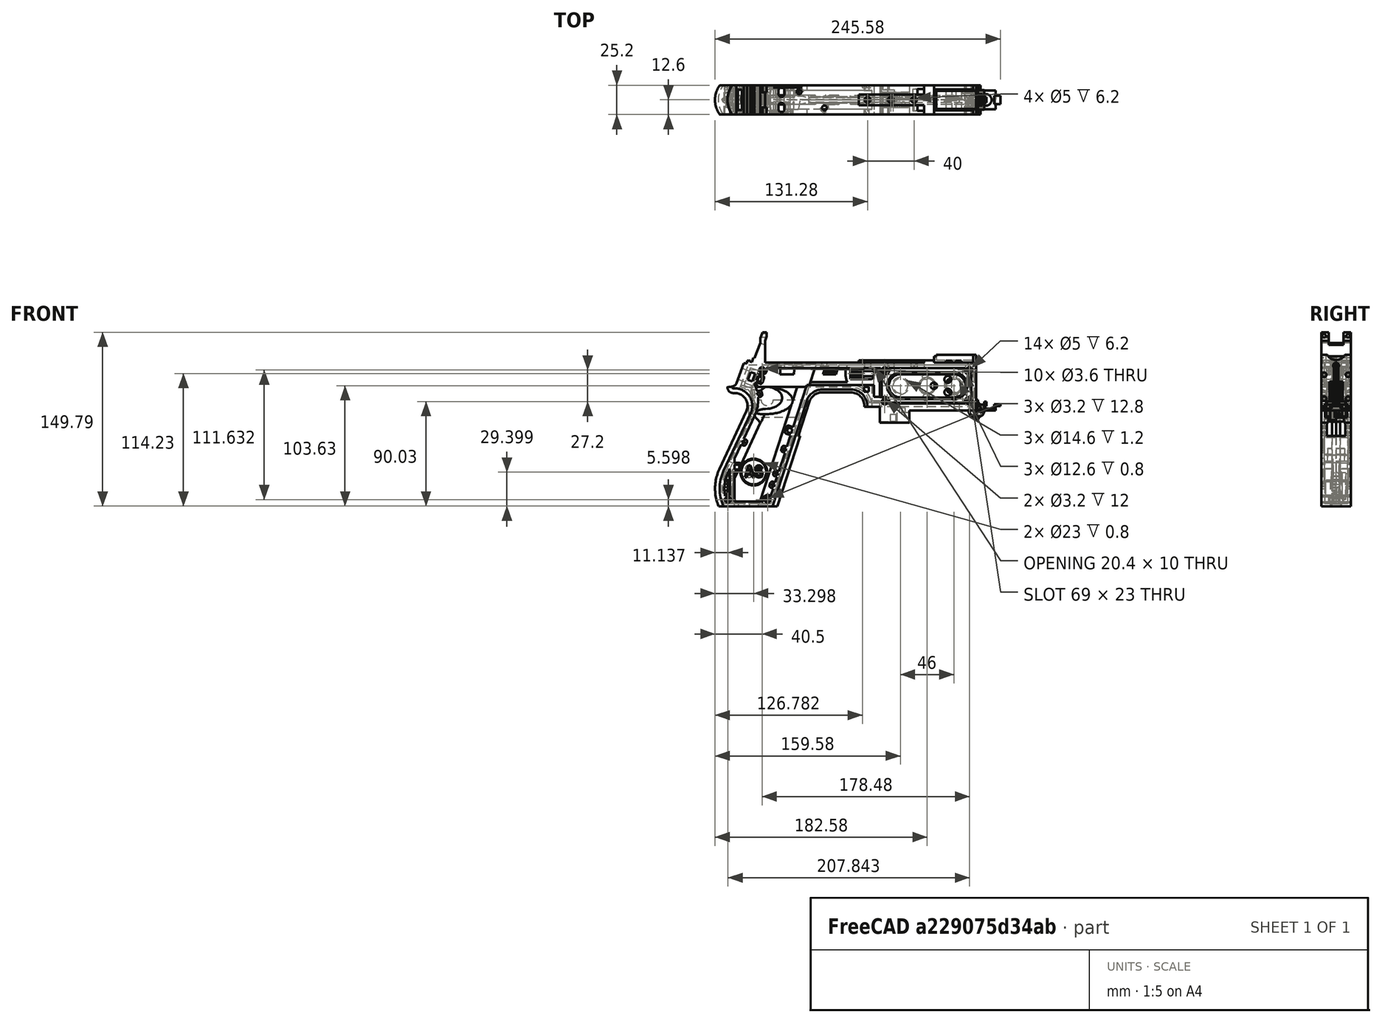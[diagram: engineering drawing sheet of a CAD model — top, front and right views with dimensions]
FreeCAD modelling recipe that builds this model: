
FCSTD DOCUMENT  (FreeCAD 1.0R39319 (Git))
Label: PICON-OF_ver_61
License: All rights reserved
LicenseURL: https://en.wikipedia.org/wiki/All_rights_reserved
objects: Sketcher::SketchObject×132, Part::Extrusion×66, Part::Cut×51, PartDesign::Pad×34, PartDesign::Pocket×21, PartDesign::Chamfer×15, PartDesign::Body×11, PartDesign::Fillet×6, Part::MultiFuse×5, Part::Part2DObjectPython×4, PartDesign::SubtractivePipe×4, PartDesign::SubtractiveLoft×4, PartDesign::Plane×3, PartDesign::SubShapeBinder×2, Part::Sweep×1, PartDesign::ShapeBinder×1, Mesh::Feature×1, PartDesign::Point×1, PartDesign::Groove×1
note: 664 computed .brp shape members not serialized (recipe doc carries the construction recipe); baked Part::Feature solids carry a one-line shape summary decoded from their .brp

FEATURE [Sketcher::SketchObject] Sketch  label="corpo principale"
  ArcFitTolerance = 1e-06
  AttacherType = Attacher::AttachEngine3D
  AttachmentSupport = -> [XZ_Plane]
  FullyConstrained = true
  MakeInternals = false
  MapMode = 5
  Placement = pos=(0,0,0) rot=(1,0,0;1.5708rad)
  sketch-geometry (65):
    g0: LineSegment StartX=0 StartY=0 StartZ=0 EndX=-57.2 EndY=0 EndZ=0
    g1: LineSegment StartX=-57.2 StartY=0 StartZ=0 EndX=-57.2 EndY=-10.4 EndZ=0
    g2: LineSegment StartX=-57.2 StartY=-10.4 StartZ=0 EndX=-82.8 EndY=-10.4 EndZ=0
    g3: LineSegment StartX=-82.8 StartY=-10.4 StartZ=0 EndX=-82.8 EndY=3.2 EndZ=0
    g4: LineSegment StartX=-82.8 StartY=3.2 StartZ=0 EndX=-93.6 EndY=3.2 EndZ=0
    g5: LineSegment StartX=-93.6 StartY=3.2 StartZ=0 EndX=-93.6 EndY=4 EndZ=0
    g6: LineSegment StartX=-107.6 StartY=18 StartZ=0 EndX=-132.428 EndY=18 EndZ=0
    g7: LineSegment StartX=-145.743 StartY=8.32624 StartZ=0 EndX=-175.232 EndY=-82.4316 EndZ=0
    g8: LineSegment StartX=-175.232 StartY=-82.4316 StartZ=0 EndX=-217.232 EndY=-82.4316 EndZ=0
    g9: LineSegment StartX=-217.232 StartY=-52.1862 StartZ=0 EndX=-193.988 EndY=-2.33927 EndZ=0
    g10: LineSegment StartX=-206.196 StartY=23.0857 StartZ=0 EndX=-199.861 EndY=40.4914 EndZ=0
    g11: LineSegment StartX=-199.861 StartY=40.4914 StartZ=0 EndX=-197.061 EndY=40.4914 EndZ=0
    g12: LineSegment StartX=-197.061 StartY=40.4914 StartZ=0 EndX=-197.061 EndY=42.8914 EndZ=0
    g13: LineSegment StartX=-197.061 StartY=42.8914 StartZ=0 EndX=-194.261 EndY=42.8914 EndZ=0
    g14: LineSegment StartX=-194.261 StartY=42.8914 StartZ=0 EndX=-194.535 EndY=42.1397 EndZ=0
    g15: LineSegment StartX=-194.535 StartY=42.1397 StartZ=0 EndX=-193.031 EndY=41.5924 EndZ=0
    g16: LineSegment StartX=-193.031 StartY=41.5924 StartZ=0 EndX=-191.663 EndY=45.3512 EndZ=0
    g17: LineSegment StartX=-191.663 StartY=45.3512 StartZ=0 EndX=-190.536 EndY=44.9408 EndZ=0
    g18: LineSegment StartX=-190.536 StartY=44.9408 StartZ=0 EndX=-185.747 EndY=58.0965 EndZ=0
    g19: LineSegment StartX=-185.747 StartY=58.0965 StartZ=0 EndX=-185.747 EndY=62.0965 EndZ=0
    g20: LineSegment StartX=-185.747 StartY=62.0965 StartZ=0 EndX=-183.832 EndY=67.3588 EndZ=0
    g21: LineSegment StartX=-183.832 StartY=67.3588 StartZ=0 EndX=-180.232 EndY=67.3588 EndZ=0
    g22: LineSegment StartX=-180.232 StartY=67.3588 StartZ=0 EndX=-180.232 EndY=63.7588 EndZ=0
    g23: LineSegment StartX=-180.232 StartY=63.7588 StartZ=0 EndX=-181.6 EndY=60 EndZ=0
    g24: LineSegment StartX=-181.6 StartY=60 StartZ=0 EndX=-181.6 EndY=41.2 EndZ=0
    g25: LineSegment StartX=-181.6 StartY=41.2 StartZ=0 EndX=-100.8 EndY=41.2 EndZ=0
    g26: LineSegment StartX=-36 StartY=43.2 StartZ=0 EndX=-36 EndY=41.2 EndZ=0
    g27: LineSegment StartX=0 StartY=48 StartZ=0 EndX=0 EndY=0 EndZ=0
    g28: LineSegment StartX=-209.901 StartY=19.85 StartZ=0 EndX=-209.901 EndY=20.1 EndZ=0
    g29: LineSegment StartX=-208.001 StartY=22 StartZ=0 EndX=-207.747 EndY=22 EndZ=0
    g30: LineSegment StartX=-207.583 StartY=19 StartZ=0 EndX=-209.051 EndY=19 EndZ=0
    g31: ArcOfCircle CenterX=-208.001 CenterY=20.1 CenterZ=0 NormalX=0 NormalY=0 NormalZ=1 AngleXU=0 Radius=1.9 StartAngle=1.5708 EndAngle=3.14159
    g32: GeomPoint [constr] X=-209.901 Y=22 Z=0
    g33: ArcOfCircle CenterX=-209.051 CenterY=19.85 CenterZ=0 NormalX=0 NormalY=0 NormalZ=1 AngleXU=0 Radius=0.85 StartAngle=3.14159 EndAngle=4.71239
    g34: GeomPoint [constr] X=-209.901 Y=19 Z=0
    g35: ArcOfCircle CenterX=-207.747 CenterY=23.65 CenterZ=0 NormalX=0 NormalY=0 NormalZ=1 AngleXU=0 Radius=1.65 StartAngle=4.71239 EndAngle=5.93412
    g36: GeomPoint [constr] X=-206.591 Y=22 Z=0
    g37: LineSegment StartX=-4 StartY=6 StartZ=0 EndX=-4 EndY=36.4 EndZ=0
    g38: LineSegment StartX=-4 StartY=36.4 StartZ=0 EndX=-185.2 EndY=36.4 EndZ=0
    g39: LineSegment StartX=-185.2 StartY=36.4 StartZ=0 EndX=-190.441 EndY=22 EndZ=0
    g40: LineSegment StartX=-214.575 StartY=-78.4316 StartZ=0 EndX=-178.142 EndY=-78.4316 EndZ=0
    g41: LineSegment StartX=-178.142 StartY=-78.4316 StartZ=0 EndX=-145.51 EndY=22 EndZ=0
    g42: LineSegment StartX=-145.51 StartY=22 StartZ=0 EndX=-87.91 EndY=22 EndZ=0
    g43: LineSegment StartX=-87.91 StartY=22 StartZ=0 EndX=-87.91 EndY=11.6 EndZ=0
    g44: LineSegment StartX=-87.91 StartY=11.6 StartZ=0 EndX=-80.11 EndY=11.6 EndZ=0
    g45: LineSegment StartX=-80.11 StartY=11.6 StartZ=0 EndX=-80.11 EndY=6 EndZ=0
    g46: LineSegment StartX=-80.11 StartY=6 StartZ=0 EndX=-4 EndY=6 EndZ=0
    g47: LineSegment StartX=-190.363 StartY=-4.02975 StartZ=0 EndX=-213.607 EndY=-53.8767 EndZ=0
    g48: ArcOfCircle CenterX=-132.428 CenterY=4 CenterZ=0 NormalX=0 NormalY=0 NormalZ=1 AngleXU=0 Radius=14 StartAngle=1.5708 EndAngle=2.82743
    g49: GeomPoint [constr] X=-142.6 Y=18 Z=0
    g50: ArcOfCircle CenterX=-107.6 CenterY=4 CenterZ=0 NormalX=0 NormalY=0 NormalZ=1 AngleXU=0 Radius=14 StartAngle=0 EndAngle=1.5708
    g51: GeomPoint [constr] X=-93.6 Y=18 Z=0
    g52: ArcOfCircle CenterX=-184.801 CenterY=-67.3089 CenterZ=0 NormalX=0 NormalY=0 NormalZ=1 AngleXU=0 Radius=35.7833 StartAngle=2.70526 EndAngle=3.57792
    g53: ArcOfCircle CenterX=-207.583 CenterY=4 CenterZ=0 NormalX=0 NormalY=0 NormalZ=1 AngleXU=0 Radius=15 StartAngle=5.84685 EndAngle=7.85398
    g54: LineSegment [constr] StartX=-213.607 StartY=-53.8767 StartZ=0 EndX=-217.232 EndY=-52.1862 EndZ=0
    g55: ArcOfCircle CenterX=-184.801 CenterY=-67.3089 CenterZ=0 NormalX=0 NormalY=0 NormalZ=1 AngleXU=0 Radius=31.7833 StartAngle=2.70526 EndAngle=3.49911
    g56: ArcOfCircle CenterX=-218.095 CenterY=8.90192 CenterZ=0 NormalX=0 NormalY=0 NormalZ=1 AngleXU=0 Radius=30.5989 StartAngle=5.84685 EndAngle=6.72553
    g57: LineSegment StartX=-44.6 StartY=43.2 StartZ=0 EndX=-36 EndY=43.2 EndZ=0
    g58: LineSegment StartX=-100.8 StartY=41.2 StartZ=0 EndX=-44.6 EndY=41.2 EndZ=0
    g59: LineSegment StartX=-44.6 StartY=41.2 StartZ=0 EndX=-44.6 EndY=43.2 EndZ=0
    g60: LineSegment StartX=-2.4 StartY=48 StartZ=0 EndX=0 EndY=48 EndZ=0
    g61: LineSegment StartX=-36 StartY=41.2 StartZ=0 EndX=-2.4 EndY=41.2 EndZ=0
    g62: LineSegment StartX=-2.4 StartY=41.2 StartZ=0 EndX=-2.4 EndY=48 EndZ=0
    g63: LineSegment [constr] StartX=-181.6 StartY=36.4 StartZ=0 EndX=-152.209 EndY=36.4 EndZ=0
    g64: LineSegment [constr] StartX=-181.6 StartY=36.4 StartZ=0 EndX=-130.41 EndY=36.4 EndZ=0
  constraints (183):
    c: Coincident(g-1,g0)
    c: PointOnObject(g0,g-1)
    c: Coincident(g0,g1)
    c: Vertical(g1)
    c: Coincident(g1,g2)
    c: Horizontal(g2)
    c: Coincident(g2,g3)
    c: Vertical(g3)
    c: Coincident(g3,g4)
    c: Coincident(g4,g5)
    c: Vertical(g5)
    c: Horizontal(g6)
    c: Coincident(g7,g8)
    c: Horizontal(g8)
    c: Coincident(g10,g11)
    c: Horizontal(g11)
    c: Coincident(g11,g12)
    c: Vertical(g12)
    c: Coincident(g12,g13)
    c: Horizontal(g13)
    c: Coincident(g13,g14)
    c: Coincident(g14,g15)
    c: Coincident(g15,g16)
    c: Coincident(g16,g17)
    c: Coincident(g17,g18)
    c: Coincident(g18,g19)
    c: Vertical(g19)
    c: Coincident(g19,g20)
    c: Coincident(g20,g21)
    c: Horizontal(g21)
    c: Coincident(g21,g22)
    c: Vertical(g22)
    c: Coincident(g22,g23)
    c: Coincident(g23,g24)
    c: Vertical(g24)
    c: Coincident(g24,g25)
    c: Horizontal(g25)
    c: Coincident(g57,g26)
    c: Vertical(g26)
    c: Coincident(g26,g61)
    c: PointOnObject(g60,g-2)
    c: Coincident(g60,g27)
    c: Coincident(g27,g0)
    c: DistanceY(g27,g27) = 48
    c: DistanceY(g1,g1) = 10.4
    c: DistanceX(g0,g0) = 57.2
    c: DistanceX(g2,g2) = 25.6
    c: Horizontal(g4)
    c: DistanceY(g3,g3) = 13.6
    c: DistanceX(g4,g4) = 10.8
    c: DistanceY(g5,g51) = 14.8
    c: DistanceX(g49,g51) = 49
    c: Distance(g7,g49) = 105.6
    c: DistanceX(g61,g60) = 36
    c: DistanceX(g25,g25) = 80.8
    c: DistanceY(g24,g24) = 18.8
    c: DistanceY(g22,g22) = 3.6
    c: Distance(g23) = 4
    c: Angle(g-1,g23) = 1.22173
    c: DistanceX(g21,g21) = 3.6
    c: Distance(g20) = 5.6
    c: Angle(g-1,g20) = 1.22173
    c: DistanceY(g19,g19) = 4
    c: Distance(g18) = 14
    c: Angle(g-1,g18) = 1.22173
    c: Distance(g17) = 1.2
    c: Distance(g16) = 4
    c: Angle(g16) = 1.22173
    c: Perpendicular(g18,g17)
    c: Distance(g15) = 1.6
    c: Perpendicular(g16,g15)
    c: Distance(g14) = 0.8
    c: DistanceX(g13,g13) = 2.8
    c: Perpendicular(g15,g14)
    c: DistanceY(g12,g12) = 2.4
    c: DistanceX(g11,g11) = 2.8
    c: Distance(g9) = 55
    c: Angle(g9,g-1) = 2.00713
    c: Horizontal(g29)
    c: Vertical(g28)
    c: Horizontal(g30)
    c: PointOnObject(g32,g29)
    c: PointOnObject(g32,g28)
    c: Tangent(g29,g31) = 1.5708
    c: Tangent(g28,g31) = 1.5708
    c: PointOnObject(g34,g28)
    c: PointOnObject(g34,g30)
    c: Tangent(g28,g33) = 1.5708
    c: Tangent(g30,g33) = 1.5708
    c: PointOnObject(g36,g29)
    c: PointOnObject(g36,g10)
    c: Tangent(g29,g35) = -1.5708
    c: Tangent(g10,g35) = -1.5708
    c: Angle(g-1,g10) = 1.22173
    c: Radius(g35) = 1.65
    c: Vertical(g37)
    c: Coincident(g37,g38)
    c: Horizontal(g38)
    c: Coincident(g38,g39)
    c: Horizontal(g40)
    c: Coincident(g40,g41)
    c: Coincident(g41,g42)
    c: Horizontal(g42)
    c: Coincident(g42,g43)
    c: Vertical(g43)
    c: Coincident(g43,g44)
    c: Horizontal(g44)
    c: Coincident(g44,g45)
    c: Vertical(g45)
    c: Coincident(g45,g46)
    c: Coincident(g46,g37)
    c: Horizontal(g46)
    c: DistanceY(g0,g37) = 6
    c: DistanceX(g37,g0) = 4
    c: DistanceY(g37,g25) = 4.8
    c: DistanceX(g38,g38) = 181.2
    c: DistanceX(g42,g42) = 57.6
    c: DistanceY(g49,g41) = 4
    c: DistanceX(g41,g49) = 2.91
    c: DistanceY(g43,g43) = 10.4
    c: DistanceX(g44,g44) = 7.8
    c: DistanceY(g7,g40) = 4
    c: Distance(g47) = 55
    c: Angle(g-1,g39) = 1.22173
    c: PointOnObject(g49,g7)
    c: PointOnObject(g49,g6)
    c: Tangent(g7,g48) = -1.5708
    c: Tangent(g6,g48) = -1.5708
    c: PointOnObject(g51,g5)
    c: PointOnObject(g51,g6)
    c: Tangent(g5,g50) = -1.5708
    c: Tangent(g6,g50) = -1.5708
    c: Radius(g50) = 14
    c: Radius(g48) = 14
    c: DistanceX(g8,g8) = 42
    c: Angle(g7,g-1) = 1.88496
    c: Parallel(g41,g7)
    c: Parallel(g47,g9)
    c: Coincident(g52,g8)
    c: Tangent(g52,g9) = 1.5708
    c: DistanceX(g9,g8) = 0
    c: Tangent(g53,g9) = -1.5708
    c: Tangent(g53,g30) = -1.5708
    c: Diameter(g53) = 30
    c: DistanceY(g53,g0) = -4
    c: Coincident(g54,g47)
    c: Distance(g54) = 4
    c: Coincident(g54,g9)
    c: Coincident(g55,g40)
    c: Tangent(g55,g47) = -1.5708
    c: Coincident(g52,g55)
    c: Coincident(g56,g39)
    c: Tangent(g56,g47) = 1.5708
    c: Horizontal(g57)
    c: DistanceX(g57,g57) = 8.6
    c: Coincident(g58,g25)
    c: Horizontal(g58)
    c: Coincident(g59,g58)
    c: Vertical(g59)
    c: DistanceY(g58,g57) = 2
    c: DistanceX(g58,g58) = 56.2
    c: Coincident(g59,g57)
    c: DistanceY(g41,g36) = 0
    c: DistanceY(g36,g39) = 0
    c: DistanceY(g28,g28) = 0.25
    c: DistanceX(g30,g36) = 2.46
    c: DistanceX(g28,g29) = 1.9
    c: Coincident(g62,g60)
    c: Horizontal(g60)
    c: DistanceX(g62,g27) = 2.4
    c: Coincident(g61,g62)
    c: DistanceY(g26,g26) = 2
    c: Vertical(g62)
    c: DistanceY(g61,g60) = 6.8
    c: Horizontal(g61)
    c: Distance(g63) = 29.391
    c: PointOnObject(g63,g38)
    c: PointOnObject(g63,g38)
    c: Distance(g64) = 51.19
    c: PointOnObject(g64,g38)
    c: PointOnObject(g64,g38)
    c: DistanceX(g24,g63) = 0
    c: DistanceX(g24,g64) = 0
FEATURE [Part::Extrusion] Extrude  label="Extrude corpo principale"
  Base = -> Sketch
  Dir = (0,-1,2e-16)
  DirMode = 2
  FaceMakerClass = Part::FaceMakerBullseye
  FaceMakerMode = 3
  LengthFwd = 25.2
  LengthRev = 12.6
  Solid = true
  Symmetric = true
FEATURE [Sketcher::SketchObject] Sketch002  label="scavo grilletto"
  ArcFitTolerance = 1e-06
  AttachmentSupport = -> [XZ_Plane]
  ExternalGeometry = -> [Sketch]
  FullyConstrained = true
  MakeInternals = false
  MapMode = 5
  Placement = pos=(0,0,0) rot=(1,0,0;1.5708rad)
  sketch-geometry (4):
    g0: LineSegment StartX=-89.51 StartY=22 StartZ=0 EndX=-152.71 EndY=22 EndZ=0
    g1: LineSegment StartX=-152.71 StartY=22 StartZ=0 EndX=-167.006 EndY=-22 EndZ=0
    g2: LineSegment StartX=-167.006 StartY=-22 StartZ=0 EndX=-89.51 EndY=-22 EndZ=0
    g3: LineSegment StartX=-89.51 StartY=-22 StartZ=0 EndX=-89.51 EndY=22 EndZ=0
  constraints (12):
    c: Horizontal(g0)
    c: Coincident(g0,g1)
    c: Coincident(g1,g2)
    c: Horizontal(g2)
    c: Coincident(g2,g3)
    c: Coincident(g3,g0)
    c: Vertical(g3)
    c: Angle(g1,g0) = 1.88496
    c: DistanceY(g3,g3) = 44
    c: DistanceX(g0,g0) = 63.2
    c: DistanceX(g0,g-3) = 1.6
    c: DistanceY(g-3,g0) = 0
FEATURE [Sketcher::SketchObject] Sketch004  label="traiettoria arrotondamento impugnatura anteriore"
  ArcFitTolerance = 1e-06
  AttachmentSupport = -> [XZ_Plane]
  ExternalGeometry = -> [Sketch]
  FullyConstrained = true
  MakeInternals = false
  MapMode = 5
  Placement = pos=(0,0,0) rot=(1,0,0;1.5708rad)
  sketch-geometry (13):
    g0: LineSegment StartX=-175.232 StartY=-82.4316 StartZ=0 EndX=-145.743 EndY=8.32624 EndZ=0
    g1: LineSegment StartX=-93.6 StartY=3.2 StartZ=0 EndX=-93.6 EndY=4 EndZ=0
    g2: LineSegment StartX=-132.428 StartY=18 StartZ=0 EndX=-107.6 EndY=18 EndZ=0
    g3: ArcOfCircle CenterX=-132.428 CenterY=4 CenterZ=0 NormalX=0 NormalY=0 NormalZ=1 AngleXU=0 Radius=14 StartAngle=1.5708 EndAngle=2.82743
    g4: ArcOfCircle CenterX=-107.6 CenterY=4 CenterZ=0 NormalX=0 NormalY=0 NormalZ=1 AngleXU=0 Radius=14 StartAngle=0 EndAngle=1.5708
    g5: LineSegment StartX=-175.232 StartY=-82.4316 StartZ=0 EndX=-217.232 EndY=-82.4316 EndZ=0
    g6: LineSegment StartX=-217.232 StartY=-52.1862 StartZ=0 EndX=-193.988 EndY=-2.33927 EndZ=0
    g7: LineSegment StartX=-209.051 StartY=19 StartZ=0 EndX=-207.583 EndY=19 EndZ=0
    g8: LineSegment StartX=-209.901 StartY=20.1 StartZ=0 EndX=-209.901 EndY=19.85 EndZ=0
    g9: ArcOfCircle CenterX=-184.801 CenterY=-67.3089 CenterZ=0 NormalX=0 NormalY=0 NormalZ=1 AngleXU=0 Radius=35.7833 StartAngle=2.70526 EndAngle=3.57792
    g10: ArcOfCircle CenterX=-207.583 CenterY=4 CenterZ=0 NormalX=0 NormalY=0 NormalZ=1 AngleXU=0 Radius=15 StartAngle=5.84685 EndAngle=7.85398
    g11: ArcOfCircle CenterX=-209.051 CenterY=19.85 CenterZ=0 NormalX=0 NormalY=0 NormalZ=1 AngleXU=0 Radius=0.85 StartAngle=3.14159 EndAngle=4.71239
    g12: ArcOfCircle CenterX=-208.001 CenterY=20.1 CenterZ=0 NormalX=0 NormalY=0 NormalZ=1 AngleXU=0 Radius=1.9 StartAngle=1.5708 EndAngle=3.14159
  constraints (26):
    c: Coincident(g0,g-3)
    c: Coincident(g0,g-6)
    c: Coincident(g1,g-8)
    c: Coincident(g1,g-7)
    c: Coincident(g2,g-5)
    c: Coincident(g2,g-4)
    c: Coincident(g3,g2)
    c: Tangent(g3,g0) = 1.5708
    c: Coincident(g4,g1)
    c: Tangent(g4,g2) = 1.5708
    c: Coincident(g5,g0)
    c: Coincident(g5,g-9)
    c: Coincident(g6,g-12)
    c: Coincident(g6,g-11)
    c: Coincident(g7,g-15)
    c: Coincident(g7,g-14)
    c: Coincident(g8,g-16)
    c: Coincident(g8,g-17)
    c: Tangent(g9,g6) = 1.5708
    c: Coincident(g9,g5)
    c: Coincident(g10,g7)
    c: Tangent(g10,g6) = -1.5708
    c: Tangent(g11,g7) = -1.5708
    c: Coincident(g11,g8)
    c: Tangent(g12,g8) = -1.5708
    c: Coincident(g12,g-17)
FEATURE [PartDesign::Plane] DatumPlane  label="Piano per disegno arrotondamento impugnatura"
  AttachmentSupport = -> [Sketch]
  Length = 73.6581
  MapMode = 7
  Placement = pos=(-145.743,1.8e-15,8.32624) rot=(0.154555,0.154555,0.97582;1.59527rad)
  ResizeMode = 0
  Width = 303.511
FEATURE [Sketcher::SketchObject] Sketch005  label="forma arrotondamento impugnatura anteriore"
  ArcFitTolerance = 1e-06
  AttachmentSupport = -> [DatumPlane]
  FullyConstrained = true
  MakeInternals = false
  MapMode = 5
  Placement = pos=(-145.743,1.8e-15,8.32624) rot=(0.154555,0.154555,0.97582;1.59527rad)
  sketch-geometry (5):
    g0: GeomPoint [constr] X=0 Y=-4 Z=0
    g1: GeomPoint [constr] X=-12.6 Y=7.1e-15 Z=0
    g2: GeomPoint [constr] X=12.6 Y=4.97e-14 Z=0
    g3: LineSegment StartX=-12.6 StartY=7.1e-15 StartZ=0 EndX=12.6 EndY=4.97e-14 EndZ=0
    g4: ArcOfCircle CenterX=-3.88e-14 CenterY=17.845 CenterZ=0 NormalX=0 NormalY=0 NormalZ=1 AngleXU=0 Radius=21.845 StartAngle=4.09759 EndAngle=5.32718
  constraints (11):
    c: DistanceY(g0,g-1) = 4
    c: DistanceX(g-1,g0) = 0
    c: DistanceX(g1,g-1) = 12.6
    c: DistanceX(g-1,g2) = 12.6
    c: DistanceY(g-1,g2) = 0
    c: DistanceY(g-1,g1) = 0
    c: Coincident(g3,g1)
    c: Coincident(g3,g2)
    c: Coincident(g4,g1)
    c: Coincident(g4,g2)
    c: PointOnObject(g0,g4)
FEATURE [Part::Sweep] Sweep  label="Sweep impugnatura"
  Frenet = true
  Sections = -> [Sketch005]
  Solid = true
  Spine = -> Sketch [Edge32,Edge33,Edge34,Edge35,Edge36,Edge37,Edge38,Edge39,Edge40,Edge41,Edge42,Edge43,Edge44]
  Transition = 1
FEATURE [Sketcher::SketchObject] Sketch008  label="buchi e pulizie varie"
  ArcFitTolerance = 1e-06
  AttachmentSupport = -> [XZ_Plane]
  ExternalGeometry = -> [Sketch]
  FullyConstrained = true
  MakeInternals = false
  MapMode = 5
  Placement = pos=(0,0,0) rot=(1,0,0;1.5708rad)
  sketch-geometry (26):
    g0: LineSegment StartX=-96.278 StartY=20.155 StartZ=0 EndX=-92.278 EndY=20.155 EndZ=0
    g1: LineSegment StartX=-92.278 StartY=20.155 StartZ=0 EndX=-92.278 EndY=16.155 EndZ=0
    g2: LineSegment StartX=-92.278 StartY=16.155 StartZ=0 EndX=-96.278 EndY=16.155 EndZ=0
    g3: LineSegment StartX=-96.278 StartY=16.155 StartZ=0 EndX=-96.278 EndY=20.155 EndZ=0
    g4: LineSegment StartX=-222.232 StartY=-82.4316 StartZ=0 EndX=-170.232 EndY=-82.4316 EndZ=0
    g5: LineSegment StartX=-170.232 StartY=-82.4316 StartZ=0 EndX=-170.232 EndY=-86.4316 EndZ=0
    g6: LineSegment StartX=-170.232 StartY=-86.4316 StartZ=0 EndX=-222.232 EndY=-86.4316 EndZ=0
    g7: LineSegment StartX=-222.232 StartY=-86.4316 StartZ=0 EndX=-222.232 EndY=-82.4316 EndZ=0
    g8: LineSegment StartX=-213.901 StartY=20.1 StartZ=0 EndX=-213.901 EndY=26 EndZ=0
    g9: LineSegment StartX=-213.901 StartY=26 StartZ=0 EndX=-206.196 EndY=26 EndZ=0
    g10: LineSegment StartX=-17.4 StartY=42.8 StartZ=0 EndX=-12.4 EndY=42.8 EndZ=0
    g11: LineSegment StartX=-12.4 StartY=42.8 StartZ=0 EndX=-12.4 EndY=41.2 EndZ=0
    g12: LineSegment StartX=-12.4 StartY=41.2 StartZ=0 EndX=-17.4 EndY=41.2 EndZ=0
    g13: LineSegment StartX=-17.4 StartY=41.2 StartZ=0 EndX=-17.4 EndY=42.8 EndZ=0
    g14: LineSegment StartX=-25.9 StartY=42.8 StartZ=0 EndX=-20.9 EndY=42.8 EndZ=0
    g15: LineSegment StartX=-20.9 StartY=42.8 StartZ=0 EndX=-20.9 EndY=41.2 EndZ=0
    g16: LineSegment StartX=-20.9 StartY=41.2 StartZ=0 EndX=-25.9 EndY=41.2 EndZ=0
    g17: LineSegment StartX=-25.9 StartY=41.2 StartZ=0 EndX=-25.9 EndY=42.8 EndZ=0
    g18: GeomPoint [constr] X=-206.196 Y=23.0857 Z=0
    g19: GeomPoint [constr] X=-213.901 Y=20.1 Z=0
    g20: BSplineCurve PolesCount=4 KnotsCount=2 Degree=3 IsPeriodic=0
    g21-g24: Circle [constr] x4 (B-spline internal-alignment scaffolding for g20; pole/knot coordinates omitted)
    g25: LineSegment StartX=-206.196 StartY=26 StartZ=0 EndX=-206.196 EndY=23.0857 EndZ=0
  constraints (73):
    c: Horizontal(g0)
    c: Coincident(g1,g0)
    c: Vertical(g1)
    c: Coincident(g2,g1)
    c: Horizontal(g2)
    c: Coincident(g3,g2)
    c: Coincident(g3,g0)
    c: Vertical(g3)
    c: DistanceX(g0,g-4) = 4.368
    c: DistanceY(g0,g-4) = 1.845
    c: DistanceY(g1,g1) = 4
    c: DistanceX(g2,g2) = 4
    c: Horizontal(g4)
    c: Coincident(g5,g4)
    c: Vertical(g5)
    c: Coincident(g6,g5)
    c: Horizontal(g6)
    c: Coincident(g7,g6)
    c: Coincident(g7,g4)
    c: Vertical(g7)
    c: DistanceY(g7,g7) = 4
    c: DistanceX(g4,g-5) = 5
    c: DistanceX(g-5,g4) = 5
    c: DistanceY(g4,g-5) = 0
    c: Coincident(g9,g8)
    c: Parallel(g9,g-6)
    c: DistanceX(g8,g-8) = 4
    c: Horizontal(g10)
    c: Coincident(g11,g10)
    c: Vertical(g11)
    c: Coincident(g12,g11)
    c: Horizontal(g12)
    c: Coincident(g13,g12)
    c: Coincident(g13,g10)
    c: Vertical(g13)
    c: Horizontal(g14)
    c: Coincident(g15,g14)
    c: Vertical(g15)
    c: Coincident(g16,g15)
    c: Horizontal(g16)
    c: Coincident(g17,g16)
    c: Coincident(g17,g14)
    c: Vertical(g17)
    c: DistanceY(g11,g10) = 1.6
    c: DistanceX(g10,g10) = 5
    c: DistanceY(g15,g14) = 1.6
    c: DistanceX(g14,g14) = 5
    c: DistanceX(g15,g12) = 3.5
    c: DistanceX(g11,g-9) = 10
    c: DistanceY(g-9,g11) = 0
    c: DistanceY(g-9,g15) = 0
    c: Perpendicular(g8,g9)
    c: DistanceY(g-7,g9) = 4
    c: DistanceY(g8,g-8) = 0
    c: InternalAlignment(g18,g20)
    c: InternalAlignment(g19,g20)
    c: InternalAlignment(g21,g20)
    c: Weight(g21) = 1
    c: InternalAlignment(g22,g20)
    c: Equal(g22,g21)
    c: InternalAlignment(g23,g20)
    c: Equal(g23,g21)
    c: InternalAlignment(g24,g20)
    c: Equal(g24,g21)
    c: Coincident(g18,g-12)
    c: Coincident(g19,g8)
    c: Coincident(g25,g9)
    c: Coincident(g25,g20)
    c: Vertical(g25)
    c: DistanceY(g20,g23) = 0
    c: DistanceY(g22,g18) = 2.26
    c: DistanceX(g22,g18) = 0.93
    c: DistanceX(g20,g23) = 2.9
FEATURE [Part::Extrusion] Extrude004  label="Extrude Buchi e pulizie varie"
  Base = -> Sketch008
  Dir = (0,-1,2e-16)
  DirMode = 2
  FaceMakerClass = Part::FaceMakerBullseye
  FaceMakerMode = 3
  LengthFwd = 25.2
  LengthRev = 0
  Solid = true
  Symmetric = true
FEATURE [Sketcher::SketchObject] Sketch009  label="rinforzi"
  ArcFitTolerance = 1e-06
  AttachmentSupport = -> [XZ_Plane]
  ExternalGeometry = -> [Sketch]
  FullyConstrained = true
  MakeInternals = false
  MapMode = 5
  Placement = pos=(0,0,0) rot=(1,0,0;1.5708rad)
  sketch-geometry (9):
    g0: LineSegment StartX=-87.91 StartY=22 StartZ=0 EndX=-87.91 EndY=36.4 EndZ=0
    g1: LineSegment StartX=-87.91 StartY=36.4 StartZ=0 EndX=-97.91 EndY=36.4 EndZ=0
    g2: LineSegment StartX=-97.91 StartY=36.4 StartZ=0 EndX=-97.91 EndY=22 EndZ=0
    g3: LineSegment StartX=-97.91 StartY=22 StartZ=0 EndX=-87.91 EndY=22 EndZ=0
    g4: LineSegment StartX=-149.713 StartY=9.06563 StartZ=0 EndX=-154.586 EndY=-5.93437 EndZ=0
    g5: LineSegment StartX=-154.586 StartY=-5.93437 StartZ=0 EndX=-191.863 EndY=-5.93437 EndZ=0
    g6: LineSegment StartX=-191.863 StartY=-5.93437 StartZ=0 EndX=-191.863 EndY=9.06563 EndZ=0
    g7: LineSegment StartX=-191.863 StartY=9.06563 StartZ=0 EndX=-149.713 EndY=9.06563 EndZ=0
    g8: LineSegment [constr] StartX=-145.51 StartY=22 StartZ=0 EndX=-149.713 EndY=9.06563 EndZ=0
  constraints (25):
    c: Vertical(g0)
    c: Coincident(g1,g0)
    c: Horizontal(g1)
    c: Coincident(g2,g1)
    c: Vertical(g2)
    c: Coincident(g3,g2)
    c: Coincident(g3,g0)
    c: Horizontal(g3)
    c: Coincident(g0,g-4)
    c: DistanceX(g3,g3) = 10
    c: DistanceY(g0,g-3) = 0
    c: Coincident(g5,g4)
    c: Horizontal(g5)
    c: Coincident(g6,g5)
    c: Vertical(g6)
    c: Coincident(g7,g6)
    c: Coincident(g7,g4)
    c: Horizontal(g7)
    c: Distance(g8) = 13.6
    c: Parallel(g-6,g8)
    c: Coincident(g-6,g8)
    c: Parallel(g4,g-6)
    c: DistanceY(g4,g4) = 15
    c: Coincident(g4,g8)
    c: DistanceX(g-5,g5) = -1.5
FEATURE [Part::Extrusion] Extrude001  label="Extrude scavo grilletto"
  Base = -> Sketch002
  Dir = (0,-1,2e-16)
  DirMode = 2
  FaceMakerClass = Part::FaceMakerBullseye
  FaceMakerMode = 3
  LengthFwd = 16
  LengthRev = 0
  Solid = true
  Symmetric = true
FEATURE [Part::Extrusion] Extrude005  label="Extrude Rinforzi"
  Base = -> Sketch009
  Dir = (0,-1,2e-16)
  DirMode = 2
  FaceMakerClass = Part::FaceMakerBullseye
  FaceMakerMode = 3
  LengthFwd = 2
  LengthRev = 0
  Placement = pos=(0,12.6,0) rot=(0,0,1;0rad)
  Solid = true
  Symmetric = false
FEATURE [PartDesign::ShapeBinder] CopyCut
  TraceSupport = false
FEATURE [PartDesign::Plane] DatumPlane001
  AttachmentSupport = -> [CopyCut]
  Length = 283.944
  MapMode = 5
  Placement = pos=(0,12.6,0) rot=(0,0.707107,0.707107;3.14159rad)
  ResizeMode = 0
  Width = 188.15
FEATURE [Sketcher::SketchObject] Sketch010  label="buco neopixel"
  ArcFitTolerance = 1e-06
  AttachmentSupport = -> [XZ_Plane]
  ExternalGeometry = -> [Sketch]
  FullyConstrained = true
  MakeInternals = false
  MapMode = 5
  Placement = pos=(0,0,0) rot=(1,0,0;1.5708rad)
  sketch-geometry (5):
    g0: LineSegment [constr] StartX=-199.861 StartY=40.4914 StartZ=0 EndX=-201.368 EndY=36.3521 EndZ=0
    g1: LineSegment StartX=-201.368 StartY=36.3521 StartZ=0 EndX=-204.932 EndY=26.5605 EndZ=0
    g2: LineSegment StartX=-201.368 StartY=36.3521 StartZ=0 EndX=-180.2 EndY=28.6477 EndZ=0
    g3: LineSegment StartX=-180.2 StartY=28.6477 StartZ=0 EndX=-183.764 EndY=18.8561 EndZ=0
    g4: LineSegment StartX=-183.764 StartY=18.8561 StartZ=0 EndX=-204.932 EndY=26.5605 EndZ=0
  constraints (14):
    c: Parallel(g0,g-3)
    c: Distance(g0) = 4.405
    c: Coincident(g0,g-3)
    c: Coincident(g2,g1)
    c: Coincident(g3,g2)
    c: Coincident(g4,g3)
    c: Coincident(g4,g1)
    c: Parallel(g1,g-3)
    c: Distance(g1) = 10.42
    c: Coincident(g1,g0)
    c: Parallel(g2,g4)
    c: Perpendicular(g1,g2)
    c: DistanceX(g-4,g2) = 5
    c: Parallel(g3,g1)
FEATURE [Part::Extrusion] Extrude006  label="Extrude buco neopixel"
  Base = -> Sketch010
  Dir = (0,-1,2e-16)
  DirMode = 2
  FaceMakerClass = Part::FaceMakerBullseye
  FaceMakerMode = 3
  LengthFwd = 17.2
  LengthRev = 0
  Solid = true
  Symmetric = true
FEATURE [Sketcher::SketchObject] Sketch011  label="fermo grilletto"
  ArcFitTolerance = 1e-06
  AttachmentSupport = -> [XZ_Plane]
  ExternalGeometry = -> [Sketch]
  FullyConstrained = true
  MakeInternals = false
  MapMode = 5
  Placement = pos=(0,0,0) rot=(1,0,0;1.5708rad)
  sketch-geometry (18):
    g0: LineSegment [constr] StartX=-145.51 StartY=22 StartZ=0 EndX=-157.347 EndY=-14.4293 EndZ=0
    g1: LineSegment [constr] StartX=-157.347 StartY=-14.4293 StartZ=0 EndX=-157.841 EndY=-15.951 EndZ=0
    g2: LineSegment StartX=-161.151 StartY=-13.1932 StartZ=0 EndX=-155.825 EndY=-14.9237 EndZ=0
    g3: LineSegment StartX=-163.167 StartY=-14.2205 StartZ=0 EndX=-164.403 EndY=-18.0247 EndZ=0
    g4: LineSegment StartX=-163.376 StartY=-20.0408 StartZ=0 EndX=-158.05 EndY=-21.7713 EndZ=0
    g5: LineSegment StartX=-158.05 StartY=-21.7713 StartZ=0 EndX=-155.825 EndY=-14.9237 EndZ=0
    g6: LineSegment StartX=-161.645 StartY=-14.7149 StartZ=0 EndX=-157.841 EndY=-15.951 EndZ=0
    g7: LineSegment StartX=-157.841 StartY=-15.951 StartZ=0 EndX=-159.077 EndY=-19.7552 EndZ=0
    g8: LineSegment StartX=-159.077 StartY=-19.7552 StartZ=0 EndX=-162.881 EndY=-18.5191 EndZ=0
    g9: LineSegment StartX=-162.881 StartY=-18.5191 StartZ=0 EndX=-161.645 EndY=-14.7149 EndZ=0
    g10: LineSegment [constr] StartX=-161.645 StartY=-14.7149 StartZ=0 EndX=-161.151 EndY=-13.1932 EndZ=0
    g11: LineSegment [constr] StartX=-159.077 StartY=-19.7552 StartZ=0 EndX=-157.555 EndY=-20.2496 EndZ=0
    g12: LineSegment [constr] StartX=-159.077 StartY=-19.7552 StartZ=0 EndX=-159.572 EndY=-21.2769 EndZ=0
    g13: LineSegment [constr] StartX=-161.645 StartY=-14.7149 StartZ=0 EndX=-163.167 EndY=-14.2205 EndZ=0
    g14: ArcOfCircle CenterX=-161.645 CenterY=-14.7149 CenterZ=0 NormalX=0 NormalY=0 NormalZ=1 AngleXU=0 Radius=1.6 StartAngle=1.25664 EndAngle=2.82743
    g15: GeomPoint [constr] X=-162.673 Y=-12.6988 Z=0
    g16: ArcOfCircle CenterX=-162.881 CenterY=-18.5191 CenterZ=0 NormalX=0 NormalY=0 NormalZ=1 AngleXU=0 Radius=1.6 StartAngle=2.82743 EndAngle=4.39823
    g17: GeomPoint [constr] X=-164.897 Y=-19.5464 Z=0
  constraints (48):
    c: Parallel(g0,g-3)
    c: Distance(g0) = 38.304
    c: Coincident(g0,g-3)
    c: Parallel(g1,g-3)
    c: Distance(g1) = 1.6
    c: Coincident(g1,g0)
    c: Coincident(g5,g4)
    c: Coincident(g5,g2)
    c: Coincident(g7,g6)
    c: Coincident(g8,g7)
    c: Coincident(g9,g8)
    c: Coincident(g9,g6)
    c: Parallel(g7,g-3)
    c: Parallel(g9,g7)
    c: Perpendicular(g6,g7)
    c: Parallel(g6,g8)
    c: Distance(g6) = 4
    c: Distance(g9) = 4
    c: Parallel(g5,g7)
    c: Parallel(g9,g3)
    c: Parallel(g2,g6)
    c: Parallel(g4,g8)
    c: Parallel(g13,g6)
    c: Parallel(g10,g9)
    c: Parallel(g11,g8)
    c: Parallel(g12,g7)
    c: Distance(g10) = 1.6
    c: Distance(g13) = 1.6
    c: Distance(g12) = 1.6
    c: Distance(g11) = 1.6
    c: Coincident(g10,g6)
    c: Coincident(g13,g6)
    c: Coincident(g12,g7)
    c: Coincident(g11,g7)
    c: Distance(g10,g15) = 1.6
    c: Distance(g15,g13) = 1.6
    c: Distance(g4,g12) = 1.6
    c: Distance(g4,g11) = 1.6
    c: PointOnObject(g15,g2)
    c: Tangent(g3,g14) = -1.5708
    c: Tangent(g2,g14) = 1.5708
    c: PointOnObject(g17,g4)
    c: PointOnObject(g17,g3)
    c: Tangent(g4,g16) = -1.5708
    c: Tangent(g3,g16) = -1.5708
    c: Equal(g16,g14)
    c: Coincident(g16,g8)
    c: Coincident(g6,g1)
FEATURE [Part::Extrusion] Extrude007  label="Extrude fermo grilletto"
  Base = -> Sketch011
  Dir = (0,-1,2e-16)
  DirMode = 2
  FaceMakerClass = Part::FaceMakerBullseye
  FaceMakerMode = 3
  LengthFwd = 25.2
  LengthRev = 0
  Solid = true
  Symmetric = true
FEATURE [Sketcher::SketchObject] Sketch012  label="buco oled"
  ArcFitTolerance = 1e-06
  AttachmentSupport = -> [XZ_Plane]
  ExternalGeometry = -> [Sketch]
  FullyConstrained = true
  MakeInternals = false
  MapMode = 5
  Placement = pos=(0,0,0) rot=(1,0,0;1.5708rad)
  sketch-geometry (4):
    g0: LineSegment StartX=-185.747 StartY=58.0965 StartZ=0 EndX=-180.232 EndY=56.0891 EndZ=0
    g1: LineSegment StartX=-185.747 StartY=58.0965 StartZ=0 EndX=-185.747 EndY=67.3588 EndZ=0
    g2: LineSegment StartX=-185.747 StartY=67.3588 StartZ=0 EndX=-180.232 EndY=67.3588 EndZ=0
    g3: LineSegment StartX=-180.232 StartY=67.3588 StartZ=0 EndX=-180.232 EndY=56.0891 EndZ=0
  constraints (10):
    c: Coincident(g1,g0)
    c: Coincident(g2,g1)
    c: Coincident(g3,g2)
    c: Coincident(g3,g0)
    c: Parallel(g1,g-5)
    c: Perpendicular(g-3,g0)
    c: Parallel(g2,g-6)
    c: Parallel(g3,g-4)
    c: Coincident(g0,g-5)
    c: Coincident(g2,g-6)
FEATURE [Part::Extrusion] Extrude008  label="Extrude buco oled"
  Base = -> Sketch012
  Dir = (0,-1,2e-16)
  DirMode = 2
  FaceMakerClass = Part::FaceMakerBullseye
  FaceMakerMode = 3
  LengthFwd = 12.8
  LengthRev = 0
  Solid = true
  Symmetric = true
FEATURE [Sketcher::SketchObject] Sketch013  label="buco pompa"
  ArcFitTolerance = 1e-06
  AttachmentSupport = -> [XZ_Plane]
  ExternalGeometry = -> [Sketch]
  FullyConstrained = true
  MakeInternals = false
  MapMode = 5
  Placement = pos=(0,0,0) rot=(1,0,0;1.5708rad)
  sketch-geometry (8):
    g0: LineSegment StartX=-82.8 StartY=-10.4 StartZ=0 EndX=-82.8 EndY=-9.6 EndZ=0
    g1: LineSegment StartX=-82.8 StartY=-9.6 StartZ=0 EndX=-67.9 EndY=-9.6 EndZ=0
    g2: LineSegment StartX=-67.9 StartY=-9.6 StartZ=0 EndX=-67.9 EndY=6 EndZ=0
    g3: LineSegment StartX=-67.9 StartY=6 StartZ=0 EndX=-65.9 EndY=6 EndZ=0
    g4: LineSegment StartX=-65.9 StartY=6 StartZ=0 EndX=-65.9 EndY=-1.7 EndZ=0
    g5: LineSegment StartX=-65.9 StartY=-1.7 StartZ=0 EndX=-57.2 EndY=-1.7 EndZ=0
    g6: LineSegment StartX=-57.2 StartY=-1.7 StartZ=0 EndX=-57.2 EndY=-10.4 EndZ=0
    g7: LineSegment StartX=-57.2 StartY=-10.4 StartZ=0 EndX=-82.8 EndY=-10.4 EndZ=0
  constraints (22):
    c: Vertical(g0)
    c: Coincident(g1,g0)
    c: Horizontal(g1)
    c: Coincident(g2,g1)
    c: Vertical(g2)
    c: Coincident(g3,g2)
    c: Horizontal(g3)
    c: Coincident(g4,g3)
    c: Vertical(g4)
    c: Coincident(g5,g4)
    c: Horizontal(g5)
    c: Coincident(g6,g5)
    c: Vertical(g6)
    c: Coincident(g7,g6)
    c: Coincident(g7,g0)
    c: DistanceY(g0,g0) = 0.8
    c: DistanceY(g6,g6) = 8.7
    c: DistanceX(g1,g1) = 14.9
    c: DistanceX(g3,g3) = 2
    c: Coincident(g0,g-4)
    c: DistanceY(g2,g-6) = 0
    c: Coincident(g6,g-5)
FEATURE [Part::Extrusion] Extrude009  label="Extrude buco pompa"
  Base = -> Sketch013
  Dir = (0,-1,2e-16)
  DirMode = 2
  FaceMakerClass = Part::FaceMakerBullseye
  FaceMakerMode = 3
  LengthFwd = 13.2
  LengthRev = 0
  Solid = true
  Symmetric = true
FEATURE [Sketcher::SketchObject] Sketch014  label="buco frontale"
  ArcFitTolerance = 1e-06
  AttachmentSupport = -> [XZ_Plane]
  ExternalGeometry = -> [Sketch]
  FullyConstrained = true
  MakeInternals = false
  MapMode = 5
  Placement = pos=(0,0,0) rot=(1,0,0;1.5708rad)
  sketch-geometry (10):
    g0: LineSegment StartX=0 StartY=0 StartZ=0 EndX=0 EndY=24.671 EndZ=0
    g1: LineSegment StartX=0 StartY=24.671 StartZ=0 EndX=-4 EndY=24.671 EndZ=0
    g2: LineSegment StartX=-4 StartY=24.671 StartZ=0 EndX=-4 EndY=16 EndZ=0
    g3: LineSegment StartX=-4 StartY=16 StartZ=0 EndX=-2.4 EndY=16 EndZ=0
    g4: LineSegment StartX=-2.4 StartY=16 StartZ=0 EndX=-2.4 EndY=10 EndZ=0
    g5: LineSegment StartX=-2.4 StartY=10 StartZ=0 EndX=-12 EndY=10 EndZ=0
    g6: LineSegment StartX=-12 StartY=10 StartZ=0 EndX=-12 EndY=6 EndZ=0
    g7: LineSegment StartX=-12 StartY=6 StartZ=0 EndX=-2.4 EndY=6 EndZ=0
    g8: LineSegment StartX=-2.4 StartY=6 StartZ=0 EndX=-2.4 EndY=0 EndZ=0
    g9: LineSegment StartX=-2.4 StartY=0 StartZ=0 EndX=0 EndY=0 EndZ=0
  constraints (29):
    c: Vertical(g0)
    c: Coincident(g1,g0)
    c: Horizontal(g1)
    c: Coincident(g2,g1)
    c: Vertical(g2)
    c: Coincident(g3,g2)
    c: Horizontal(g3)
    c: Coincident(g4,g3)
    c: Vertical(g4)
    c: Coincident(g5,g4)
    c: Horizontal(g5)
    c: Coincident(g6,g5)
    c: Vertical(g6)
    c: Coincident(g7,g6)
    c: Coincident(g8,g7)
    c: Vertical(g8)
    c: Coincident(g9,g8)
    c: Coincident(g9,g0)
    c: Horizontal(g9)
    c: DistanceY(g0,g0) = 24.671
    c: Horizontal(g7)
    c: DistanceY(g6,g6) = 4
    c: DistanceY(g4,g4) = 6
    c: DistanceX(g9,g9) = 2.4
    c: Coincident(g0,g-1)
    c: DistanceY(g-3,g7) = 0
    c: DistanceX(g8,g4) = 0
    c: DistanceX(g-3,g1) = 0
    c: DistanceX(g6,g-3) = 8
FEATURE [Part::Extrusion] Extrude010  label="Extrude buco frontale"
  Base = -> Sketch014
  Dir = (0,-1,2e-16)
  DirMode = 2
  FaceMakerClass = Part::FaceMakerBullseye
  FaceMakerMode = 3
  LengthFwd = 11.2
  LengthRev = 0
  Solid = true
  Symmetric = true
FEATURE [Sketcher::SketchObject] Sketch015  label="guida rail"
  ArcFitTolerance = 1e-06
  AttachmentSupport = -> [XZ_Plane]
  ExternalGeometry = -> [Sketch]
  FullyConstrained = true
  MakeInternals = false
  MapMode = 5
  Placement = pos=(0,0,0) rot=(1,0,0;1.5708rad)
  sketch-geometry (4):
    g0: LineSegment StartX=-100.8 StartY=43.2 StartZ=0 EndX=-44.6 EndY=43.2 EndZ=0
    g1: LineSegment StartX=-44.6 StartY=43.2 StartZ=0 EndX=-44.6 EndY=41.2 EndZ=0
    g2: LineSegment StartX=-44.6 StartY=41.2 StartZ=0 EndX=-100.8 EndY=41.2 EndZ=0
    g3: LineSegment StartX=-100.8 StartY=41.2 StartZ=0 EndX=-100.8 EndY=43.2 EndZ=0
  constraints (9):
    c: Horizontal(g0)
    c: Coincident(g1,g0)
    c: Coincident(g2,g1)
    c: Coincident(g3,g2)
    c: Coincident(g3,g0)
    c: Vertical(g3)
    c: Coincident(g2,g-3)
    c: Coincident(g1,g-3)
    c: Coincident(g0,g-4)
FEATURE [Part::Extrusion] Extrude011  label="Extrude guida rail"
  Base = -> Sketch015
  Dir = (0,-1,2e-16)
  DirMode = 2
  FaceMakerClass = Part::FaceMakerBullseye
  FaceMakerMode = 3
  LengthFwd = 9
  LengthRev = 0
  Solid = true
  Symmetric = true
FEATURE [Sketcher::SketchObject] Sketch016  label="guide per coperture laterali"
  ArcFitTolerance = 1e-06
  AttachmentSupport = -> [XZ_Plane]
  ExternalGeometry = -> [Sketch]
  FullyConstrained = true
  MakeInternals = false
  MapMode = 5
  Placement = pos=(0,0,0) rot=(1,0,0;1.5708rad)
  sketch-geometry (14):
    g0: Circle CenterX=-5.6 CenterY=7.6 CenterZ=0 NormalX=0 NormalY=0 NormalZ=1 AngleXU=0 Radius=1.6
    g1: Circle CenterX=-5.6 CenterY=7.6 CenterZ=0 NormalX=0 NormalY=0 NormalZ=1 AngleXU=0 Radius=4
    g2: Circle CenterX=-5.6 CenterY=34.8 CenterZ=0 NormalX=0 NormalY=0 NormalZ=1 AngleXU=0 Radius=1.6
    g3: Circle CenterX=-5.6 CenterY=34.8 CenterZ=0 NormalX=0 NormalY=0 NormalZ=1 AngleXU=0 Radius=4
    g4: Circle CenterX=-184.08 CenterY=34.8 CenterZ=0 NormalX=0 NormalY=0 NormalZ=1 AngleXU=0 Radius=1.6
    g5: Circle CenterX=-184.08 CenterY=34.8 CenterZ=0 NormalX=0 NormalY=0 NormalZ=1 AngleXU=0 Radius=4
    g6: Circle CenterX=-179.305 CenterY=-76.8316 CenterZ=0 NormalX=0 NormalY=0 NormalZ=1 AngleXU=0 Radius=1.6
    g7: Circle CenterX=-179.305 CenterY=-76.8316 CenterZ=0 NormalX=0 NormalY=0 NormalZ=1 AngleXU=0 Radius=4
    g8: Circle CenterX=-213.443 CenterY=-76.8316 CenterZ=0 NormalX=0 NormalY=0 NormalZ=1 AngleXU=0 Radius=1.6
    g9: Circle CenterX=-213.443 CenterY=-76.8316 CenterZ=0 NormalX=0 NormalY=0 NormalZ=1 AngleXU=0 Radius=4
    g10: Circle CenterX=-78.51 CenterY=7.6 CenterZ=0 NormalX=0 NormalY=0 NormalZ=1 AngleXU=0 Radius=1.6
    g11: Circle CenterX=-78.51 CenterY=7.6 CenterZ=0 NormalX=0 NormalY=0 NormalZ=1 AngleXU=0 Radius=4
    g12: Circle CenterX=-78.51 CenterY=34.8 CenterZ=0 NormalX=0 NormalY=0 NormalZ=1 AngleXU=0 Radius=1.6
    g13: Circle CenterX=-78.51 CenterY=34.8 CenterZ=0 NormalX=0 NormalY=0 NormalZ=1 AngleXU=0 Radius=4
  constraints (35):
    c: Diameter(g0) = 3.2
    c: Diameter(g1) = 8
    c: Coincident(g0,g1)
    c: Diameter(g2) = 3.2
    c: Diameter(g3) = 8
    c: Coincident(g3,g2)
    c: Tangent(g2,g-7)
    c: Diameter(g4) = 3.2
    c: Diameter(g5) = 8
    c: Coincident(g5,g4)
    c: Tangent(g4,g-7)
    c: Tangent(g4,g-8)
    c: Diameter(g6) = 3.2
    c: Diameter(g7) = 8
    c: Coincident(g7,g6)
    c: Tangent(g6,g-9)
    c: Tangent(g6,g-10)
    c: Diameter(g8) = 3.2
    c: Diameter(g9) = 8
    c: Coincident(g9,g8)
    c: Tangent(g8,g-10)
    c: Tangent(g8,g-11)
    c: Diameter(g10) = 3.2
    c: Diameter(g11) = 8
    c: Diameter(g12) = 3.2
    c: Diameter(g13) = 8
    c: Coincident(g12,g13)
    c: Coincident(g10,g11)
    c: Tangent(g12,g-7)
    c: DistanceX(g12,g10) = 0
    c: Tangent(g2,g-6)
    c: Tangent(g0,g-6)
    c: Tangent(g0,g-3)
    c: Tangent(g10,g-3)
    c: Tangent(g10,g-4)
FEATURE [Part::Extrusion] Extrude012  label="extrude guide per coperture laterali"
  Base = -> Sketch016
  Dir = (0,-1,2e-16)
  DirMode = 2
  FaceMakerClass = Part::FaceMakerBullseye
  FaceMakerMode = 3
  LengthFwd = 25.2
  LengthRev = 0
  Solid = true
  Symmetric = true
FEATURE [Sketcher::SketchObject] Sketch017  label="supporto CAM"
  ArcFitTolerance = 1e-06
  AttachmentSupport = -> [XZ_Plane]
  ExternalGeometry = -> [Sketch]
  FullyConstrained = true
  MakeInternals = false
  MapMode = 5
  Placement = pos=(0,0,0) rot=(1,0,0;1.5708rad)
  sketch-geometry (6):
    g0: LineSegment StartX=-2.4 StartY=48 StartZ=0 EndX=-2.4 EndY=41.2 EndZ=0
    g1: LineSegment StartX=-2.4 StartY=48 StartZ=0 EndX=-34 EndY=48 EndZ=0
    g2: LineSegment StartX=-34 StartY=48 StartZ=0 EndX=-34 EndY=46.72 EndZ=0
    g3: LineSegment StartX=-34 StartY=46.72 StartZ=0 EndX=-36 EndY=46.72 EndZ=0
    g4: LineSegment StartX=-36 StartY=46.72 StartZ=0 EndX=-36 EndY=41.2 EndZ=0
    g5: LineSegment StartX=-36 StartY=41.2 StartZ=0 EndX=-2.4 EndY=41.2 EndZ=0
  constraints (15):
    c: Coincident(g1,g0)
    c: Horizontal(g1)
    c: Coincident(g2,g1)
    c: Vertical(g2)
    c: Coincident(g3,g2)
    c: Horizontal(g3)
    c: Coincident(g4,g3)
    c: Coincident(g5,g4)
    c: DistanceX(g1,g0) = 31.6
    c: Coincident(g5,g0)
    c: Vertical(g4)
    c: DistanceY(g2,g1) = 1.28
    c: Coincident(g0,g-3)
    c: Coincident(g0,g-3)
    c: Coincident(g4,g-4)
FEATURE [Part::Extrusion] Extrude013  label="Extrude supporto CAM"
  Base = -> Sketch017
  Dir = (0,-1,2e-16)
  DirMode = 2
  FaceMakerClass = Part::FaceMakerBullseye
  FaceMakerMode = 3
  LengthFwd = 17.8
  LengthRev = 0
  Solid = true
  Symmetric = true
FEATURE [Sketcher::SketchObject] Sketch018  label="Scavo CAM"
  ArcFitTolerance = 1e-06
  AttachmentSupport = -> [YZ_Plane]
  ExternalGeometry = -> [Sketch]
  FullyConstrained = true
  MakeInternals = false
  MapMode = 5
  Placement = pos=(0,0,0) rot=(0.57735,0.57735,0.57735;2.0944rad)
  sketch-geometry (4):
    g0: LineSegment StartX=-7.73 StartY=48 StartZ=0 EndX=7.73 EndY=48 EndZ=0
    g1: LineSegment [constr] StartX=1.07e-14 StartY=48 StartZ=0 EndX=0 EndY=43.5155 EndZ=0
    g2: ArcOfCircle CenterX=9e-15 CenterY=52.42 CenterZ=0 NormalX=0 NormalY=0 NormalZ=1 AngleXU=0 Radius=8.90445 StartAngle=3.66102 EndAngle=5.76376
    g3: Circle [constr] CenterX=9e-15 CenterY=52.42 CenterZ=0 NormalX=0 NormalY=0 NormalZ=1 AngleXU=0 Radius=8.9
  constraints (13):
    c: Horizontal(g0)
    c: DistanceY(g-3,g0) = 0
    c: DistanceX(g0,g0) = 15.46
    c: DistanceX(g0,g-3) = 7.73
    c: DistanceX(g-3) = 0
    c: Coincident(g1,g-3)
    c: PointOnObject(g1,g-2)
    c: Coincident(g2,g0)
    c: Coincident(g2,g0)
    c: PointOnObject(g1,g2)
    c: Diameter(g3) = 17.8
    c: DistanceY(g1,g3) = 4.42
    c: Coincident(g2,g3)
FEATURE [Part::Extrusion] Extrude014  label="Extrude Scavo CAM"
  Base = -> Sketch018
  Dir = (1,0,0)
  DirMode = 2
  FaceMakerClass = Part::FaceMakerBullseye
  FaceMakerMode = 3
  LengthFwd = -34
  LengthRev = 0
  Solid = true
  Symmetric = false
FEATURE [Sketcher::SketchObject] Sketch019  label="scavo rumble"
  ArcFitTolerance = 1e-06
  AttachmentSupport = -> [XZ_Plane]
  ExternalGeometry = -> [Sketch]
  FullyConstrained = true
  MakeInternals = false
  MapMode = 5
  Placement = pos=(0,0,0) rot=(1,0,0;1.5708rad)
  sketch-geometry (6):
    g0: LineSegment StartX=-168.716 StartY=-37.1227 StartZ=0 EndX=-163.58 EndY=-38.7914 EndZ=0
    g1: LineSegment StartX=-163.58 StartY=-38.7914 StartZ=0 EndX=-170.687 EndY=-60.6657 EndZ=0
    g2: LineSegment StartX=-170.687 StartY=-60.6657 StartZ=0 EndX=-175.823 EndY=-58.997 EndZ=0
    g3: LineSegment StartX=-175.823 StartY=-58.997 StartZ=0 EndX=-168.716 EndY=-37.1227 EndZ=0
    g4: LineSegment [constr] StartX=-145.51 StartY=22 StartZ=0 EndX=-165.102 EndY=-38.297 EndZ=0
    g5: LineSegment [constr] StartX=-163.58 StartY=-38.7914 StartZ=0 EndX=-165.102 EndY=-38.297 EndZ=0
  constraints (17):
    c: Coincident(g1,g0)
    c: Coincident(g2,g1)
    c: Coincident(g3,g2)
    c: Coincident(g3,g0)
    c: Parallel(g3,g-3)
    c: Parallel(g3,g1)
    c: Perpendicular(g3,g0)
    c: Perpendicular(g2,g3)
    c: Distance(g2,g0) = 23
    c: Parallel(g4,g-3)
    c: Distance(g4) = 63.4
    c: Coincident(g4,g-3)
    c: Parallel(g5,g0)
    c: Coincident(g5,g0)
    c: Coincident(g5,g4)
    c: Distance(g4,g0) = 3.8
    c: Distance(g4,g0) = 1.6
FEATURE [Part::Extrusion] Extrude015  label="scavo rumble001"
  Base = -> Sketch019
  Dir = (0,-1,2e-16)
  DirMode = 2
  FaceMakerClass = Part::FaceMakerBullseye
  FaceMakerMode = 3
  LengthFwd = 21
  LengthRev = 0
  Solid = true
  Symmetric = true
FEATURE [Sketcher::SketchObject] Sketch020  label="fermo rumble"
  ArcFitTolerance = 1e-06
  AttachmentSupport = -> [XZ_Plane]
  ExternalGeometry = -> [Sketch019,Sketch]
  FullyConstrained = true
  MakeInternals = false
  MapMode = 5
  Placement = pos=(0,0,0) rot=(1,0,0;1.5708rad)
  sketch-geometry (16):
    g0: LineSegment [constr] StartX=-170.849 StartY=-55.9866 StartZ=0 EndX=-172.209 EndY=-60.1713 EndZ=0
    g1: LineSegment [constr] StartX=-172.209 StartY=-60.1713 StartZ=0 EndX=-170.687 EndY=-60.6657 EndZ=0
    g2: LineSegment StartX=-172.262 StartY=-53.2145 StartZ=0 EndX=-170.17 EndY=-53.8943 EndZ=0
    g3: LineSegment StartX=-170.17 StartY=-53.8943 StartZ=0 EndX=-170.849 EndY=-55.9866 EndZ=0
    g4: LineSegment StartX=-170.849 StartY=-55.9866 StartZ=0 EndX=-172.942 EndY=-55.3068 EndZ=0
    g5: LineSegment StartX=-172.942 StartY=-55.3068 StartZ=0 EndX=-172.262 EndY=-53.2145 EndZ=0
    g6: LineSegment StartX=-171.767 StartY=-51.6928 StartZ=0 EndX=-168.344 EndY=-52.8052 EndZ=0
    g7: LineSegment StartX=-168.344 StartY=-52.8052 StartZ=0 EndX=-169.951 EndY=-57.7507 EndZ=0
    g8: LineSegment StartX=-169.951 StartY=-57.7507 StartZ=0 EndX=-173.374 EndY=-56.6383 EndZ=0
    g9: LineSegment StartX=-174.402 StartY=-54.6222 StartZ=0 EndX=-173.784 EndY=-52.72 EndZ=0
    g10: LineSegment [constr] StartX=-173.784 StartY=-52.72 StartZ=0 EndX=-173.289 EndY=-51.1984 EndZ=0
    g11: LineSegment [constr] StartX=-173.289 StartY=-51.1984 StartZ=0 EndX=-171.767 EndY=-51.6928 EndZ=0
    g12: ArcOfCircle CenterX=-172.88 CenterY=-55.1166 CenterZ=0 NormalX=0 NormalY=0 NormalZ=1 AngleXU=0 Radius=1.6 StartAngle=2.82743 EndAngle=4.39823
    g13: GeomPoint [constr] X=-174.896 Y=-56.1438 Z=0
    g14: ArcOfCircle CenterX=-172.262 CenterY=-53.2145 CenterZ=0 NormalX=0 NormalY=0 NormalZ=1 AngleXU=0 Radius=1.6 StartAngle=1.25664 EndAngle=2.82743
    g15: GeomPoint [constr] X=-173.289 Y=-51.1984 Z=0
  constraints (42):
    c: Parallel(g0,g-4)
    c: Distance(g0) = 4.4
    c: Coincident(g1,g0)
    c: Perpendicular(g0,g1)
    c: Distance(g1) = 1.6
    c: Coincident(g1,g-5)
    c: Coincident(g3,g2)
    c: Coincident(g4,g3)
    c: Coincident(g5,g4)
    c: Coincident(g5,g2)
    c: Parallel(g3,g-4)
    c: Parallel(g3,g5)
    c: Perpendicular(g2,g3)
    c: Parallel(g4,g2)
    c: Distance(g2) = 2.2
    c: Distance(g3) = 2.2
    c: Coincident(g7,g6)
    c: Coincident(g8,g7)
    c: Parallel(g7,g-4)
    c: Parallel(g7,g9)
    c: Perpendicular(g6,g7)
    c: Parallel(g6,g8)
    c: Distance(g6,g15) = 5.2
    c: Distance(g7) = 5.2
    c: Coincident(g11,g10)
    c: Parallel(g10,g9)
    c: Parallel(g11,g6)
    c: Distance(g10) = 1.6
    c: Distance(g11) = 1.6
    c: Coincident(g10,g15)
    c: Distance(g11,g2) = 1.6
    c: Distance(g2,g10) = 1.6
    c: PointOnObject(g13,g8)
    c: PointOnObject(g13,g9)
    c: Tangent(g8,g12) = 1.5708
    c: Tangent(g9,g12) = 1.5708
    c: PointOnObject(g15,g9)
    c: Tangent(g6,g14) = 1.5708
    c: Tangent(g9,g14) = 1.5708
    c: Equal(g12,g14)
    c: Coincident(g6,g11)
    c: Coincident(g3,g0)
FEATURE [Part::Extrusion] Extrude016  label="Extrude fermo rumble"
  Base = -> Sketch020
  Dir = (0,-1,2e-16)
  DirMode = 2
  FaceMakerClass = Part::FaceMakerBullseye
  FaceMakerMode = 3
  LengthFwd = 25.2
  LengthRev = 0
  Solid = true
  Symmetric = true
FEATURE [Sketcher::SketchObject] Sketch021  label="perno fermo rumble001"
  ArcFitTolerance = 1e-06
  AttachmentSupport = -> [XZ_Plane001]
  FullyConstrained = true
  MakeInternals = false
  MapMode = 5
  Placement = pos=(0,0,0) rot=(1,0,0;1.5708rad)
  sketch-geometry (16):
    g0: LineSegment StartX=0 StartY=0.45 StartZ=0 EndX=0 EndY=1.55 EndZ=0
    g1: LineSegment StartX=0.45 StartY=2 StartZ=0 EndX=1.55 EndY=2 EndZ=0
    g2: LineSegment StartX=2 StartY=1.55 StartZ=0 EndX=2 EndY=0.45 EndZ=0
    g3: LineSegment StartX=1.55 StartY=0 StartZ=0 EndX=0.45 EndY=0 EndZ=0
    g4: ArcOfCircle [constr] CenterX=0.45 CenterY=1.55 CenterZ=0 NormalX=0 NormalY=0 NormalZ=1 AngleXU=0 Radius=0.45 StartAngle=1.5708 EndAngle=3.14159
    g5: GeomPoint [constr] X=0 Y=2 Z=0
    g6: LineSegment StartX=0.45 StartY=2 StartZ=0 EndX=0 EndY=1.55 EndZ=0
    g7: ArcOfCircle [constr] CenterX=1.55 CenterY=1.55 CenterZ=0 NormalX=0 NormalY=0 NormalZ=1 AngleXU=0 Radius=0.45 StartAngle=0 EndAngle=1.5708
    g8: GeomPoint [constr] X=2 Y=2 Z=0
    g9: LineSegment StartX=2 StartY=1.55 StartZ=0 EndX=1.55 EndY=2 EndZ=0
    g10: ArcOfCircle [constr] CenterX=1.55 CenterY=0.45 CenterZ=0 NormalX=0 NormalY=0 NormalZ=1 AngleXU=0 Radius=0.45 StartAngle=4.71239 EndAngle=6.28319
    g11: GeomPoint [constr] X=2 Y=0 Z=0
    g12: LineSegment StartX=1.55 StartY=0 StartZ=0 EndX=2 EndY=0.45 EndZ=0
    g13: ArcOfCircle [constr] CenterX=0.45 CenterY=0.45 CenterZ=0 NormalX=0 NormalY=0 NormalZ=1 AngleXU=0 Radius=0.45 StartAngle=3.14159 EndAngle=4.71239
    g14: GeomPoint [constr] X=0 Y=0 Z=0
    g15: LineSegment StartX=0 StartY=0.45 StartZ=0 EndX=0.45 EndY=0 EndZ=0
  constraints (35):
    c: Coincident(g14,g-1)
    c: PointOnObject(g5,g-2)
    c: Horizontal(g1)
    c: Vertical(g2)
    c: Horizontal(g3)
    c: DistanceX(g5,g8) = 2
    c: DistanceY(g11,g8) = 2
    c: PointOnObject(g5,g0)
    c: PointOnObject(g5,g1)
    c: Tangent(g0,g4) = 1.5708
    c: Tangent(g1,g4) = 1.5708
    c: Coincident(g6,g0)
    c: Coincident(g6,g1)
    c: PointOnObject(g8,g2)
    c: PointOnObject(g8,g1)
    c: Tangent(g2,g7) = 1.5708
    c: Tangent(g1,g7) = 1.5708
    c: Coincident(g9,g2)
    c: Coincident(g9,g1)
    c: PointOnObject(g11,g2)
    c: PointOnObject(g11,g3)
    c: Tangent(g2,g10) = 1.5708
    c: Tangent(g3,g10) = 1.5708
    c: Coincident(g12,g2)
    c: Coincident(g12,g3)
    c: PointOnObject(g14,g0)
    c: PointOnObject(g14,g3)
    c: Tangent(g0,g13) = 1.5708
    c: Tangent(g3,g13) = 1.5708
    c: Coincident(g15,g0)
    c: Coincident(g15,g3)
    c: Equal(g6,g9)
    c: Equal(g9,g12)
    c: Equal(g12,g15)
    c: DistanceX(g14,g3) = 0.45
FEATURE [Sketcher::SketchObject] Sketch022  label="fori per M3x5(OD)x6(L)"
  ArcFitTolerance = 1e-06
  AttachmentSupport = -> [XZ_Plane]
  ExternalGeometry = -> [Sketch016]
  FullyConstrained = true
  MakeInternals = false
  MapMode = 5
  Placement = pos=(0,0,0) rot=(1,0,0;1.5708rad)
  sketch-geometry (7):
    g0: Circle CenterX=-5.6 CenterY=34.8 CenterZ=0 NormalX=0 NormalY=0 NormalZ=1 AngleXU=0 Radius=2.5
    g1: Circle CenterX=-5.6 CenterY=7.6 CenterZ=0 NormalX=0 NormalY=0 NormalZ=1 AngleXU=0 Radius=2.5
    g2: Circle CenterX=-78.51 CenterY=34.8 CenterZ=0 NormalX=0 NormalY=0 NormalZ=1 AngleXU=0 Radius=2.5
    g3: Circle CenterX=-78.51 CenterY=7.6 CenterZ=0 NormalX=0 NormalY=0 NormalZ=1 AngleXU=0 Radius=2.5
    g4: Circle CenterX=-184.08 CenterY=34.8 CenterZ=0 NormalX=0 NormalY=0 NormalZ=1 AngleXU=0 Radius=2.5
    g5: Circle CenterX=-179.305 CenterY=-76.8316 CenterZ=0 NormalX=0 NormalY=0 NormalZ=1 AngleXU=0 Radius=2.5
    g6: Circle CenterX=-213.443 CenterY=-76.8316 CenterZ=0 NormalX=0 NormalY=0 NormalZ=1 AngleXU=0 Radius=2.5
  constraints (14):
    c: Diameter(g0) = 5
    c: Diameter(g1) = 5
    c: Diameter(g2) = 5
    c: Diameter(g3) = 5
    c: Diameter(g4) = 5
    c: Diameter(g5) = 5
    c: Diameter(g6) = 5
    c: Coincident(g0,g-8)
    c: Coincident(g1,g-9)
    c: Coincident(g2,g-6)
    c: Coincident(g3,g-7)
    c: Coincident(g4,g-5)
    c: Coincident(g5,g-4)
    c: Coincident(g6,g-3)
FEATURE [Part::Extrusion] Extrude018  label="Extrude fori M3x5x6 - dx"
  Base = -> Sketch022
  Dir = (0,-1,2e-16)
  DirMode = 2
  FaceMakerClass = Part::FaceMakerBullseye
  FaceMakerMode = 3
  LengthFwd = 6.2
  LengthRev = 0
  Placement = pos=(0,-9.5,0) rot=(0,0,1;0rad)
  Solid = true
  Symmetric = true
FEATURE [Part::Extrusion] Extrude019  label="Extrude fori M3x5x6 - sx"
  Base = -> Sketch022
  Dir = (0,-1,2e-16)
  DirMode = 2
  FaceMakerClass = Part::FaceMakerBullseye
  FaceMakerMode = 3
  LengthFwd = 6.2
  LengthRev = 0
  Placement = pos=(0,9.5,0) rot=(0,0,1;0rad)
  Solid = true
  Symmetric = true
FEATURE [Sketcher::SketchObject] Sketch023  label="foro anteriore M3x5x6"
  ArcFitTolerance = 1e-06
  AttachmentSupport = -> [YZ_Plane]
  FullyConstrained = true
  MakeInternals = false
  MapMode = 5
  Placement = pos=(0,0,0) rot=(0.57735,0.57735,0.57735;2.0944rad)
  sketch-geometry (2):
    g0: LineSegment [constr] StartX=0 StartY=0 StartZ=0 EndX=0 EndY=38.6 EndZ=0
    g1: Circle CenterX=0 CenterY=38.6 CenterZ=0 NormalX=0 NormalY=0 NormalZ=1 AngleXU=0 Radius=2.5
  constraints (5):
    c: Coincident(g0,g-1)
    c: PointOnObject(g0,g-2)
    c: DistanceY(g0,g0) = 38.6
    c: Diameter(g1) = 5
    c: Coincident(g1,g0)
FEATURE [Part::Extrusion] Extrude020  label="Extrude foro anteriore M3x5x6"
  Base = -> Sketch023
  Dir = (1,0,0)
  DirMode = 2
  FaceMakerClass = Part::FaceMakerBullseye
  FaceMakerMode = 3
  LengthFwd = -6.2
  LengthRev = 0
  Solid = true
  Symmetric = false
FEATURE [Sketcher::SketchObject] Sketch024  label="fori per viti frontale"
  ArcFitTolerance = 1e-06
  AttachmentSupport = -> [YZ_Plane]
  FullyConstrained = true
  MakeInternals = false
  MapMode = 5
  Placement = pos=(0,0,0) rot=(0.57735,0.57735,0.57735;2.0944rad)
  sketch-geometry (9):
    g0: LineSegment [constr] StartX=-10.3 StartY=30.721 StartZ=0 EndX=10.3 EndY=30.721 EndZ=0
    g1: LineSegment [constr] StartX=10.3 StartY=30.721 StartZ=0 EndX=10.3 EndY=10.121 EndZ=0
    g2: LineSegment [constr] StartX=10.3 StartY=10.121 StartZ=0 EndX=-10.3 EndY=10.121 EndZ=0
    g3: LineSegment [constr] StartX=-10.3 StartY=10.121 StartZ=0 EndX=-10.3 EndY=30.721 EndZ=0
    g4: LineSegment [constr] StartX=0 StartY=0 StartZ=0 EndX=0 EndY=10.121 EndZ=0
    g5: Circle CenterX=-10.3 CenterY=30.721 CenterZ=0 NormalX=0 NormalY=0 NormalZ=1 AngleXU=0 Radius=2
    g6: Circle CenterX=10.3 CenterY=30.721 CenterZ=0 NormalX=0 NormalY=0 NormalZ=1 AngleXU=0 Radius=2
    g7: Circle CenterX=-10.3 CenterY=10.121 CenterZ=0 NormalX=0 NormalY=0 NormalZ=1 AngleXU=0 Radius=2
    g8: Circle CenterX=10.3 CenterY=10.121 CenterZ=0 NormalX=0 NormalY=0 NormalZ=1 AngleXU=0 Radius=2
  constraints (22):
    c: Horizontal(g0)
    c: Coincident(g1,g0)
    c: Vertical(g1)
    c: Coincident(g2,g1)
    c: Horizontal(g2)
    c: Coincident(g3,g2)
    c: Coincident(g3,g0)
    c: Vertical(g3)
    c: DistanceX(g0,g0) = 20.6
    c: DistanceY(g3,g3) = 20.6
    c: Coincident(g4,g-1)
    c: PointOnObject(g4,g-2)
    c: DistanceY(g4,g4) = 10.121
    c: Symmetric(g2,g2,g4)
    c: Diameter(g5) = 4
    c: Diameter(g6) = 4
    c: Diameter(g7) = 4
    c: Diameter(g8) = 4
    c: Coincident(g5,g0)
    c: Coincident(g6,g0)
    c: Coincident(g7,g2)
    c: Coincident(g8,g1)
FEATURE [Part::Extrusion] Extrude021  label="Extrude fori per viti frontale"
  Base = -> Sketch024
  Dir = (1,0,0)
  DirMode = 2
  FaceMakerClass = Part::FaceMakerBullseye
  FaceMakerMode = 3
  LengthFwd = -2.4
  LengthRev = 0
  Solid = true
  Symmetric = false
FEATURE [Sketcher::SketchObject] Sketch025  label="foro per filo CAM"
  ArcFitTolerance = 1e-06
  AttachmentSupport = -> [XZ_Plane]
  ExternalGeometry = -> [Sketch]
  FullyConstrained = true
  MakeInternals = false
  MapMode = 5
  Placement = pos=(0,0,0) rot=(1,0,0;1.5708rad)
  sketch-geometry (4):
    g0: LineSegment StartX=-44.6 StartY=41.2 StartZ=0 EndX=-44.6 EndY=36.4 EndZ=0
    g1: LineSegment StartX=-44.6 StartY=36.4 StartZ=0 EndX=-54.6 EndY=36.4 EndZ=0
    g2: LineSegment StartX=-54.6 StartY=36.4 StartZ=0 EndX=-50.4 EndY=41.2 EndZ=0
    g3: LineSegment StartX=-50.4 StartY=41.2 StartZ=0 EndX=-44.6 EndY=41.2 EndZ=0
  constraints (11):
    c: Vertical(g0)
    c: Coincident(g1,g0)
    c: Horizontal(g1)
    c: Coincident(g2,g1)
    c: Coincident(g3,g2)
    c: Coincident(g3,g0)
    c: Horizontal(g3)
    c: Coincident(g0,g-3)
    c: DistanceY(g0,g-4) = 0
    c: DistanceX(g3,g3) = 5.8
    c: DistanceX(g1,g1) = 10
FEATURE [Part::Extrusion] Extrude022  label="Extrude foro per filo CAM dx"
  Base = -> Sketch025
  Dir = (0,-1,2e-16)
  DirMode = 2
  FaceMakerClass = Part::FaceMakerBullseye
  FaceMakerMode = 3
  LengthFwd = 4.9
  LengthRev = 0
  Placement = pos=(0,6.95,0) rot=(0,0,1;0rad)
  Solid = true
  Symmetric = true
FEATURE [Part::Extrusion] Extrude023  label="Extrude foro per filo CAM sx"
  Base = -> Sketch025
  Dir = (0,-1,2e-16)
  DirMode = 2
  FaceMakerClass = Part::FaceMakerBullseye
  FaceMakerMode = 3
  LengthFwd = 4.9
  LengthRev = 0
  Placement = pos=(0,-6.95,0) rot=(0,0,1;0rad)
  Solid = true
  Symmetric = true
FEATURE [Sketcher::SketchObject] Sketch026  label="foro sotto anteriore M3x5x6"
  ArcFitTolerance = 1e-06
  AttachmentSupport = -> [XY_Plane]
  FullyConstrained = true
  MakeInternals = false
  MapMode = 5
  sketch-geometry (2):
    g0: LineSegment [constr] StartX=0 StartY=0 StartZ=0 EndX=-16.5 EndY=0 EndZ=0
    g1: Circle CenterX=-16.5 CenterY=0 CenterZ=0 NormalX=0 NormalY=0 NormalZ=1 AngleXU=0 Radius=2.5
  constraints (5):
    c: Distance(g0) = 16.5
    c: Coincident(g0,g-1)
    c: PointOnObject(g0,g-1)
    c: Diameter(g1) = 5
    c: Coincident(g0,g1)
FEATURE [Sketcher::SketchObject] Sketch027  label="foro sotto posteriore M3x5x6"
  ArcFitTolerance = 1e-06
  AttachmentSupport = -> [XY_Plane]
  ExternalGeometry = -> [Sketch]
  FullyConstrained = true
  MakeInternals = false
  MapMode = 5
  sketch-geometry (2):
    g0: LineSegment [constr] StartX=-82.8 StartY=2e-16 StartZ=0 EndX=-71.3 EndY=2e-16 EndZ=0
    g1: Circle CenterX=-71.3 CenterY=2e-16 CenterZ=0 NormalX=0 NormalY=0 NormalZ=1 AngleXU=0 Radius=2.5
  constraints (5):
    c: Distance(g0) = 11.5
    c: Coincident(g0,g-3)
    c: PointOnObject(g0,g-3)
    c: Diameter(g1) = 5
    c: Coincident(g1,g0)
FEATURE [Sketcher::SketchObject] Sketch029  label="fori sotto impugnatura"
  ArcFitTolerance = 1e-06
  AttachmentSupport = -> [XY_Plane]
  ExternalGeometry = -> [Sketch]
  FullyConstrained = true
  MakeInternals = false
  MapMode = 5
  sketch-geometry (15):
    g0: LineSegment [constr] StartX=-175.232 StartY=-1.83e-14 StartZ=0 EndX=-191.232 EndY=0 EndZ=0
    g1: Circle CenterX=-191.232 CenterY=0 CenterZ=0 NormalX=0 NormalY=0 NormalZ=1 AngleXU=0 Radius=3.95
    g2: LineSegment [constr] StartX=-175.232 StartY=-1.83e-14 StartZ=0 EndX=-204.275 EndY=0 EndZ=0
    g3: LineSegment StartX=-204.275 StartY=3.525 StartZ=0 EndX=-204.275 EndY=-3.525 EndZ=0
    g4: LineSegment StartX=-205.4 StartY=-4.65 StartZ=0 EndX=-206.65 EndY=-4.65 EndZ=0
    g5: LineSegment StartX=-207.775 StartY=-3.525 StartZ=0 EndX=-207.775 EndY=3.525 EndZ=0
    g6: LineSegment StartX=-206.65 StartY=4.65 StartZ=0 EndX=-205.4 EndY=4.65 EndZ=0
    g7: ArcOfCircle CenterX=-206.65 CenterY=3.525 CenterZ=0 NormalX=0 NormalY=0 NormalZ=1 AngleXU=0 Radius=1.125 StartAngle=1.5708 EndAngle=3.14159
    g8: GeomPoint [constr] X=-207.775 Y=4.65 Z=0
    g9: ArcOfCircle CenterX=-205.4 CenterY=3.525 CenterZ=0 NormalX=0 NormalY=0 NormalZ=1 AngleXU=0 Radius=1.125 StartAngle=0 EndAngle=1.5708
    g10: GeomPoint [constr] X=-204.275 Y=4.65 Z=0
    g11: ArcOfCircle CenterX=-205.4 CenterY=-3.525 CenterZ=0 NormalX=0 NormalY=0 NormalZ=1 AngleXU=0 Radius=1.125 StartAngle=4.71239 EndAngle=6.28319
    g12: GeomPoint [constr] X=-204.275 Y=-4.65 Z=0
    g13: ArcOfCircle CenterX=-206.65 CenterY=-3.525 CenterZ=0 NormalX=0 NormalY=0 NormalZ=1 AngleXU=0 Radius=1.125 StartAngle=3.14159 EndAngle=4.71239
    g14: GeomPoint [constr] X=-207.775 Y=-4.65 Z=0
  constraints (35):
    c: Distance(g0) = 16
    c: Coincident(g0,g-3)
    c: PointOnObject(g0,g-1)
    c: Diameter(g1) = 7.9
    c: Coincident(g1,g0)
    c: Coincident(g2,g0)
    c: PointOnObject(g2,g-1)
    c: Vertical(g3)
    c: Horizontal(g4)
    c: Vertical(g5)
    c: Horizontal(g6)
    c: DistanceY(g12,g10) = 9.3
    c: DistanceX(g8,g10) = 3.5
    c: Symmetric(g10,g12,g2)
    c: PointOnObject(g8,g5)
    c: PointOnObject(g8,g6)
    c: Tangent(g5,g7) = 1.5708
    c: Tangent(g6,g7) = 1.5708
    c: PointOnObject(g10,g3)
    c: PointOnObject(g10,g6)
    c: Tangent(g3,g9) = 1.5708
    c: Tangent(g6,g9) = 1.5708
    c: PointOnObject(g12,g3)
    c: PointOnObject(g12,g4)
    c: Tangent(g3,g11) = 1.5708
    c: Tangent(g4,g11) = 1.5708
    c: PointOnObject(g14,g4)
    c: PointOnObject(g14,g5)
    c: Tangent(g4,g13) = 1.5708
    c: Tangent(g5,g13) = 1.5708
    c: Equal(g7,g9)
    c: Equal(g9,g11)
    c: Equal(g11,g13)
    c: DistanceX(g6,g6) = 1.25
    c: DistanceX(g-5,g5) = 6.8
FEATURE [Sketcher::SketchObject] Sketch030  label="fori superiori per solenoide e oled"
  ArcFitTolerance = 1e-06
  AttachmentSupport = -> [XY_Plane]
  ExternalGeometry = -> [Sketch]
  FullyConstrained = true
  MakeInternals = false
  MapMode = 5
  sketch-geometry (33):
    g0: LineSegment [constr] StartX=-181.6 StartY=1.12e-14 StartZ=0 EndX=-169.91 EndY=0 EndZ=0
    g1: LineSegment [constr] StartX=-169.91 StartY=0 StartZ=0 EndX=-169.91 EndY=-2.6 EndZ=0
    g2: LineSegment [constr] StartX=-169.91 StartY=0 StartZ=0 EndX=-169.91 EndY=2.6 EndZ=0
    g3: LineSegment StartX=-169.91 StartY=4.975 StartZ=0 EndX=-169.91 EndY=8.225 EndZ=0
    g4: LineSegment StartX=-167.535 StartY=10.6 StartZ=0 EndX=-167.285 EndY=10.6 EndZ=0
    g5: LineSegment StartX=-164.91 StartY=8.225 StartZ=0 EndX=-164.91 EndY=4.975 EndZ=0
    g6: LineSegment StartX=-167.285 StartY=2.6 StartZ=0 EndX=-167.535 EndY=2.6 EndZ=0
    g7: LineSegment StartX=-169.91 StartY=-4.975 StartZ=0 EndX=-169.91 EndY=-8.225 EndZ=0
    g8: LineSegment StartX=-167.535 StartY=-10.6 StartZ=0 EndX=-167.285 EndY=-10.6 EndZ=0
    g9: LineSegment StartX=-164.91 StartY=-8.225 StartZ=0 EndX=-164.91 EndY=-4.975 EndZ=0
    g10: LineSegment StartX=-167.285 StartY=-2.6 StartZ=0 EndX=-167.535 EndY=-2.6 EndZ=0
    g11: ArcOfCircle CenterX=-167.535 CenterY=8.225 CenterZ=0 NormalX=0 NormalY=0 NormalZ=1 AngleXU=0 Radius=2.375 StartAngle=1.5708 EndAngle=3.14159
    g12: GeomPoint [constr] X=-169.91 Y=10.6 Z=0
    g13: ArcOfCircle CenterX=-167.285 CenterY=8.225 CenterZ=0 NormalX=0 NormalY=0 NormalZ=1 AngleXU=0 Radius=2.375 StartAngle=0 EndAngle=1.5708
    g14: GeomPoint [constr] X=-164.91 Y=10.6 Z=0
    g15: ArcOfCircle CenterX=-167.285 CenterY=4.975 CenterZ=0 NormalX=0 NormalY=0 NormalZ=1 AngleXU=0 Radius=2.375 StartAngle=4.71239 EndAngle=6.28319
    g16: GeomPoint [constr] X=-164.91 Y=2.6 Z=0
    g17: ArcOfCircle CenterX=-167.535 CenterY=4.975 CenterZ=0 NormalX=0 NormalY=0 NormalZ=1 AngleXU=0 Radius=2.375 StartAngle=3.14159 EndAngle=4.71239
    g18: GeomPoint [constr] X=-169.91 Y=2.6 Z=0
    g19: ArcOfCircle CenterX=-167.535 CenterY=-4.975 CenterZ=0 NormalX=0 NormalY=0 NormalZ=1 AngleXU=0 Radius=2.375 StartAngle=1.5708 EndAngle=3.14159
    g20: GeomPoint [constr] X=-169.91 Y=-2.6 Z=0
    g21: ArcOfCircle CenterX=-167.285 CenterY=-4.975 CenterZ=0 NormalX=0 NormalY=0 NormalZ=1 AngleXU=0 Radius=2.375 StartAngle=0 EndAngle=1.5708
    g22: GeomPoint [constr] X=-164.91 Y=-2.6 Z=0
    g23: ArcOfCircle CenterX=-167.285 CenterY=-8.225 CenterZ=0 NormalX=0 NormalY=0 NormalZ=1 AngleXU=0 Radius=2.375 StartAngle=4.71239 EndAngle=6.28319
    g24: GeomPoint [constr] X=-164.91 Y=-10.6 Z=0
    g25: ArcOfCircle CenterX=-167.535 CenterY=-8.225 CenterZ=0 NormalX=0 NormalY=0 NormalZ=1 AngleXU=0 Radius=2.375 StartAngle=3.14159 EndAngle=4.71239
    g26: GeomPoint [constr] X=-169.91 Y=-10.6 Z=0
    g27: LineSegment [constr] StartX=-181.6 StartY=1.12e-14 StartZ=0 EndX=-152.209 EndY=0 EndZ=0
    g28: LineSegment [constr] StartX=-181.6 StartY=1.12e-14 StartZ=0 EndX=-130.41 EndY=0 EndZ=0
    g29: LineSegment [constr] StartX=-152.209 StartY=0 StartZ=0 EndX=-152.209 EndY=6.95 EndZ=0
    g30: LineSegment [constr] StartX=-130.41 StartY=0 StartZ=0 EndX=-130.41 EndY=-6.95 EndZ=0
    g31: Circle CenterX=-152.209 CenterY=6.95 CenterZ=0 NormalX=0 NormalY=0 NormalZ=1 AngleXU=0 Radius=2.1
    g32: Circle CenterX=-130.41 CenterY=-6.95 CenterZ=0 NormalX=0 NormalY=0 NormalZ=1 AngleXU=0 Radius=2.1
  constraints (79):
    c: Distance(g0) = 11.69
    c: PointOnObject(g0,g-1)
    c: Coincident(g-4,g0)
    c: Distance(g1) = 2.6
    c: Coincident(g1,g0)
    c: Vertical(g1)
    c: Distance(g2) = 2.6
    c: Coincident(g2,g0)
    c: Vertical(g2)
    c: Distance(g18,g12) = 8
    c: Coincident(g18,g2)
    c: Vertical(g3)
    c: Distance(g14,g12) = 5
    c: Horizontal(g4)
    c: Distance(g16,g14) = 8
    c: Vertical(g5)
    c: Distance(g26,g20) = 8
    c: Coincident(g20,g1)
    c: Vertical(g7)
    c: Distance(g26,g24) = 5
    c: Horizontal(g8)
    c: Distance(g24,g22) = 8
    c: Vertical(g9)
    c: PointOnObject(g12,g3)
    c: PointOnObject(g12,g4)
    c: Tangent(g3,g11) = 1.5708
    c: Tangent(g4,g11) = 1.5708
    c: PointOnObject(g14,g5)
    c: PointOnObject(g14,g4)
    c: Tangent(g5,g13) = 1.5708
    c: Tangent(g4,g13) = 1.5708
    c: PointOnObject(g16,g5)
    c: PointOnObject(g16,g6)
    c: Tangent(g5,g15) = 1.5708
    c: Tangent(g6,g15) = 1.5708
    c: PointOnObject(g18,g3)
    c: PointOnObject(g18,g6)
    c: Tangent(g3,g17) = 1.5708
    c: Tangent(g6,g17) = 1.5708
    c: Equal(g11,g13)
    c: Equal(g13,g15)
    c: Equal(g15,g17)
    c: DistanceX(g4,g4) = 0.25
    c: PointOnObject(g20,g7)
    c: PointOnObject(g20,g10)
    c: Tangent(g7,g19) = -1.5708
    c: Tangent(g10,g19) = -1.5708
    c: PointOnObject(g22,g9)
    c: PointOnObject(g22,g10)
    c: Tangent(g9,g21) = -1.5708
    c: Tangent(g10,g21) = -1.5708
    c: PointOnObject(g24,g9)
    c: PointOnObject(g24,g8)
    c: Tangent(g9,g23) = -1.5708
    c: Tangent(g8,g23) = -1.5708
    c: PointOnObject(g26,g8)
    c: PointOnObject(g26,g7)
    c: Tangent(g8,g25) = -1.5708
    c: Tangent(g7,g25) = -1.5708
    c: Equal(g19,g21)
    c: Equal(g21,g23)
    c: Equal(g23,g25)
    c: DistanceX(g10,g10) = 0.25
    c: Distance(g27) = 29.391
    c: Coincident(g27,g0)
    c: PointOnObject(g27,g-1)
    c: Distance(g28) = 51.19
    c: Coincident(g28,g0)
    c: PointOnObject(g28,g-1)
    c: Distance(g29) = 6.95
    c: Coincident(g29,g27)
    c: Vertical(g29)
    c: Distance(g30) = 6.95
    c: Coincident(g30,g28)
    c: Vertical(g30)
    c: Diameter(g31) = 4.2
    c: Diameter(g32) = 4.2
    c: Coincident(g32,g30)
    c: Coincident(g31,g29)
FEATURE [Sketcher::SketchObject] Sketch031  label="fori inferiori switch pompa"
  ArcFitTolerance = 1e-06
  AttachmentSupport = -> [XY_Plane]
  ExternalGeometry = -> [Sketch]
  FullyConstrained = true
  MakeInternals = false
  MapMode = 5
  sketch-geometry (4):
    g0: LineSegment [constr] StartX=-57.2 StartY=1.9e-15 StartZ=0 EndX=-62.45 EndY=1.9e-15 EndZ=0
    g1: LineSegment [constr] StartX=-62.45 StartY=3.25 StartZ=0 EndX=-62.45 EndY=-3.25 EndZ=0
    g2: Circle CenterX=-62.45 CenterY=3.25 CenterZ=0 NormalX=0 NormalY=0 NormalZ=1 AngleXU=0 Radius=1.6
    g3: Circle CenterX=-62.45 CenterY=-3.25 CenterZ=0 NormalX=0 NormalY=0 NormalZ=1 AngleXU=0 Radius=1.6
  constraints (10):
    c: Distance(g0) = 5.25
    c: Coincident(g0,g-3)
    c: PointOnObject(g0,g-3)
    c: Vertical(g1)
    c: DistanceY(g1,g1) = 6.5
    c: Symmetric(g1,g1,g0)
    c: Diameter(g2) = 3.2
    c: Diameter(g3) = 3.2
    c: Coincident(g2,g1)
    c: Coincident(g3,g1)
FEATURE [Sketcher::SketchObject] Sketch032  label="spazio per PILA 18650"
  ArcFitTolerance = 1e-06
  AttachmentSupport = -> [XY_Plane]
  ExternalGeometry = -> [Sketch]
  FullyConstrained = true
  MakeInternals = false
  MapMode = 5
  sketch-geometry (2):
    g0: LineSegment [constr] StartX=-178.142 StartY=-1.74e-14 StartZ=0 EndX=-191.142 EndY=-1.83e-14 EndZ=0
    g1: Circle CenterX=-191.142 CenterY=-1.83e-14 CenterZ=0 NormalX=0 NormalY=0 NormalZ=1 AngleXU=0 Radius=10.5
  constraints (5):
    c: Distance(g0) = 13
    c: Coincident(g0,g-3)
    c: PointOnObject(g0,g-4)
    c: Diameter(g1) = 21
    c: Coincident(g1,g0)
FEATURE [Part::Extrusion] Extrude030  label="Extrude spazio per PILA 18650"
  Base = -> Sketch032
  Dir = (0,0,1)
  DirLink = -> Sketch [Edge45]
  DirMode = 2
  FaceMakerClass = Part::FaceMakerBullseye
  FaceMakerMode = 3
  LengthFwd = 76
  LengthRev = 0
  Placement = pos=(6,0,-72) rot=(0,0,1;0rad)
  Solid = true
  Symmetric = false
FEATURE [Sketcher::SketchObject] Sketch033  label="fermo per scheda micro"
  ArcFitTolerance = 1e-06
  AttachmentSupport = -> [XZ_Plane]
  ExternalGeometry = -> [Sketch]
  FullyConstrained = true
  MakeInternals = false
  MapMode = 5
  Placement = pos=(0,0,0) rot=(1,0,0;1.5708rad)
  sketch-geometry (12):
    g0: LineSegment StartX=-11.6 StartY=6 StartZ=0 EndX=-4 EndY=6 EndZ=0
    g1: LineSegment StartX=-4 StartY=6 StartZ=0 EndX=-4 EndY=36.4 EndZ=0
    g2: LineSegment StartX=-4 StartY=36.4 StartZ=0 EndX=-11.6 EndY=36.4 EndZ=0
    g3: LineSegment StartX=-11.6 StartY=36.4 StartZ=0 EndX=-11.6 EndY=6 EndZ=0
    g4: LineSegment StartX=-80.11 StartY=11.6 StartZ=0 EndX=-70.51 EndY=11.6 EndZ=0
    g5: LineSegment StartX=-70.51 StartY=11.6 StartZ=0 EndX=-70.51 EndY=6 EndZ=0
    g6: LineSegment StartX=-70.51 StartY=6 StartZ=0 EndX=-80.11 EndY=6 EndZ=0
    g7: LineSegment StartX=-80.11 StartY=6 StartZ=0 EndX=-80.11 EndY=11.6 EndZ=0
    g8: LineSegment StartX=-78.51 StartY=36.4 StartZ=0 EndX=-70.51 EndY=36.4 EndZ=0
    g9: LineSegment StartX=-70.51 StartY=36.4 StartZ=0 EndX=-70.51 EndY=30.8 EndZ=0
    g10: LineSegment StartX=-70.51 StartY=30.8 StartZ=0 EndX=-78.51 EndY=30.8 EndZ=0
    g11: LineSegment StartX=-78.51 StartY=30.8 StartZ=0 EndX=-78.51 EndY=36.4 EndZ=0
  constraints (33):
    c: Horizontal(g0)
    c: Coincident(g1,g0)
    c: Coincident(g2,g1)
    c: Horizontal(g2)
    c: Coincident(g3,g2)
    c: Coincident(g3,g0)
    c: Vertical(g3)
    c: DistanceX(g2,g2) = 7.6
    c: Coincident(g1,g-3)
    c: Coincident(g0,g-3)
    c: Horizontal(g4)
    c: Coincident(g5,g4)
    c: Vertical(g5)
    c: Coincident(g6,g5)
    c: Horizontal(g6)
    c: Coincident(g7,g6)
    c: Coincident(g7,g4)
    c: Vertical(g7)
    c: DistanceY(g5,g5) = 5.6
    c: DistanceX(g4,g4) = 9.6
    c: Coincident(g9,g8)
    c: Vertical(g9)
    c: Coincident(g10,g9)
    c: Horizontal(g10)
    c: Coincident(g11,g10)
    c: Coincident(g11,g8)
    c: Vertical(g11)
    c: DistanceY(g9,g9) = 5.6
    c: DistanceX(g10,g10) = 8
    c: Coincident(g4,g-4)
    c: DistanceX(g4,g10) = 1.6
    c: Horizontal(g8)
    c: DistanceY(g8,g1) = 0
FEATURE [Sketcher::SketchObject] Sketch034  label="buchi guida rail"
  ArcFitTolerance = 1e-06
  AttachmentSupport = -> [XY_Plane]
  ExternalGeometry = -> [Sketch]
  FullyConstrained = true
  MakeInternals = false
  MapMode = 5
  sketch-geometry (6):
    g0: LineSegment [constr] StartX=-100.8 StartY=9.1e-15 StartZ=0 EndX=-93.3 EndY=0 EndZ=0
    g1: LineSegment [constr] StartX=-93.3 StartY=0 StartZ=0 EndX=-73.3 EndY=0 EndZ=0
    g2: LineSegment [constr] StartX=-73.3 StartY=0 StartZ=0 EndX=-53.3 EndY=0 EndZ=0
    g3: Circle CenterX=-93.3 CenterY=0 CenterZ=0 NormalX=0 NormalY=0 NormalZ=1 AngleXU=0 Radius=2.5
    g4: Circle CenterX=-73.3 CenterY=0 CenterZ=0 NormalX=0 NormalY=0 NormalZ=1 AngleXU=0 Radius=2.5
    g5: Circle CenterX=-53.3 CenterY=0 CenterZ=0 NormalX=0 NormalY=0 NormalZ=1 AngleXU=0 Radius=2.5
  constraints (15):
    c: Distance(g0) = 7.5
    c: Coincident(g0,g-3)
    c: PointOnObject(g0,g-1)
    c: Distance(g1) = 20
    c: Coincident(g1,g0)
    c: PointOnObject(g1,g-1)
    c: Distance(g2) = 20
    c: Coincident(g2,g1)
    c: PointOnObject(g2,g-1)
    c: Diameter(g3) = 5
    c: Diameter(g4) = 5
    c: Diameter(g5) = 5
    c: Coincident(g3,g0)
    c: Coincident(g4,g1)
    c: Coincident(g5,g2)
FEATURE [Part::Extrusion] Extrude032  label="Extrude buchi guida rail"
  Base = -> Sketch034
  Dir = (0,0,1)
  DirMode = 2
  FaceMakerClass = Part::FaceMakerBullseye
  FaceMakerMode = 3
  LengthFwd = -6.2
  LengthRev = 0
  Placement = pos=(0,0,43.2) rot=(0,0,1;0rad)
  Solid = true
  Symmetric = false
FEATURE [Part::Extrusion] Extrude033  label="Extrude fori superiori per solenoide e oled001"
  Base = -> Sketch030
  Dir = (0,0,1)
  DirMode = 2
  FaceMakerClass = Part::FaceMakerBullseye
  FaceMakerMode = 3
  LengthFwd = -4.8
  LengthRev = 0
  Placement = pos=(0,0,41.2) rot=(0,0,1;0rad)
  Solid = true
  Symmetric = false
FEATURE [Part::Extrusion] Extrude034  label="Extrude fori sotto impugnatura001"
  Base = -> Sketch029
  Dir = (0,0,1)
  DirMode = 2
  FaceMakerClass = Part::FaceMakerBullseye
  FaceMakerMode = 3
  LengthFwd = 5
  LengthRev = 0
  Placement = pos=(0,0,-83) rot=(0,0,1;0rad)
  Solid = true
  Symmetric = false
FEATURE [Part::Extrusion] Extrude035  label="Extrude fori inferiori switch pompa001"
  Base = -> Sketch031
  Dir = (0,0,1)
  DirMode = 2
  FaceMakerClass = Part::FaceMakerBullseye
  FaceMakerMode = 3
  LengthFwd = 4
  LengthRev = 0
  Placement = pos=(0,0,-1.7) rot=(0,0,1;0rad)
  Solid = true
  Symmetric = false
FEATURE [Part::Extrusion] Extrude036  label="Extrude foro sotto posteriore M3x5x007"
  Base = -> Sketch027
  Dir = (0,0,1)
  DirMode = 2
  FaceMakerClass = Part::FaceMakerBullseye
  FaceMakerMode = 3
  LengthFwd = 6.2
  LengthRev = 0
  Placement = pos=(0,0,-9.6) rot=(0,0,1;0rad)
  Solid = true
  Symmetric = false
FEATURE [Part::Extrusion] Extrude037  label="Extrude foro sotto anteriore M3x5x007"
  Base = -> Sketch026
  Dir = (0,0,1)
  DirMode = 2
  FaceMakerClass = Part::FaceMakerBullseye
  FaceMakerMode = 3
  LengthFwd = 6.2
  LengthRev = 0
  Solid = true
  Symmetric = false
FEATURE [Sketcher::SketchObject] Sketch035  label="foro per fissaggio micro"
  ArcFitTolerance = 1e-06
  AttachmentSupport = -> [XZ_Plane]
  ExternalGeometry = -> [Sketch,Sketch033]
  FullyConstrained = true
  MakeInternals = false
  MapMode = 5
  Placement = pos=(0,0,0) rot=(1,0,0;1.5708rad)
  sketch-geometry (3):
    g0: Circle CenterX=-7.8 CenterY=21.2 CenterZ=0 NormalX=0 NormalY=0 NormalZ=1 AngleXU=0 Radius=1.6
    g1: GeomPoint [constr] X=-4 Y=21.2 Z=0
    g2: LineSegment [constr] StartX=-4 StartY=21.2 StartZ=0 EndX=-11.6 EndY=21.2 EndZ=0
  constraints (6):
    c: Diameter(g0) = 3.2
    c: Symmetric(g-3,g-3,g1)
    c: Coincident(g2,g1)
    c: Horizontal(g2)
    c: DistanceX(g-4,g2) = 0
    c: Symmetric(g2,g1,g0)
FEATURE [Part::Extrusion] Extrude038  label="Extrude foro per fissaggio micro"
  Base = -> Sketch035
  Dir = (0,-1,2e-16)
  DirMode = 2
  FaceMakerClass = Part::FaceMakerBullseye
  FaceMakerMode = 3
  LengthFwd = 3
  LengthRev = 0
  Placement = pos=(0,8.6,0) rot=(0,0,1;0rad)
  Solid = true
  Symmetric = false
FEATURE [Sketcher::SketchObject] Sketch036  label="supporto per alimentatore"
  ArcFitTolerance = 1e-06
  AttachmentSupport = -> [XZ_Plane]
  ExternalGeometry = -> [Sketch,Sketch016,Sketch022]
  FullyConstrained = true
  MakeInternals = false
  MapMode = 5
  Placement = pos=(0,0,0) rot=(1,0,0;1.5708rad)
  sketch-geometry (5):
    g0: LineSegment StartX=-211.843 StartY=-50.0944 StartZ=0 EndX=-211.843 EndY=-80.4316 EndZ=0
    g1: LineSegment StartX=-211.843 StartY=-50.0944 StartZ=0 EndX=-207.775 EndY=-41.3701 EndZ=0
    g2: LineSegment [constr] StartX=-209.443 StartY=-50.0944 StartZ=0 EndX=-209.443 EndY=-80.4316 EndZ=0
    g3: LineSegment StartX=-207.775 StartY=-41.3701 StartZ=0 EndX=-207.775 EndY=-80.4316 EndZ=0
    g4: LineSegment StartX=-211.843 StartY=-80.4316 StartZ=0 EndX=-207.775 EndY=-80.4316 EndZ=0
  constraints (15):
    c: Vertical(g0)
    c: Coincident(g1,g0)
    c: Vertical(g2)
    c: Tangent(g2,g-5)
    c: Coincident(g3,g1)
    c: Vertical(g3)
    c: DistanceY(g-3,g3) = -2
    c: Tangent(g1,g-8)
    c: DistanceY(g-3,g0) = -2
    c: Coincident(g4,g0)
    c: Coincident(g4,g3)
    c: Tangent(g0,g-6)
    c: DistanceY(g-3,g2) = -2
    c: DistanceY(g2,g0) = 0
    c: DistanceX(g-3,g3) = 6.8
FEATURE [Part::Extrusion] Extrude039  label="Extrude039 supporto alimentatore"
  Base = -> Sketch036
  Dir = (0,-1,2e-16)
  DirMode = 2
  FaceMakerClass = Part::FaceMakerBullseye
  FaceMakerMode = 3
  LengthFwd = 25.2
  LengthRev = 0
  Solid = true
  Symmetric = true
FEATURE [Sketcher::SketchObject] Sketch037  label="scavo per alimentatore"
  ArcFitTolerance = 1e-06
  AttachmentSupport = -> [XZ_Plane]
  ExternalGeometry = -> [Sketch036]
  FullyConstrained = true
  MakeInternals = false
  MapMode = 5
  Placement = pos=(0,0,0) rot=(1,0,0;1.5708rad)
  sketch-geometry (4):
    g0: LineSegment StartX=-209.575 StartY=-50.4316 StartZ=0 EndX=-209.575 EndY=-80.4316 EndZ=0
    g1: LineSegment StartX=-209.575 StartY=-50.4316 StartZ=0 EndX=-207.775 EndY=-50.4316 EndZ=0
    g2: LineSegment StartX=-207.775 StartY=-50.4316 StartZ=0 EndX=-207.775 EndY=-80.4316 EndZ=0
    g3: LineSegment StartX=-207.775 StartY=-80.4316 StartZ=0 EndX=-209.575 EndY=-80.4316 EndZ=0
  constraints (11):
    c: Vertical(g0)
    c: Coincident(g1,g0)
    c: Horizontal(g1)
    c: Coincident(g2,g1)
    c: Vertical(g2)
    c: Coincident(g3,g2)
    c: Coincident(g3,g0)
    c: Horizontal(g3)
    c: DistanceX(g1,g1) = 1.8
    c: Coincident(g2,g-3)
    c: DistanceY(g2,g2) = 30
FEATURE [Part::Extrusion] Extrude040  label="Extrude040 scavo alimentatore"
  Base = -> Sketch037
  Dir = (0,-1,2e-16)
  DirMode = 2
  FaceMakerClass = Part::FaceMakerBullseye
  FaceMakerMode = 3
  LengthFwd = 19.5
  LengthRev = 0
  Solid = true
  Symmetric = true
FEATURE [Part::Extrusion] Extrude031  label="Extrude fermo per scheda micro"
  Base = -> Sketch033
  Dir = (0,-1,2e-16)
  DirMode = 2
  FaceMakerClass = Part::FaceMakerBullseye
  FaceMakerMode = 3
  LengthFwd = 3
  LengthRev = 0
  Placement = pos=(0,8.6,0) rot=(0,0,1;0rad)
  Solid = true
  Symmetric = false
FEATURE [Sketcher::SketchObject] Sketch038  label="scavo driver solenoide"
  ArcFitTolerance = 1e-06
  AttachmentSupport = -> [XZ_Plane]
  ExternalGeometry = -> [Sketch,Sketch036]
  FullyConstrained = true
  MakeInternals = false
  MapMode = 5
  Placement = pos=(0,0,0) rot=(1,0,0;1.5708rad)
  sketch-geometry (7):
    g0: LineSegment StartX=-192.222 StartY=-8.0175 StartZ=0 EndX=-194.941 EndY=-6.74965 EndZ=0
    g1: LineSegment StartX=-194.941 StartY=-6.74965 StartZ=0 EndX=-212.269 EndY=-43.9083 EndZ=0
    g2: LineSegment StartX=-192.222 StartY=-8.0175 StartZ=0 EndX=-188.779 EndY=-9.62345 EndZ=0
    g3: LineSegment StartX=-188.779 StartY=-9.62345 StartZ=0 EndX=-205.357 EndY=-45.1761 EndZ=0
    g4: LineSegment StartX=-205.357 StartY=-45.1761 StartZ=0 EndX=-209.55 EndY=-45.1761 EndZ=0
    g5: LineSegment [constr] StartX=-212.269 StartY=-43.9083 StartZ=0 EndX=-209.55 EndY=-45.1761 EndZ=0
    g6: LineSegment StartX=-212.269 StartY=-43.9083 StartZ=0 EndX=-209.55 EndY=-45.1761 EndZ=0
  constraints (20):
    c: Coincident(g1,g0)
    c: Coincident(g3,g2)
    c: Coincident(g4,g3)
    c: Distance(g2) = 3.8
    c: Distance(g1) = 41
    c: Coincident(g5,g1)
    c: Distance(g5) = 3
    c: Perpendicular(g5,g-3)
    c: Parallel(g1,g-3)
    c: Perpendicular(g1,g0)
    c: Distance(g0) = 3
    c: Coincident(g6,g1)
    c: Parallel(g3,g-3)
    c: Perpendicular(g2,g3)
    c: Coincident(g2,g0)
    c: Perpendicular(g-4,g4)
    c: PointOnObject(g5,g-3)
    c: Distance(g-3,g5) = 9.6
    c: Coincident(g4,g5)
    c: Coincident(g6,g4)
FEATURE [Part::Extrusion] Extrude041  label="Extrude scavo driver solenoide"
  Base = -> Sketch038
  Dir = (0,-1,2e-16)
  DirMode = 2
  FaceMakerClass = Part::FaceMakerBullseye
  FaceMakerMode = 3
  LengthFwd = 20.6
  LengthRev = 0
  Solid = true
  Symmetric = true
FEATURE [Sketcher::SketchObject] Sketch039  label="scavo per cavo usb per micro"
  ArcFitTolerance = 1e-06
  AttachmentSupport = -> [XZ_Plane]
  ExternalGeometry = -> [Sketch,Sketch016]
  FullyConstrained = true
  MakeInternals = false
  MapMode = 5
  Placement = pos=(0,0,0) rot=(1,0,0;1.5708rad)
  sketch-geometry (4):
    g0: LineSegment StartX=-82.51 StartY=36.4 StartZ=0 EndX=-74.51 EndY=36.4 EndZ=0
    g1: LineSegment StartX=-74.51 StartY=36.4 StartZ=0 EndX=-74.51 EndY=30.8 EndZ=0
    g2: LineSegment StartX=-74.51 StartY=30.8 StartZ=0 EndX=-82.51 EndY=30.8 EndZ=0
    g3: LineSegment StartX=-82.51 StartY=30.8 StartZ=0 EndX=-82.51 EndY=36.4 EndZ=0
  constraints (11):
    c: Coincident(g1,g0)
    c: Vertical(g1)
    c: Coincident(g2,g1)
    c: Horizontal(g2)
    c: Coincident(g3,g2)
    c: Coincident(g3,g0)
    c: Vertical(g3)
    c: Tangent(g0,g-3)
    c: Tangent(g2,g-4)
    c: Tangent(g3,g-4)
    c: Tangent(g1,g-4)
FEATURE [Part::Extrusion] Extrude042  label="Extrude scavo per cavo usb per micro"
  Base = -> Sketch039
  Dir = (0,-1,2e-16)
  DirMode = 2
  FaceMakerClass = Part::FaceMakerBullseye
  FaceMakerMode = 3
  LengthFwd = 11.2
  LengthRev = 0
  Solid = true
  Symmetric = true
FEATURE [Sketcher::SketchObject] Sketch040  label="scavo saldature alimentatore connettore 5v"
  ArcFitTolerance = 1e-06
  AttachmentSupport = -> [XZ_Plane]
  ExternalGeometry = -> [Sketch037]
  FullyConstrained = true
  MakeInternals = false
  MapMode = 5
  Placement = pos=(0,0,0) rot=(1,0,0;1.5708rad)
  sketch-geometry (4):
    g0: LineSegment StartX=-211.175 StartY=-52.4316 StartZ=0 EndX=-211.175 EndY=-56.4316 EndZ=0
    g1: LineSegment StartX=-211.175 StartY=-52.4316 StartZ=0 EndX=-209.575 EndY=-52.4316 EndZ=0
    g2: LineSegment StartX=-209.575 StartY=-52.4316 StartZ=0 EndX=-209.575 EndY=-56.4316 EndZ=0
    g3: LineSegment StartX=-209.575 StartY=-56.4316 StartZ=0 EndX=-211.175 EndY=-56.4316 EndZ=0
  constraints (11):
    c: Vertical(g0)
    c: Coincident(g1,g0)
    c: Horizontal(g1)
    c: Coincident(g2,g1)
    c: Coincident(g3,g2)
    c: Coincident(g3,g0)
    c: Horizontal(g3)
    c: DistanceX(g1,g1) = 1.6
    c: DistanceY(g2,g2) = 4
    c: Tangent(g2,g-3)
    c: DistanceY(g1,g-3) = 2
FEATURE [Part::Extrusion] Extrude043  label="Extrude scavo saldature alimentatore connettore 5v"
  Base = -> Sketch040
  Dir = (0,-1,2e-16)
  DirMode = 2
  FaceMakerClass = Part::FaceMakerBullseye
  FaceMakerMode = 3
  LengthFwd = 8
  LengthRev = 0
  Solid = true
  Symmetric = true
FEATURE [Sketcher::SketchObject] Sketch041  label="scavo saldature alimentatore connettore 5v verticali"
  ArcFitTolerance = 1e-06
  AttachmentSupport = -> [XZ_Plane]
  ExternalGeometry = -> [Sketch037]
  FullyConstrained = true
  MakeInternals = false
  MapMode = 5
  Placement = pos=(0,0,0) rot=(1,0,0;1.5708rad)
  sketch-geometry (4):
    g0: LineSegment StartX=-211.175 StartY=-53.6316 StartZ=0 EndX=-209.575 EndY=-53.6316 EndZ=0
    g1: LineSegment StartX=-209.575 StartY=-53.6316 StartZ=0 EndX=-209.575 EndY=-76.6316 EndZ=0
    g2: LineSegment StartX=-209.575 StartY=-76.6316 StartZ=0 EndX=-211.175 EndY=-76.6316 EndZ=0
    g3: LineSegment StartX=-211.175 StartY=-76.6316 StartZ=0 EndX=-211.175 EndY=-53.6316 EndZ=0
  constraints (11):
    c: Horizontal(g0)
    c: Coincident(g1,g0)
    c: Coincident(g2,g1)
    c: Horizontal(g2)
    c: Coincident(g3,g2)
    c: Coincident(g3,g0)
    c: Vertical(g3)
    c: DistanceY(g3,g3) = 23
    c: DistanceX(g0,g0) = 1.6
    c: Tangent(g1,g-3)
    c: DistanceY(g0,g-3) = 3.2
FEATURE [Part::Extrusion] Extrude044  label="Extrude scavo saldature alimentatore connettore 5v verticali"
  Base = -> Sketch041
  Dir = (0,-1,2e-16)
  DirMode = 2
  FaceMakerClass = Part::FaceMakerBullseye
  FaceMakerMode = 3
  LengthFwd = 3.2
  LengthRev = 0
  Placement = pos=(0,8.3,0) rot=(0,0,1;0rad)
  Solid = true
  Symmetric = false
FEATURE [Sketcher::SketchObject] Sketch042  label="fermi per driver solenoide e alimentatore"
  ArcFitTolerance = 1e-06
  AttachmentSupport = -> [XZ_Plane]
  ExternalGeometry = -> [Sketch036,Sketch037,Sketch,Sketch038]
  FullyConstrained = true
  MakeInternals = false
  MapMode = 5
  Placement = pos=(0,0,0) rot=(1,0,0;1.5708rad)
  sketch-geometry (27):
    g0: LineSegment StartX=-200.506 StartY=-25.7811 StartZ=0 EndX=-201.436 EndY=-27.775 EndZ=0
    g1: LineSegment StartX=-201.436 StartY=-27.775 StartZ=0 EndX=-199.442 EndY=-28.7048 EndZ=0
    g2: LineSegment StartX=-199.442 StartY=-28.7048 StartZ=0 EndX=-198.512 EndY=-26.7109 EndZ=0
    g3: LineSegment StartX=-198.512 StartY=-26.7109 StartZ=0 EndX=-200.506 EndY=-25.7811 EndZ=0
    g4: LineSegment StartX=-201.28 StartY=-23.6549 StartZ=0 EndX=-203.562 EndY=-28.5489 EndZ=0
    g5: LineSegment StartX=-203.562 StartY=-28.5489 StartZ=0 EndX=-200.118 EndY=-30.1549 EndZ=0
    g6: LineSegment StartX=-197.992 StartY=-29.381 StartZ=0 EndX=-197.062 EndY=-27.3871 EndZ=0
    g7: LineSegment StartX=-197.836 StartY=-25.2608 StartZ=0 EndX=-201.28 EndY=-23.6549 EndZ=0
    g8: LineSegment [constr] StartX=-198.668 StartY=-30.8311 StartZ=0 EndX=-197.992 EndY=-29.381 EndZ=0
    g9: LineSegment [constr] StartX=-198.668 StartY=-30.8311 StartZ=0 EndX=-200.118 EndY=-30.1549 EndZ=0
    g10: ArcOfCircle CenterX=-198.512 CenterY=-26.7109 CenterZ=0 NormalX=0 NormalY=0 NormalZ=1 AngleXU=0 Radius=1.6 StartAngle=5.84685 EndAngle=7.41765
    g11: GeomPoint [constr] X=-196.386 Y=-25.937 Z=0
    g12: ArcOfCircle CenterX=-199.442 CenterY=-28.7048 CenterZ=0 NormalX=0 NormalY=0 NormalZ=1 AngleXU=0 Radius=1.6 StartAngle=4.27606 EndAngle=5.84685
    g13: GeomPoint [constr] X=-198.668 Y=-30.8311 Z=0
    g14: LineSegment StartX=-207.775 StartY=-46.8316 StartZ=0 EndX=-207.775 EndY=-50.8316 EndZ=0
    g15: LineSegment StartX=-207.775 StartY=-46.8316 StartZ=0 EndX=-203.775 EndY=-46.8316 EndZ=0
    g16: LineSegment StartX=-203.775 StartY=-46.8316 StartZ=0 EndX=-203.775 EndY=-50.8316 EndZ=0
    g17: LineSegment StartX=-207.775 StartY=-50.8316 StartZ=0 EndX=-203.775 EndY=-50.8316 EndZ=0
    g18: LineSegment StartX=-209.375 StartY=-52.4316 StartZ=0 EndX=-203.775 EndY=-52.4316 EndZ=0
    g19: LineSegment StartX=-202.175 StartY=-50.8316 StartZ=0 EndX=-202.175 EndY=-46.8316 EndZ=0
    g20: LineSegment StartX=-203.775 StartY=-45.2316 StartZ=0 EndX=-209.375 EndY=-45.2316 EndZ=0
    g21: LineSegment StartX=-209.375 StartY=-45.2316 StartZ=0 EndX=-209.375 EndY=-52.4316 EndZ=0
    g22: ArcOfCircle CenterX=-203.775 CenterY=-46.8316 CenterZ=0 NormalX=0 NormalY=0 NormalZ=1 AngleXU=0 Radius=1.6 StartAngle=1.8e-15 EndAngle=1.5708
    g23: GeomPoint [constr] X=-202.175 Y=-45.2316 Z=0
    g24: ArcOfCircle CenterX=-203.775 CenterY=-50.8316 CenterZ=0 NormalX=0 NormalY=0 NormalZ=1 AngleXU=0 Radius=1.6 StartAngle=4.71239 EndAngle=6.28319
    g25: GeomPoint [constr] X=-202.175 Y=-52.4316 Z=0
    g26: LineSegment [constr] StartX=-207.775 StartY=-50.4316 StartZ=0 EndX=-207.775 EndY=-50.8316 EndZ=0
  constraints (69):
    c: Coincident(g1,g0)
    c: Coincident(g2,g1)
    c: Coincident(g3,g2)
    c: Coincident(g3,g0)
    c: Parallel(g0,g2)
    c: Perpendicular(g3,g0)
    c: Perpendicular(g1,g0)
    c: Coincident(g5,g4)
    c: Coincident(g7,g4)
    c: Distance(g3) = 2.2
    c: Distance(g2) = 2.2
    c: Parallel(g6,g2)
    c: Parallel(g6,g4)
    c: Perpendicular(g5,g6)
    c: Perpendicular(g7,g6)
    c: Distance(g13,g11) = 5.4
    c: Distance(g5,g13) = 5.4
    c: Coincident(g9,g8)
    c: Distance(g8) = 1.6
    c: Distance(g9) = 1.6
    c: Perpendicular(g9,g8)
    c: Parallel(g8,g6)
    c: Coincident(g8,g13)
    c: Distance(g8,g1) = 1.6
    c: Distance(g9,g1) = 1.6
    c: Tangent(g0,g-5)
    c: Distance(g0,g-6) = 19.2
    c: PointOnObject(g11,g7)
    c: PointOnObject(g11,g6)
    c: Tangent(g7,g10) = -1.5708
    c: Tangent(g6,g10) = -1.5708
    c: PointOnObject(g13,g5)
    c: Tangent(g5,g12) = -1.5708
    c: Tangent(g6,g12) = -1.5708
    c: Equal(g10,g12)
    c: Coincident(g10,g2)
    c: Vertical(g14)
    c: Coincident(g15,g14)
    c: Horizontal(g15)
    c: Coincident(g16,g15)
    c: Vertical(g16)
    c: Coincident(g17,g14)
    c: Coincident(g17,g16)
    c: Horizontal(g17)
    c: Distance(g16) = 4
    c: Distance(g15) = 4
    c: Horizontal(g18)
    c: Vertical(g19)
    c: Horizontal(g20)
    c: Coincident(g21,g20)
    c: Coincident(g21,g18)
    c: Vertical(g21)
    c: Distance(g20,g23) = 7.2
    c: Distance(g25,g23) = 7.2
    c: DistanceY(g18,g14) = 1.6
    c: DistanceX(g18,g14) = 1.6
    c: PointOnObject(g23,g20)
    c: PointOnObject(g23,g19)
    c: Tangent(g20,g22) = -1.5708
    c: Tangent(g19,g22) = -1.5708
    c: PointOnObject(g25,g19)
    c: Tangent(g18,g24) = -1.5708
    c: Tangent(g19,g24) = -1.5708
    c: Equal(g22,g24)
    c: Coincident(g22,g15)
    c: Vertical(g26)
    c: Distance(g26) = 0.4
    c: Coincident(g26,g-4)
    c: Coincident(g14,g26)
FEATURE [Part::Extrusion] Extrude045  label="Extrude fermi per driver solenoide e alimentatore"
  Base = -> Sketch042
  Dir = (0,-1,2e-16)
  DirMode = 2
  FaceMakerClass = Part::FaceMakerBullseye
  FaceMakerMode = 3
  LengthFwd = 25.2
  LengthRev = 0
  Solid = true
  Symmetric = true
FEATURE [Sketcher::SketchObject] Sketch043  label="scavo pulizia fermo alimentatore"
  ArcFitTolerance = 1e-06
  AttachmentSupport = -> [XZ_Plane]
  ExternalGeometry = -> [Sketch042,Sketch036,Sketch037]
  FullyConstrained = true
  MakeInternals = false
  MapMode = 5
  Placement = pos=(0,0,0) rot=(1,0,0;1.5708rad)
  sketch-geometry (6):
    g0: LineSegment StartX=-209.375 StartY=-52.4316 StartZ=0 EndX=-209.375 EndY=-50.4316 EndZ=0
    g1: LineSegment StartX=-209.375 StartY=-50.4316 StartZ=0 EndX=-207.775 EndY=-50.4316 EndZ=0
    g2: LineSegment StartX=-207.775 StartY=-50.4316 StartZ=0 EndX=-207.775 EndY=-45.2316 EndZ=0
    g3: LineSegment StartX=-207.775 StartY=-45.2316 StartZ=0 EndX=-202.175 EndY=-45.2316 EndZ=0
    g4: LineSegment StartX=-202.175 StartY=-45.2316 StartZ=0 EndX=-202.175 EndY=-52.4316 EndZ=0
    g5: LineSegment StartX=-202.175 StartY=-52.4316 StartZ=0 EndX=-209.375 EndY=-52.4316 EndZ=0
  constraints (13):
    c: Vertical(g0)
    c: Coincident(g1,g0)
    c: Coincident(g2,g1)
    c: Coincident(g3,g2)
    c: Coincident(g4,g3)
    c: Coincident(g5,g4)
    c: Coincident(g5,g0)
    c: Horizontal(g5)
    c: Coincident(g0,g-6)
    c: Tangent(g1,g-8)
    c: Tangent(g2,g-4)
    c: Tangent(g3,g-7)
    c: Tangent(g4,g-3)
FEATURE [Part::Extrusion] Extrude046  label="Extrude scavo pulizia fermo alimentatore"
  Base = -> Sketch043
  Dir = (0,-1,2e-16)
  DirMode = 2
  FaceMakerClass = Part::FaceMakerBullseye
  FaceMakerMode = 3
  LengthFwd = 19.5
  LengthRev = 0
  Solid = true
  Symmetric = true
FEATURE [Sketcher::SketchObject] Sketch044  label="buchini per fissaggio oled"
  ArcFitTolerance = 1e-06
  AttachmentSupport = -> [YZ_Plane]
  ExternalGeometry = -> [Sketch]
  FullyConstrained = true
  MakeInternals = false
  MapMode = 5
  Placement = pos=(0,0,0) rot=(0.57735,0.57735,0.57735;2.0944rad)
  sketch-geometry (5):
    g0: LineSegment [constr] StartX=1.5e-14 StartY=67.3588 StartZ=0 EndX=0 EndY=64.3588 EndZ=0
    g1: LineSegment [constr] StartX=0 StartY=64.3588 StartZ=0 EndX=10.4 EndY=64.3588 EndZ=0
    g2: LineSegment [constr] StartX=0 StartY=64.3588 StartZ=0 EndX=-10.4 EndY=64.3588 EndZ=0
    g3: Circle CenterX=10.4 CenterY=64.3588 CenterZ=0 NormalX=0 NormalY=0 NormalZ=1 AngleXU=0 Radius=1.5
    g4: Circle CenterX=-10.4 CenterY=64.3588 CenterZ=0 NormalX=0 NormalY=0 NormalZ=1 AngleXU=0 Radius=1.5
  constraints (13):
    c: Distance(g0) = 3
    c: PointOnObject(g0,g-2)
    c: Coincident(g1,g0)
    c: Horizontal(g1)
    c: Coincident(g2,g0)
    c: Horizontal(g2)
    c: DistanceX(g1,g1) = 10.4
    c: Coincident(g3,g1)
    c: Diameter(g4) = 3
    c: Coincident(g4,g2)
    c: Coincident(g0,g-7)
    c: Equal(g1,g2)
    c: Equal(g4,g3)
FEATURE [Part::Extrusion] Extrude047  label="Extrude buchini per fissaggio oled"
  Base = -> Sketch044
  Dir = (1,0,0)
  DirMode = 2
  FaceMakerClass = Part::FaceMakerBullseye
  FaceMakerMode = 3
  LengthFwd = 10
  LengthRev = 0
  Placement = pos=(-186,0,0) rot=(0,0,1;0rad)
  Solid = true
  Symmetric = false
FEATURE [Sketcher::SketchObject] Sketch046  label="scavo 5x5 neopixel"
  ArcFitTolerance = 1e-06
  AttachmentSupport = -> [YZ_Plane002]
  FullyConstrained = true
  MakeInternals = false
  MapMode = 5
  Placement = pos=(0,0,0) rot=(0.57735,0.57735,0.57735;2.0944rad)
  sketch-geometry (4):
    g0: LineSegment StartX=-2.7 StartY=2.7 StartZ=0 EndX=2.7 EndY=2.7 EndZ=0
    g1: LineSegment StartX=2.7 StartY=2.7 StartZ=0 EndX=2.7 EndY=-2.7 EndZ=0
    g2: LineSegment StartX=2.7 StartY=-2.7 StartZ=0 EndX=-2.7 EndY=-2.7 EndZ=0
    g3: LineSegment StartX=-2.7 StartY=-2.7 StartZ=0 EndX=-2.7 EndY=2.7 EndZ=0
  constraints (11):
    c: Horizontal(g0)
    c: Coincident(g1,g0)
    c: Vertical(g1)
    c: Coincident(g2,g1)
    c: Horizontal(g2)
    c: Coincident(g3,g2)
    c: Coincident(g3,g0)
    c: Vertical(g3)
    c: DistanceX(g0,g0) = 5.4
    c: DistanceY(g1,g1) = 5.4
    c: Symmetric(g0,g1,g-1)
FEATURE [Sketcher::SketchObject] Sketch047  label="scavo 10x10 neopixel corpo"
  ArcFitTolerance = 1e-06
  AttachmentOffset = pos=(0,0,1) rot=(0,0,1;0rad)
  AttachmentSupport = -> [YZ_Plane002]
  FullyConstrained = true
  MakeInternals = false
  MapMode = 5
  Placement = pos=(1,0,0) rot=(0.57735,0.57735,0.57735;2.0944rad)
  sketch-geometry (4):
    g0: LineSegment StartX=-5 StartY=5.1 StartZ=0 EndX=5 EndY=5.1 EndZ=0
    g1: LineSegment StartX=5 StartY=5.1 StartZ=0 EndX=5 EndY=-5.1 EndZ=0
    g2: LineSegment StartX=5 StartY=-5.1 StartZ=0 EndX=-5 EndY=-5.1 EndZ=0
    g3: LineSegment StartX=-5 StartY=-5.1 StartZ=0 EndX=-5 EndY=5.1 EndZ=0
  constraints (11):
    c: Horizontal(g0)
    c: Coincident(g1,g0)
    c: Vertical(g1)
    c: Coincident(g2,g1)
    c: Horizontal(g2)
    c: Coincident(g3,g2)
    c: Coincident(g3,g0)
    c: Vertical(g3)
    c: DistanceX(g0,g0) = 10
    c: DistanceY(g1,g1) = 10.2
    c: Symmetric(g0,g2,g-1)
FEATURE [Sketcher::SketchObject] Sketch048  label="buco per perno blocco neopixel"
  ArcFitTolerance = 1e-06
  AttachmentSupport = -> [XZ_Plane002]
  FullyConstrained = true
  MakeInternals = false
  MapMode = 5
  Placement = pos=(0,0,0) rot=(1,0,0;1.5708rad)
  sketch-geometry (4):
    g0: LineSegment StartX=3 StartY=1.2 StartZ=0 EndX=3 EndY=-1.2 EndZ=0
    g1: LineSegment StartX=3 StartY=-1.2 StartZ=0 EndX=5.4 EndY=-1.2 EndZ=0
    g2: LineSegment StartX=5.4 StartY=-1.2 StartZ=0 EndX=5.4 EndY=1.2 EndZ=0
    g3: LineSegment StartX=5.4 StartY=1.2 StartZ=0 EndX=3 EndY=1.2 EndZ=0
  constraints (11):
    c: Coincident(g1,g0)
    c: Horizontal(g1)
    c: Coincident(g2,g1)
    c: Vertical(g2)
    c: Coincident(g3,g2)
    c: Coincident(g3,g0)
    c: Horizontal(g3)
    c: DistanceX(g1,g1) = 2.4
    c: DistanceY(g2,g2) = 2.4
    c: Symmetric(g0,g0,g-1)
    c: DistanceX(g-1,g0) = 3
FEATURE [Sketcher::SketchObject] Sketch045  label="blocco principale per neopixel"
  ArcFitTolerance = 1e-06
  AttachmentSupport = -> [XZ_Plane002]
  ExternalGeometry = -> [Sketch048]
  FullyConstrained = true
  MakeInternals = false
  MapMode = 5
  Placement = pos=(0,0,0) rot=(1,0,0;1.5708rad)
  sketch-geometry (6):
    g0: LineSegment StartX=0 StartY=5.1 StartZ=0 EndX=0 EndY=-5.1 EndZ=0
    g1: LineSegment StartX=0 StartY=-5.1 StartZ=0 EndX=3 EndY=-5.1 EndZ=0
    g2: LineSegment StartX=7 StartY=-1.1 StartZ=0 EndX=7 EndY=5.1 EndZ=0
    g3: LineSegment StartX=7 StartY=5.1 StartZ=0 EndX=0 EndY=5.1 EndZ=0
    g4: ArcOfCircle CenterX=3 CenterY=-1.1 CenterZ=0 NormalX=0 NormalY=0 NormalZ=1 AngleXU=0 Radius=4 StartAngle=4.71239 EndAngle=6.28319
    g5: GeomPoint [constr] X=7 Y=-5.1 Z=0
  constraints (15):
    c: Vertical(g0)
    c: Coincident(g1,g0)
    c: Horizontal(g1)
    c: Vertical(g2)
    c: Coincident(g3,g2)
    c: Coincident(g3,g0)
    c: Horizontal(g3)
    c: DistanceY(g0,g0) = 10.2
    c: Symmetric(g0,g0,g-1)
    c: DistanceX(g3,g3) = 7
    c: PointOnObject(g5,g2)
    c: PointOnObject(g5,g1)
    c: Tangent(g2,g4) = -1.5708
    c: Tangent(g1,g4) = -1.5708
    c: DistanceX(g-3,g1) = 0
FEATURE [Sketcher::SketchObject] Sketch049  label="rinforzi esterni per corpo neopoixel"
  ArcFitTolerance = 1e-06
  AttachmentSupport = -> [XZ_Plane002]
  ExternalGeometry = -> [Sketch045]
  FullyConstrained = true
  MakeInternals = false
  MapMode = 5
  Placement = pos=(0,0,0) rot=(1,0,0;1.5708rad)
  sketch-geometry (8):
    g0: LineSegment StartX=1 StartY=-4.1 StartZ=0 EndX=2 EndY=-4.1 EndZ=0
    g1: LineSegment StartX=2 StartY=-4.1 StartZ=0 EndX=2 EndY=-5.1 EndZ=0
    g2: LineSegment StartX=2 StartY=-5.1 StartZ=0 EndX=1 EndY=-5.1 EndZ=0
    g3: LineSegment StartX=1 StartY=-5.1 StartZ=0 EndX=1 EndY=-4.1 EndZ=0
    g4: LineSegment StartX=1 StartY=5.1 StartZ=0 EndX=2 EndY=5.1 EndZ=0
    g5: LineSegment StartX=2 StartY=5.1 StartZ=0 EndX=2 EndY=4.1 EndZ=0
    g6: LineSegment StartX=2 StartY=4.1 StartZ=0 EndX=1 EndY=4.1 EndZ=0
    g7: LineSegment StartX=1 StartY=4.1 StartZ=0 EndX=1 EndY=5.1 EndZ=0
  constraints (24):
    c: Horizontal(g0)
    c: Coincident(g1,g0)
    c: Vertical(g1)
    c: Coincident(g2,g1)
    c: Horizontal(g2)
    c: Coincident(g3,g2)
    c: Coincident(g3,g0)
    c: Vertical(g3)
    c: Horizontal(g4)
    c: Coincident(g5,g4)
    c: Vertical(g5)
    c: Coincident(g6,g5)
    c: Horizontal(g6)
    c: Coincident(g7,g6)
    c: Coincident(g7,g4)
    c: Vertical(g7)
    c: DistanceX(g4,g4) = 1
    c: DistanceY(g5,g5) = 1
    c: DistanceX(g0,g0) = 1
    c: DistanceY(g1,g1) = 1
    c: DistanceX(g-3,g4) = 1
    c: DistanceY(g-3,g4) = 0
    c: DistanceX(g-4,g2) = 1
    c: DistanceY(g2,g-4) = 0
FEATURE [Sketcher::SketchObject] Sketch052  label="scavo saldature driver solenoide"
  ArcFitTolerance = 1e-06
  AttachmentSupport = -> [XZ_Plane]
  ExternalGeometry = -> [Sketch038]
  FullyConstrained = true
  MakeInternals = false
  MapMode = 5
  Placement = pos=(0,0,0) rot=(1,0,0;1.5708rad)
  sketch-geometry (4):
    g0: LineSegment StartX=-195.304 StartY=-6.5806 StartZ=0 EndX=-196.994 EndY=-10.2058 EndZ=0
    g1: LineSegment StartX=-196.994 StartY=-10.2058 StartZ=0 EndX=-196.632 EndY=-10.3749 EndZ=0
    g2: LineSegment StartX=-196.632 StartY=-10.3749 StartZ=0 EndX=-194.941 EndY=-6.74965 EndZ=0
    g3: LineSegment StartX=-194.941 StartY=-6.74965 StartZ=0 EndX=-195.304 EndY=-6.5806 EndZ=0
  constraints (11):
    c: Coincident(g1,g0)
    c: Coincident(g2,g1)
    c: Coincident(g3,g2)
    c: Coincident(g3,g0)
    c: Parallel(g2,g0)
    c: Perpendicular(g2,g3)
    c: Perpendicular(g1,g2,g1) = 1.5708
    c: Parallel(g2,g-3)
    c: Distance(g2) = 4
    c: Distance(g3) = 0.4
    c: Coincident(g2,g-3)
FEATURE [Part::Extrusion] Extrude055  label="Extrude scavo saldature driver solenoide"
  Base = -> Sketch052
  Dir = (0,-1,2e-16)
  DirMode = 2
  FaceMakerClass = Part::FaceMakerBullseye
  FaceMakerMode = 3
  LengthFwd = 6
  LengthRev = 0
  Solid = true
  Symmetric = true
FEATURE [Sketcher::SketchObject] Sketch053  label="scavo saldature rumble"
  ArcFitTolerance = 1e-06
  AttachmentSupport = -> [XZ_Plane]
  ExternalGeometry = -> [Sketch019]
  FullyConstrained = true
  MakeInternals = false
  MapMode = 5
  Placement = pos=(0,0,0) rot=(1,0,0;1.5708rad)
  sketch-geometry (4):
    g0: LineSegment StartX=-169.451 StartY=-56.8615 StartZ=0 EndX=-170.687 EndY=-60.6657 EndZ=0
    g1: LineSegment StartX=-170.687 StartY=-60.6657 StartZ=0 EndX=-169.546 EndY=-61.0365 EndZ=0
    g2: LineSegment StartX=-169.546 StartY=-61.0365 StartZ=0 EndX=-168.31 EndY=-57.2323 EndZ=0
    g3: LineSegment StartX=-168.31 StartY=-57.2323 StartZ=0 EndX=-169.451 EndY=-56.8615 EndZ=0
  constraints (11):
    c: Coincident(g1,g0)
    c: Coincident(g2,g1)
    c: Coincident(g3,g2)
    c: Coincident(g3,g0)
    c: Parallel(g0,g2)
    c: Perpendicular(g3,g0)
    c: Perpendicular(g1,g0)
    c: Parallel(g0,g-3)
    c: Distance(g0) = 4
    c: Coincident(g0,g-3)
    c: Distance(g1) = 1.2
FEATURE [Part::Extrusion] Extrude056  label="Extrude scavo saldature rumble"
  Base = -> Sketch053
  Dir = (0,-1,2e-16)
  DirMode = 2
  FaceMakerClass = Part::FaceMakerBullseye
  FaceMakerMode = 3
  LengthFwd = 8.4
  LengthRev = 0
  Solid = true
  Symmetric = true
FEATURE [Sketcher::SketchObject] Sketch054  label="scavo saldature alimentatore connettore USB"
  ArcFitTolerance = 1e-06
  AttachmentSupport = -> [XZ_Plane]
  ExternalGeometry = -> [Sketch037]
  FullyConstrained = true
  MakeInternals = false
  MapMode = 5
  Placement = pos=(0,0,0) rot=(1,0,0;1.5708rad)
  sketch-geometry (4):
    g0: LineSegment StartX=-209.575 StartY=-80.4316 StartZ=0 EndX=-210.375 EndY=-80.4316 EndZ=0
    g1: LineSegment StartX=-210.375 StartY=-80.4316 StartZ=0 EndX=-210.375 EndY=-72.4316 EndZ=0
    g2: LineSegment StartX=-210.375 StartY=-72.4316 StartZ=0 EndX=-209.575 EndY=-72.4316 EndZ=0
    g3: LineSegment StartX=-209.575 StartY=-72.4316 StartZ=0 EndX=-209.575 EndY=-80.4316 EndZ=0
  constraints (11):
    c: Horizontal(g0)
    c: Coincident(g1,g0)
    c: Vertical(g1)
    c: Coincident(g2,g1)
    c: Horizontal(g2)
    c: Coincident(g3,g2)
    c: Coincident(g3,g0)
    c: Vertical(g3)
    c: DistanceX(g0,g0) = 0.8
    c: DistanceY(g3,g3) = 8
    c: Coincident(g0,g-4)
FEATURE [Part::Extrusion] Extrude057  label="Extrude scavo saldature alimentatore connettore USB"
  Base = -> Sketch054
  Dir = (0,-1,2e-16)
  DirMode = 2
  FaceMakerClass = Part::FaceMakerBullseye
  FaceMakerMode = 3
  LengthFwd = 11
  LengthRev = 0
  Solid = true
  Symmetric = true
FEATURE [Sketcher::SketchObject] Sketch055  label="buco interno per micro switch"
  ArcFitTolerance = 1e-06
  AttachmentSupport = -> [XZ_Plane]
  ExternalGeometry = -> [Sketch]
  FullyConstrained = true
  MakeInternals = false
  MapMode = 5
  Placement = pos=(0,0,0) rot=(1,0,0;1.5708rad)
  sketch-geometry (11):
    g0: LineSegment [constr] StartX=-194.483 StartY=34.2854 StartZ=0 EndX=-196.022 EndY=30.0568 EndZ=0
    g1: LineSegment [constr] StartX=-196.022 StartY=30.0568 StartZ=0 EndX=-197.561 EndY=25.8282 EndZ=0
    g2: LineSegment [constr] StartX=-196.022 StartY=30.0568 StartZ=0 EndX=-194.143 EndY=29.3727 EndZ=0
    g3: LineSegment [constr] StartX=-196.022 StartY=30.0568 StartZ=0 EndX=-197.902 EndY=30.7408 EndZ=0
    g4: LineSegment StartX=-196.362 StartY=34.9694 StartZ=0 EndX=-192.604 EndY=33.6014 EndZ=0
    g5: LineSegment StartX=-199.441 StartY=26.5122 StartZ=0 EndX=-195.682 EndY=25.1441 EndZ=0
    g6: LineSegment StartX=-192.604 StartY=33.6014 StartZ=0 EndX=-195.682 EndY=25.1441 EndZ=0
    g7: LineSegment StartX=-196.362 StartY=34.9694 StartZ=0 EndX=-199.441 EndY=26.5122 EndZ=0
    g8: GeomPoint [constr] X=-187.821 Y=29.2 Z=0
    g9: LineSegment [constr] StartX=-188.505 StartY=27.3206 StartZ=0 EndX=-196.022 EndY=30.0568 EndZ=0
    g10: LineSegment [constr] StartX=-187.821 StartY=29.2 StartZ=0 EndX=-188.505 EndY=27.3206 EndZ=0
  constraints (27):
    c: Coincident(g2,g0)
    c: Parallel(g0,g-3)
    c: Tangent(g1,g0) = -1.5708
    c: Perpendicular(g0,g2)
    c: Tangent(g2,g3)
    c: Distance(g0,g1) = 9
    c: Equal(g0,g1)
    c: Distance(g3,g2) = 4
    c: Equal(g2,g3)
    c: Parallel(g3,g4)
    c: Symmetric(g4,g4,g0)
    c: Parallel(g6,g1)
    c: Parallel(g7,g1)
    c: Symmetric(g6,g6,g2)
    c: Symmetric(g5,g5,g1)
    c: Symmetric(g7,g7,g3)
    c: Coincident(g7,g4)
    c: Coincident(g6,g4)
    c: Coincident(g5,g6)
    c: Symmetric(g-3,g-3,g8)
    c: Perpendicular(g-3,g9)
    c: Distance(g9) = 8
    c: Coincident(g3,g9)
    c: Coincident(g10,g8)
    c: Parallel(g10,g-3)
    c: Distance(g10) = 2
    c: Coincident(g10,g9)
FEATURE [Sketcher::SketchObject] Sketch056  label="buco esterno per micro switch"
  ArcFitTolerance = 1e-06
  AttachmentSupport = -> [XZ_Plane]
  ExternalGeometry = -> [Sketch055]
  FullyConstrained = true
  MakeInternals = false
  MapMode = 5
  Placement = pos=(0,0,0) rot=(1,0,0;1.5708rad)
  sketch-geometry (17):
    g0: GeomPoint [constr] X=-194.143 Y=29.3727 Z=0
    g1: GeomPoint [constr] X=-194.483 Y=34.2854 Z=0
    g2: GeomPoint [constr] X=-197.902 Y=30.7408 Z=0
    g3: GeomPoint [constr] X=-197.561 Y=25.8282 Z=0
    g4: GeomPoint [constr] X=-196.022 Y=30.0568 Z=0
    g5: LineSegment [constr] StartX=-194.483 StartY=34.2854 StartZ=0 EndX=-196.022 EndY=30.0568 EndZ=0
    g6: LineSegment [constr] StartX=-196.022 StartY=30.0568 StartZ=0 EndX=-197.561 EndY=25.8282 EndZ=0
    g7: LineSegment [constr] StartX=-197.902 StartY=30.7408 StartZ=0 EndX=-196.022 EndY=30.0568 EndZ=0
    g8: LineSegment [constr] StartX=-196.022 StartY=30.0568 StartZ=0 EndX=-194.143 EndY=29.3727 EndZ=0
    g9: LineSegment [constr] StartX=-195.338 StartY=31.9362 StartZ=0 EndX=-196.022 EndY=30.0568 EndZ=0
    g10: LineSegment [constr] StartX=-196.022 StartY=30.0568 StartZ=0 EndX=-196.706 EndY=28.1774 EndZ=0
    g11: LineSegment [constr] StartX=-196.022 StartY=30.0568 StartZ=0 EndX=-196.821 EndY=30.3475 EndZ=0
    g12: LineSegment [constr] StartX=-196.022 StartY=30.0568 StartZ=0 EndX=-195.223 EndY=29.7661 EndZ=0
    g13: LineSegment StartX=-194.539 StartY=31.6454 StartZ=0 EndX=-195.907 EndY=27.8867 EndZ=0
    g14: LineSegment StartX=-196.137 StartY=32.2269 StartZ=0 EndX=-197.505 EndY=28.4681 EndZ=0
    g15: LineSegment StartX=-196.137 StartY=32.2269 StartZ=0 EndX=-194.539 EndY=31.6454 EndZ=0
    g16: LineSegment StartX=-197.505 StartY=28.4681 StartZ=0 EndX=-195.907 EndY=27.8867 EndZ=0
  constraints (34):
    c: Symmetric(g-5,g-5,g1)
    c: Symmetric(g-5,g-6,g0)
    c: Symmetric(g-6,g-6,g3)
    c: Symmetric(g-5,g-6,g2)
    c: Coincident(g5,g1)
    c: Coincident(g5,g4)
    c: Coincident(g6,g4)
    c: Coincident(g6,g3)
    c: Equal(g5,g6)
    c: Coincident(g7,g2)
    c: Coincident(g7,g4)
    c: Coincident(g8,g4)
    c: Coincident(g8,g0)
    c: Equal(g7,g8)
    c: Coincident(g11,g9)
    c: Coincident(g12,g9)
    c: Tangent(g10,g9) = -1.5708
    c: Perpendicular(g11,g9)
    c: Parallel(g9,g-4)
    c: Equal(g9,g10)
    c: Parallel(g12,g11)
    c: Equal(g11,g12)
    c: Distance(g11,g12) = 1.7
    c: Distance(g9,g10) = 4
    c: Symmetric(g13,g13,g12)
    c: Parallel(g13,g9)
    c: Symmetric(g14,g14,g11)
    c: Symmetric(g15,g15,g9)
    c: Parallel(g15,g11)
    c: Symmetric(g16,g16,g10)
    c: Coincident(g16,g14)
    c: Coincident(g15,g14)
    c: Coincident(g13,g15)
    c: Coincident(g9,g4)
FEATURE [Sketcher::SketchObject] Sketch057  label="buco interno per SWITCH"
  ArcFitTolerance = 1e-06
  AttachmentSupport = -> [XZ_Plane]
  ExternalGeometry = -> [Sketch]
  FullyConstrained = true
  MakeInternals = false
  MapMode = 5
  Placement = pos=(0,0,0) rot=(1,0,0;1.5708rad)
  sketch-geometry (10):
    g0: GeomPoint [constr] X=-187.821 Y=29.2 Z=0
    g1: LineSegment [constr] StartX=-188.505 StartY=27.3206 StartZ=0 EndX=-193.203 EndY=29.0307 EndZ=0
    g2: LineSegment [constr] StartX=-190.809 StartY=35.6086 StartZ=0 EndX=-195.597 EndY=22.4529 EndZ=0
    g3: GeomPoint [constr] X=-193.203 Y=29.0307 Z=0
    g4: LineSegment [constr] StartX=-196.492 StartY=30.2278 StartZ=0 EndX=-189.914 EndY=27.8336 EndZ=0
    g5: LineSegment StartX=-194.098 StartY=36.8056 StartZ=0 EndX=-187.52 EndY=34.4115 EndZ=0
    g6: LineSegment StartX=-194.098 StartY=36.8056 StartZ=0 EndX=-198.886 EndY=23.6499 EndZ=0
    g7: LineSegment StartX=-187.52 StartY=34.4115 StartZ=0 EndX=-192.308 EndY=21.2558 EndZ=0
    g8: LineSegment StartX=-198.886 StartY=23.6499 StartZ=0 EndX=-192.308 EndY=21.2558 EndZ=0
    g9: LineSegment [constr] StartX=-187.821 StartY=29.2 StartZ=0 EndX=-188.505 EndY=27.3206 EndZ=0
  constraints (23):
    c: Symmetric(g-3,g-3,g0)
    c: Perpendicular(g1,g-3)
    c: Parallel(g2,g-3)
    c: Symmetric(g2,g2,g3)
    c: Perpendicular(g2,g4)
    c: Symmetric(g4,g4,g3)
    c: Distance(g2) = 14
    c: Distance(g4) = 7
    c: Distance(g1) = 5
    c: Parallel(g5,g4)
    c: Parallel(g7,g2)
    c: Symmetric(g5,g5,g2)
    c: Symmetric(g6,g6,g4)
    c: Symmetric(g7,g7,g4)
    c: Symmetric(g8,g8,g2)
    c: Coincident(g6,g5)
    c: Coincident(g7,g5)
    c: Coincident(g8,g7)
    c: Coincident(g3,g1)
    c: Coincident(g9,g0)
    c: Parallel(g9,g-3)
    c: Distance(g9) = 2
    c: Coincident(g1,g9)
FEATURE [Sketcher::SketchObject] Sketch058  label="buco esterno per SWITCH"
  ArcFitTolerance = 1e-06
  AttachmentSupport = -> [XZ_Plane]
  ExternalGeometry = -> [Sketch057]
  FullyConstrained = true
  MakeInternals = false
  MapMode = 5
  Placement = pos=(0,0,0) rot=(1,0,0;1.5708rad)
  sketch-geometry (12):
    g0: GeomPoint [constr] X=-190.809 Y=35.6086 Z=0
    g1: GeomPoint [constr] X=-196.492 Y=30.2278 Z=0
    g2: GeomPoint [constr] X=-189.914 Y=27.8336 Z=0
    g3: GeomPoint [constr] X=-195.597 Y=22.4529 Z=0
    g4: GeomPoint [constr] X=-193.203 Y=29.0307 Z=0
    g5: LineSegment [constr] StartX=-192.006 StartY=32.3196 StartZ=0 EndX=-194.4 EndY=25.7418 EndZ=0
    g6: GeomPoint [constr] X=-193.203 Y=29.0307 Z=0
    g7: LineSegment [constr] StartX=-195.082 StartY=29.7148 StartZ=0 EndX=-191.324 EndY=28.3467 EndZ=0
    g8: LineSegment StartX=-193.885 StartY=33.0037 StartZ=0 EndX=-190.127 EndY=31.6356 EndZ=0
    g9: LineSegment StartX=-190.127 StartY=31.6356 StartZ=0 EndX=-192.521 EndY=25.0578 EndZ=0
    g10: LineSegment StartX=-196.28 StartY=26.4258 StartZ=0 EndX=-192.521 EndY=25.0578 EndZ=0
    g11: LineSegment StartX=-193.885 StartY=33.0037 StartZ=0 EndX=-196.28 EndY=26.4258 EndZ=0
  constraints (21):
    c: Symmetric(g-6,g-6,g3)
    c: Symmetric(g-4,g-6,g2)
    c: Symmetric(g-5,g-4,g0)
    c: Symmetric(g-5,g-6,g1)
    c: Symmetric(g1,g2,g4)
    c: Parallel(g5,g-4)
    c: Symmetric(g5,g5,g6)
    c: Perpendicular(g7,g5)
    c: Symmetric(g7,g7,g6)
    c: Distance(g5) = 7
    c: Distance(g7) = 4
    c: Parallel(g8,g7)
    c: Parallel(g11,g5)
    c: Symmetric(g8,g8,g5)
    c: Symmetric(g9,g9,g7)
    c: Symmetric(g10,g10,g5)
    c: Symmetric(g11,g11,g7)
    c: Coincident(g11,g8)
    c: Coincident(g9,g8)
    c: Coincident(g9,g10)
    c: Coincident(g6,g4)
FEATURE [Part::Extrusion] Extrude060  label="Extrude buco interno per SWITCH destro"
  Base = -> Sketch057
  Dir = (0,-1,2e-16)
  DirMode = 2
  FaceMakerClass = Part::FaceMakerBullseye
  FaceMakerMode = 3
  LengthFwd = 13.2
  LengthRev = 0
  Placement = pos=(0,2.6,0) rot=(0,0,1;0rad)
  Solid = true
  Symmetric = false
FEATURE [Part::Extrusion] Extrude061  label="Extrude buco esterno per SWITCH destro"
  Base = -> Sketch058
  Dir = (0,-1,2e-16)
  DirMode = 2
  FaceMakerClass = Part::FaceMakerBullseye
  FaceMakerMode = 3
  LengthFwd = 2
  LengthRev = 0
  Placement = pos=(0,-10.6,0) rot=(0,0,1;0rad)
  Solid = true
  Symmetric = false
FEATURE [Sketcher::SketchObject] Sketch059  label="buco per spazio introduzione SWITCH"
  ArcFitTolerance = 1e-06
  AttachmentSupport = -> [XZ_Plane]
  ExternalGeometry = -> [Sketch057,Sketch010]
  FullyConstrained = true
  MakeInternals = false
  MapMode = 5
  Placement = pos=(0,0,0) rot=(1,0,0;1.5708rad)
  sketch-geometry (8):
    g0: LineSegment [constr] StartX=-201.368 StartY=36.3521 StartZ=0 EndX=-195.094 EndY=34.0687 EndZ=0
    g1: LineSegment [constr] StartX=-194.098 StartY=36.8056 StartZ=0 EndX=-195.094 EndY=34.0687 EndZ=0
    g2: LineSegment StartX=-198.658 StartY=24.2771 StartZ=0 EndX=-199.654 EndY=21.5401 EndZ=0
    g3: LineSegment StartX=-199.654 StartY=21.5401 StartZ=0 EndX=-181.196 EndY=14.822 EndZ=0
    g4: LineSegment StartX=-181.196 StartY=14.822 StartZ=0 EndX=-180.2 EndY=17.559 EndZ=0
    g5: LineSegment StartX=-180.2 StartY=17.559 StartZ=0 EndX=-198.658 EndY=24.2771 EndZ=0
    g6: LineSegment [constr] StartX=-204.932 StartY=26.5605 StartZ=0 EndX=-198.658 EndY=24.2771 EndZ=0
    g7: LineSegment [constr] StartX=-198.658 StartY=24.2771 StartZ=0 EndX=-199.654 EndY=21.5401 EndZ=0
  constraints (20):
    c: Parallel(g1,g-3)
    c: Parallel(g0,g-4)
    c: Coincident(g0,g-4)
    c: Coincident(g1,g-3)
    c: Coincident(g0,g1)
    c: Coincident(g3,g2)
    c: Coincident(g4,g3)
    c: Coincident(g5,g4)
    c: Coincident(g5,g2)
    c: Parallel(g5,g-5)
    c: Parallel(g3,g-5)
    c: Parallel(g4,g-6)
    c: DistanceX(g-6,g4) = 0
    c: Coincident(g6,g-5)
    c: Equal(g6,g0)
    c: Coincident(g7,g6)
    c: Equal(g7,g1)
    c: Tangent(g7,g-3)
    c: Coincident(g2,g6)
    c: Coincident(g2,g7)
FEATURE [Part::Extrusion] Extrude062  label="Extrude buco per spazio introduzione SWITCH"
  Base = -> Sketch059
  Dir = (0,-1,2e-16)
  DirMode = 2
  FaceMakerClass = Part::FaceMakerBullseye
  FaceMakerMode = 3
  LengthFwd = 13.2
  LengthRev = 0
  Solid = true
  Symmetric = true
FEATURE [Part::Extrusion] Extrude063  label="Extrude buco interno per SWITCH sinistro"
  Base = -> Sketch057
  Dir = (0,-1,2e-16)
  DirMode = 2
  FaceMakerClass = Part::FaceMakerBullseye
  FaceMakerMode = 3
  LengthFwd = 13.2
  LengthRev = 0
  Placement = pos=(0,10.6,0) rot=(0,0,1;0rad)
  Solid = true
  Symmetric = false
FEATURE [Part::Extrusion] Extrude064  label="Extrude buco esterno per SWITCH sinistro"
  Base = -> Sketch058
  Dir = (0,-1,2e-16)
  DirMode = 2
  FaceMakerClass = Part::FaceMakerBullseye
  FaceMakerMode = 3
  LengthFwd = 2
  LengthRev = 0
  Placement = pos=(0,12.6,0) rot=(0,0,1;0rad)
  Solid = true
  Symmetric = false
FEATURE [Sketcher::SketchObject] Sketch061  label="struttura esterna blocco switch"
  ArcFitTolerance = 1e-06
  AttachmentSupport = -> [XZ_Plane003]
  FullyConstrained = true
  MakeInternals = false
  MapMode = 5
  Placement = pos=(0,0,0) rot=(1,0,0;1.5708rad)
  sketch-geometry (5):
    g0: LineSegment StartX=-1 StartY=-5.1 StartZ=0 EndX=1 EndY=-5.1 EndZ=0
    g1: LineSegment StartX=1 StartY=-5.1 StartZ=0 EndX=1 EndY=5.1 EndZ=0
    g2: LineSegment StartX=1 StartY=5.1 StartZ=0 EndX=-1 EndY=5.1 EndZ=0
    g3: LineSegment StartX=-1 StartY=5.1 StartZ=0 EndX=-1 EndY=-5.1 EndZ=0
    g4: GeomPoint [constr] X=0 Y=0 Z=0
  constraints (12):
    c: Coincident(g0,g1)
    c: Coincident(g1,g2)
    c: Coincident(g2,g3)
    c: Coincident(g3,g0)
    c: Horizontal(g0)
    c: Horizontal(g2)
    c: Vertical(g1)
    c: Vertical(g3)
    c: Symmetric(g2,g0,g4)
    c: Distance(g1,g3) = 2
    c: Distance(g0,g2) = 10.2
    c: Coincident(g4,g-1)
FEATURE [Sketcher::SketchObject] Sketch062  label="struttura interna blocco switch"
  ArcFitTolerance = 1e-06
  AttachmentSupport = -> [XZ_Plane003]
  ExternalGeometry = -> [Sketch061]
  FullyConstrained = true
  MakeInternals = false
  MapMode = 5
  Placement = pos=(0,0,0) rot=(1,0,0;1.5708rad)
  sketch-geometry (5):
    g0: LineSegment StartX=-1 StartY=3.1 StartZ=0 EndX=-1 EndY=-3.1 EndZ=0
    g1: LineSegment StartX=-1 StartY=-3.1 StartZ=0 EndX=1 EndY=-3.1 EndZ=0
    g2: LineSegment StartX=1 StartY=-3.1 StartZ=0 EndX=1 EndY=3.1 EndZ=0
    g3: LineSegment StartX=1 StartY=3.1 StartZ=0 EndX=-1 EndY=3.1 EndZ=0
    g4: GeomPoint [constr] X=0 Y=0 Z=0
  constraints (12):
    c: Coincident(g0,g1)
    c: Coincident(g1,g2)
    c: Coincident(g2,g3)
    c: Coincident(g3,g0)
    c: Vertical(g0)
    c: Vertical(g2)
    c: Horizontal(g1)
    c: Horizontal(g3)
    c: Symmetric(g2,g0,g4)
    c: Coincident(g4,g-1)
    c: Distance(g0) = 6.2
    c: Equal(g3,g-3)
FEATURE [Sketcher::SketchObject] Sketch063  label="blocchi tra switch"
  ArcFitTolerance = 1e-06
  AttachmentSupport = -> [XZ_Plane003]
  ExternalGeometry = -> [Sketch061,Sketch062]
  FullyConstrained = true
  MakeInternals = false
  MapMode = 5
  Placement = pos=(0,0,0) rot=(1,0,0;1.5708rad)
  sketch-geometry (8):
    g0: LineSegment StartX=-3 StartY=5.1 StartZ=0 EndX=-1 EndY=5.1 EndZ=0
    g1: LineSegment StartX=-1 StartY=5.1 StartZ=0 EndX=-1 EndY=3.1 EndZ=0
    g2: LineSegment StartX=-1 StartY=3.1 StartZ=0 EndX=-3 EndY=3.1 EndZ=0
    g3: LineSegment StartX=-3 StartY=3.1 StartZ=0 EndX=-3 EndY=5.1 EndZ=0
    g4: LineSegment StartX=-3 StartY=-3.1 StartZ=0 EndX=-1 EndY=-3.1 EndZ=0
    g5: LineSegment StartX=-1 StartY=-3.1 StartZ=0 EndX=-1 EndY=-5.1 EndZ=0
    g6: LineSegment StartX=-1 StartY=-5.1 StartZ=0 EndX=-3 EndY=-5.1 EndZ=0
    g7: LineSegment StartX=-3 StartY=-5.1 StartZ=0 EndX=-3 EndY=-3.1 EndZ=0
  constraints (20):
    c: Horizontal(g0)
    c: Coincident(g1,g0)
    c: Coincident(g2,g1)
    c: Horizontal(g2)
    c: Coincident(g3,g2)
    c: Coincident(g3,g0)
    c: Vertical(g3)
    c: Horizontal(g4)
    c: Coincident(g5,g4)
    c: Coincident(g6,g5)
    c: Horizontal(g6)
    c: Coincident(g7,g6)
    c: Coincident(g7,g4)
    c: Vertical(g7)
    c: Coincident(g0,g-4)
    c: Coincident(g1,g-5)
    c: Coincident(g4,g-6)
    c: Coincident(g5,g-7)
    c: Distance(g0) = 2
    c: Distance(g4) = 2
FEATURE [Sketcher::SketchObject] Sketch066  label="piano per rampino"
  ArcFitTolerance = 1e-06
  AttachmentSupport = -> [XZ_Plane002]
  ExternalGeometry = -> [Sketch045]
  FullyConstrained = true
  MakeInternals = false
  MapMode = 5
  Placement = pos=(0,0,0) rot=(1,0,0;1.5708rad)
  sketch-geometry (4):
    g0: LineSegment StartX=5.4 StartY=5.1 StartZ=0 EndX=5.4 EndY=3.9 EndZ=0
    g1: LineSegment StartX=5.4 StartY=3.9 StartZ=0 EndX=7 EndY=3.9 EndZ=0
    g2: LineSegment StartX=7 StartY=3.9 StartZ=0 EndX=7 EndY=5.1 EndZ=0
    g3: LineSegment StartX=7 StartY=5.1 StartZ=0 EndX=5.4 EndY=5.1 EndZ=0
  constraints (11):
    c: Coincident(g0,g1)
    c: Coincident(g1,g2)
    c: Coincident(g2,g3)
    c: Coincident(g3,g0)
    c: Vertical(g0)
    c: Vertical(g2)
    c: Horizontal(g1)
    c: Horizontal(g3)
    c: Distance(g0,g2) = 1.6
    c: Distance(g1,g3) = 1.2
    c: Coincident(g2,g-3)
FEATURE [Sketcher::SketchObject] Sketch064  label="rampini_per_serraggio_struttura"
  ArcFitTolerance = 1e-06
  AttachmentSupport = -> [XZ_Plane002]
  ExternalGeometry = -> [Sketch066,Sketch045]
  FullyConstrained = true
  MakeInternals = false
  MapMode = 5
  Placement = pos=(0,0,0) rot=(1,0,0;1.5708rad)
  sketch-geometry (7):
    g0: LineSegment StartX=7 StartY=5.1 StartZ=0 EndX=7 EndY=3.9 EndZ=0
    g1: LineSegment StartX=7 StartY=3.9 StartZ=0 EndX=9 EndY=3.9 EndZ=0
    g2: LineSegment StartX=7 StartY=5.1 StartZ=0 EndX=7 EndY=5.1 EndZ=0
    g3: LineSegment StartX=7 StartY=5.1 StartZ=0 EndX=7 EndY=7.5 EndZ=0
    g4: LineSegment StartX=9 StartY=5.1 StartZ=0 EndX=9 EndY=3.9 EndZ=0
    g5: LineSegment StartX=7 StartY=7.5 StartZ=0 EndX=9 EndY=7.5 EndZ=0
    g6: LineSegment StartX=9 StartY=7.5 StartZ=0 EndX=9 EndY=5.1 EndZ=0
  constraints (20):
    c: Vertical(g0)
    c: Coincident(g1,g0)
    c: Horizontal(g1)
    c: Coincident(g2,g0)
    c: Horizontal(g2)
    c: Coincident(g3,g2)
    c: Vertical(g3)
    c: Coincident(g5,g3)
    c: Coincident(g4,g6)
    c: Coincident(g4,g1)
    c: Vertical(g4)
    c: Coincident(g0,g-3)
    c: DistanceY(g-4,g3) = 2.4
    c: DistanceX(g1,g1) = 2
    c: DistanceY(g2,g6) = 0
    c: DistanceX(g2,g2) = 0
    c: DistanceY(g0,g0) = 1.2
    c: Coincident(g5,g6)
    c: Horizontal(g5)
    c: Vertical(g6)
FEATURE [Sketcher::SketchObject] Sketch067  label="perno per blocco switch"
  ArcFitTolerance = 1e-06
  AttachmentSupport = -> [XZ_Plane]
  ExternalGeometry = -> [Sketch,Sketch010]
  FullyConstrained = true
  MakeInternals = false
  MapMode = 5
  Placement = pos=(0,0,0) rot=(1,0,0;1.5708rad)
  sketch-geometry (14):
    g0: LineSegment StartX=-191.073 StartY=24.9429 StartZ=0 EndX=-185.81 EndY=23.0276 EndZ=0
    g1: LineSegment StartX=-183.76 StartY=23.9839 StartZ=0 EndX=-182.392 EndY=27.7427 EndZ=0
    g2: LineSegment StartX=-183.348 StartY=29.7934 StartZ=0 EndX=-188.61 EndY=31.7087 EndZ=0
    g3: LineSegment StartX=-188.61 StartY=31.7087 StartZ=0 EndX=-191.073 EndY=24.9429 EndZ=0
    g4: GeomPoint [constr] X=-186.459 Y=27.0946 Z=0
    g5: LineSegment StartX=-189.022 StartY=25.8992 StartZ=0 EndX=-185.263 EndY=24.5311 EndZ=0
    g6: LineSegment StartX=-185.263 StartY=24.5311 StartZ=0 EndX=-183.895 EndY=28.2899 EndZ=0
    g7: LineSegment StartX=-183.895 StartY=28.2899 StartZ=0 EndX=-187.654 EndY=29.658 EndZ=0
    g8: LineSegment StartX=-187.654 StartY=29.658 StartZ=0 EndX=-189.022 EndY=25.8992 EndZ=0
    g9: GeomPoint [constr] X=-186.459 Y=27.0946 Z=0
    g10: ArcOfCircle CenterX=-185.263 CenterY=24.5311 CenterZ=0 NormalX=0 NormalY=0 NormalZ=1 AngleXU=0 Radius=1.6 StartAngle=4.36332 EndAngle=5.93412
    g11: GeomPoint [constr] X=-184.307 Y=22.4804 Z=0
    g12: ArcOfCircle CenterX=-183.895 CenterY=28.2899 CenterZ=0 NormalX=0 NormalY=0 NormalZ=1 AngleXU=0 Radius=1.6 StartAngle=5.93412 EndAngle=7.50492
    g13: GeomPoint [constr] X=-181.844 Y=29.2462 Z=0
  constraints (30):
    c: Coincident(g2,g3)
    c: Coincident(g3,g0)
    c: Symmetric(g13,g0,g4)
    c: Distance(g11,g3) = 7.2
    c: Distance(g0,g2) = 7.2
    c: Parallel(g3,g1)
    c: Parallel(g2,g0)
    c: Perpendicular(g2,g3)
    c: Coincident(g5,g6)
    c: Coincident(g6,g7)
    c: Coincident(g7,g8)
    c: Coincident(g8,g5)
    c: Symmetric(g7,g5,g9)
    c: Distance(g6,g8) = 4
    c: Distance(g5,g7) = 4
    c: Coincident(g9,g4)
    c: Parallel(g8,g6)
    c: Parallel(g7,g5)
    c: Perpendicular(g7,g8)
    c: Tangent(g8,g-3)
    c: Tangent(g2,g-4)
    c: PointOnObject(g11,g1)
    c: PointOnObject(g11,g0)
    c: Tangent(g1,g10) = -1.5708
    c: Tangent(g0,g10) = -1.5708
    c: PointOnObject(g13,g1)
    c: Tangent(g1,g12) = -1.5708
    c: Tangent(g2,g12) = -1.5708
    c: Equal(g10,g12)
    c: Coincident(g10,g5)
FEATURE [Part::Extrusion] Extrude072  label="Extrude perno per blocco switch"
  Base = -> Sketch067
  Dir = (0,-1,2e-16)
  DirMode = 2
  FaceMakerClass = Part::FaceMakerBullseye
  FaceMakerMode = 3
  LengthFwd = 25.2
  LengthRev = 0
  Solid = true
  Symmetric = true
FEATURE [Part::MultiFuse] Fusion
  Refine = true
  Shapes = -> [Extrude,Sweep,Extrude007,Extrude011,Extrude005,Extrude012,Extrude013,Extrude016,Extrude031,Extrude039,Extrude045,Extrude072]
FEATURE [Part::Cut] Cut
  Base = -> Fusion
  Refine = true
  Tool = -> Extrude001
FEATURE [Part::Cut] Cut001
  Base = -> Cut
  Refine = true
  Tool = -> Extrude004
FEATURE [Part::Cut] Cut002
  Base = -> Cut001
  Refine = true
  Tool = -> Extrude006
FEATURE [Part::Cut] Cut003
  Base = -> Cut002
  Refine = true
  Tool = -> Extrude008
FEATURE [Part::Cut] Cut004
  Base = -> Cut003
  Refine = true
  Tool = -> Extrude009
FEATURE [Part::Cut] Cut005
  Base = -> Cut004
  Refine = true
  Tool = -> Extrude010
FEATURE [Part::Cut] Cut006
  Base = -> Cut005
  Refine = true
  Tool = -> Extrude014
FEATURE [Part::Cut] Cut007
  Base = -> Cut006
  Refine = true
  Tool = -> Extrude015
FEATURE [Part::Cut] Cut008
  Base = -> Cut007
  Refine = true
  Tool = -> Extrude018
FEATURE [Part::Cut] Cut009
  Base = -> Cut008
  Refine = true
  Tool = -> Extrude019
FEATURE [Part::Cut] Cut010
  Base = -> Cut009
  Refine = true
  Tool = -> Extrude020
FEATURE [Part::Cut] Cut011
  Base = -> Cut010
  Refine = true
  Tool = -> Extrude021
FEATURE [Part::Cut] Cut012
  Base = -> Cut011
  Refine = true
  Tool = -> Extrude022
FEATURE [Part::Cut] Cut013
  Base = -> Cut012
  Refine = true
  Tool = -> Extrude023
FEATURE [Part::Cut] Cut014
  Base = -> Cut013
  Refine = true
  Tool = -> Extrude032
FEATURE [Part::Cut] Cut015
  Base = -> Cut014
  Refine = true
  Tool = -> Extrude033
FEATURE [Part::Cut] Cut016
  Base = -> Cut015
  Refine = true
  Tool = -> Extrude034
FEATURE [Part::Cut] Cut017
  Base = -> Cut016
  Refine = true
  Tool = -> Extrude035
FEATURE [Part::Cut] Cut018
  Base = -> Cut017
  Refine = true
  Tool = -> Extrude036
FEATURE [Part::Cut] Cut019
  Base = -> Cut018
  Refine = true
  Tool = -> Extrude037
FEATURE [Part::Cut] Cut020
  Base = -> Cut019
  Refine = true
  Tool = -> Extrude030
FEATURE [Part::Cut] Cut022
  Base = -> Cut020
  Refine = true
  Tool = -> Extrude038
FEATURE [Part::Cut] Cut023
  Base = -> Cut022
  Refine = true
  Tool = -> Extrude041
FEATURE [Part::Cut] Cut024
  Base = -> Cut023
  Refine = true
  Tool = -> Extrude040
FEATURE [Part::Cut] Cut025
  Base = -> Cut024
  Refine = true
  Tool = -> Extrude042
FEATURE [Part::Cut] Cut026
  Base = -> Cut025
  Refine = true
  Tool = -> Extrude043
FEATURE [Part::Cut] Cut027
  Base = -> Cut026
  Refine = true
  Tool = -> Extrude044
FEATURE [Part::Cut] Cut028
  Base = -> Cut027
  Refine = true
  Tool = -> Extrude046
FEATURE [Part::Cut] Cut029
  Base = -> Cut028
  Refine = true
  Tool = -> Extrude047
FEATURE [Part::Cut] Cut033
  Base = -> Cut029
  Refine = true
  Tool = -> Extrude055
FEATURE [Part::Cut] Cut034
  Base = -> Cut033
  Refine = true
  Tool = -> Extrude056
FEATURE [Part::Cut] Cut035
  Base = -> Cut034
  Refine = true
  Tool = -> Extrude057
FEATURE [Part::Cut] Cut037
  Base = -> Cut035
  Refine = true
  Tool = -> Extrude060
FEATURE [Part::Cut] Cut038
  Base = -> Cut037
  Refine = true
  Tool = -> Extrude061
FEATURE [Part::Cut] Cut039
  Base = -> Cut038
  Refine = true
  Tool = -> Extrude063
FEATURE [Part::Cut] Cut040
  Base = -> Cut039
  Refine = true
  Tool = -> Extrude064
FEATURE [Part::Cut] Cut041
  Base = -> Cut040
  Refine = true
  Tool = -> Extrude062
FEATURE [Sketcher::SketchObject] Sketch068  label="base con smusso sopra neopixel"
  ArcFitTolerance = 1e-06
  AttachmentSupport = -> [YZ_Plane002]
  FullyConstrained = true
  MakeInternals = false
  MapMode = 5
  Placement = pos=(0,0,0) rot=(0.57735,0.57735,0.57735;2.0944rad)
  sketch-geometry (5):
    g0: LineSegment StartX=-9.5 StartY=-6.1 StartZ=0 EndX=9.5 EndY=-6.1 EndZ=0
    g1: LineSegment StartX=9.5 StartY=-6.1 StartZ=0 EndX=9.5 EndY=6.1 EndZ=0
    g2: LineSegment StartX=9.5 StartY=6.1 StartZ=0 EndX=-9.5 EndY=6.1 EndZ=0
    g3: LineSegment StartX=-9.5 StartY=6.1 StartZ=0 EndX=-9.5 EndY=-6.1 EndZ=0
    g4: GeomPoint [constr] X=0 Y=0 Z=0
  constraints (12):
    c: Coincident(g0,g1)
    c: Coincident(g1,g2)
    c: Coincident(g2,g3)
    c: Coincident(g3,g0)
    c: Horizontal(g0)
    c: Horizontal(g2)
    c: Vertical(g1)
    c: Vertical(g3)
    c: Symmetric(g2,g0,g4)
    c: Distance(g1,g3) = 19
    c: Distance(g0,g2) = 12.2
    c: Coincident(g4,g-1)
FEATURE [Sketcher::SketchObject] Sketch069  label="cilindro minore"
  ArcFitTolerance = 1e-06
  AttachmentSupport = -> [XZ_Plane004]
  FullyConstrained = true
  MakeInternals = false
  MapMode = 5
  Placement = pos=(0,0,0) rot=(1,0,0;1.5708rad)
  sketch-geometry (1):
    g0: Circle CenterX=0 CenterY=0 CenterZ=0 NormalX=0 NormalY=0 NormalZ=1 AngleXU=0 Radius=5.8
  constraints (2):
    c: Diameter(g0) = 11.6
    c: Coincident(g0,g-1)
FEATURE [Sketcher::SketchObject] Sketch070  label="cilindro maggiore"
  ArcFitTolerance = 1e-06
  AttachmentSupport = -> [XZ_Plane004]
  ExternalGeometry = -> [Sketch069]
  FullyConstrained = true
  MakeInternals = false
  MapMode = 5
  Placement = pos=(0,0,0) rot=(1,0,0;1.5708rad)
  sketch-geometry (1):
    g0: Circle CenterX=0 CenterY=0 CenterZ=0 NormalX=0 NormalY=0 NormalZ=1 AngleXU=0 Radius=6.5
  constraints (2):
    c: Coincident(g0,g-1)
    c: Diameter(g0) = 13
FEATURE [Sketcher::SketchObject] Sketch071  label="buco interno"
  ArcFitTolerance = 1e-06
  AttachmentSupport = -> [XZ_Plane004]
  ExternalGeometry = -> [Sketch069]
  FullyConstrained = true
  MakeInternals = false
  MapMode = 5
  Placement = pos=(0,0,0) rot=(1,0,0;1.5708rad)
  sketch-geometry (1):
    g0: Circle CenterX=0 CenterY=0 CenterZ=0 NormalX=0 NormalY=0 NormalZ=1 AngleXU=0 Radius=5
  constraints (2):
    c: Coincident(g0,g-1)
    c: Diameter(g0) = 10
FEATURE [PartDesign::Pad] Pad
  Direction = (0,-1,2e-16)
  Length = 1.2
  Length2 = 10
  Placement = pos=(0,0,0) rot=(1,0,0;1.5708rad)
  Profile = -> Sketch070
  ReferenceAxis = -> Sketch070 [N_Axis]
  Refine = true
  Suppressed = false
  Type = 0
FEATURE [PartDesign::Pad] Pad001
  BaseFeature = -> Pad
  Direction = (0,-1,2e-16)
  Length = 5.6
  Length2 = 10
  Placement = pos=(0,0,0) rot=(1,0,0;1.5708rad)
  Profile = -> Sketch069
  ReferenceAxis = -> Sketch069 [N_Axis]
  Refine = true
  Suppressed = false
  Type = 0
FEATURE [PartDesign::Pocket] Pocket
  BaseFeature = -> Pad001
  Direction = (0,1,-2e-16)
  Length = 7
  Length2 = 5
  Midplane = true
  Placement = pos=(0,0,0) rot=(1,0,0;1.5708rad)
  Profile = -> Sketch071
  ReferenceAxis = -> Sketch071 [N_Axis]
  Refine = true
  Suppressed = false
  Type = 0
FEATURE [PartDesign::Fillet] Fillet
  Base = -> Pocket [Face7]
  BaseFeature = -> Pocket
  Placement = pos=(0,0,0) rot=(1,0,0;1.5708rad)
  Radius = 1
  Refine = true
  SupportTransform = false
  Suppressed = false
  UseAllEdges = false
FEATURE [PartDesign::Body] Body004  label="pulsanti lato sinistro"
  AllowCompound = false
  Group = -> [Sketch069,Sketch070,Sketch071,Pad,Pad001,Pocket,Fillet]
  Origin = -> Origin004
  Tip = -> Fillet
FEATURE [Sketcher::SketchObject] Sketch072  label="buco per saldature e diodo driver solenoide"
  ArcFitTolerance = 1e-06
  AttachmentSupport = -> [XZ_Plane]
  ExternalGeometry = -> [Sketch038]
  FullyConstrained = true
  MakeInternals = false
  MapMode = 5
  Placement = pos=(0,0,0) rot=(1,0,0;1.5708rad)
  sketch-geometry (4):
    g0: LineSegment StartX=-212.269 StartY=-43.9083 StartZ=0 EndX=-207.197 EndY=-33.0326 EndZ=0
    g1: LineSegment StartX=-207.197 StartY=-33.0326 StartZ=0 EndX=-207.56 EndY=-32.8635 EndZ=0
    g2: LineSegment StartX=-207.56 StartY=-32.8635 StartZ=0 EndX=-212.631 EndY=-43.7392 EndZ=0
    g3: LineSegment StartX=-212.631 StartY=-43.7392 StartZ=0 EndX=-212.269 EndY=-43.9083 EndZ=0
  constraints (11):
    c: Coincident(g1,g0)
    c: Coincident(g2,g1)
    c: Coincident(g3,g2)
    c: Coincident(g3,g0)
    c: Parallel(g-3,g0)
    c: Parallel(g0,g2)
    c: Perpendicular(g0,g3)
    c: Perpendicular(g1,g0)
    c: Distance(g3) = 0.4
    c: Distance(g2) = 12
    c: Coincident(g0,g-3)
FEATURE [Part::Extrusion] Extrude074  label="Extrude buco per saldature e diodo driver solenoide"
  Base = -> Sketch072
  Dir = (0,-1,2e-16)
  DirMode = 2
  FaceMakerClass = Part::FaceMakerBullseye
  FaceMakerMode = 3
  LengthFwd = 14.6
  LengthRev = 0
  Solid = true
  Symmetric = true
FEATURE [Part::Cut] Cut042
  Base = -> Cut041
  Refine = true
  Tool = -> Extrude074
FEATURE [Sketcher::SketchObject] Sketch073  label="fori slargati blocco solenoide"
  ArcFitTolerance = 1e-06
  AttachmentSupport = -> [XY_Plane]
  ExternalGeometry = -> [Sketch030]
  FullyConstrained = true
  MakeInternals = false
  MapMode = 5
  sketch-geometry (2):
    g0: Circle CenterX=-152.209 CenterY=6.95 CenterZ=0 NormalX=0 NormalY=0 NormalZ=1 AngleXU=0 Radius=3.7
    g1: Circle CenterX=-130.41 CenterY=-6.95 CenterZ=0 NormalX=0 NormalY=0 NormalZ=1 AngleXU=0 Radius=3.7
  constraints (4):
    c: Diameter(g0) = 7.4
    c: Coincident(g0,g-3)
    c: Diameter(g1) = 7.4
    c: Coincident(g1,g-4)
FEATURE [Part::Extrusion] Extrude075  label="Extrude fori slargati blocco solenoide"
  Base = -> Sketch073
  Dir = (0,0,1)
  DirMode = 2
  FaceMakerClass = Part::FaceMakerBullseye
  FaceMakerMode = 3
  LengthFwd = 1.5
  LengthRev = 0
  Placement = pos=(0,0,36.4) rot=(0,0,1;0rad)
  Solid = true
  Symmetric = false
FEATURE [Part::Cut] Cut043
  Base = -> Cut042
  Refine = true
  Tool = -> Extrude075
FEATURE [Sketcher::SketchObject] Sketch074  label="lato sx pistola"
  ArcFitTolerance = 1e-06
  AttachmentSupport = -> [XZ_Plane]
  ExternalGeometry = -> [Sketch016,Sketch,Sketch058]
  FullyConstrained = true
  MakeInternals = false
  MapMode = 5
  Placement = pos=(0,0,0) rot=(1,0,0;1.5708rad)
  sketch-geometry (37):
    g0: LineSegment StartX=-82.8 StartY=3.2 StartZ=0 EndX=0 EndY=3.2 EndZ=0
    g1: LineSegment StartX=-82.8 StartY=3.2 StartZ=0 EndX=-82.8 EndY=6.2 EndZ=0
    g2: LineSegment [constr] StartX=-107.6 StartY=18 StartZ=0 EndX=-107.6 EndY=20 EndZ=0
    g3: LineSegment [constr] StartX=-132.428 StartY=18 StartZ=0 EndX=-132.428 EndY=20 EndZ=0
    g4: LineSegment StartX=-132.428 StartY=20 StartZ=0 EndX=-107.6 EndY=20 EndZ=0
    g5: ArcOfCircle CenterX=-107.6 CenterY=4 CenterZ=0 NormalX=0 NormalY=0 NormalZ=1 AngleXU=0 Radius=16 StartAngle=0.137937 EndAngle=1.5708
    g6: LineSegment StartX=-82.8 StartY=6.2 StartZ=0 EndX=-91.752 EndY=6.2 EndZ=0
    g7: LineSegment [constr] StartX=-145.743 StartY=8.32624 StartZ=0 EndX=-147.645 EndY=8.94427 EndZ=0
    g8: ArcOfCircle CenterX=-132.428 CenterY=4 CenterZ=0 NormalX=0 NormalY=0 NormalZ=1 AngleXU=0 Radius=16 StartAngle=1.5708 EndAngle=2.82743
    g9: LineSegment StartX=-215.932 StartY=-80.4316 StartZ=0 EndX=-176.685 EndY=-80.4316 EndZ=0
    g10: LineSegment StartX=-147.645 StartY=8.94427 StartZ=0 EndX=-176.685 EndY=-80.4316 EndZ=0
    g11: LineSegment [constr] StartX=-193.988 StartY=-2.33927 StartZ=0 EndX=-192.176 EndY=-3.18451 EndZ=0
    g12: LineSegment [constr] StartX=-217.232 StartY=-52.1862 StartZ=0 EndX=-215.42 EndY=-53.0314 EndZ=0
    g13: LineSegment StartX=-192.176 StartY=-3.18451 StartZ=0 EndX=-215.42 EndY=-53.0314 EndZ=0
    g14: ArcOfCircle CenterX=-184.801 CenterY=-67.3089 CenterZ=0 NormalX=0 NormalY=0 NormalZ=1 AngleXU=0 Radius=33.7833 StartAngle=2.70526 EndAngle=3.54053
    g15: ArcOfCircle CenterX=-207.583 CenterY=4 CenterZ=0 NormalX=0 NormalY=0 NormalZ=1 AngleXU=0 Radius=17 StartAngle=5.84685 EndAngle=7.56663
    g16: LineSegment StartX=-202.765 StartY=20.303 StartZ=0 EndX=-195.887 EndY=39.2 EndZ=0
    g17: LineSegment [constr] StartX=-193.885 StartY=33.0037 StartZ=0 EndX=-197.644 EndY=34.3718 EndZ=0
    g18: LineSegment StartX=-195.887 StartY=39.2 StartZ=0 EndX=0 EndY=39.2 EndZ=0
    g19: LineSegment StartX=0 StartY=3.2 StartZ=0 EndX=0 EndY=39.2 EndZ=0
    g20: LineSegment StartX=-189.939 StartY=31.5672 StartZ=0 EndX=-192.333 EndY=24.9893 EndZ=0
    g21: LineSegment StartX=-196.467 StartY=26.4942 StartZ=0 EndX=-194.073 EndY=33.0721 EndZ=0
    g22: Circle CenterX=-213.443 CenterY=-76.8316 CenterZ=0 NormalX=0 NormalY=0 NormalZ=1 AngleXU=0 Radius=1.8
    g23: Circle CenterX=-179.305 CenterY=-76.8316 CenterZ=0 NormalX=0 NormalY=0 NormalZ=1 AngleXU=0 Radius=1.8
    g24: Circle CenterX=-184.08 CenterY=34.8 CenterZ=0 NormalX=0 NormalY=0 NormalZ=1 AngleXU=0 Radius=1.8
    g25: Circle CenterX=-78.51 CenterY=34.8 CenterZ=0 NormalX=0 NormalY=0 NormalZ=1 AngleXU=0 Radius=1.8
    g26: Circle CenterX=-78.51 CenterY=7.6 CenterZ=0 NormalX=0 NormalY=0 NormalZ=1 AngleXU=0 Radius=1.8
    g27: Circle CenterX=-5.6 CenterY=34.8 CenterZ=0 NormalX=0 NormalY=0 NormalZ=1 AngleXU=0 Radius=1.8
    g28: Circle CenterX=-5.6 CenterY=7.6 CenterZ=0 NormalX=0 NormalY=0 NormalZ=1 AngleXU=0 Radius=1.8
    g29: LineSegment StartX=-190.127 StartY=31.6356 StartZ=0 EndX=-189.939 EndY=31.5672 EndZ=0
    g30: LineSegment StartX=-194.073 StartY=33.0721 StartZ=0 EndX=-193.885 EndY=33.0037 EndZ=0
    g31: LineSegment StartX=-193.885 StartY=33.0037 StartZ=0 EndX=-190.127 EndY=31.6356 EndZ=0
    g32: LineSegment StartX=-196.467 StartY=26.4942 StartZ=0 EndX=-192.333 EndY=24.9893 EndZ=0
    g33: Circle CenterX=-19 CenterY=21.2 CenterZ=0 NormalX=0 NormalY=0 NormalZ=1 AngleXU=0 Radius=6.3
    g34: Circle CenterX=-42 CenterY=21.2 CenterZ=0 NormalX=0 NormalY=0 NormalZ=1 AngleXU=0 Radius=6.3
    g35: Circle CenterX=-65 CenterY=21.2 CenterZ=0 NormalX=0 NormalY=0 NormalZ=1 AngleXU=0 Radius=6.3
    g36: LineSegment [constr] StartX=-4 StartY=21.2 StartZ=0 EndX=-65 EndY=21.2 EndZ=0
  constraints (96):
    c: Coincident(g0,g-41)
    c: Horizontal(g0)
    c: PointOnObject(g0,g-39)
    c: Coincident(g1,g0)
    c: Vertical(g1)
    c: DistanceY(g1,g1) = 3
    c: Coincident(g2,g-17)
    c: Vertical(g2)
    c: Coincident(g3,g-16)
    c: Vertical(g3)
    c: DistanceY(g2,g2) = 2
    c: DistanceY(g3,g3) = 2
    c: Coincident(g4,g3)
    c: Coincident(g4,g2)
    c: Coincident(g5,g-17)
    c: Coincident(g5,g2)
    c: Coincident(g6,g1)
    c: Horizontal(g6)
    c: Coincident(g6,g5)
    c: Coincident(g7,g-15)
    c: Coincident(g8,g7)
    c: Coincident(g8,g3)
    c: Coincident(g8,g-15)
    c: Horizontal(g9)
    c: DistanceY(g-13,g9) = 2
    c: Coincident(g10,g7)
    c: Parallel(g10,g-14)
    c: Coincident(g9,g10)
    c: Distance(g11) = 2
    c: Coincident(g11,g-11)
    c: Perpendicular(g-11,g11)
    c: Distance(g12) = 2
    c: Coincident(g12,g-12)
    c: Perpendicular(g-11,g12)
    c: Coincident(g13,g11)
    c: Coincident(g13,g12)
    c: Coincident(g14,g-32)
    c: Coincident(g14,g12)
    c: Coincident(g14,g9)
    c: Coincident(g15,g-10)
    c: Coincident(g15,g11)
    c: Parallel(g16,g-22)
    c: Distance(g17) = 4
    c: PointOnObject(g17,g16)
    c: Coincident(g15,g16)
    c: Horizontal(g18)
    c: Coincident(g18,g16)
    c: Coincident(g19,g0)
    c: PointOnObject(g19,g-39)
    c: DistanceY(g19,g-36) = 2
    c: Coincident(g18,g19)
    c: Diameter(g22) = 3.6
    c: Coincident(g22,g-9)
    c: Diameter(g23) = 3.6
    c: Coincident(g23,g-8)
    c: Diameter(g24) = 3.6
    c: Diameter(g25) = 3.6
    c: Diameter(g26) = 3.6
    c: Diameter(g27) = 3.6
    c: Diameter(g28) = 3.6
    c: Coincident(g27,g-4)
    c: Coincident(g28,g-3)
    c: Coincident(g25,g-6)
    c: Coincident(g26,g-5)
    c: Coincident(g24,g-7)
    c: Parallel(g20,g-21)
    c: Equal(g20,g-21)
    c: Parallel(g21,g-19)
    c: Equal(g21,g-19)
    c: Distance(g29) = 0.2
    c: Distance(g30) = 0.2
    c: Parallel(g29,g-20)
    c: Parallel(g31,g-20)
    c: Equal(g31,g-20)
    c: Coincident(g30,g31)
    c: Coincident(g31,g29)
    c: Coincident(g29,g-21)
    c: Parallel(g30,g31)
    c: Coincident(g17,g30)
    c: Coincident(g20,g29)
    c: Coincident(g21,g30)
    c: Perpendicular(g16,g17)
    c: Coincident(g32,g21)
    c: Coincident(g32,g20)
    c: Perpendicular(g10,g7)
    c: Diameter(g33) = 12.6
    c: Diameter(g34) = 12.6
    c: Diameter(g35) = 12.6
    c: Horizontal(g36)
    c: PointOnObject(g33,g36)
    c: PointOnObject(g34,g36)
    c: DistanceX(g34,g33) = 23
    c: DistanceX(g35,g34) = 23
    c: DistanceX(g33,g36) = 15
    c: Symmetric(g-24,g-24,g36)
    c: Coincident(g36,g35)
FEATURE [Sketcher::SketchObject] Sketch075  label="lato dx pistola"
  ArcFitTolerance = 1e-06
  AttachmentSupport = -> [XZ_Plane]
  ExternalGeometry = -> [Sketch016,Sketch,Sketch058,Sketch074]
  FullyConstrained = true
  MakeInternals = false
  MapMode = 5
  Placement = pos=(0,0,0) rot=(1,0,0;1.5708rad)
  sketch-geometry (61):
    g0: LineSegment StartX=-82.8 StartY=3.2 StartZ=0 EndX=0 EndY=3.2 EndZ=0
    g1: LineSegment StartX=-82.8 StartY=3.2 StartZ=0 EndX=-82.8 EndY=6.2 EndZ=0
    g2: LineSegment [constr] StartX=-107.6 StartY=18 StartZ=0 EndX=-107.6 EndY=20 EndZ=0
    g3: LineSegment [constr] StartX=-132.428 StartY=18 StartZ=0 EndX=-132.428 EndY=20 EndZ=0
    g4: LineSegment StartX=-132.428 StartY=20 StartZ=0 EndX=-107.6 EndY=20 EndZ=0
    g5: ArcOfCircle CenterX=-107.6 CenterY=4 CenterZ=0 NormalX=0 NormalY=0 NormalZ=1 AngleXU=0 Radius=16 StartAngle=0.137937 EndAngle=1.5708
    g6: LineSegment StartX=-82.8 StartY=6.2 StartZ=0 EndX=-91.752 EndY=6.2 EndZ=0
    g7: LineSegment [constr] StartX=-145.743 StartY=8.32624 StartZ=0 EndX=-147.645 EndY=8.94427 EndZ=0
    g8: ArcOfCircle CenterX=-132.428 CenterY=4 CenterZ=0 NormalX=0 NormalY=0 NormalZ=1 AngleXU=0 Radius=16 StartAngle=1.5708 EndAngle=2.82743
    g9: LineSegment StartX=-215.932 StartY=-80.4316 StartZ=0 EndX=-176.685 EndY=-80.4316 EndZ=0
    g10: LineSegment StartX=-147.645 StartY=8.94427 StartZ=0 EndX=-176.685 EndY=-80.4316 EndZ=0
    g11: LineSegment [constr] StartX=-193.988 StartY=-2.33927 StartZ=0 EndX=-192.176 EndY=-3.18451 EndZ=0
    g12: LineSegment [constr] StartX=-217.232 StartY=-52.1862 StartZ=0 EndX=-215.42 EndY=-53.0314 EndZ=0
    g13: LineSegment StartX=-192.176 StartY=-3.18451 StartZ=0 EndX=-215.42 EndY=-53.0314 EndZ=0
    g14: ArcOfCircle CenterX=-184.801 CenterY=-67.3089 CenterZ=0 NormalX=0 NormalY=0 NormalZ=1 AngleXU=0 Radius=33.7833 StartAngle=2.70526 EndAngle=3.54053
    g15: ArcOfCircle CenterX=-207.583 CenterY=4 CenterZ=0 NormalX=0 NormalY=0 NormalZ=1 AngleXU=0 Radius=17 StartAngle=5.84685 EndAngle=7.56663
    g16: LineSegment StartX=-202.765 StartY=20.303 StartZ=0 EndX=-195.887 EndY=39.2 EndZ=0
    g17: LineSegment [constr] StartX=-193.885 StartY=33.0037 StartZ=0 EndX=-197.644 EndY=34.3718 EndZ=0
    g18: LineSegment StartX=-195.887 StartY=39.2 StartZ=0 EndX=0 EndY=39.2 EndZ=0
    g19: LineSegment StartX=0 StartY=3.2 StartZ=0 EndX=0 EndY=39.2 EndZ=0
    g20: LineSegment StartX=-189.939 StartY=31.5672 StartZ=0 EndX=-192.333 EndY=24.9893 EndZ=0
    g21: LineSegment StartX=-196.467 StartY=26.4942 StartZ=0 EndX=-194.073 EndY=33.0721 EndZ=0
    g22: Circle CenterX=-213.443 CenterY=-76.8316 CenterZ=0 NormalX=0 NormalY=0 NormalZ=1 AngleXU=0 Radius=1.8
    g23: Circle CenterX=-179.305 CenterY=-76.8316 CenterZ=0 NormalX=0 NormalY=0 NormalZ=1 AngleXU=0 Radius=1.8
    g24: Circle CenterX=-184.08 CenterY=34.8 CenterZ=0 NormalX=0 NormalY=0 NormalZ=1 AngleXU=0 Radius=1.8
    g25: Circle CenterX=-78.51 CenterY=34.8 CenterZ=0 NormalX=0 NormalY=0 NormalZ=1 AngleXU=0 Radius=1.8
    g26: Circle CenterX=-78.51 CenterY=7.6 CenterZ=0 NormalX=0 NormalY=0 NormalZ=1 AngleXU=0 Radius=1.8
    g27: Circle CenterX=-5.6 CenterY=34.8 CenterZ=0 NormalX=0 NormalY=0 NormalZ=1 AngleXU=0 Radius=1.8
    g28: Circle CenterX=-5.6 CenterY=7.6 CenterZ=0 NormalX=0 NormalY=0 NormalZ=1 AngleXU=0 Radius=1.8
    g29: LineSegment StartX=-190.127 StartY=31.6356 StartZ=0 EndX=-189.939 EndY=31.5672 EndZ=0
    g30: LineSegment StartX=-194.073 StartY=33.0721 StartZ=0 EndX=-193.885 EndY=33.0037 EndZ=0
    g31: LineSegment StartX=-193.885 StartY=33.0037 StartZ=0 EndX=-190.127 EndY=31.6356 EndZ=0
    g32: LineSegment StartX=-196.467 StartY=26.4942 StartZ=0 EndX=-192.333 EndY=24.9893 EndZ=0
    g33: LineSegment [constr] StartX=-4 StartY=21.2 StartZ=0 EndX=-87.91 EndY=21.2 EndZ=0
    g34: GeomPoint [constr] X=-4 Y=21.2 Z=0
    g35: LineSegment [constr] StartX=-15.2 StartY=33.7 StartZ=0 EndX=-15.2 EndY=8.7 EndZ=0
    g36: LineSegment [constr] StartX=-15.2 StartY=33.7 StartZ=0 EndX=-56.2 EndY=33.7 EndZ=0
    g37: LineSegment [constr] StartX=-15.2 StartY=8.7 StartZ=0 EndX=-56.2 EndY=8.7 EndZ=0
    g38: LineSegment [constr] StartX=-56.2 StartY=33.7 StartZ=0 EndX=-56.2 EndY=8.7 EndZ=0
    g39: Circle CenterX=-18.6 CenterY=30.3 CenterZ=0 NormalX=0 NormalY=0 NormalZ=1 AngleXU=0 Radius=3.4
    g40: Circle CenterX=-18.6 CenterY=12.1 CenterZ=0 NormalX=0 NormalY=0 NormalZ=1 AngleXU=0 Radius=3.4
    g41: Circle CenterX=-43.2 CenterY=30.3 CenterZ=0 NormalX=0 NormalY=0 NormalZ=1 AngleXU=0 Radius=3.4
    g42: Circle CenterX=-43.2 CenterY=12.1 CenterZ=0 NormalX=0 NormalY=0 NormalZ=1 AngleXU=0 Radius=3.4
    g43: LineSegment [constr] StartX=-4 StartY=21.2 StartZ=0 EndX=-15.2 EndY=21.2 EndZ=0
    g44: LineSegment [constr] StartX=-15.2 StartY=21.2 StartZ=0 EndX=-36.2 EndY=21.2 EndZ=0
    g45: LineSegment [constr] StartX=-41.5 StartY=16.2 StartZ=0 EndX=-30.9 EndY=16.2 EndZ=0
    g46: LineSegment [constr] StartX=-30.9 StartY=16.2 StartZ=0 EndX=-30.9 EndY=26.2 EndZ=0
    g47: LineSegment [constr] StartX=-30.9 StartY=26.2 StartZ=0 EndX=-41.5 EndY=26.2 EndZ=0
    g48: LineSegment [constr] StartX=-41.5 StartY=26.2 StartZ=0 EndX=-41.5 EndY=16.2 EndZ=0
    g49: GeomPoint [constr] X=-36.2 Y=21.2 Z=0
    g50: Circle CenterX=-36.2 CenterY=21.2 CenterZ=0 NormalX=0 NormalY=0 NormalZ=1 AngleXU=0 Radius=2.8
    g51: LineSegment [constr] StartX=-24.2 StartY=26.7 StartZ=0 EndX=-24.2 EndY=15.7 EndZ=0
    g52: Circle CenterX=-24.2 CenterY=26.7 CenterZ=0 NormalX=0 NormalY=0 NormalZ=1 AngleXU=0 Radius=3
    g53: Circle CenterX=-24.2 CenterY=15.7 CenterZ=0 NormalX=0 NormalY=0 NormalZ=1 AngleXU=0 Radius=3
    g54: GeomPoint X=-18.6 Y=30.3 Z=0
    g55: GeomPoint X=-18.6 Y=12.1 Z=0
    g56: GeomPoint X=-43.2 Y=12.1 Z=0
    g57: GeomPoint X=-43.2 Y=30.3 Z=0
    g58: Circle CenterX=-65 CenterY=21.2 CenterZ=0 NormalX=0 NormalY=0 NormalZ=1 AngleXU=0 Radius=1.5
    g59: Circle CenterX=-42 CenterY=21.2 CenterZ=0 NormalX=0 NormalY=0 NormalZ=1 AngleXU=0 Radius=1.5
    g60: Circle CenterX=-19 CenterY=21.2 CenterZ=0 NormalX=0 NormalY=0 NormalZ=1 AngleXU=0 Radius=1.5
  constraints (149):
    c: Coincident(g0,g-41)
    c: Horizontal(g0)
    c: PointOnObject(g0,g-39)
    c: Coincident(g1,g0)
    c: Vertical(g1)
    c: DistanceY(g1,g1) = 3
    c: Coincident(g2,g-17)
    c: Vertical(g2)
    c: Coincident(g3,g-16)
    c: Vertical(g3)
    c: DistanceY(g2,g2) = 2
    c: DistanceY(g3,g3) = 2
    c: Coincident(g4,g3)
    c: Coincident(g4,g2)
    c: Coincident(g5,g-17)
    c: Coincident(g5,g2)
    c: Coincident(g6,g1)
    c: Horizontal(g6)
    c: Coincident(g6,g5)
    c: Coincident(g7,g-15)
    c: Coincident(g8,g7)
    c: Coincident(g8,g3)
    c: Coincident(g8,g-15)
    c: Horizontal(g9)
    c: DistanceY(g-13,g9) = 2
    c: Coincident(g10,g7)
    c: Parallel(g10,g-14)
    c: Coincident(g9,g10)
    c: Distance(g11) = 2
    c: Coincident(g11,g-11)
    c: Perpendicular(g-11,g11)
    c: Distance(g12) = 2
    c: Coincident(g12,g-12)
    c: Perpendicular(g-11,g12)
    c: Coincident(g13,g11)
    c: Coincident(g13,g12)
    c: Coincident(g14,g-32)
    c: Coincident(g14,g12)
    c: Coincident(g14,g9)
    c: Coincident(g15,g-10)
    c: Coincident(g15,g11)
    c: Parallel(g16,g-22)
    c: Distance(g17) = 4
    c: PointOnObject(g17,g16)
    c: Coincident(g15,g16)
    c: Horizontal(g18)
    c: Coincident(g18,g16)
    c: Coincident(g19,g0)
    c: PointOnObject(g19,g-39)
    c: DistanceY(g19,g-36) = 2
    c: Coincident(g18,g19)
    c: Diameter(g22) = 3.6
    c: Coincident(g22,g-9)
    c: Diameter(g23) = 3.6
    c: Coincident(g23,g-8)
    c: Diameter(g24) = 3.6
    c: Diameter(g25) = 3.6
    c: Diameter(g26) = 3.6
    c: Diameter(g27) = 3.6
    c: Diameter(g28) = 3.6
    c: Coincident(g27,g-4)
    c: Coincident(g28,g-3)
    c: Coincident(g25,g-6)
    c: Coincident(g26,g-5)
    c: Coincident(g24,g-7)
    c: Parallel(g20,g-21)
    c: Equal(g20,g-21)
    c: Parallel(g21,g-19)
    c: Equal(g21,g-19)
    c: Distance(g29) = 0.2
    c: Distance(g30) = 0.2
    c: Parallel(g29,g-20)
    c: Parallel(g31,g-20)
    c: Equal(g31,g-20)
    c: Coincident(g30,g31)
    c: Coincident(g31,g29)
    c: Coincident(g29,g-21)
    c: Parallel(g30,g31)
    c: Coincident(g17,g30)
    c: Coincident(g20,g29)
    c: Coincident(g21,g30)
    c: Perpendicular(g16,g17)
    c: Coincident(g32,g21)
    c: Coincident(g32,g20)
    c: Perpendicular(g10,g7)
    c: Horizontal(g33)
    c: Symmetric(g-24,g-24,g33)
    c: PointOnObject(g33,g-28)
    c: Symmetric(g-24,g-24,g34)
    c: DistanceY(g35,g35) = 25
    c: Symmetric(g35,g35,g33)
    c: Distance(g36) = 41
    c: Coincident(g36,g35)
    c: Horizontal(g36)
    c: Coincident(g37,g35)
    c: Horizontal(g37)
    c: Coincident(g38,g36)
    c: Vertical(g38)
    c: Coincident(g37,g38)
    c: Diameter(g39) = 6.8
    c: Diameter(g40) = 6.8
    c: Tangent(g39,g36)
    c: Tangent(g40,g37)
    c: Tangent(g39,g35)
    c: Tangent(g40,g35)
    c: Diameter(g41) = 6.8
    c: Diameter(g42) = 6.8
    c: Tangent(g41,g36)
    c: Tangent(g42,g37)
    c: DistanceX(g41,g39) = 24.6
    c: DistanceX(g42,g40) = 24.6
    c: Distance(g43) = 11.2
    c: Coincident(g43,g33)
    c: PointOnObject(g43,g33)
    c: PointOnObject(g43,g35)
    c: Distance(g44) = 21
    c: Coincident(g44,g43)
    c: PointOnObject(g44,g33)
    c: Coincident(g45,g46)
    c: Coincident(g46,g47)
    c: Coincident(g47,g48)
    c: Coincident(g48,g45)
    c: Horizontal(g45)
    c: Horizontal(g47)
    c: Vertical(g46)
    c: Vertical(g48)
    c: Symmetric(g47,g45,g49)
    c: Distance(g46,g48) = 10.6
    c: Distance(g45,g47) = 10
    c: Coincident(g49,g44)
    c: Diameter(g50) = 5.6
    c: Coincident(g50,g44)
    c: Distance(g51) = 11
    c: Symmetric(g51,g51,g33)
    c: DistanceX(g51,g43) = 9
    c: Diameter(g52) = 6
    c: Coincident(g52,g51)
    c: Diameter(g53) = 6
    c: Coincident(g53,g51)
    c: Coincident(g40,g55)
    c: Coincident(g39,g54)
    c: Coincident(g41,g57)
    c: Coincident(g42,g56)
    c: Diameter(g58) = 3
    c: Diameter(g59) = 3
    c: Diameter(g60) = 3
    c: Coincident(g58,g-44)
    c: Coincident(g59,g-46)
    c: Coincident(g60,g-45)
FEATURE [Sketcher::SketchObject] Sketch078
  ArcFitTolerance = 1e-06
  AttachmentSupport = -> [XZ_Plane005]
  FullyConstrained = true
  MakeInternals = false
  MapMode = 5
  Placement = pos=(0,0,0) rot=(1,0,0;1.5708rad)
  sketch-geometry (5):
    g0: LineSegment [constr] StartX=0 StartY=5.5 StartZ=0 EndX=0 EndY=-5.5 EndZ=0
    g1: ArcOfCircle CenterX=0 CenterY=5.5 CenterZ=0 NormalX=0 NormalY=0 NormalZ=1 AngleXU=0 Radius=2.7 StartAngle=0 EndAngle=3.14159
    g2: ArcOfCircle CenterX=0 CenterY=-5.5 CenterZ=0 NormalX=0 NormalY=0 NormalZ=1 AngleXU=0 Radius=2.7 StartAngle=3.1416 EndAngle=6.28318
    g3: LineSegment StartX=-2.7 StartY=5.5 StartZ=0 EndX=-2.7 EndY=-5.50001 EndZ=0
    g4: LineSegment StartX=2.7 StartY=5.5 StartZ=0 EndX=2.7 EndY=-5.50001 EndZ=0
  constraints (13):
    c: Distance(g0) = 11
    c: Vertical(g0)
    c: Symmetric(g0,g0,g-1)
    c: Radius(g1) = 2.7
    c: Coincident(g1,g0)
    c: Radius(g2) = 2.7
    c: Coincident(g2,g0)
    c: Vertical(g3)
    c: Vertical(g4)
    c: Coincident(g2,g4)
    c: Coincident(g2,g3)
    c: Tangent(g3,g1) = -1.5708
    c: Tangent(g4,g1) = 1.5708
FEATURE [PartDesign::Pad] Pad002
  Direction = (0,-1,2e-16)
  Length = 0.8
  Length2 = 10
  Placement = pos=(0,0,0) rot=(1,0,0;1.5708rad)
  Profile = -> Sketch078
  ReferenceAxis = -> Sketch078 [N_Axis]
  Refine = true
  Suppressed = false
  Type = 0
FEATURE [Sketcher::SketchObject] Sketch079
  ArcFitTolerance = 1e-06
  AttachmentSupport = -> [XZ_Plane005]
  ExternalGeometry = -> [Sketch078]
  FullyConstrained = true
  MakeInternals = false
  MapMode = 5
  Placement = pos=(0,0,0) rot=(1,0,0;1.5708rad)
  sketch-geometry (2):
    g0: Circle CenterX=-1e-16 CenterY=5.5 CenterZ=0 NormalX=0 NormalY=0 NormalZ=1 AngleXU=0 Radius=2.7
    g1: Circle CenterX=0 CenterY=-5.5 CenterZ=0 NormalX=0 NormalY=0 NormalZ=1 AngleXU=0 Radius=2.7
  constraints (4):
    c: Coincident(g0,g-3)
    c: PointOnObject(g-3,g0)
    c: Coincident(g1,g-4)
    c: Equal(g1,g-4)
FEATURE [PartDesign::Pad] Pad003
  BaseFeature = -> Pad002
  Direction = (0,-1,2e-16)
  Length = 5
  Length2 = 10
  Placement = pos=(0,0,0) rot=(1,0,0;1.5708rad)
  Profile = -> Sketch079
  ReferenceAxis = -> Sketch079 [N_Axis]
  Refine = true
  Suppressed = false
  Type = 0
FEATURE [PartDesign::Fillet] Fillet001
  Base = -> Pad003 [Edge16,Edge14]
  BaseFeature = -> Pad003
  Placement = pos=(0,0,0) rot=(1,0,0;1.5708rad)
  Radius = 0.4
  Refine = true
  SupportTransform = false
  Suppressed = false
  UseAllEdges = false
FEATURE [PartDesign::Body] Body005  label="pulsanti lato destro"
  AllowCompound = false
  Group = -> [Sketch078,Pad002,Sketch079,Pad003,Fillet001]
  Origin = -> Origin005
  Tip = -> Fillet001
FEATURE [PartDesign::SubShapeBinder] Binder
  BindCopyOnChange = 0
  BindMode = 0
  ClaimChildren = false
  Context = -> Body006 [Binder.]
  Fuse = false
  MakeFace = true
  OffsetFill = false
  OffsetIntersection = false
  OffsetJoinType = 0
  OffsetOpenResult = false
  PartialLoad = false
  Refine = true
  Relative = true
  Support = -> [Body[Sketch074.]]
  _Version = 2
FEATURE [PartDesign::SubShapeBinder] Binder001
  BindCopyOnChange = 0
  BindMode = 0
  ClaimChildren = false
  Context = -> Body007 [Binder001.]
  Fuse = false
  MakeFace = true
  OffsetFill = false
  OffsetIntersection = false
  OffsetJoinType = 0
  OffsetOpenResult = false
  PartialLoad = false
  Refine = true
  Relative = true
  Support = -> [Body[Sketch075.]]
  _Version = 2
FEATURE [Mesh::Feature] logo_per_PCB_definitivo_positivo
  Placement = pos=(-191,17,-66) rot=(0,1,1;0rad)
FEATURE [Sketcher::SketchObject] Sketch114  label="Sketch114 - base lato DX"
  ArcFitTolerance = 1e-06
  AttachmentSupport = -> [Binder001]
  ExternalGeometry = -> [Binder001]
  FullyConstrained = true
  MakeInternals = false
  MapMode = 5
  Placement = pos=(0,1e-15,0) rot=(0,0.707107,0.707107;3.14159rad)
  sketch-geometry (30):
    g0: Circle CenterX=5.6 CenterY=34.8 CenterZ=0 NormalX=0 NormalY=0 NormalZ=1 AngleXU=0 Radius=1.8
    g1: Circle CenterX=5.6 CenterY=7.6 CenterZ=0 NormalX=0 NormalY=0 NormalZ=1 AngleXU=0 Radius=1.8
    g2: Circle CenterX=24.2 CenterY=26.7 CenterZ=0 NormalX=0 NormalY=0 NormalZ=1 AngleXU=0 Radius=3
    g3: Circle CenterX=24.2 CenterY=15.7 CenterZ=0 NormalX=0 NormalY=0 NormalZ=1 AngleXU=0 Radius=3
    g4: Circle CenterX=36.2 CenterY=21.2 CenterZ=0 NormalX=0 NormalY=0 NormalZ=1 AngleXU=0 Radius=2.8
    g5: Circle CenterX=78.51 CenterY=34.8 CenterZ=0 NormalX=0 NormalY=0 NormalZ=1 AngleXU=0 Radius=1.8
    g6: Circle CenterX=78.51 CenterY=7.6 CenterZ=0 NormalX=0 NormalY=0 NormalZ=1 AngleXU=0 Radius=1.8
    g7: Circle CenterX=184.08 CenterY=34.8 CenterZ=0 NormalX=0 NormalY=0 NormalZ=1 AngleXU=0 Radius=1.8
    g8: Circle CenterX=213.443 CenterY=-76.8316 CenterZ=0 NormalX=0 NormalY=0 NormalZ=1 AngleXU=0 Radius=1.8
    g9: Circle CenterX=179.305 CenterY=-76.8316 CenterZ=0 NormalX=0 NormalY=0 NormalZ=1 AngleXU=0 Radius=1.8
    g10: ArcOfCircle [constr] CenterX=132.428 CenterY=4 CenterZ=0 NormalX=0 NormalY=0 NormalZ=1 AngleXU=0 Radius=16 StartAngle=0.314159 EndAngle=1.5708
    g11: ArcOfCircle CenterX=107.6 CenterY=4 CenterZ=0 NormalX=0 NormalY=0 NormalZ=1 AngleXU=0 Radius=16 StartAngle=1.5708 EndAngle=3.00366
    g12: ArcOfCircle CenterX=207.583 CenterY=4 CenterZ=0 NormalX=0 NormalY=0 NormalZ=1 AngleXU=0 Radius=17 StartAngle=1.85815 EndAngle=3.57792
    g13: ArcOfCircle CenterX=184.801 CenterY=-67.3089 CenterZ=0 NormalX=0 NormalY=0 NormalZ=1 AngleXU=0 Radius=33.7833 StartAngle=5.88425 EndAngle=6.71952
    g14: LineSegment StartX=0 StartY=39.2 StartZ=0 EndX=0 EndY=3.2 EndZ=0
    g15: LineSegment StartX=0 StartY=3.2 StartZ=0 EndX=82.8 EndY=3.2 EndZ=0
    g16: LineSegment StartX=82.8 StartY=3.2 StartZ=0 EndX=82.8 EndY=6.2 EndZ=0
    g17: LineSegment StartX=82.8 StartY=6.2 StartZ=0 EndX=91.752 EndY=6.2 EndZ=0
    g18: LineSegment StartX=107.6 StartY=20 StartZ=0 EndX=132.428 EndY=20 EndZ=0
    g19: LineSegment StartX=147.645 StartY=8.94427 StartZ=0 EndX=176.685 EndY=-80.4316 EndZ=0
    g20: LineSegment StartX=176.685 StartY=-80.4316 StartZ=0 EndX=215.932 EndY=-80.4316 EndZ=0
    g21: LineSegment StartX=215.42 StartY=-53.0314 StartZ=0 EndX=192.176 EndY=-3.18451 EndZ=0
    g22: LineSegment StartX=202.765 StartY=20.303 StartZ=0 EndX=195.887 EndY=39.2 EndZ=0
    g23: LineSegment StartX=195.887 StartY=39.2 StartZ=0 EndX=0 EndY=39.2 EndZ=0
    g24: LineSegment StartX=196.467 StartY=26.4942 StartZ=0 EndX=194.073 EndY=33.0721 EndZ=0
    g25: LineSegment StartX=194.073 StartY=33.0721 StartZ=0 EndX=189.939 EndY=31.5672 EndZ=0
    g26: LineSegment StartX=189.939 StartY=31.5672 StartZ=0 EndX=192.333 EndY=24.9893 EndZ=0
    g27: LineSegment StartX=192.333 StartY=24.9893 StartZ=0 EndX=196.467 EndY=26.4942 EndZ=0
    g28: LineSegment StartX=132.428 StartY=20 StartZ=0 EndX=144.053 EndY=20 EndZ=0
    g29: LineSegment StartX=144.053 StartY=20 StartZ=0 EndX=147.645 EndY=8.94427 EndZ=0
  constraints (65):
    c: Equal(g0,g-25)
    c: Equal(g2,g-29)
    c: Equal(g3,g-30)
    c: Equal(g4,g-28)
    c: Equal(g1,g-26)
    c: Coincident(g0,g-25)
    c: Coincident(g1,g-26)
    c: Coincident(g2,g-29)
    c: Coincident(g3,g-30)
    c: Coincident(g4,g-28)
    c: Equal(g5,g-23)
    c: Equal(g6,g-24)
    c: Coincident(g5,g-23)
    c: Coincident(g6,g-24)
    c: Equal(g7,g-20)
    c: Coincident(g7,g-20)
    c: Equal(g9,g-22)
    c: Coincident(g9,g-22)
    c: Equal(g8,g-21)
    c: Coincident(g8,g-21)
    c: Equal(g13,g-12)
    c: Equal(g12,g-14)
    c: Equal(g10,g-9)
    c: Equal(g11,g-7)
    c: Coincident(g14,g-27)
    c: Coincident(g14,g-27)
    c: Coincident(g15,g14)
    c: Coincident(g15,g-5)
    c: Coincident(g16,g15)
    c: Coincident(g16,g-6)
    c: Coincident(g17,g16)
    c: Coincident(g17,g-7)
    c: Coincident(g11,g17)
    c: Coincident(g11,g-8)
    c: Coincident(g18,g11)
    c: Coincident(g18,g-9)
    c: Coincident(g10,g18)
    c: Coincident(g10,g-10)
    c: Coincident(g19,g10)
    c: Coincident(g19,g-11)
    c: Coincident(g20,g19)
    c: Coincident(g20,g-12)
    c: Coincident(g13,g20)
    c: Coincident(g13,g-13)
    c: Coincident(g21,g13)
    c: Coincident(g21,g-14)
    c: Coincident(g12,g21)
    c: Coincident(g12,g-15)
    c: Coincident(g22,g12)
    c: Coincident(g22,g-15)
    c: Coincident(g23,g22)
    c: Coincident(g23,g14)
    c: Coincident(g24,g-18)
    c: Coincident(g24,g-16)
    c: Coincident(g25,g24)
    c: Coincident(g25,g-19)
    c: Coincident(g26,g25)
    c: Coincident(g26,g-19)
    c: Coincident(g27,g26)
    c: Coincident(g27,g24)
    c: Coincident(g29,g10)
    c: Coincident(g28,g10)
    c: Coincident(g29,g28)
    c: Parallel(g28,g18)
    c: Parallel(g29,g19)
FEATURE [PartDesign::Pad] Pad011
  Direction = (0,1,-2e-16)
  Length = 2
  Length2 = 10
  Profile = -> Sketch114
  ReferenceAxis = -> Sketch114 [N_Axis]
  Refine = true
  Reversed = true
  Suppressed = false
  Type = 0
FEATURE [Sketcher::SketchObject] Sketch115
  ArcFitTolerance = 1e-06
  AttachmentSupport = -> [Pad011]
  ExternalGeometry = -> [Binder001]
  FullyConstrained = true
  MakeInternals = false
  MapMode = 5
  Placement = pos=(0,1.7e-15,0) rot=(0,0.707107,0.707107;3.14159rad)
  sketch-geometry (4):
    g0: ArcOfCircle CenterX=24.2 CenterY=26.7 CenterZ=0 NormalX=0 NormalY=0 NormalZ=1 AngleXU=0 Radius=3 StartAngle=4.48384e-08 EndAngle=3.14159
    g1: ArcOfCircle CenterX=24.2 CenterY=15.7 CenterZ=0 NormalX=0 NormalY=0 NormalZ=1 AngleXU=0 Radius=3 StartAngle=3.14159 EndAngle=6.28318
    g2: LineSegment StartX=21.2 StartY=26.7 StartZ=0 EndX=21.2 EndY=15.7 EndZ=0
    g3: LineSegment StartX=27.2 StartY=26.7 StartZ=0 EndX=27.2 EndY=15.7 EndZ=0
  constraints (12):
    c: Equal(g1,g-4)
    c: Equal(g0,g-3)
    c: Coincident(g0,g-3)
    c: Coincident(g1,g-4)
    c: Vertical(g2)
    c: Vertical(g3)
    c: Tangent(g3,g-3)
    c: Tangent(g2,g-3)
    c: Coincident(g0,g2)
    c: Coincident(g0,g3)
    c: Coincident(g1,g2)
    c: Coincident(g3,g1)
FEATURE [Sketcher::SketchObject] Sketch117  label="Sketch117 - fori per inserto M3 x 3 x 4.5"
  ArcFitTolerance = 1e-06
  AttachmentSupport = -> [Pad011]
  ExternalGeometry = -> [Binder001]
  FullyConstrained = true
  MakeInternals = false
  MapMode = 5
  Placement = pos=(0,1.7e-15,0) rot=(0,0.707107,0.707107;3.14159rad)
  sketch-geometry (4):
    g0: Circle CenterX=43.2 CenterY=30.3 CenterZ=0 NormalX=0 NormalY=0 NormalZ=1 AngleXU=0 Radius=2.25
    g1: Circle CenterX=43.2 CenterY=12.1 CenterZ=0 NormalX=0 NormalY=0 NormalZ=1 AngleXU=0 Radius=2.25
    g2: Circle CenterX=18.6 CenterY=30.3 CenterZ=0 NormalX=0 NormalY=0 NormalZ=1 AngleXU=0 Radius=2.25
    g3: Circle CenterX=18.6 CenterY=12.1 CenterZ=0 NormalX=0 NormalY=0 NormalZ=1 AngleXU=0 Radius=2.25
  constraints (8):
    c: Diameter(g0) = 4.5
    c: Diameter(g1) = 4.5
    c: Diameter(g2) = 4.5
    c: Diameter(g3) = 4.5
    c: Coincident(g2,g-3)
    c: Coincident(g3,g-6)
    c: Coincident(g0,g-4)
    c: Coincident(g1,g-5)
FEATURE [Sketcher::SketchObject] Sketch118
  ArcFitTolerance = 1e-06
  AttachmentSupport = -> [Pad011]
  ExternalGeometry = -> [Binder001]
  FullyConstrained = true
  MakeInternals = false
  MapMode = 5
  Placement = pos=(0,-2,0) rot=(1,0,0;1.5708rad)
  sketch-geometry (12):
    g0: Circle CenterX=-78.51 CenterY=34.8 CenterZ=0 NormalX=0 NormalY=0 NormalZ=1 AngleXU=0 Radius=1.8
    g1: Circle CenterX=-78.51 CenterY=7.6 CenterZ=0 NormalX=0 NormalY=0 NormalZ=1 AngleXU=0 Radius=1.8
    g2: Circle CenterX=-5.6 CenterY=34.8 CenterZ=0 NormalX=0 NormalY=0 NormalZ=1 AngleXU=0 Radius=1.8
    g3: Circle CenterX=-5.6 CenterY=7.6 CenterZ=0 NormalX=0 NormalY=0 NormalZ=1 AngleXU=0 Radius=1.8
    g4: LineSegment StartX=0 StartY=39.2 StartZ=0 EndX=0 EndY=3.2 EndZ=0
    g5: LineSegment StartX=0 StartY=3.2 StartZ=0 EndX=-82.8 EndY=3.2 EndZ=0
    g6: LineSegment StartX=-82.8 StartY=3.2 StartZ=0 EndX=-82.8 EndY=39.2 EndZ=0
    g7: LineSegment StartX=-82.8 StartY=39.2 StartZ=0 EndX=0 EndY=39.2 EndZ=0
    g8: ArcOfCircle CenterX=-65 CenterY=21.2 CenterZ=0 NormalX=0 NormalY=0 NormalZ=1 AngleXU=0 Radius=10 StartAngle=1.5708 EndAngle=4.71239
    g9: ArcOfCircle CenterX=-19 CenterY=21.2 CenterZ=0 NormalX=0 NormalY=0 NormalZ=1 AngleXU=0 Radius=10 StartAngle=4.71239 EndAngle=7.85398
    g10: LineSegment StartX=-65 StartY=31.2 StartZ=0 EndX=-19 EndY=31.2 EndZ=0
    g11: LineSegment StartX=-65 StartY=11.2 StartZ=0 EndX=-19 EndY=11.2 EndZ=0
  constraints (25):
    c: Equal(g2,g-5)
    c: Equal(g3,g-7)
    c: Equal(g1,g-6)
    c: Equal(g0,g-4)
    c: Coincident(g0,g-4)
    c: Coincident(g1,g-6)
    c: Coincident(g3,g-7)
    c: Coincident(g2,g-5)
    c: Coincident(g4,g-8)
    c: Coincident(g4,g-9)
    c: Coincident(g5,g4)
    c: Coincident(g5,g-10)
    c: Coincident(g6,g5)
    c: PointOnObject(g6,g-3)
    c: Vertical(g6)
    c: Coincident(g7,g6)
    c: Coincident(g7,g4)
    c: Tangent(g8,g10) = 1.5708
    c: Tangent(g8,g11) = -1.5708
    c: Tangent(g9,g10) = 1.5708
    c: Tangent(g9,g11) = -1.5708
    c: Equal(g8,g9)
    c: Radius(g8) = 10
    c: Coincident(g8,g-11)
    c: Coincident(g9,g-12)
FEATURE [Sketcher::SketchObject] Sketch120
  ArcFitTolerance = 1e-06
  AttachmentSupport = -> [Pad011]
  ExternalGeometry = -> [Binder001]
  FullyConstrained = true
  MakeInternals = false
  MapMode = 5
  Placement = pos=(0,-2,0) rot=(1,0,0;1.5708rad)
  sketch-geometry (4):
    g0: LineSegment StartX=-137.815 StartY=39.2 StartZ=0 EndX=-142.655 EndY=24.303 EndZ=0
    g1: LineSegment StartX=-137.815 StartY=39.2 StartZ=0 EndX=-110.815 EndY=39.2 EndZ=0
    g2: LineSegment StartX=-142.655 StartY=24.303 StartZ=0 EndX=-110.815 EndY=24.303 EndZ=0
    g3: ArcOfCircle CenterX=-92.2534 CenterY=31.7515 CenterZ=0 NormalX=0 NormalY=0 NormalZ=1 AngleXU=0 Radius=20 StartAngle=2.75997 EndAngle=3.52321
  constraints (12):
    c: PointOnObject(g0,g-3)
    c: Coincident(g1,g0)
    c: PointOnObject(g1,g-3)
    c: Coincident(g2,g0)
    c: Horizontal(g2)
    c: Tangent(g0,g-4)
    c: Vertical(g2,g1)
    c: DistanceX(g1,g1) = 27
    c: DistanceY(g-6,g0) = 4
    c: Radius(g3) = 20
    c: Coincident(g3,g1)
    c: Coincident(g3,g2)
FEATURE [Sketcher::SketchObject] Sketch121
  ArcFitTolerance = 1e-06
  AttachmentSupport = -> [Pad011]
  ExternalGeometry = -> [Binder001]
  FullyConstrained = true
  MakeInternals = false
  MapMode = 5
  Placement = pos=(0,-2,0) rot=(1,0,0;1.5708rad)
  sketch-geometry (15):
    g0: LineSegment StartX=-137.815 StartY=39.2 StartZ=0 EndX=-143.955 EndY=20.303 EndZ=0
    g1: LineSegment StartX=-143.955 StartY=20.303 StartZ=0 EndX=-190.141 EndY=20.303 EndZ=0
    g2: LineSegment StartX=-190.141 StartY=20.303 StartZ=0 EndX=-186.139 EndY=31.3 EndZ=0
    g3: LineSegment StartX=-178.754 StartY=39.2 StartZ=0 EndX=-180.791 EndY=33.6029 EndZ=0
    g4: ArcOfCircle CenterX=-184.08 CenterY=34.8 CenterZ=0 NormalX=0 NormalY=0 NormalZ=1 AngleXU=0 Radius=3.5 StartAngle=4.71239 EndAngle=5.93412
    g5: LineSegment StartX=-184.08 StartY=31.3 StartZ=0 EndX=-186.139 EndY=31.3 EndZ=0
    g6: LineSegment StartX=-137.815 StartY=39.2 StartZ=0 EndX=-156.815 EndY=39.2 EndZ=0
    g7: LineSegment StartX=-168.815 StartY=39.2 StartZ=0 EndX=-178.754 EndY=39.2 EndZ=0
    g8: LineSegment StartX=-157.815 StartY=39.2 StartZ=0 EndX=-167.815 EndY=39.2 EndZ=0
    g9: LineSegment StartX=-168.815 StartY=31.2 StartZ=0 EndX=-156.815 EndY=31.2 EndZ=0
    g10: LineSegment StartX=-167.436 StartY=36.2 StartZ=0 EndX=-157.436 EndY=36.2 EndZ=0
    g11: ArcOfCircle CenterX=-176.411 CenterY=35.2 CenterZ=0 NormalX=0 NormalY=0 NormalZ=1 AngleXU=0 Radius=20 StartAngle=6.08183 EndAngle=6.48454
    g12: ArcOfCircle CenterX=-188.411 CenterY=35.2 CenterZ=0 NormalX=0 NormalY=0 NormalZ=1 AngleXU=0 Radius=20 StartAngle=6.08183 EndAngle=6.48454
    g13: ArcOfCircle CenterX=-177.411 CenterY=35.2 CenterZ=0 NormalX=0 NormalY=0 NormalZ=1 AngleXU=0 Radius=20 StartAngle=0.0500209 EndAngle=0.201358
    g14: ArcOfCircle CenterX=-187.411 CenterY=35.2 CenterZ=0 NormalX=0 NormalY=0 NormalZ=1 AngleXU=0 Radius=20 StartAngle=0.0500209 EndAngle=0.201358
  constraints (46):
    c: PointOnObject(g0,g-3)
    c: Tangent(g0,g-5)
    c: Coincident(g1,g0)
    c: Horizontal(g1)
    c: Coincident(g2,g1)
    c: PointOnObject(g3,g-3)
    c: Parallel(g3,g-6)
    c: Parallel(g2,g-6)
    c: Radius(g4) = 3.5
    c: Coincident(g4,g-7)
    c: Tangent(g3,g4) = 1.5708
    c: Horizontal(g5)
    c: Tangent(g5,g4) = 1.5708
    c: DistanceX(g-8,g5) = 3.8
    c: Coincident(g2,g5)
    c: Coincident(g6,g0)
    c: PointOnObject(g6,g-3)
    c: DistanceX(g6,g6) = 19
    c: PointOnObject(g7,g-3)
    c: DistanceX(g7,g6) = 12
    c: Coincident(g7,g3)
    c: PointOnObject(g8,g-3)
    c: PointOnObject(g8,g-3)
    c: DistanceX(g8,g8) = 10
    c: DistanceX(g8,g6) = 1
    c: Horizontal(g9)
    c: Vertical(g7,g9)
    c: Vertical(g6,g9)
    c: DistanceY(g9,g7) = 8
    c: Horizontal(g10)
    c: Equal(g8,g10)
    c: DistanceY(g10,g8) = 3
    c: Radius(g11) = 20
    c: Coincident(g11,g6)
    c: Coincident(g11,g9)
    c: Radius(g12) = 20
    c: Coincident(g12,g7)
    c: Coincident(g12,g9)
    c: Equal(g13,g11)
    c: Coincident(g13,g8)
    c: Coincident(g13,g10)
    c: Horizontal(g13,g11)
    c: Equal(g14,g12)
    c: Coincident(g14,g8)
    c: Coincident(g14,g10)
    c: Horizontal(g1,g-6)
FEATURE [Sketcher::SketchObject] Sketch122
  ArcFitTolerance = 1e-06
  AttachmentSupport = -> [Pad011]
  ExternalGeometry = -> [Binder001]
  FullyConstrained = true
  MakeInternals = false
  MapMode = 5
  Placement = pos=(0,-2,0) rot=(1,0,0;1.5708rad)
  sketch-geometry (8):
    g0: ArcOfCircle CenterX=-184.801 CenterY=-67.3089 CenterZ=0 NormalX=0 NormalY=0 NormalZ=1 AngleXU=0 Radius=33.7833 StartAngle=2.70526 EndAngle=3.54053
    g1: LineSegment StartX=-176.685 StartY=-80.4316 StartZ=0 EndX=-215.932 EndY=-80.4316 EndZ=0
    g2: LineSegment StartX=-215.42 StartY=-53.0314 StartZ=0 EndX=-192.176 EndY=-3.18454 EndZ=0
    g3: ArcOfCircle CenterX=-207.583 CenterY=4 CenterZ=0 NormalX=0 NormalY=0 NormalZ=1 AngleXU=0 Radius=17 StartAngle=5.84685 EndAngle=7.56663
    g4: Circle CenterX=-213.443 CenterY=-76.8316 CenterZ=0 NormalX=0 NormalY=0 NormalZ=1 AngleXU=0 Radius=3
    g5: Circle CenterX=-179.305 CenterY=-76.8316 CenterZ=0 NormalX=0 NormalY=0 NormalZ=1 AngleXU=0 Radius=3
    g6: LineSegment StartX=-143.955 StartY=20.303 StartZ=0 EndX=-176.685 EndY=-80.4316 EndZ=0
    g7: LineSegment StartX=-202.765 StartY=20.303 StartZ=0 EndX=-143.955 EndY=20.303 EndZ=0
  constraints (18):
    c: Coincident(g0,g-7)
    c: Coincident(g0,g-8)
    c: Coincident(g1,g0)
    c: Tangent(g2,g-5)
    c: Coincident(g3,g-6)
    c: Coincident(g2,g3)
    c: Coincident(g0,g2)
    c: Diameter(g4) = 6
    c: Diameter(g5) = 6
    c: Coincident(g4,g-9)
    c: Coincident(g5,g-10)
    c: Horizontal(g1)
    c: Coincident(g6,g1)
    c: Tangent(g6,g-4)
    c: Coincident(g3,g-6)
    c: Coincident(g7,g3)
    c: Horizontal(g7)
    c: Coincident(g7,g6)
FEATURE [Sketcher::SketchObject] Sketch123
  ArcFitTolerance = 1e-06
  AttachmentSupport = -> [Pad011]
  ExternalGeometry = -> [Binder001]
  FullyConstrained = true
  MakeInternals = false
  MapMode = 5
  Placement = pos=(0,-2,0) rot=(1,0,0;1.5708rad)
  sketch-geometry (4):
    g0: LineSegment StartX=-108 StartY=36.8 StartZ=0 EndX=-90 EndY=36.8 EndZ=0
    g1: LineSegment StartX=-108 StartY=36.8 StartZ=0 EndX=-108 EndY=26.8 EndZ=0
    g2: LineSegment StartX=-108 StartY=26.8 StartZ=0 EndX=-90 EndY=26.8 EndZ=0
    g3: ArcOfCircle CenterX=-94 CenterY=31.8 CenterZ=0 NormalX=0 NormalY=0 NormalZ=1 AngleXU=0 Radius=6.40312 StartAngle=5.38713 EndAngle=7.17924
  constraints (13):
    c: Horizontal(g0)
    c: Coincident(g1,g0)
    c: Vertical(g1)
    c: Coincident(g2,g1)
    c: Horizontal(g2)
    c: DistanceX(g0,g0) = 18
    c: DistanceY(g1,g1) = 10
    c: Equal(g0,g2)
    c: DistanceX(g0,g-3) = 90
    c: DistanceY(g0,g-3) = 2.4
    c: Coincident(g3,g0)
    c: Coincident(g3,g2)
    c: DistanceX(g3,g0) = 4
FEATURE [PartDesign::Chamfer] Chamfer014
  Angle = 45
  Base = -> Pad011 [Edge80,Edge4,Edge7]
  BaseFeature = -> Pad011
  ChamferType = 0
  FlipDirection = false
  Refine = true
  Size = 1.9
  Size2 = 1
  SupportTransform = false
  Suppressed = false
  UseAllEdges = false
FEATURE [PartDesign::Pocket] Pocket006
  BaseFeature = -> Chamfer014
  Direction = (0,-1,2e-16)
  Length = 1.2
  Length2 = 5
  Profile = -> Sketch115
  ReferenceAxis = -> Sketch115 [N_Axis]
  Refine = true
  Suppressed = false
  Type = 0
FEATURE [Sketcher::SketchObject] Sketch116  label="Sketch116 - pieno per inserto M3 x 3 x 4,5"
  ArcFitTolerance = 1e-06
  AttachmentSupport = -> [Pocket006]
  ExternalGeometry = -> [Binder001]
  FullyConstrained = true
  MakeInternals = false
  MapMode = 5
  Placement = pos=(0,1.7e-15,0) rot=(0,0.707107,0.707107;3.14159rad)
  sketch-geometry (4):
    g0: Circle CenterX=43.2 CenterY=30.3 CenterZ=0 NormalX=0 NormalY=0 NormalZ=1 AngleXU=0 Radius=3.4
    g1: Circle CenterX=43.2 CenterY=12.1 CenterZ=0 NormalX=0 NormalY=0 NormalZ=1 AngleXU=0 Radius=3.4
    g2: Circle CenterX=18.6 CenterY=30.3 CenterZ=0 NormalX=0 NormalY=0 NormalZ=1 AngleXU=0 Radius=3.4
    g3: Circle CenterX=18.6 CenterY=12.1 CenterZ=0 NormalX=0 NormalY=0 NormalZ=1 AngleXU=0 Radius=3.4
  constraints (8):
    c: Diameter(g0) = 6.8
    c: Diameter(g1) = 6.8
    c: Diameter(g2) = 6.8
    c: Diameter(g3) = 6.8
    c: Coincident(g2,g-3)
    c: Coincident(g0,g-4)
    c: Coincident(g3,g-6)
    c: Coincident(g1,g-5)
FEATURE [PartDesign::Pad] Pad012
  BaseFeature = -> Pocket006
  Direction = (0,1,-2e-16)
  Length = 2.4
  Length2 = 10
  Profile = -> Sketch116
  ReferenceAxis = -> Sketch116 [N_Axis]
  Refine = true
  Suppressed = false
  Type = 0
FEATURE [PartDesign::Pocket] Pocket007
  BaseFeature = -> Pad012
  Direction = (0,-1,2e-16)
  Length = 0.6
  Length2 = 2.4
  Profile = -> Sketch117
  ReferenceAxis = -> Sketch117 [N_Axis]
  Refine = true
  Suppressed = false
  Type = 4
FEATURE [PartDesign::Pad] Pad013
  BaseFeature = -> Pocket007
  Direction = (0,-1,2e-16)
  Length = 1.6
  Length2 = 10
  Profile = -> Sketch118
  ReferenceAxis = -> Sketch118 [N_Axis]
  Refine = true
  Suppressed = false
  Type = 0
FEATURE [Sketcher::SketchObject] Sketch119
  ArcFitTolerance = 1e-06
  AttachmentSupport = -> [Pad013]
  ExternalGeometry = -> [Binder001]
  FullyConstrained = true
  MakeInternals = false
  MapMode = 5
  Placement = pos=(0,-3.6,0) rot=(1,0,0;1.5708rad)
  sketch-geometry (21):
    g0: LineSegment [constr] StartX=-82.8 StartY=3.2 StartZ=0 EndX=-82.8 EndY=39.2 EndZ=0
    g1: ArcOfCircle CenterX=-78.51 CenterY=34.8 CenterZ=0 NormalX=0 NormalY=0 NormalZ=1 AngleXU=0 Radius=3.5 StartAngle=4.71239 EndAngle=6.28319
    g2: ArcOfCircle CenterX=-78.51 CenterY=7.6 CenterZ=0 NormalX=0 NormalY=0 NormalZ=1 AngleXU=0 Radius=3.5 StartAngle=0 EndAngle=1.5708
    g3: ArcOfCircle CenterX=-5.6 CenterY=34.8 CenterZ=0 NormalX=0 NormalY=0 NormalZ=1 AngleXU=0 Radius=3.5 StartAngle=3.14159 EndAngle=4.71239
    g4: ArcOfCircle CenterX=-5.6 CenterY=7.6 CenterZ=0 NormalX=0 NormalY=0 NormalZ=1 AngleXU=0 Radius=3.5 StartAngle=1.5708 EndAngle=3.14159
    g5: LineSegment StartX=0 StartY=39.2 StartZ=0 EndX=0 EndY=31.3 EndZ=0
    g6: LineSegment StartX=0 StartY=39.2 StartZ=0 EndX=-9.1 EndY=39.2 EndZ=0
    g7: LineSegment StartX=0 StartY=3.2 StartZ=0 EndX=0 EndY=11.1 EndZ=0
    g8: LineSegment StartX=0 StartY=3.2 StartZ=0 EndX=-9.1 EndY=3.2 EndZ=0
    g9: LineSegment StartX=-82.8 StartY=3.2 StartZ=0 EndX=-75.01 EndY=3.2 EndZ=0
    g10: LineSegment StartX=-82.8 StartY=3.2 StartZ=0 EndX=-82.8 EndY=11.1 EndZ=0
    g11: LineSegment StartX=-82.8 StartY=39.2 StartZ=0 EndX=-82.8 EndY=31.3 EndZ=0
    g12: LineSegment StartX=-82.8 StartY=39.2 StartZ=0 EndX=-75.01 EndY=39.2 EndZ=0
    g13: LineSegment StartX=-82.8 StartY=31.3 StartZ=0 EndX=-78.51 EndY=31.3 EndZ=0
    g14: LineSegment StartX=-75.01 StartY=39.2 StartZ=0 EndX=-75.01 EndY=34.8 EndZ=0
    g15: LineSegment StartX=-82.8 StartY=11.1 StartZ=0 EndX=-78.51 EndY=11.1 EndZ=0
    g16: LineSegment StartX=-75.01 StartY=3.2 StartZ=0 EndX=-75.01 EndY=7.6 EndZ=0
    g17: LineSegment StartX=-9.1 StartY=39.2 StartZ=0 EndX=-9.1 EndY=34.8 EndZ=0
    g18: LineSegment StartX=0 StartY=31.3 StartZ=0 EndX=-5.6 EndY=31.3 EndZ=0
    g19: LineSegment StartX=0 StartY=11.1 StartZ=0 EndX=-5.6 EndY=11.1 EndZ=0
    g20: LineSegment StartX=-9.1 StartY=3.2 StartZ=0 EndX=-9.1 EndY=7.6 EndZ=0
  constraints (51):
    c: Coincident(g0,g-10)
    c: PointOnObject(g0,g-8)
    c: Vertical(g0)
    c: Coincident(g1,g-3)
    c: Coincident(g2,g-4)
    c: Coincident(g3,g-5)
    c: Coincident(g4,g-6)
    c: Radius(g4) = 3.5
    c: Radius(g3) = 3.5
    c: Radius(g1) = 3.5
    c: Radius(g2) = 3.5
    c: Coincident(g5,g-9)
    c: PointOnObject(g5,g-9)
    c: Coincident(g6,g5)
    c: PointOnObject(g6,g-8)
    c: Coincident(g7,g-9)
    c: PointOnObject(g7,g-9)
    c: Coincident(g8,g7)
    c: PointOnObject(g8,g-7)
    c: Coincident(g9,g0)
    c: PointOnObject(g9,g-7)
    c: Coincident(g10,g0)
    c: PointOnObject(g10,g0)
    c: Coincident(g11,g0)
    c: PointOnObject(g11,g0)
    c: Coincident(g12,g0)
    c: PointOnObject(g12,g-8)
    c: Coincident(g13,g11)
    c: Horizontal(g13)
    c: Coincident(g14,g12)
    c: Vertical(g14)
    c: Coincident(g15,g10)
    c: Horizontal(g15)
    c: Coincident(g16,g9)
    c: Vertical(g16)
    c: Coincident(g17,g6)
    c: Vertical(g17)
    c: Coincident(g18,g5)
    c: Horizontal(g18)
    c: Coincident(g19,g7)
    c: Horizontal(g19)
    c: Coincident(g20,g8)
    c: Vertical(g20)
    c: Tangent(g20,g4) = 1.5708
    c: Tangent(g4,g19) = -1.5708
    c: Tangent(g18,g3) = 1.5708
    c: Tangent(g3,g17) = -1.5708
    c: Tangent(g13,g1) = -1.5708
    c: Tangent(g1,g14) = 1.5708
    c: Tangent(g16,g2) = -1.5708
    c: Tangent(g2,g15) = 1.5708
FEATURE [PartDesign::Pocket] Pocket008
  BaseFeature = -> Pad013
  Direction = (0,1,-2e-16)
  Length = 1.6
  Length2 = 5
  Profile = -> Sketch119
  ReferenceAxis = -> Sketch119 [N_Axis]
  Refine = true
  Suppressed = false
  Type = 0
FEATURE [PartDesign::Pad] Pad017
  BaseFeature = -> Pocket008
  Direction = (0,-1,2e-16)
  Length = 1.6
  Length2 = 10
  Profile = -> Sketch123
  ReferenceAxis = -> Sketch123 [N_Axis]
  Refine = true
  Suppressed = false
  Type = 0
FEATURE [Sketcher::SketchObject] Sketch125
  ArcFitTolerance = 1e-06
  AttachmentSupport = -> [Pad017]
  ExternalGeometry = -> [Pad017]
  FullyConstrained = true
  MakeInternals = false
  MapMode = 5
  Placement = pos=(0,-3.6,8e-16) rot=(1,0,0;1.5708rad)
  sketch-geometry (20):
    g0: LineSegment StartX=-108 StartY=35.8 StartZ=0 EndX=-108 EndY=35 EndZ=0
    g1: LineSegment StartX=-108 StartY=35 StartZ=0 EndX=-97 EndY=35 EndZ=0
    g2: LineSegment StartX=-97 StartY=35 StartZ=0 EndX=-97 EndY=35.8 EndZ=0
    g3: LineSegment StartX=-97 StartY=35.8 StartZ=0 EndX=-108 EndY=35.8 EndZ=0
    g4: LineSegment StartX=-108 StartY=28.6 StartZ=0 EndX=-108 EndY=27.8 EndZ=0
    g5: LineSegment StartX=-108 StartY=27.8 StartZ=0 EndX=-97 EndY=27.8 EndZ=0
    g6: LineSegment StartX=-97 StartY=27.8 StartZ=0 EndX=-97 EndY=28.6 EndZ=0
    g7: LineSegment StartX=-97 StartY=28.6 StartZ=0 EndX=-108 EndY=28.6 EndZ=0
    g8: LineSegment StartX=-108 StartY=30.4 StartZ=0 EndX=-108 EndY=29.6 EndZ=0
    g9: LineSegment StartX=-108 StartY=29.6 StartZ=0 EndX=-97 EndY=29.6 EndZ=0
    g10: LineSegment StartX=-97 StartY=29.6 StartZ=0 EndX=-97 EndY=30.4 EndZ=0
    g11: LineSegment StartX=-97 StartY=30.4 StartZ=0 EndX=-108 EndY=30.4 EndZ=0
    g12: LineSegment StartX=-108 StartY=32.2 StartZ=0 EndX=-108 EndY=31.4 EndZ=0
    g13: LineSegment StartX=-108 StartY=31.4 StartZ=0 EndX=-97 EndY=31.4 EndZ=0
    g14: LineSegment StartX=-97 StartY=31.4 StartZ=0 EndX=-97 EndY=32.2 EndZ=0
    g15: LineSegment StartX=-97 StartY=32.2 StartZ=0 EndX=-108 EndY=32.2 EndZ=0
    g16: LineSegment StartX=-108 StartY=34 StartZ=0 EndX=-108 EndY=33.2 EndZ=0
    g17: LineSegment StartX=-108 StartY=33.2 StartZ=0 EndX=-97 EndY=33.2 EndZ=0
    g18: LineSegment StartX=-97 StartY=33.2 StartZ=0 EndX=-97 EndY=34 EndZ=0
    g19: LineSegment StartX=-97 StartY=34 StartZ=0 EndX=-108 EndY=34 EndZ=0
  constraints (55):
    c: Coincident(g1,g0)
    c: Horizontal(g1)
    c: Coincident(g2,g1)
    c: Vertical(g2)
    c: Coincident(g3,g2)
    c: Horizontal(g3)
    c: Coincident(g3,g0)
    c: DistanceX(g1,g1) = 11
    c: DistanceY(g2,g2) = 0.8
    c: Coincident(g5,g4)
    c: Horizontal(g5)
    c: Coincident(g6,g5)
    c: Vertical(g6)
    c: Coincident(g7,g6)
    c: Horizontal(g7)
    c: Coincident(g7,g4)
    c: Coincident(g9,g8)
    c: Horizontal(g9)
    c: Coincident(g10,g9)
    c: Vertical(g10)
    c: Coincident(g11,g10)
    c: Horizontal(g11)
    c: Coincident(g11,g8)
    c: Coincident(g13,g12)
    c: Horizontal(g13)
    c: Coincident(g14,g13)
    c: Vertical(g14)
    c: Coincident(g15,g14)
    c: Horizontal(g15)
    c: Coincident(g15,g12)
    c: Coincident(g17,g16)
    c: Horizontal(g17)
    c: Coincident(g18,g17)
    c: Vertical(g18)
    c: Coincident(g19,g18)
    c: Horizontal(g19)
    c: Coincident(g19,g16)
    c: Equal(g3,g19)
    c: Equal(g3,g15)
    c: Equal(g3,g11)
    c: Equal(g3,g7)
    c: Equal(g2,g18)
    c: Equal(g2,g14)
    c: Equal(g2,g10)
    c: Equal(g2,g6)
    c: DistanceY(g-4,g4) = 1
    c: DistanceY(g4,g8) = 1
    c: DistanceY(g8,g12) = 1
    c: DistanceY(g12,g16) = 1
    c: DistanceY(g16,g0) = 1
    c: Tangent(g0,g-5)
    c: Tangent(g16,g-5)
    c: Tangent(g12,g-5)
    c: Tangent(g8,g-5)
    c: Tangent(g4,g-5)
FEATURE [PartDesign::Chamfer] Chamfer009
  Angle = 45
  Base = -> Pad017 [Edge151,Edge154]
  BaseFeature = -> Pad017
  ChamferType = 1
  FlipDirection = false
  Refine = true
  Size = 1.5
  Size2 = 2.8
  SupportTransform = false
  Suppressed = false
  UseAllEdges = false
FEATURE [PartDesign::Pocket] Pocket009
  BaseFeature = -> Chamfer009
  Direction = (0,1,-2e-16)
  Length = 1
  Length2 = 5
  Profile = -> Sketch125
  ReferenceAxis = -> Sketch125 [N_Axis]
  Refine = true
  Suppressed = false
  Type = 0
FEATURE [PartDesign::Pad] Pad014
  BaseFeature = -> Pocket009
  Direction = (0,-1,2e-16)
  Length = 0.8
  Length2 = 10
  Profile = -> Sketch120
  ReferenceAxis = -> Sketch120 [N_Axis]
  Refine = true
  Suppressed = false
  Type = 0
FEATURE [Sketcher::SketchObject] Sketch124
  ArcFitTolerance = 1e-06
  AttachmentSupport = -> [Pad014]
  ExternalGeometry = -> [Binder001]
  FullyConstrained = true
  MakeInternals = false
  MapMode = 5
  Placement = pos=(0,-2.8,6e-16) rot=(1,0,0;1.5708rad)
  sketch-geometry (4):
    g0: LineSegment StartX=-129 StartY=39.2 StartZ=0 EndX=-131.599 EndY=31.2 EndZ=0
    g1: LineSegment StartX=-118 StartY=39.2 StartZ=0 EndX=-120.599 EndY=31.2 EndZ=0
    g2: LineSegment StartX=-129 StartY=39.2 StartZ=0 EndX=-118 EndY=39.2 EndZ=0
    g3: LineSegment StartX=-120.599 StartY=31.2 StartZ=0 EndX=-131.599 EndY=31.2 EndZ=0
  constraints (12):
    c: PointOnObject(g0,g-3)
    c: PointOnObject(g1,g-3)
    c: Parallel(g-4,g0)
    c: Parallel(g-4,g1)
    c: Coincident(g2,g0)
    c: Coincident(g2,g1)
    c: DistanceX(g2,g2) = 11
    c: DistanceY(g1,g1) = 8
    c: Coincident(g3,g1)
    c: Horizontal(g3)
    c: Coincident(g3,g0)
    c: DistanceX(g1,g-3) = 118
FEATURE [PartDesign::Pad] Pad018
  BaseFeature = -> Pad014
  Direction = (0,-1,2e-16)
  Length = 1.2
  Length2 = 10
  Profile = -> Sketch124
  ReferenceAxis = -> Sketch124 [N_Axis]
  Refine = true
  Suppressed = false
  Type = 0
FEATURE [Sketcher::SketchObject] Sketch126
  ArcFitTolerance = 1e-06
  AttachmentSupport = -> [Pad018]
  ExternalGeometry = -> [Pad018]
  FullyConstrained = true
  MakeInternals = false
  MapMode = 5
  Placement = pos=(0,-4,0) rot=(1,0,0;1.5708rad)
  sketch-geometry (8):
    g0: LineSegment StartX=-129.877 StartY=36.5 StartZ=0 EndX=-130.137 EndY=35.7 EndZ=0
    g1: LineSegment StartX=-130.69 StartY=34 StartZ=0 EndX=-130.95 EndY=33.2 EndZ=0
    g2: LineSegment StartX=-129.877 StartY=36.5 StartZ=0 EndX=-118.877 EndY=36.5 EndZ=0
    g3: LineSegment StartX=-130.137 StartY=35.7 StartZ=0 EndX=-119.137 EndY=35.7 EndZ=0
    g4: LineSegment StartX=-130.69 StartY=34 StartZ=0 EndX=-119.69 EndY=34 EndZ=0
    g5: LineSegment StartX=-130.95 StartY=33.2 StartZ=0 EndX=-119.95 EndY=33.2 EndZ=0
    g6: LineSegment StartX=-118.877 StartY=36.5 StartZ=0 EndX=-119.137 EndY=35.7 EndZ=0
    g7: LineSegment StartX=-119.69 StartY=34 StartZ=0 EndX=-119.95 EndY=33.2 EndZ=0
  constraints (20):
    c: Coincident(g2,g0)
    c: Horizontal(g2)
    c: Coincident(g3,g0)
    c: Horizontal(g3)
    c: Coincident(g4,g1)
    c: Horizontal(g4)
    c: Coincident(g5,g1)
    c: Horizontal(g5)
    c: Coincident(g6,g2)
    c: Coincident(g6,g3)
    c: Coincident(g7,g4)
    c: Coincident(g7,g5)
    c: Tangent(g0,g-4)
    c: Tangent(g6,g-5)
    c: Tangent(g1,g-4)
    c: Tangent(g7,g-5)
    c: DistanceY(g3,g2) = 0.8
    c: DistanceY(g5,g4) = 0.8
    c: DistanceY(g-6,g1) = 2
    c: DistanceY(g-6,g0) = 4.5
FEATURE [PartDesign::Chamfer] Chamfer008
  Angle = 45
  Base = -> Pad018 [Edge257]
  BaseFeature = -> Pad018
  ChamferType = 1
  FlipDirection = false
  Refine = true
  Size = 1
  Size2 = 6
  SupportTransform = false
  Suppressed = false
  UseAllEdges = false
FEATURE [PartDesign::Pocket] Pocket010
  BaseFeature = -> Chamfer008
  Direction = (0,1,-2e-16)
  Length = 1
  Length2 = 5
  Profile = -> Sketch126
  ReferenceAxis = -> Sketch126 [N_Axis]
  Refine = true
  Suppressed = false
  Type = 0
FEATURE [PartDesign::Pad] Pad015
  BaseFeature = -> Pocket010
  Direction = (0,-1,2e-16)
  Length = 2
  Length2 = 10
  Profile = -> Sketch121
  ReferenceAxis = -> Sketch121 [N_Axis]
  Refine = true
  Suppressed = false
  Type = 0
FEATURE [PartDesign::Pad] Pad016
  BaseFeature = -> Pad015
  Direction = (0,-1,2e-16)
  Length = 1.6
  Length2 = 10
  Profile = -> Sketch122
  ReferenceAxis = -> Sketch122 [N_Axis]
  Refine = true
  Suppressed = false
  Type = 0
FEATURE [Sketcher::SketchObject] Sketch129
  ArcFitTolerance = 1e-06
  AttachmentSupport = -> [Pad016]
  ExternalGeometry = -> [Binder001]
  FullyConstrained = true
  MakeInternals = false
  MapMode = 5
  Placement = pos=(0,-3.6,0) rot=(1,0,0;1.5708rad)
  sketch-geometry (12):
    g0: LineSegment [constr] StartX=-192.176 StartY=-3.18451 StartZ=0 EndX=-181.223 EndY=20.303 EndZ=0
    g1: LineSegment [constr] StartX=-202.765 StartY=20.303 StartZ=0 EndX=-181.223 EndY=20.303 EndZ=0
    g2: LineSegment StartX=-202.765 StartY=20.303 StartZ=0 EndX=-181.223 EndY=20.303 EndZ=0
    g3: LineSegment StartX=-192.176 StartY=-3.18451 StartZ=0 EndX=-196.804 EndY=-13.1107 EndZ=0
    g4: ArcOfCircle CenterX=-207.583 CenterY=4 CenterZ=0 NormalX=0 NormalY=0 NormalZ=1 AngleXU=0 Radius=17 StartAngle=5.84685 EndAngle=7.56663
    g5: ArcOfEllipse CenterX=-181.223 CenterY=8.55923 CenterZ=0 NormalX=0 NormalY=0 NormalZ=1 MajorRadius=23.4779 MinorRadius=11.7437 AngleXU=2e-16 StartAngle=4.71239 EndAngle=7.85398
    g6: LineSegment [constr] StartX=-157.745 StartY=8.55923 StartZ=0 EndX=-204.701 EndY=8.55923 EndZ=0
    g7: LineSegment [constr] StartX=-181.223 StartY=20.303 StartZ=0 EndX=-181.223 EndY=-3.18451 EndZ=0
    g8: GeomPoint [constr] X=-160.894 Y=8.55923 Z=0
    g9: GeomPoint [constr] X=-201.553 Y=8.55923 Z=0
    g10: ArcOfCircle CenterX=-181.223 CenterY=-20.3763 CenterZ=0 NormalX=0 NormalY=0 NormalZ=1 AngleXU=0 Radius=17.1918 StartAngle=1.57079 EndAngle=2.70526
    g11: GeomPoint [constr] X=-181.223 Y=-3.18451 Z=0
  constraints (23):
    c: Coincident(g0,g-5)
    c: Coincident(g1,g-6)
    c: Horizontal(g1)
    c: Coincident(g1,g0)
    c: Parallel(g0,g-4)
    c: Coincident(g2,g1)
    c: Coincident(g2,g0)
    c: Coincident(g3,g0)
    c: Equal(g4,g-5)
    c: Coincident(g4,g1)
    c: Coincident(g4,g0)
    c: InternalAlignment(g6-g9 -> g5) x4
    c: Vertical(g5,g0)
    c: Horizontal(g6)
    c: Coincident(g5,g0)
    c: DistanceX(g6,g-3) = 10.1
    c: Tangent(g10,g3) = -1.5708
    c: PointOnObject(g11,g10)
    c: Tangent(g5,g10,g11) = 1.5708
    c: Coincident(g10,g5)
    c: Coincident(g11,g7)
    c: Parallel(g3,g-4)
    c: Horizontal(g5,g0)
FEATURE [Sketcher::SketchObject] Sketch130
  ArcFitTolerance = 1e-06
  AttachmentOffset = pos=(0,0,-1.6) rot=(0,0,1;0rad)
  AttachmentSupport = -> [Pad016]
  ExternalGeometry = -> [Binder001]
  FullyConstrained = true
  MakeInternals = false
  MapMode = 5
  Placement = pos=(0,-2,-4e-16) rot=(1,0,0;1.5708rad)
  sketch-geometry (12):
    g0: LineSegment [constr] StartX=-192.176 StartY=-3.18451 StartZ=0 EndX=-181.223 EndY=20.303 EndZ=0
    g1: LineSegment [constr] StartX=-202.765 StartY=20.303 StartZ=0 EndX=-181.223 EndY=20.303 EndZ=0
    g2: LineSegment StartX=-202.765 StartY=20.303 StartZ=0 EndX=-181.223 EndY=20.303 EndZ=0
    g3: LineSegment StartX=-192.176 StartY=-3.18451 StartZ=0 EndX=-193.827 EndY=-6.72678 EndZ=0
    g4: ArcOfCircle CenterX=-207.583 CenterY=4 CenterZ=0 NormalX=0 NormalY=0 NormalZ=1 AngleXU=0 Radius=17 StartAngle=5.84685 EndAngle=7.56663
    g5: ArcOfEllipse CenterX=-181.223 CenterY=10.803 CenterZ=0 NormalX=0 NormalY=0 NormalZ=1 MajorRadius=14.4779 MinorRadius=9.5 AngleXU=0 StartAngle=4.71239 EndAngle=7.85398
    g6: LineSegment [constr] StartX=-166.745 StartY=10.803 StartZ=0 EndX=-195.701 EndY=10.803 EndZ=0
    g7: LineSegment [constr] StartX=-181.223 StartY=20.303 StartZ=0 EndX=-181.223 EndY=1.30297 EndZ=0
    g8: GeomPoint [constr] X=-170.298 Y=10.803 Z=0
    g9: GeomPoint [constr] X=-192.148 Y=10.803 Z=0
    g10: ArcOfCircle CenterX=-181.223 CenterY=-12.6042 CenterZ=0 NormalX=0 NormalY=0 NormalZ=1 AngleXU=0 Radius=13.9072 StartAngle=1.5708 EndAngle=2.70526
    g11: GeomPoint [constr] X=-181.223 Y=1.30297 Z=0
  constraints (23):
    c: Coincident(g0,g-5)
    c: Coincident(g1,g-6)
    c: Horizontal(g1)
    c: Coincident(g1,g0)
    c: Parallel(g0,g-4)
    c: Coincident(g2,g1)
    c: Coincident(g2,g0)
    c: Coincident(g3,g0)
    c: Equal(g4,g-5)
    c: Coincident(g4,g1)
    c: Coincident(g4,g0)
    c: InternalAlignment(g6-g9 -> g5) x4
    c: Vertical(g5,g0)
    c: Horizontal(g6)
    c: Coincident(g5,g0)
    c: DistanceX(g6,g-3) = 19.1
    c: Tangent(g10,g3) = -1.5708
    c: PointOnObject(g11,g10)
    c: Tangent(g5,g10,g11) = 1.5708
    c: Coincident(g10,g5)
    c: Coincident(g11,g7)
    c: Parallel(g3,g-4)
    c: DistanceY(g5,g0) = 19
FEATURE [Part::Part2DObjectPython] Clone2D001  label="Sketch130 (2D)"  # Draft 2D object (typed FeaturePython)
  Fuse = false
  Objects = -> [Sketch130]
  Placement = pos=(0,-2,-4e-16) rot=(1,0,0;1.5708rad)
  Scale = (1,1,1)
FEATURE [Sketcher::SketchObject] Sketch131
  ArcFitTolerance = 1e-06
  AttachmentOffset = pos=(0,0,-3.5) rot=(0,0,1;0rad)
  AttachmentSupport = -> [Pad016]
  ExternalGeometry = -> [Binder001]
  FullyConstrained = true
  MakeInternals = false
  MapMode = 5
  Placement = pos=(0,-0.1,-8e-16) rot=(1,0,0;1.5708rad)
  sketch-geometry (1):
    g0: GeomPoint X=-197.47 Y=8.55923 Z=0
  constraints (1):
    c: Symmetric(g-6,g-4,g0)
FEATURE [Sketcher::SketchObject] Sketch132
  ArcFitTolerance = 1e-06
  AttachmentSupport = -> [Pad016]
  ExternalGeometry = -> [Binder001]
  FullyConstrained = true
  MakeInternals = false
  MapMode = 5
  Placement = pos=(0,-3.6,0) rot=(1,0,0;1.5708rad)
  sketch-geometry (3):
    g0: LineSegment [constr] StartX=-215.42 StartY=-53.0314 StartZ=0 EndX=-167.782 EndY=-53.0314 EndZ=0
    g1: Circle CenterX=-191.282 CenterY=-53.0314 CenterZ=0 NormalX=0 NormalY=0 NormalZ=1 AngleXU=0 Radius=11.5
    g2: Circle CenterX=-191.282 CenterY=-53.0314 CenterZ=0 NormalX=0 NormalY=0 NormalZ=1 AngleXU=0 Radius=10.7
  constraints (8):
    c: Coincident(g0,g-3)
    c: PointOnObject(g0,g-4)
    c: Horizontal(g0)
    c: Diameter(g1) = 23
    c: PointOnObject(g1,g0)
    c: DistanceX(g1,g0) = 23.5
    c: Diameter(g2) = 21.4
    c: Coincident(g2,g1)
FEATURE [Part::Part2DObjectPython] ShapeString  # Draft 2D object (typed FeaturePython)
  FontFile = <path>
  Fuse = false
  Justification = 6
  JustificationReference = 0
  KeepLeftMargin = false
  MakeFace = true
  ObliqueAngle = 0
  Placement = pos=(-199,-3.6,-57.5) rot=(1,0,0;1.5708rad)
  ScaleToSize = true
  Size = 10
  String = AS
  Tracking = 0
FEATURE [Sketcher::SketchObject] Sketch133
  ArcFitTolerance = 1e-06
  AttachmentSupport = -> [Binder]
  ExternalGeometry = -> [Binder]
  FullyConstrained = true
  MakeInternals = false
  MapMode = 5
  Placement = pos=(0,9e-16,0) rot=(0,0.707107,0.707107;3.14159rad)
  sketch-geometry (30):
    g0: LineSegment StartX=0 StartY=39.2 StartZ=0 EndX=0 EndY=3.2 EndZ=0
    g1: LineSegment StartX=0 StartY=3.2 StartZ=0 EndX=82.8 EndY=3.2 EndZ=0
    g2: LineSegment StartX=82.8 StartY=3.2 StartZ=0 EndX=82.8 EndY=6.2 EndZ=0
    g3: LineSegment StartX=82.8 StartY=6.2 StartZ=0 EndX=91.752 EndY=6.2 EndZ=0
    g4: LineSegment StartX=0 StartY=39.2 StartZ=0 EndX=195.887 EndY=39.2 EndZ=0
    g5: LineSegment StartX=195.887 StartY=39.2 StartZ=0 EndX=202.765 EndY=20.303 EndZ=0
    g6: LineSegment StartX=192.333 StartY=24.9893 StartZ=0 EndX=196.467 EndY=26.4942 EndZ=0
    g7: LineSegment StartX=196.467 StartY=26.4942 StartZ=0 EndX=194.073 EndY=33.0721 EndZ=0
    g8: LineSegment StartX=194.073 StartY=33.0721 StartZ=0 EndX=189.939 EndY=31.5672 EndZ=0
    g9: LineSegment StartX=189.939 StartY=31.5672 StartZ=0 EndX=192.333 EndY=24.9893 EndZ=0
    g10: ArcOfCircle CenterX=107.6 CenterY=4 CenterZ=0 NormalX=0 NormalY=0 NormalZ=1 AngleXU=0 Radius=16 StartAngle=1.5708 EndAngle=3.00366
    g11: LineSegment StartX=107.6 StartY=20 StartZ=0 EndX=132.428 EndY=20 EndZ=0
    g12: ArcOfCircle [constr] CenterX=132.428 CenterY=4 CenterZ=0 NormalX=0 NormalY=0 NormalZ=1 AngleXU=0 Radius=16 StartAngle=0.314159 EndAngle=1.5708
    g13: LineSegment StartX=147.645 StartY=8.94427 StartZ=0 EndX=176.685 EndY=-80.4316 EndZ=0
    g14: LineSegment StartX=176.685 StartY=-80.4316 StartZ=0 EndX=215.932 EndY=-80.4316 EndZ=0
    g15: ArcOfCircle CenterX=207.583 CenterY=4 CenterZ=0 NormalX=0 NormalY=0 NormalZ=1 AngleXU=0 Radius=17 StartAngle=1.85815 EndAngle=3.57792
    g16: ArcOfCircle CenterX=184.801 CenterY=-67.3089 CenterZ=0 NormalX=0 NormalY=0 NormalZ=1 AngleXU=0 Radius=33.7833 StartAngle=5.88425 EndAngle=6.71952
    g17: LineSegment StartX=192.176 StartY=-3.18451 StartZ=0 EndX=215.42 EndY=-53.0314 EndZ=0
    g18: Circle CenterX=5.6 CenterY=34.8 CenterZ=0 NormalX=0 NormalY=0 NormalZ=1 AngleXU=0 Radius=1.8
    g19: Circle CenterX=5.6 CenterY=7.6 CenterZ=0 NormalX=0 NormalY=0 NormalZ=1 AngleXU=0 Radius=1.8
    g20: Circle CenterX=78.51 CenterY=34.8 CenterZ=0 NormalX=0 NormalY=0 NormalZ=1 AngleXU=0 Radius=1.8
    g21: Circle CenterX=78.51 CenterY=7.6 CenterZ=0 NormalX=0 NormalY=0 NormalZ=1 AngleXU=0 Radius=1.8
    g22: Circle CenterX=184.08 CenterY=34.8 CenterZ=0 NormalX=0 NormalY=0 NormalZ=1 AngleXU=0 Radius=1.8
    g23: Circle CenterX=179.305 CenterY=-76.8316 CenterZ=0 NormalX=0 NormalY=0 NormalZ=1 AngleXU=0 Radius=1.8
    g24: Circle CenterX=213.443 CenterY=-76.8316 CenterZ=0 NormalX=0 NormalY=0 NormalZ=1 AngleXU=0 Radius=1.8
    g25: Circle CenterX=19 CenterY=21.2 CenterZ=0 NormalX=0 NormalY=0 NormalZ=1 AngleXU=0 Radius=6.3
    g26: Circle CenterX=42 CenterY=21.2 CenterZ=0 NormalX=0 NormalY=0 NormalZ=1 AngleXU=0 Radius=6.3
    g27: Circle CenterX=65 CenterY=21.2 CenterZ=0 NormalX=0 NormalY=0 NormalZ=1 AngleXU=0 Radius=6.3
    g28: LineSegment StartX=132.428 StartY=20 StartZ=0 EndX=144.053 EndY=20 EndZ=0
    g29: LineSegment StartX=147.645 StartY=8.94427 StartZ=0 EndX=144.053 EndY=20 EndZ=0
  constraints (65):
    c: Coincident(g0,g-4)
    c: Coincident(g0,g-5)
    c: Coincident(g1,g0)
    c: Coincident(g1,g-6)
    c: Coincident(g2,g1)
    c: Coincident(g2,g-7)
    c: Coincident(g3,g2)
    c: Coincident(g3,g-8)
    c: Coincident(g4,g0)
    c: Coincident(g4,g-16)
    c: Coincident(g5,g4)
    c: Coincident(g5,g-16)
    c: Coincident(g6,g-20)
    c: Coincident(g6,g-21)
    c: Coincident(g7,g6)
    c: Coincident(g7,g-23)
    c: Coincident(g8,g7)
    c: Coincident(g8,g-22)
    c: Coincident(g9,g8)
    c: Coincident(g9,g6)
    c: Equal(g10,g-8)
    c: Coincident(g10,g3)
    c: Coincident(g10,g-9)
    c: Coincident(g11,g10)
    c: Coincident(g11,g-10)
    c: Equal(g12,g-10)
    c: Coincident(g12,g11)
    c: Coincident(g12,g-11)
    c: Coincident(g13,g12)
    c: Coincident(g13,g-12)
    c: Coincident(g14,g13)
    c: Coincident(g14,g-13)
    c: Equal(g15,g-15)
    c: Coincident(g15,g5)
    c: Coincident(g15,g-15)
    c: Equal(g16,g-13)
    c: Coincident(g16,g14)
    c: Coincident(g16,g-14)
    c: Coincident(g17,g15)
    c: Coincident(g17,g16)
    c: Equal(g18,g-28)
    c: Equal(g19,g-29)
    c: Equal(g20,g-26)
    c: Equal(g21,g-27)
    c: Equal(g22,g-17)
    c: Equal(g24,g-25)
    c: Equal(g23,g-24)
    c: Coincident(g23,g-24)
    c: Coincident(g24,g-25)
    c: Coincident(g22,g-17)
    c: Coincident(g20,g-26)
    c: Coincident(g21,g-27)
    c: Coincident(g18,g-28)
    c: Coincident(g19,g-29)
    c: Equal(g25,g-30)
    c: Equal(g26,g-31)
    c: Equal(g27,g-32)
    c: Coincident(g25,g-30)
    c: Coincident(g26,g-31)
    c: Coincident(g27,g-32)
    c: Parallel(g28,g11)
    c: Parallel(g29,g13)
    c: Coincident(g28,g11)
    c: Coincident(g29,g12)
    c: Coincident(g29,g28)
FEATURE [PartDesign::Pad] Pad019
  Direction = (0,1,-2e-16)
  Length = 2
  Length2 = 10
  Profile = -> Sketch133
  ReferenceAxis = -> Sketch133 [N_Axis]
  Refine = true
  Suppressed = false
  Type = 0
FEATURE [Sketcher::SketchObject] Sketch091  label="Sketch091 - forma anteriore"
  ArcFitTolerance = 1e-06
  AttachmentSupport = -> [Pad019]
  ExternalGeometry = -> [Binder]
  FullyConstrained = true
  MakeInternals = false
  MapMode = 5
  Placement = pos=(0,2,0) rot=(0,0.707107,0.707107;3.14159rad)
  sketch-geometry (12):
    g0: Circle CenterX=5.6 CenterY=34.8 CenterZ=0 NormalX=0 NormalY=0 NormalZ=1 AngleXU=0 Radius=1.8
    g1: Circle CenterX=5.6 CenterY=7.6 CenterZ=0 NormalX=0 NormalY=0 NormalZ=1 AngleXU=0 Radius=1.8
    g2: Circle CenterX=78.51 CenterY=34.8 CenterZ=0 NormalX=0 NormalY=0 NormalZ=1 AngleXU=0 Radius=1.8
    g3: Circle CenterX=78.51 CenterY=7.6 CenterZ=0 NormalX=0 NormalY=0 NormalZ=1 AngleXU=0 Radius=1.8
    g4: LineSegment StartX=0 StartY=39.2 StartZ=0 EndX=0 EndY=3.2 EndZ=0
    g5: LineSegment StartX=0 StartY=3.2 StartZ=0 EndX=82.8 EndY=3.2 EndZ=0
    g6: LineSegment StartX=82.8 StartY=3.2 StartZ=0 EndX=82.8 EndY=39.2 EndZ=0
    g7: LineSegment StartX=82.8 StartY=39.2 StartZ=0 EndX=0 EndY=39.2 EndZ=0
    g8: ArcOfCircle CenterX=19 CenterY=21.2 CenterZ=0 NormalX=0 NormalY=0 NormalZ=1 AngleXU=0 Radius=10 StartAngle=1.5708 EndAngle=4.71239
    g9: ArcOfCircle CenterX=65 CenterY=21.2 CenterZ=0 NormalX=0 NormalY=0 NormalZ=1 AngleXU=0 Radius=10 StartAngle=4.71239 EndAngle=7.85398
    g10: LineSegment StartX=19 StartY=31.2 StartZ=0 EndX=65 EndY=31.2 EndZ=0
    g11: LineSegment StartX=19 StartY=11.2 StartZ=0 EndX=65 EndY=11.2 EndZ=0
  constraints (25):
    c: Equal(g2,g-7)
    c: Equal(g3,g-8)
    c: Equal(g1,g-13)
    c: Equal(g0,g-12)
    c: Coincident(g0,g-12)
    c: Coincident(g1,g-13)
    c: Coincident(g3,g-8)
    c: Coincident(g2,g-7)
    c: Coincident(g4,g-4)
    c: Coincident(g4,g-5)
    c: Coincident(g5,g4)
    c: Coincident(g5,g-6)
    c: Coincident(g6,g5)
    c: PointOnObject(g6,g-3)
    c: Vertical(g6)
    c: Coincident(g7,g6)
    c: Coincident(g7,g4)
    c: Tangent(g8,g10) = 1.5708
    c: Tangent(g8,g11) = -1.5708
    c: Tangent(g9,g10) = 1.5708
    c: Tangent(g9,g11) = -1.5708
    c: Equal(g8,g9)
    c: Radius(g8) = 10
    c: Coincident(g8,g-11)
    c: Coincident(g9,g-9)
FEATURE [Sketcher::SketchObject] Sketch093  label="Sketch093 - scavi interni pulsanti"
  ArcFitTolerance = 1e-06
  AttachmentSupport = -> [Pad019]
  ExternalGeometry = -> [Binder]
  FullyConstrained = true
  MakeInternals = false
  MapMode = 5
  Placement = pos=(0,1.8e-15,0) rot=(1,0,0;1.5708rad)
  sketch-geometry (3):
    g0: Circle CenterX=-65 CenterY=21.2 CenterZ=0 NormalX=0 NormalY=0 NormalZ=1 AngleXU=0 Radius=7.3
    g1: Circle CenterX=-42 CenterY=21.2 CenterZ=0 NormalX=0 NormalY=0 NormalZ=1 AngleXU=0 Radius=7.3
    g2: Circle CenterX=-19 CenterY=21.2 CenterZ=0 NormalX=0 NormalY=0 NormalZ=1 AngleXU=0 Radius=7.3
  constraints (6):
    c: Coincident(g0,g-3)
    c: Coincident(g1,g-4)
    c: Coincident(g2,g-5)
    c: Diameter(g0) = 14.6
    c: Diameter(g1) = 14.6
    c: Diameter(g2) = 14.6
FEATURE [Sketcher::SketchObject] Sketch094  label="Sketch094 - forma centrale"
  ArcFitTolerance = 1e-06
  AttachmentSupport = -> [Pad019]
  ExternalGeometry = -> [Binder]
  FullyConstrained = true
  MakeInternals = false
  MapMode = 5
  Placement = pos=(0,2,0) rot=(0,0.707107,0.707107;3.14159rad)
  sketch-geometry (4):
    g0: LineSegment StartX=137.815 StartY=39.2 StartZ=0 EndX=142.655 EndY=24.303 EndZ=0
    g1: LineSegment StartX=110.815 StartY=24.303 StartZ=0 EndX=142.655 EndY=24.303 EndZ=0
    g2: LineSegment StartX=137.815 StartY=39.2 StartZ=0 EndX=110.815 EndY=39.2 EndZ=0
    g3: ArcOfCircle CenterX=92.2534 CenterY=31.7515 CenterZ=0 NormalX=0 NormalY=0 NormalZ=1 AngleXU=0 Radius=20 StartAngle=5.90156 EndAngle=6.66481
  constraints (12):
    c: PointOnObject(g0,g-3)
    c: Tangent(g0,g-5)
    c: Horizontal(g1)
    c: Coincident(g1,g0)
    c: Coincident(g2,g0)
    c: PointOnObject(g2,g-3)
    c: DistanceX(g2,g2) = 27
    c: Vertical(g1,g2)
    c: Coincident(g3,g2)
    c: Radius(g3) = 20
    c: Coincident(g3,g1)
    c: DistanceY(g-6,g0) = 4
FEATURE [Sketcher::SketchObject] Sketch095  label="Sketch095 - forma posteriore"
  ArcFitTolerance = 1e-06
  AttachmentSupport = -> [Pad019]
  ExternalGeometry = -> [Binder]
  FullyConstrained = true
  MakeInternals = false
  MapMode = 5
  Placement = pos=(0,2,0) rot=(0,0.707107,0.707107;3.14159rad)
  sketch-geometry (15):
    g0: LineSegment StartX=137.815 StartY=39.2 StartZ=0 EndX=143.955 EndY=20.303 EndZ=0
    g1: LineSegment StartX=143.955 StartY=20.303 StartZ=0 EndX=190.141 EndY=20.303 EndZ=0
    g2: ArcOfCircle CenterX=184.08 CenterY=34.8 CenterZ=0 NormalX=0 NormalY=0 NormalZ=1 AngleXU=0 Radius=3.5 StartAngle=3.49066 EndAngle=4.71239
    g3: LineSegment StartX=180.791 StartY=33.6029 StartZ=0 EndX=178.754 EndY=39.2 EndZ=0
    g4: LineSegment StartX=184.08 StartY=31.3 StartZ=0 EndX=186.139 EndY=31.3 EndZ=0
    g5: LineSegment StartX=190.141 StartY=20.303 StartZ=0 EndX=186.139 EndY=31.3 EndZ=0
    g6: LineSegment StartX=137.815 StartY=39.2 StartZ=0 EndX=156.815 EndY=39.2 EndZ=0
    g7: LineSegment StartX=178.754 StartY=39.2 StartZ=0 EndX=168.815 EndY=39.2 EndZ=0
    g8: LineSegment StartX=156.815 StartY=31.2 StartZ=0 EndX=168.815 EndY=31.2 EndZ=0
    g9: ArcOfCircle CenterX=176.411 CenterY=35.2 CenterZ=0 NormalX=0 NormalY=0 NormalZ=1 AngleXU=0 Radius=20 StartAngle=2.94023 EndAngle=3.34295
    g10: ArcOfCircle CenterX=188.411 CenterY=35.2 CenterZ=0 NormalX=0 NormalY=0 NormalZ=1 AngleXU=0 Radius=20 StartAngle=2.94023 EndAngle=3.34295
    g11: LineSegment StartX=157.815 StartY=39.2 StartZ=0 EndX=167.815 EndY=39.2 EndZ=0
    g12: LineSegment StartX=157.436 StartY=36.2 StartZ=0 EndX=167.436 EndY=36.2 EndZ=0
    g13: ArcOfCircle CenterX=177.411 CenterY=35.2 CenterZ=0 NormalX=0 NormalY=0 NormalZ=1 AngleXU=0 Radius=20 StartAngle=2.94023 EndAngle=3.09157
    g14: ArcOfCircle CenterX=187.411 CenterY=35.2 CenterZ=0 NormalX=0 NormalY=0 NormalZ=1 AngleXU=0 Radius=20 StartAngle=2.94023 EndAngle=3.09157
  constraints (46):
    c: PointOnObject(g0,g-3)
    c: Tangent(g0,g-6)
    c: Coincident(g1,g0)
    c: Horizontal(g1)
    c: Radius(g2) = 3.5
    c: Coincident(g2,g-5)
    c: PointOnObject(g3,g-3)
    c: Parallel(g3,g-4)
    c: Tangent(g3,g2) = 1.5708
    c: Horizontal(g4)
    c: Tangent(g4,g2) = -1.5708
    c: Coincident(g5,g1)
    c: Parallel(g5,g-4)
    c: Coincident(g5,g4)
    c: DistanceX(g4,g-8) = 3.8
    c: Coincident(g6,g0)
    c: PointOnObject(g6,g-3)
    c: Coincident(g7,g3)
    c: PointOnObject(g7,g-3)
    c: Horizontal(g8)
    c: DistanceX(g6,g7) = 12
    c: Vertical(g8,g6)
    c: Vertical(g7,g8)
    c: DistanceY(g8,g6) = 8
    c: Coincident(g9,g8)
    c: Coincident(g9,g6)
    c: Coincident(g10,g7)
    c: Coincident(g10,g8)
    c: Radius(g9) = 20
    c: Radius(g10) = 20
    c: PointOnObject(g11,g-3)
    c: PointOnObject(g11,g-3)
    c: DistanceX(g11,g11) = 10
    c: DistanceX(g6,g11) = 1
    c: Horizontal(g12)
    c: Equal(g12,g11)
    c: DistanceY(g12,g11) = 3
    c: Coincident(g13,g11)
    c: Coincident(g13,g12)
    c: Radius(g13) = 20
    c: Coincident(g14,g11)
    c: Coincident(g14,g12)
    c: Radius(g14) = 20
    c: DistanceX(g0,g6) = 19
    c: Horizontal(g9,g13)
    c: Horizontal(g0,g-4)
FEATURE [Sketcher::SketchObject] Sketch096  label="Sketch096 - forma impugnatura"
  ArcFitTolerance = 1e-06
  AttachmentSupport = -> [Pad019]
  ExternalGeometry = -> [Binder]
  FullyConstrained = true
  MakeInternals = false
  MapMode = 5
  Placement = pos=(0,2,0) rot=(0,0.707107,0.707107;3.14159rad)
  sketch-geometry (8):
    g0: LineSegment StartX=176.685 StartY=-80.4316 StartZ=0 EndX=143.955 EndY=20.303 EndZ=0
    g1: LineSegment StartX=176.685 StartY=-80.4316 StartZ=0 EndX=215.932 EndY=-80.4316 EndZ=0
    g2: Circle CenterX=179.305 CenterY=-76.8316 CenterZ=0 NormalX=0 NormalY=0 NormalZ=1 AngleXU=0 Radius=3
    g3: Circle CenterX=213.443 CenterY=-76.8316 CenterZ=0 NormalX=0 NormalY=0 NormalZ=1 AngleXU=0 Radius=3
    g4: LineSegment StartX=143.955 StartY=20.303 StartZ=0 EndX=202.765 EndY=20.303 EndZ=0
    g5: LineSegment StartX=215.42 StartY=-53.0314 StartZ=0 EndX=192.176 EndY=-3.18451 EndZ=0
    g6: ArcOfCircle CenterX=184.801 CenterY=-67.3089 CenterZ=0 NormalX=0 NormalY=0 NormalZ=1 AngleXU=0 Radius=33.7833 StartAngle=5.88425 EndAngle=6.71952
    g7: ArcOfCircle CenterX=207.583 CenterY=4 CenterZ=0 NormalX=0 NormalY=0 NormalZ=1 AngleXU=0 Radius=17 StartAngle=1.85815 EndAngle=3.57792
  constraints (19):
    c: Coincident(g0,g-4)
    c: PointOnObject(g0,g-3)
    c: Horizontal(g0,g-7)
    c: Coincident(g1,g0)
    c: Coincident(g1,g-5)
    c: Diameter(g2) = 6
    c: Diameter(g3) = 6
    c: Coincident(g2,g-9)
    c: Coincident(g3,g-10)
    c: Coincident(g4,g0)
    c: Coincident(g5,g-6)
    c: Coincident(g6,g1)
    c: Coincident(g6,g5)
    c: Equal(g-5,g6)
    c: Coincident(g5,g-7)
    c: Coincident(g4,g-7)
    c: Tangent(g7,g-7)
    c: Coincident(g7,g4)
    c: Coincident(g7,g5)
FEATURE [Sketcher::SketchObject] Sketch097
  ArcFitTolerance = 1e-06
  AttachmentSupport = -> [Pad019]
  ExternalGeometry = -> [Binder]
  FullyConstrained = true
  MakeInternals = false
  MapMode = 5
  Placement = pos=(0,2,0) rot=(0,0.707107,0.707107;3.14159rad)
  sketch-geometry (4):
    g0: LineSegment StartX=90 StartY=36.8 StartZ=0 EndX=108 EndY=36.8 EndZ=0
    g1: LineSegment StartX=108 StartY=36.8 StartZ=0 EndX=108 EndY=26.8 EndZ=0
    g2: LineSegment StartX=108 StartY=26.8 StartZ=0 EndX=90 EndY=26.8 EndZ=0
    g3: ArcOfCircle CenterX=94 CenterY=31.8 CenterZ=0 NormalX=0 NormalY=0 NormalZ=1 AngleXU=0 Radius=6.40312 StartAngle=2.24554 EndAngle=4.03765
  constraints (13):
    c: Horizontal(g0)
    c: Coincident(g1,g0)
    c: Vertical(g1)
    c: DistanceX(g0,g0) = 18
    c: DistanceY(g1,g1) = 10
    c: Coincident(g2,g1)
    c: Horizontal(g2)
    c: Equal(g2,g0)
    c: DistanceY(g0,g-3) = 2.4
    c: Coincident(g3,g0)
    c: Coincident(g3,g2)
    c: DistanceX(g2,g3) = 4
    c: DistanceX(g-3,g0) = 90
FEATURE [PartDesign::Chamfer] Chamfer015
  Angle = 45
  Base = -> Pad019 [Edge19,Edge22,Edge79]
  BaseFeature = -> Pad019
  ChamferType = 0
  FlipDirection = false
  Refine = true
  Size = 1.9
  Size2 = 1
  SupportTransform = false
  Suppressed = false
  UseAllEdges = false
FEATURE [PartDesign::Pocket] Pocket002
  BaseFeature = -> Chamfer015
  Direction = (0,1,-2e-16)
  Length = 1.2
  Length2 = 5
  Profile = -> Sketch093
  ReferenceAxis = -> Sketch093 [N_Axis]
  Refine = true
  Suppressed = false
  Type = 0
FEATURE [PartDesign::Pad] Pad005
  BaseFeature = -> Pocket002
  Direction = (0,1,-2e-16)
  Length = 1.6
  Length2 = 10
  Profile = -> Sketch091
  ReferenceAxis = -> Sketch091 [N_Axis]
  Refine = true
  Suppressed = false
  Type = 0
FEATURE [Sketcher::SketchObject] Sketch092  label="Sketch092 - scavi per viti anteriori"
  ArcFitTolerance = 1e-06
  AttachmentSupport = -> [Pad005]
  ExternalGeometry = -> [Binder]
  FullyConstrained = true
  MakeInternals = false
  MapMode = 5
  Placement = pos=(0,3.6,0) rot=(0,0.707107,0.707107;3.14159rad)
  sketch-geometry (20):
    g0: ArcOfCircle CenterX=5.6 CenterY=7.6 CenterZ=0 NormalX=0 NormalY=0 NormalZ=1 AngleXU=0 Radius=3.5 StartAngle=0 EndAngle=1.5708
    g1: ArcOfCircle CenterX=5.6 CenterY=34.8 CenterZ=0 NormalX=0 NormalY=0 NormalZ=1 AngleXU=0 Radius=3.5 StartAngle=4.71239 EndAngle=6.28319
    g2: ArcOfCircle CenterX=78.51 CenterY=34.8 CenterZ=0 NormalX=0 NormalY=0 NormalZ=1 AngleXU=0 Radius=3.5 StartAngle=3.14159 EndAngle=4.71239
    g3: ArcOfCircle CenterX=78.51 CenterY=7.6 CenterZ=0 NormalX=0 NormalY=0 NormalZ=1 AngleXU=0 Radius=3.5 StartAngle=1.5708 EndAngle=3.14159
    g4: LineSegment StartX=0 StartY=3.2 StartZ=0 EndX=0 EndY=11.1 EndZ=0
    g5: LineSegment StartX=0 StartY=11.1 StartZ=0 EndX=5.6 EndY=11.1 EndZ=0
    g6: LineSegment StartX=0 StartY=3.2 StartZ=0 EndX=9.1 EndY=3.2 EndZ=0
    g7: LineSegment StartX=9.1 StartY=3.2 StartZ=0 EndX=9.1 EndY=7.6 EndZ=0
    g8: LineSegment StartX=0 StartY=39.2 StartZ=0 EndX=0 EndY=31.3 EndZ=0
    g9: LineSegment StartX=0 StartY=31.3 StartZ=0 EndX=5.6 EndY=31.3 EndZ=0
    g10: LineSegment StartX=0 StartY=39.2 StartZ=0 EndX=9.1 EndY=39.2 EndZ=0
    g11: LineSegment StartX=9.1 StartY=39.2 StartZ=0 EndX=9.1 EndY=34.8 EndZ=0
    g12: LineSegment StartX=82.8 StartY=39.2 StartZ=0 EndX=75.01 EndY=39.2 EndZ=0
    g13: LineSegment StartX=82.8 StartY=39.2 StartZ=0 EndX=82.8 EndY=31.3 EndZ=0
    g14: LineSegment StartX=82.8 StartY=31.3 StartZ=0 EndX=78.51 EndY=31.3 EndZ=0
    g15: LineSegment StartX=82.8 StartY=3.2 StartZ=0 EndX=75.01 EndY=3.2 EndZ=0
    g16: LineSegment StartX=75.01 StartY=3.2 StartZ=0 EndX=75.01 EndY=7.6 EndZ=0
    g17: LineSegment StartX=82.8 StartY=3.2 StartZ=0 EndX=82.8 EndY=11.1 EndZ=0
    g18: LineSegment StartX=82.8 StartY=11.1 StartZ=0 EndX=78.51 EndY=11.1 EndZ=0
    g19: LineSegment StartX=75.01 StartY=39.2 StartZ=0 EndX=75.01 EndY=34.8 EndZ=0
  constraints (48):
    c: Radius(g0) = 3.5
    c: Coincident(g0,g-10)
    c: Radius(g1) = 3.5
    c: Coincident(g1,g-9)
    c: Radius(g2) = 3.5
    c: Coincident(g2,g-8)
    c: Radius(g3) = 3.5
    c: Coincident(g3,g-7)
    c: Coincident(g4,g-5)
    c: PointOnObject(g4,g-4)
    c: Coincident(g5,g4)
    c: Horizontal(g5)
    c: Coincident(g6,g4)
    c: PointOnObject(g6,g-5)
    c: Coincident(g7,g6)
    c: Vertical(g7)
    c: Coincident(g8,g-4)
    c: PointOnObject(g8,g-4)
    c: Coincident(g9,g8)
    c: Horizontal(g9)
    c: Coincident(g10,g8)
    c: PointOnObject(g10,g-3)
    c: Coincident(g11,g10)
    c: Vertical(g11)
    c: PointOnObject(g12,g-3)
    c: PointOnObject(g12,g-3)
    c: Coincident(g13,g12)
    c: Vertical(g13)
    c: Coincident(g14,g13)
    c: Horizontal(g14)
    c: Coincident(g15,g-6)
    c: PointOnObject(g15,g-5)
    c: Coincident(g16,g15)
    c: Vertical(g16)
    c: Coincident(g17,g15)
    c: Coincident(g18,g17)
    c: Horizontal(g18)
    c: Tangent(g3,g18) = -1.5708
    c: Tangent(g16,g3) = 1.5708
    c: Coincident(g19,g12)
    c: Vertical(g19)
    c: Tangent(g2,g19) = -1.5708
    c: Tangent(g2,g14) = 1.5708
    c: Tangent(g0,g7) = -1.5708
    c: Tangent(g0,g5) = 1.5708
    c: Tangent(g9,g1) = -1.5708
    c: Tangent(g1,g11) = 1.5708
    c: Tangent(g17,g13)
FEATURE [PartDesign::Pocket] Pocket001
  BaseFeature = -> Pad005
  Direction = (0,-1,2e-16)
  Length = 1.6
  Length2 = 5
  Profile = -> Sketch092
  ReferenceAxis = -> Sketch092 [N_Axis]
  Refine = true
  Suppressed = false
  Type = 0
FEATURE [PartDesign::Pad] Pad006
  BaseFeature = -> Pocket001
  Direction = (0,1,-2e-16)
  Length = 0.8
  Length2 = 10
  Profile = -> Sketch094
  ReferenceAxis = -> Sketch094 [N_Axis]
  Refine = true
  Suppressed = false
  Type = 0
FEATURE [PartDesign::Pad] Pad007
  BaseFeature = -> Pad006
  Direction = (0,1,-2e-16)
  Length = 2
  Length2 = 10
  Profile = -> Sketch095
  ReferenceAxis = -> Sketch095 [N_Axis]
  Refine = true
  Suppressed = false
  Type = 0
FEATURE [PartDesign::Pad] Pad008  label="Pad008 - forma impugnatura"
  BaseFeature = -> Pad007
  Direction = (0,1,-2e-16)
  Length = 1.6
  Length2 = 10
  Profile = -> Sketch096
  ReferenceAxis = -> Sketch096 [N_Axis]
  Refine = true
  Suppressed = false
  Type = 0
FEATURE [PartDesign::Pad] Pad009
  BaseFeature = -> Pad008
  Direction = (0,1,-2e-16)
  Length = 1.6
  Length2 = 10
  Profile = -> Sketch097
  ReferenceAxis = -> Sketch097 [N_Axis]
  Refine = true
  Suppressed = false
  Type = 0
FEATURE [Sketcher::SketchObject] Sketch098
  ArcFitTolerance = 1e-06
  AttachmentSupport = -> [Pad006]
  ExternalGeometry = -> [Binder]
  FullyConstrained = true
  MakeInternals = false
  MapMode = 5
  Placement = pos=(0,2.8,-7e-16) rot=(0,0.707107,0.707107;3.14159rad)
  sketch-geometry (4):
    g0: LineSegment StartX=118 StartY=39.2 StartZ=0 EndX=129 EndY=39.2 EndZ=0
    g1: LineSegment StartX=120.599 StartY=31.2 StartZ=0 EndX=131.599 EndY=31.2 EndZ=0
    g2: LineSegment StartX=129 StartY=39.2 StartZ=0 EndX=131.599 EndY=31.2 EndZ=0
    g3: LineSegment StartX=118 StartY=39.2 StartZ=0 EndX=120.599 EndY=31.2 EndZ=0
  constraints (12):
    c: PointOnObject(g0,g-3)
    c: PointOnObject(g0,g-3)
    c: DistanceX(g0,g0) = 11
    c: Horizontal(g1)
    c: Equal(g1,g0)
    c: Coincident(g2,g0)
    c: Coincident(g3,g0)
    c: Parallel(g-4,g2)
    c: Coincident(g1,g2)
    c: Coincident(g1,g3)
    c: DistanceY(g1,g0) = 8
    c: DistanceX(g-3,g0) = 118
FEATURE [Sketcher::SketchObject] Sketch099
  ArcFitTolerance = 1e-06
  AttachmentSupport = -> [Pad008]
  ExternalGeometry = -> [Binder]
  FullyConstrained = true
  MakeInternals = false
  MapMode = 5
  Placement = pos=(0,3.6,0) rot=(0,0.707107,0.707107;3.14159rad)
  sketch-geometry (13):
    g0: LineSegment StartX=192.176 StartY=-3.18451 StartZ=0 EndX=196.804 EndY=-13.1108 EndZ=0
    g1: LineSegment [constr] StartX=202.765 StartY=20.303 StartZ=0 EndX=181.223 EndY=20.303 EndZ=0
    g2: LineSegment [constr] StartX=181.223 StartY=20.303 StartZ=0 EndX=181.223 EndY=-3.18451 EndZ=0
    g3: ArcOfCircle CenterX=181.223 CenterY=-20.3764 CenterZ=0 NormalX=0 NormalY=0 NormalZ=1 AngleXU=0 Radius=17.1918 StartAngle=0.436332 EndAngle=1.57079
    g4: ArcOfEllipse CenterX=181.223 CenterY=8.55923 CenterZ=0 NormalX=0 NormalY=0 NormalZ=1 MajorRadius=23.4779 MinorRadius=11.7437 AngleXU=0 StartAngle=1.5708 EndAngle=4.71239
    g5: LineSegment [constr] StartX=204.701 StartY=8.55923 StartZ=0 EndX=157.745 EndY=8.55923 EndZ=0
    g6: LineSegment [constr] StartX=181.223 StartY=20.303 StartZ=0 EndX=181.223 EndY=-3.18451 EndZ=0
    g7: GeomPoint [constr] X=201.553 Y=8.55923 Z=0
    g8: GeomPoint [constr] X=160.894 Y=8.55923 Z=0
    g9: GeomPoint [constr] X=181.223 Y=-3.18451 Z=0
    g10: LineSegment StartX=181.223 StartY=20.303 StartZ=0 EndX=202.765 EndY=20.303 EndZ=0
    g11: ArcOfCircle CenterX=207.583 CenterY=4 CenterZ=0 NormalX=0 NormalY=0 NormalZ=1 AngleXU=0 Radius=17 StartAngle=1.85815 EndAngle=3.57792
    g12: LineSegment [constr] StartX=172.411 StartY=39.2 StartZ=0 EndX=192.176 EndY=-3.18451 EndZ=0
  constraints (27):
    c: Coincident(g1,g-7)
    c: Horizontal(g1)
    c: Coincident(g2,g1)
    c: Vertical(g2)
    c: Horizontal(g2,g0)
    c: Coincident(g3,g0)
    c: Coincident(g3,g2)
    c: InternalAlignment(g5-g8 -> g4) x4
    c: Horizontal(g5)
    c: PointOnObject(g4,g2)
    c: Coincident(g4,g1)
    c: DistanceX(g-3,g5) = 10.1
    c: Coincident(g4,g2)
    c: Tangent(g3,g-5)
    c: PointOnObject(g9,g4)
    c: PointOnObject(g9,g3)
    c: Tangent(g4,g3,g9) = 1.5708
    c: Coincident(g10,g1)
    c: Coincident(g10,g1)
    c: Equal(g11,g-4)
    c: Coincident(g11,g1)
    c: Coincident(g11,g0)
    c: PointOnObject(g12,g-6)
    c: PointOnObject(g1,g12)
    c: Tangent(g12,g-5) = -1.5708
    c: Tangent(g0,g-5) = -1.5708
    c: Horizontal(g9,g12)
FEATURE [Sketcher::SketchObject] Sketch106  label="Sketch106 - smusso impuniatura interno"
  ArcFitTolerance = 1e-06
  AttachmentSupport = -> [Pad008]
  ExternalGeometry = -> [Pad008]
  FullyConstrained = true
  MakeInternals = false
  MapMode = 5
  Placement = pos=(0,-1.586e-13,-80.4316) rot=(1,0,0;3.14159rad)
  sketch-geometry (9):
    g0: LineSegment StartX=-176.685 StartY=-3.6 StartZ=0 EndX=-176.685 EndY=-2.691e-13 EndZ=0
    g1: LineSegment [constr] StartX=-176.685 StartY=-1.416e-13 StartZ=0 EndX=-176.685 EndY=-2.691e-13 EndZ=0
    g2: LineSegment [constr] StartX=-186.685 StartY=-3.6 StartZ=0 EndX=-186.685 EndY=-2.691e-13 EndZ=0
    g3: ArcOfEllipse CenterX=-186.685 CenterY=-2.691e-13 CenterZ=0 NormalX=0 NormalY=0 NormalZ=1 MajorRadius=10 MinorRadius=3.6 AngleXU=3.14159 StartAngle=1.5708 EndAngle=3.14159
    g4: LineSegment [constr] StartX=-196.685 StartY=-1.416e-13 StartZ=0 EndX=-176.685 EndY=-1.416e-13 EndZ=0
    g5: LineSegment [constr] StartX=-186.685 StartY=-3.6 StartZ=0 EndX=-186.685 EndY=3.6 EndZ=0
    g6: GeomPoint [constr] X=-196.015 Y=-1.41e-13 Z=0
    g7: GeomPoint [constr] X=-177.356 Y=-1.416e-13 Z=0
    g8: LineSegment StartX=-176.685 StartY=-3.6 StartZ=0 EndX=-186.685 EndY=-3.6 EndZ=0
  constraints (15):
    c: PointOnObject(g2,g-3)
    c: Coincident(g1,g-5)
    c: DistanceY(g1,g1) = 0
    c: Coincident(g0,g1)
    c: DistanceX(g2,g-5) = 10
    c: Vertical(g2)
    c: Horizontal(g2,g0)
    c: InternalAlignment(g4-g7 -> g3) x4
    c: Coincident(g3,g2)
    c: Horizontal(g4)
    c: Coincident(g3,g0)
    c: Tangent(g0,g-5) = 1.5708
    c: Coincident(g3,g2)
    c: Coincident(g8,g0)
    c: Coincident(g8,g2)
FEATURE [Sketcher::SketchObject] Sketch107  label="Sketch107 - smusso impugnatura esterno"
  ArcFitTolerance = 1e-06
  AttachmentSupport = -> [Pad008]
  ExternalGeometry = -> [Pad008]
  FullyConstrained = true
  MakeInternals = false
  MapMode = 5
  Placement = pos=(0,-1.586e-13,-80.4316) rot=(1,0,0;3.14159rad)
  sketch-geometry (9):
    g0: LineSegment [constr] StartX=-215.932 StartY=-1.416e-13 StartZ=0 EndX=-215.932 EndY=-5.88e-14 EndZ=0
    g1: LineSegment StartX=-215.932 StartY=-3.6 StartZ=0 EndX=-215.932 EndY=-5.86e-14 EndZ=0
    g2: LineSegment StartX=-215.932 StartY=-3.6 StartZ=0 EndX=-205.932 EndY=-3.6 EndZ=0
    g3: LineSegment [constr] StartX=-205.932 StartY=-3.6 StartZ=0 EndX=-205.932 EndY=-5.86e-14 EndZ=0
    g4: ArcOfEllipse CenterX=-205.932 CenterY=-5.88e-14 CenterZ=0 NormalX=0 NormalY=0 NormalZ=1 MajorRadius=10 MinorRadius=3.6 AngleXU=-3.14159 StartAngle=-2.66e-14 EndAngle=1.5708
    g5: LineSegment [constr] StartX=-215.932 StartY=-1.416e-13 StartZ=0 EndX=-195.932 EndY=-1.416e-13 EndZ=0
    g6: LineSegment [constr] StartX=-205.932 StartY=-3.6 StartZ=0 EndX=-205.932 EndY=3.6 EndZ=0
    g7: GeomPoint [constr] X=-215.262 Y=-1.483e-13 Z=0
    g8: GeomPoint [constr] X=-196.602 Y=-1.551e-13 Z=0
  constraints (16):
    c: Coincident(g0,g-6)
    c: PointOnObject(g0,g-6)
    c: DistanceY(g0,g0) = 0
    c: Coincident(g1,g-6)
    c: Coincident(g1,g0)
    c: Tangent(g2,g-3)
    c: DistanceX(g2,g2) = 10
    c: Coincident(g3,g2)
    c: Vertical(g3)
    c: Horizontal(g3,g0)
    c: InternalAlignment(g5-g8 -> g4) x4
    c: Coincident(g4,g3)
    c: Horizontal(g5)
    c: Coincident(g4,g0)
    c: Coincident(g4,g2)
    c: PointOnObject(g2,g1)
FEATURE [Sketcher::SketchObject] Sketch108
  ArcFitTolerance = 1e-06
  AttachmentOffset = pos=(0,0,-1.6) rot=(0,0,1;0rad)
  AttachmentSupport = -> [Pad008]
  ExternalGeometry = -> [Binder]
  FullyConstrained = true
  MakeInternals = false
  MapMode = 5
  Placement = pos=(0,2,4e-16) rot=(0,0.707107,0.707107;3.14159rad)
  sketch-geometry (14):
    g0: LineSegment StartX=192.176 StartY=-3.18451 StartZ=0 EndX=193.827 EndY=-6.72678 EndZ=0
    g1: LineSegment [constr] StartX=202.765 StartY=20.303 StartZ=0 EndX=181.223 EndY=20.303 EndZ=0
    g2: LineSegment [constr] StartX=181.223 StartY=20.303 StartZ=0 EndX=181.223 EndY=1.30297 EndZ=0
    g3: ArcOfCircle CenterX=181.223 CenterY=-12.6042 CenterZ=0 NormalX=0 NormalY=0 NormalZ=1 AngleXU=0 Radius=13.9072 StartAngle=0.436332 EndAngle=1.5708
    g4: ArcOfEllipse CenterX=181.223 CenterY=10.803 CenterZ=0 NormalX=0 NormalY=0 NormalZ=1 MajorRadius=14.4779 MinorRadius=9.5 AngleXU=0 StartAngle=1.5708 EndAngle=4.71239
    g5: LineSegment [constr] StartX=195.701 StartY=10.803 StartZ=0 EndX=166.745 EndY=10.803 EndZ=0
    g6: LineSegment [constr] StartX=181.223 StartY=20.303 StartZ=0 EndX=181.223 EndY=1.30297 EndZ=0
    g7: GeomPoint [constr] X=192.148 Y=10.803 Z=0
    g8: GeomPoint [constr] X=170.298 Y=10.803 Z=0
    g9: LineSegment StartX=181.223 StartY=20.303 StartZ=0 EndX=202.765 EndY=20.303 EndZ=0
    g10: ArcOfCircle CenterX=207.583 CenterY=4 CenterZ=0 NormalX=0 NormalY=0 NormalZ=1 AngleXU=0 Radius=17 StartAngle=1.85815 EndAngle=3.57792
    g11: LineSegment [constr] StartX=172.411 StartY=39.2 StartZ=0 EndX=192.176 EndY=-3.18451 EndZ=0
    g12: GeomPoint [constr] X=181.223 Y=1.30297 Z=0
    g13: GeomPoint [constr] X=181.223 Y=1.30297 Z=0
  constraints (28):
    c: Coincident(g1,g-7)
    c: Horizontal(g1)
    c: Coincident(g2,g1)
    c: Vertical(g2)
    c: Coincident(g3,g2)
    c: InternalAlignment(g5-g8 -> g4) x4
    c: Horizontal(g5)
    c: PointOnObject(g4,g2)
    c: Coincident(g4,g1)
    c: DistanceX(g-3,g5) = 19.1
    c: Coincident(g4,g2)
    c: Coincident(g9,g1)
    c: Coincident(g9,g1)
    c: Coincident(g10,g1)
    c: Coincident(g10,g0)
    c: PointOnObject(g11,g-6)
    c: PointOnObject(g1,g11)
    c: DistanceY(g2,g1) = 19
    c: Coincident(g10,g-4)
    c: PointOnObject(g12,g4)
    c: PointOnObject(g12,g3)
    c: Tangent(g11,g-5) = -1.5708
    c: Tangent(g0,g-5) = -1.5708
    c: Tangent(g3,g0) = 1.5708
    c: PointOnObject(g13,g4)
    c: PointOnObject(g13,g3)
    c: Tangent(g4,g3,g13) = 1.5708
    c: Horizontal(g11,g0)
FEATURE [Part::Part2DObjectPython] Clone2D  label="Sketch108 (2D)"  # Draft 2D object (typed FeaturePython)
  Fuse = false
  Objects = -> [Sketch108]
  Placement = pos=(0,2,4e-16) rot=(0,0.707107,0.707107;3.14159rad)
  Scale = (1,1,1)
FEATURE [Sketcher::SketchObject] Sketch109
  ArcFitTolerance = 1e-06
  AttachmentOffset = pos=(0,0,-3.5) rot=(0,0,1;0rad)
  AttachmentSupport = -> [Pad008]
  ExternalGeometry = -> [Binder]
  FullyConstrained = true
  MakeInternals = false
  MapMode = 5
  Placement = pos=(0,0.1,8e-16) rot=(0,0.707107,0.707107;3.14159rad)
  sketch-geometry (1):
    g0: GeomPoint X=197.47 Y=8.55923 Z=0
  constraints (1):
    c: Symmetric(g-7,g-5,g0)
FEATURE [PartDesign::Chamfer] Chamfer005
  Angle = 45
  Base = -> Pad009 [Edge215,Edge212]
  BaseFeature = -> Pad009
  ChamferType = 1
  FlipDirection = false
  Refine = true
  Size = 1.5
  Size2 = 2.8
  SupportTransform = false
  Suppressed = false
  UseAllEdges = false
FEATURE [Sketcher::SketchObject] Sketch111
  ArcFitTolerance = 1e-06
  AttachmentSupport = -> [Pad009]
  ExternalGeometry = -> [Pad009]
  FullyConstrained = true
  MakeInternals = false
  MapMode = 5
  Placement = pos=(0,3.6,-8e-16) rot=(0,0.707107,0.707107;3.14159rad)
  sketch-geometry (21):
    g0: LineSegment [constr] StartX=97 StartY=36.8 StartZ=0 EndX=97 EndY=26.8 EndZ=0
    g1: LineSegment StartX=97 StartY=28.6 StartZ=0 EndX=97 EndY=27.8 EndZ=0
    g2: LineSegment StartX=97 StartY=27.8 StartZ=0 EndX=108 EndY=27.8 EndZ=0
    g3: LineSegment StartX=108 StartY=27.8 StartZ=0 EndX=108 EndY=28.6 EndZ=0
    g4: LineSegment StartX=108 StartY=28.6 StartZ=0 EndX=97 EndY=28.6 EndZ=0
    g5: LineSegment StartX=97 StartY=35.8 StartZ=0 EndX=97 EndY=35 EndZ=0
    g6: LineSegment StartX=97 StartY=35 StartZ=0 EndX=108 EndY=35 EndZ=0
    g7: LineSegment StartX=108 StartY=35 StartZ=0 EndX=108 EndY=35.8 EndZ=0
    g8: LineSegment StartX=108 StartY=35.8 StartZ=0 EndX=97 EndY=35.8 EndZ=0
    g9: LineSegment StartX=97 StartY=30.4 StartZ=0 EndX=97 EndY=29.6 EndZ=0
    g10: LineSegment StartX=97 StartY=29.6 StartZ=0 EndX=108 EndY=29.6 EndZ=0
    g11: LineSegment StartX=108 StartY=29.6 StartZ=0 EndX=108 EndY=30.4 EndZ=0
    g12: LineSegment StartX=108 StartY=30.4 StartZ=0 EndX=97 EndY=30.4 EndZ=0
    g13: LineSegment StartX=97 StartY=34 StartZ=0 EndX=97 EndY=33.2 EndZ=0
    g14: LineSegment StartX=97 StartY=33.2 StartZ=0 EndX=108 EndY=33.2 EndZ=0
    g15: LineSegment StartX=108 StartY=33.2 StartZ=0 EndX=108 EndY=34 EndZ=0
    g16: LineSegment StartX=108 StartY=34 StartZ=0 EndX=97 EndY=34 EndZ=0
    g17: LineSegment StartX=97 StartY=32.2 StartZ=0 EndX=97 EndY=31.4 EndZ=0
    g18: LineSegment StartX=97 StartY=31.4 StartZ=0 EndX=108 EndY=31.4 EndZ=0
    g19: LineSegment StartX=108 StartY=31.4 StartZ=0 EndX=108 EndY=32.2 EndZ=0
    g20: LineSegment StartX=108 StartY=32.2 StartZ=0 EndX=97 EndY=32.2 EndZ=0
  constraints (54):
    c: Vertical(g0)
    c: PointOnObject(g0,g-3)
    c: PointOnObject(g0,g-4)
    c: DistanceX(g0,g-5) = 11
    c: Coincident(g1,g2)
    c: Coincident(g2,g3)
    c: Coincident(g3,g4)
    c: Coincident(g4,g1)
    c: Horizontal(g2)
    c: Horizontal(g4)
    c: Tangent(g1,g0)
    c: Tangent(g3,g-5)
    c: DistanceY(g2,g3) = 0.8
    c: Coincident(g5,g6)
    c: Coincident(g6,g7)
    c: Coincident(g7,g8)
    c: Coincident(g8,g5)
    c: Horizontal(g6)
    c: Horizontal(g8)
    c: DistanceY(g6,g7) = 0.8
    c: Coincident(g9,g10)
    c: Coincident(g10,g11)
    c: Coincident(g11,g12)
    c: Coincident(g12,g9)
    c: Horizontal(g10)
    c: Horizontal(g12)
    c: DistanceY(g10,g11) = 0.8
    c: Tangent(g5,g0)
    c: Tangent(g7,g-5)
    c: Tangent(g9,g0)
    c: Tangent(g11,g-5)
    c: Coincident(g13,g14)
    c: Coincident(g14,g15)
    c: Coincident(g15,g16)
    c: Coincident(g16,g13)
    c: Horizontal(g14)
    c: Horizontal(g16)
    c: DistanceY(g14,g15) = 0.8
    c: Tangent(g13,g0)
    c: Tangent(g15,g-5)
    c: Coincident(g17,g18)
    c: Coincident(g18,g19)
    c: Coincident(g19,g20)
    c: Coincident(g20,g17)
    c: Horizontal(g18)
    c: Horizontal(g20)
    c: DistanceY(g18,g19) = 0.8
    c: Tangent(g17,g0)
    c: Tangent(g19,g-5)
    c: DistanceY(g1,g9) = 1
    c: DistanceY(g9,g17) = 1
    c: DistanceY(g17,g13) = 1
    c: DistanceY(g13,g5) = 1
    c: DistanceY(g0,g1) = 1
FEATURE [PartDesign::Pocket] Pocket004
  BaseFeature = -> Chamfer005
  Direction = (0,-1,2e-16)
  Length = 1
  Length2 = 5
  Profile = -> Sketch111
  ReferenceAxis = -> Sketch111 [N_Axis]
  Refine = true
  Suppressed = false
  Type = 0
FEATURE [PartDesign::Pad] Pad010
  BaseFeature = -> Pocket004
  Direction = (0,1,-2e-16)
  Length = 1.2
  Length2 = 10
  Profile = -> Sketch098
  ReferenceAxis = -> Sketch098 [N_Axis]
  Refine = true
  Suppressed = false
  Type = 0
FEATURE [PartDesign::Chamfer] Chamfer006
  Angle = 45
  Base = -> Pad010 [Edge291]
  BaseFeature = -> Pad010
  ChamferType = 1
  FlipDirection = false
  Refine = true
  Size = 1
  Size2 = 6
  SupportTransform = false
  Suppressed = false
  UseAllEdges = false
FEATURE [Sketcher::SketchObject] Sketch110
  ArcFitTolerance = 1e-06
  AttachmentSupport = -> [Pad010]
  ExternalGeometry = -> [Sketch098]
  FullyConstrained = true
  MakeInternals = false
  MapMode = 5
  Placement = pos=(0,4,-9e-16) rot=(0,0.707107,0.707107;3.14159rad)
  sketch-geometry (8):
    g0: LineSegment StartX=119.69 StartY=34 StartZ=0 EndX=130.69 EndY=34 EndZ=0
    g1: LineSegment StartX=119.95 StartY=33.2 StartZ=0 EndX=130.95 EndY=33.2 EndZ=0
    g2: LineSegment StartX=119.137 StartY=35.7 StartZ=0 EndX=130.137 EndY=35.7 EndZ=0
    g3: LineSegment StartX=118.877 StartY=36.5 StartZ=0 EndX=129.877 EndY=36.5 EndZ=0
    g4: LineSegment StartX=118.877 StartY=36.5 StartZ=0 EndX=119.137 EndY=35.7 EndZ=0
    g5: LineSegment StartX=129.877 StartY=36.5 StartZ=0 EndX=130.137 EndY=35.7 EndZ=0
    g6: LineSegment StartX=119.69 StartY=34 StartZ=0 EndX=119.95 EndY=33.2 EndZ=0
    g7: LineSegment StartX=130.69 StartY=34 StartZ=0 EndX=130.95 EndY=33.2 EndZ=0
  constraints (24):
    c: Horizontal(g0)
    c: Horizontal(g1)
    c: Horizontal(g2)
    c: Horizontal(g3)
    c: Equal(g1,g-5)
    c: Equal(g0,g-5)
    c: Equal(g2,g-5)
    c: Equal(g3,g-5)
    c: PointOnObject(g0,g-3)
    c: PointOnObject(g1,g-3)
    c: PointOnObject(g2,g-3)
    c: PointOnObject(g3,g-3)
    c: Coincident(g4,g3)
    c: Coincident(g4,g2)
    c: Coincident(g5,g3)
    c: Coincident(g5,g2)
    c: Coincident(g6,g0)
    c: Coincident(g6,g1)
    c: Coincident(g7,g0)
    c: Coincident(g7,g1)
    c: DistanceY(g1,g0) = 0.8
    c: DistanceY(g2,g3) = 0.8
    c: DistanceY(g-5,g1) = 2
    c: DistanceY(g-5,g2) = 4.5
FEATURE [PartDesign::Pocket] Pocket003
  BaseFeature = -> Chamfer006
  Direction = (0,-1,2e-16)
  Length = 1
  Length2 = 5
  Profile = -> Sketch110
  ReferenceAxis = -> Sketch110 [N_Axis]
  Refine = true
  Suppressed = false
  Type = 0
FEATURE [PartDesign::SubtractivePipe] SubtractivePipe
  AuxilleryCurvelinear = true
  AuxillerySpineTangent = false
  BaseFeature = -> Pocket003
  Binormal = (0,0,0)
  Mode = 0
  Profile = -> Sketch106
  Refine = true
  Spine = -> Pad008 [Edge215]
  SpineTangent = false
  Suppressed = false
  Transformation = 0
  Transition = 0
FEATURE [PartDesign::SubtractivePipe] SubtractivePipe001
  AuxilleryCurvelinear = true
  AuxillerySpineTangent = false
  BaseFeature = -> SubtractivePipe
  Binormal = (0,0,0)
  Mode = 0
  Profile = -> Sketch107
  Refine = true
  Spine = -> Pad008 [Edge213,Edge216,Edge210]
  SpineTangent = false
  Suppressed = false
  Transformation = 0
  Transition = 0
FEATURE [PartDesign::SubtractiveLoft] SubtractiveLoft
  BaseFeature = -> SubtractivePipe001
  Closed = false
  Profile = -> Sketch099
  Refine = true
  Ruled = false
  Sections = -> [Sketch108]
  Suppressed = false
FEATURE [PartDesign::SubtractiveLoft] SubtractiveLoft001
  BaseFeature = -> SubtractiveLoft
  Closed = false
  Profile = -> Clone2D
  Refine = true
  Ruled = false
  Sections = -> [Sketch109]
  Suppressed = false
FEATURE [Sketcher::SketchObject] Sketch112
  ArcFitTolerance = 1e-06
  AttachmentSupport = -> [Pad008]
  ExternalGeometry = -> [Binder]
  FullyConstrained = true
  MakeInternals = false
  MapMode = 5
  Placement = pos=(0,3.6,0) rot=(0,0.707107,0.707107;3.14159rad)
  sketch-geometry (4):
    g0: LineSegment [constr] StartX=167.782 StartY=-53.0314 StartZ=0 EndX=215.42 EndY=-53.0314 EndZ=0
    g1: GeomPoint [constr] X=191.282 Y=-53.0314 Z=0
    g2: Circle CenterX=191.282 CenterY=-53.0314 CenterZ=0 NormalX=0 NormalY=0 NormalZ=1 AngleXU=0 Radius=11.5
    g3: Circle CenterX=191.282 CenterY=-53.0314 CenterZ=0 NormalX=0 NormalY=0 NormalZ=1 AngleXU=0 Radius=10.7
  constraints (9):
    c: Horizontal(g0)
    c: PointOnObject(g0,g-3)
    c: Diameter(g2) = 23
    c: Coincident(g2,g1)
    c: Diameter(g3) = 21.4
    c: Coincident(g3,g1)
    c: DistanceX(g0,g1) = 23.5
    c: PointOnObject(g1,g0)
    c: Coincident(g0,g-4)
FEATURE [PartDesign::Chamfer] Chamfer016
  Angle = 45
  Base = -> SubtractiveLoft001 [Edge118,Edge117,Edge119,Edge120,Edge109]
  BaseFeature = -> SubtractiveLoft001
  ChamferType = 0
  FlipDirection = false
  Refine = true
  Size = 1.5
  Size2 = 1
  SupportTransform = false
  Suppressed = false
  UseAllEdges = false
FEATURE [PartDesign::Chamfer] Chamfer017
  Angle = 45
  Base = -> Chamfer016 [Edge15]
  BaseFeature = -> Chamfer016
  ChamferType = 0
  FlipDirection = false
  Refine = true
  Size = 1.6
  Size2 = 1
  SupportTransform = false
  Suppressed = false
  UseAllEdges = false
FEATURE [PartDesign::Chamfer] Chamfer018
  Angle = 45
  Base = -> Chamfer017 [Edge10]
  BaseFeature = -> Chamfer017
  ChamferType = 0
  FlipDirection = false
  Refine = true
  Size = 3.5
  Size2 = 1
  SupportTransform = false
  Suppressed = false
  UseAllEdges = false
FEATURE [PartDesign::Chamfer] Chamfer019
  Angle = 45
  Base = -> Chamfer018 [Edge94]
  BaseFeature = -> Chamfer018
  ChamferType = 0
  FlipDirection = false
  Refine = true
  Size = 1.9
  Size2 = 1
  SupportTransform = false
  Suppressed = false
  UseAllEdges = false
FEATURE [PartDesign::Fillet] Fillet009
  Base = -> Chamfer019 [Edge83]
  BaseFeature = -> Chamfer019
  Radius = 1.1
  Refine = true
  SupportTransform = false
  Suppressed = false
  UseAllEdges = false
FEATURE [PartDesign::Fillet] Fillet010
  Base = -> Fillet009 [Edge77]
  BaseFeature = -> Fillet009
  Radius = 1.9
  Refine = true
  SupportTransform = false
  Suppressed = false
  UseAllEdges = false
FEATURE [PartDesign::Pocket] Pocket005
  BaseFeature = -> Fillet010
  Direction = (0,-1,2e-16)
  Length = 0.8
  Length2 = 5
  Profile = -> Sketch112
  ReferenceAxis = -> Sketch112 [N_Axis]
  Refine = true
  Suppressed = false
  Type = 0
FEATURE [Part::Part2DObjectPython] ShapeString001  # Draft 2D object (typed FeaturePython)
  FontFile = <path>
  Fuse = false
  Justification = 6
  JustificationReference = 0
  KeepLeftMargin = false
  MakeFace = true
  ObliqueAngle = 0
  Placement = pos=(-183.5,3.6,-57.5) rot=(0,0.707107,0.707107;3.14159rad)
  ScaleToSize = true
  Size = 10
  String = AS
  Tracking = 0
FEATURE [PartDesign::Pocket] Pocket013
  BaseFeature = -> Pocket005
  Direction = (-1e-16,-1,2e-16)
  Length = 1
  Length2 = 5
  Profile = -> ShapeString001
  ReferenceAxis = -> ShapeString001 [N_Axis]
  Refine = true
  Suppressed = false
  Type = 0
FEATURE [PartDesign::Pad] Pad020
  Direction = (0,-1,2e-16)
  Length = 25.2
  Length2 = 10
  Midplane = true
  Placement = pos=(0,0,0) rot=(1,0,0;1.5708rad)
  Profile = -> Sketch021
  ReferenceAxis = -> Sketch021 [N_Axis]
  Refine = true
  Suppressed = false
  Type = 0
FEATURE [PartDesign::Body] Body001  label="perno fermo rumble e driver solenoide"
  AllowCompound = false
  Group = -> [Sketch021,Pad020]
  Origin = -> Origin001
  Tip = -> Pad020
FEATURE [PartDesign::Pad] Pad021
  Direction = (0,-1,2e-16)
  Length = 16.8
  Length2 = 10
  Midplane = true
  Placement = pos=(0,0,0) rot=(1,0,0;1.5708rad)
  Profile = -> Sketch061
  ReferenceAxis = -> Sketch061 [N_Axis]
  Refine = true
  Suppressed = false
  Type = 0
FEATURE [PartDesign::Pocket] Pocket014
  BaseFeature = -> Pad021
  Direction = (0,1,-2e-16)
  Length = 12.8
  Length2 = 5
  Midplane = true
  Placement = pos=(0,0,0) rot=(1,0,0;1.5708rad)
  Profile = -> Sketch062
  ReferenceAxis = -> Sketch062 [N_Axis]
  Refine = true
  Suppressed = false
  Type = 0
FEATURE [PartDesign::Pad] Pad022
  BaseFeature = -> Pocket014
  Direction = (0,-1,2e-16)
  Length = 7.6
  Length2 = 10
  Midplane = true
  Placement = pos=(0,0,0) rot=(1,0,0;1.5708rad)
  Profile = -> Sketch063
  ReferenceAxis = -> Sketch063 [N_Axis]
  Refine = true
  Suppressed = false
  Type = 0
FEATURE [PartDesign::Body] Body003  label="blocco switch"
  AllowCompound = false
  Group = -> [Sketch061,Sketch062,Sketch063,Pad021,Pocket014,Pad022]
  Origin = -> Origin003
  Tip = -> Pad022
FEATURE [PartDesign::Pad] Pad024
  Direction = (0,-1,2e-16)
  Length = 17
  Length2 = 10
  Midplane = true
  Placement = pos=(0,0,0) rot=(1,0,0;1.5708rad)
  Profile = -> Sketch045
  ReferenceAxis = -> Sketch045 [N_Axis]
  Refine = true
  Suppressed = false
  Type = 0
FEATURE [PartDesign::Pocket] Pocket015
  BaseFeature = -> Pad024
  Direction = (-1,0,0)
  Length = 8
  Length2 = 5
  Placement = pos=(0,0,0) rot=(1,0,0;1.5708rad)
  Profile = -> Sketch047
  ReferenceAxis = -> Sketch047 [N_Axis]
  Refine = true
  Reversed = true
  Suppressed = false
  Type = 0
FEATURE [PartDesign::Pocket] Pocket016
  BaseFeature = -> Pocket015
  Direction = (-1,0,0)
  Length = 1
  Length2 = 5
  Placement = pos=(0,0,0) rot=(1,0,0;1.5708rad)
  Profile = -> Sketch046
  ReferenceAxis = -> Sketch046 [N_Axis]
  Refine = true
  Reversed = true
  Suppressed = false
  Type = 0
FEATURE [PartDesign::Pocket] Pocket017
  BaseFeature = -> Pocket016
  Direction = (0,1,-2e-16)
  Length = 17
  Length2 = 5
  Midplane = true
  Placement = pos=(0,0,0) rot=(1,0,0;1.5708rad)
  Profile = -> Sketch048
  ReferenceAxis = -> Sketch048 [N_Axis]
  Refine = true
  Suppressed = false
  Type = 0
FEATURE [PartDesign::Pad] Pad025
  BaseFeature = -> Pocket017
  Direction = (0,-1,2e-16)
  Length = 17
  Length2 = 10
  Midplane = true
  Placement = pos=(0,0,0) rot=(1,0,0;1.5708rad)
  Profile = -> Sketch049
  ReferenceAxis = -> Sketch049 [N_Axis]
  Refine = true
  Suppressed = false
  Type = 0
FEATURE [PartDesign::Pad] Pad026
  BaseFeature = -> Pad025
  Direction = (0,-1,2e-16)
  Length = 17
  Length2 = 10
  Midplane = true
  Placement = pos=(0,0,0) rot=(1,0,0;1.5708rad)
  Profile = -> Sketch066
  ReferenceAxis = -> Sketch066 [N_Axis]
  Refine = true
  Suppressed = false
  Type = 0
FEATURE [PartDesign::Pad] Pad027
  BaseFeature = -> Pad026
  Direction = (0,-1,2e-16)
  Length = 5
  Length2 = 10
  Midplane = true
  Placement = pos=(0,0,0) rot=(1,0,0;1.5708rad)
  Profile = -> Sketch064
  ReferenceAxis = -> Sketch064 [N_Axis]
  Refine = true
  Suppressed = false
  Type = 0
FEATURE [PartDesign::Pad] Pad028
  BaseFeature = -> Pad027
  Direction = (1,0,0)
  Length = 1
  Length2 = 10
  Placement = pos=(0,0,0) rot=(1,0,0;1.5708rad)
  Profile = -> Sketch068
  ReferenceAxis = -> Sketch068 [N_Axis]
  Refine = true
  Reversed = true
  Suppressed = false
  Type = 0
FEATURE [PartDesign::Chamfer] Chamfer020
  Angle = 45
  Base = -> Pad028 [Edge73,Edge75,Edge78,Edge77]
  BaseFeature = -> Pad028
  ChamferType = 0
  FlipDirection = false
  Placement = pos=(0,0,0) rot=(1,0,0;1.5708rad)
  Refine = true
  Size = 0.5
  Size2 = 1
  SupportTransform = false
  Suppressed = false
  UseAllEdges = false
FEATURE [PartDesign::Body] Body002  label="supporto per neopixel"
  AllowCompound = false
  Group = -> [Sketch045,Sketch047,Sketch046,Sketch048,Sketch049,Sketch066,Sketch064,Sketch068,Pad024,Pocket015,Pocket016,Pocket017,Pad025,Pad026,Pad027,Pad028,Chamfer020]
  Origin = -> Origin002
  Tip = -> Chamfer020
FEATURE [Sketcher::SketchObject] Sketch134  label="perno fermo rumble002"
  ArcFitTolerance = 1e-06
  AttachmentSupport = -> [XZ_Plane008]
  FullyConstrained = true
  MakeInternals = false
  MapMode = 5
  Placement = pos=(0,0,0) rot=(1,0,0;1.5708rad)
  sketch-geometry (16):
    g0: LineSegment StartX=0 StartY=0.45 StartZ=0 EndX=0 EndY=1.55 EndZ=0
    g1: LineSegment StartX=0.45 StartY=2 StartZ=0 EndX=1.55 EndY=2 EndZ=0
    g2: LineSegment StartX=2 StartY=1.55 StartZ=0 EndX=2 EndY=0.45 EndZ=0
    g3: LineSegment StartX=1.55 StartY=0 StartZ=0 EndX=0.45 EndY=0 EndZ=0
    g4: ArcOfCircle [constr] CenterX=0.45 CenterY=1.55 CenterZ=0 NormalX=0 NormalY=0 NormalZ=1 AngleXU=0 Radius=0.45 StartAngle=1.5708 EndAngle=3.14159
    g5: GeomPoint [constr] X=0 Y=2 Z=0
    g6: LineSegment StartX=0.45 StartY=2 StartZ=0 EndX=0 EndY=1.55 EndZ=0
    g7: ArcOfCircle [constr] CenterX=1.55 CenterY=1.55 CenterZ=0 NormalX=0 NormalY=0 NormalZ=1 AngleXU=0 Radius=0.45 StartAngle=0 EndAngle=1.5708
    g8: GeomPoint [constr] X=2 Y=2 Z=0
    g9: LineSegment StartX=2 StartY=1.55 StartZ=0 EndX=1.55 EndY=2 EndZ=0
    g10: ArcOfCircle [constr] CenterX=1.55 CenterY=0.45 CenterZ=0 NormalX=0 NormalY=0 NormalZ=1 AngleXU=0 Radius=0.45 StartAngle=4.71239 EndAngle=6.28319
    g11: GeomPoint [constr] X=2 Y=0 Z=0
    g12: LineSegment StartX=1.55 StartY=0 StartZ=0 EndX=2 EndY=0.45 EndZ=0
    g13: ArcOfCircle [constr] CenterX=0.45 CenterY=0.45 CenterZ=0 NormalX=0 NormalY=0 NormalZ=1 AngleXU=0 Radius=0.45 StartAngle=3.14159 EndAngle=4.71239
    g14: GeomPoint [constr] X=0 Y=0 Z=0
    g15: LineSegment StartX=0 StartY=0.45 StartZ=0 EndX=0.45 EndY=0 EndZ=0
  constraints (35):
    c: Coincident(g14,g-1)
    c: PointOnObject(g5,g-2)
    c: Horizontal(g1)
    c: Vertical(g2)
    c: Horizontal(g3)
    c: DistanceX(g5,g8) = 2
    c: DistanceY(g11,g8) = 2
    c: PointOnObject(g5,g0)
    c: PointOnObject(g5,g1)
    c: Tangent(g0,g4) = 1.5708
    c: Tangent(g1,g4) = 1.5708
    c: Coincident(g6,g0)
    c: Coincident(g6,g1)
    c: PointOnObject(g8,g2)
    c: PointOnObject(g8,g1)
    c: Tangent(g2,g7) = 1.5708
    c: Tangent(g1,g7) = 1.5708
    c: Coincident(g9,g2)
    c: Coincident(g9,g1)
    c: PointOnObject(g11,g2)
    c: PointOnObject(g11,g3)
    c: Tangent(g2,g10) = 1.5708
    c: Tangent(g3,g10) = 1.5708
    c: Coincident(g12,g2)
    c: Coincident(g12,g3)
    c: PointOnObject(g14,g0)
    c: PointOnObject(g14,g3)
    c: Tangent(g0,g13) = 1.5708
    c: Tangent(g3,g13) = 1.5708
    c: Coincident(g15,g0)
    c: Coincident(g15,g3)
    c: Equal(g6,g9)
    c: Equal(g9,g12)
    c: Equal(g12,g15)
    c: DistanceX(g14,g3) = 0.45
FEATURE [PartDesign::Pad] Pad029
  Direction = (0,-1,2e-16)
  Length = 17
  Length2 = 10
  Midplane = true
  Placement = pos=(0,0,0) rot=(1,0,0;1.5708rad)
  Profile = -> Sketch134
  ReferenceAxis = -> Sketch134 [N_Axis]
  Refine = true
  Suppressed = false
  Type = 0
FEATURE [PartDesign::Body] Body008  label="perno fermo neopixel"
  AllowCompound = false
  Group = -> [Sketch134,Pad029]
  Origin = -> Origin008
  Tip = -> Pad029
FEATURE [Sketcher::SketchObject] Sketch135  label="perno fermo rumble003"
  ArcFitTolerance = 1e-06
  AttachmentSupport = -> [XZ_Plane009]
  FullyConstrained = true
  MakeInternals = false
  MapMode = 5
  Placement = pos=(0,0,0) rot=(1,0,0;1.5708rad)
  sketch-geometry (16):
    g0: LineSegment StartX=4.69e-14 StartY=0.8 StartZ=0 EndX=-3.04e-14 EndY=3.1 EndZ=0
    g1: LineSegment StartX=0.8 StartY=3.9 StartZ=0 EndX=3.1 EndY=3.9 EndZ=0
    g2: LineSegment StartX=3.9 StartY=3.1 StartZ=0 EndX=3.9 EndY=0.8 EndZ=0
    g3: LineSegment StartX=3.1 StartY=0 StartZ=0 EndX=0.8 EndY=0 EndZ=0
    g4: ArcOfCircle [constr] CenterX=0.8 CenterY=3.1 CenterZ=0 NormalX=0 NormalY=0 NormalZ=1 AngleXU=0 Radius=0.8 StartAngle=1.5708 EndAngle=3.14159
    g5: GeomPoint [constr] X=0 Y=3.9 Z=0
    g6: LineSegment StartX=0.8 StartY=3.9 StartZ=0 EndX=-3.04e-14 EndY=3.1 EndZ=0
    g7: ArcOfCircle [constr] CenterX=3.1 CenterY=3.1 CenterZ=0 NormalX=0 NormalY=0 NormalZ=1 AngleXU=0 Radius=0.8 StartAngle=-2.4e-14 EndAngle=1.5708
    g8: GeomPoint [constr] X=3.9 Y=3.9 Z=0
    g9: LineSegment StartX=3.9 StartY=3.1 StartZ=0 EndX=3.1 EndY=3.9 EndZ=0
    g10: ArcOfCircle [constr] CenterX=3.1 CenterY=0.8 CenterZ=0 NormalX=0 NormalY=0 NormalZ=1 AngleXU=0 Radius=0.8 StartAngle=4.71239 EndAngle=6.28319
    g11: GeomPoint [constr] X=3.9 Y=0 Z=0
    g12: LineSegment StartX=3.1 StartY=0 StartZ=0 EndX=3.9 EndY=0.8 EndZ=0
    g13: ArcOfCircle [constr] CenterX=0.8 CenterY=0.8 CenterZ=0 NormalX=0 NormalY=0 NormalZ=1 AngleXU=0 Radius=0.8 StartAngle=3.14159 EndAngle=4.71239
    g14: GeomPoint [constr] X=0 Y=0 Z=0
    g15: LineSegment StartX=4.69e-14 StartY=0.8 StartZ=0 EndX=0.8 EndY=0 EndZ=0
  constraints (35):
    c: Coincident(g14,g-1)
    c: PointOnObject(g5,g-2)
    c: Horizontal(g1)
    c: Vertical(g2)
    c: Horizontal(g3)
    c: DistanceX(g5,g8) = 3.9
    c: DistanceY(g11,g8) = 3.9
    c: PointOnObject(g5,g0)
    c: PointOnObject(g5,g1)
    c: Tangent(g0,g4) = 1.5708
    c: Tangent(g1,g4) = 1.5708
    c: Coincident(g6,g0)
    c: Coincident(g6,g1)
    c: PointOnObject(g8,g2)
    c: PointOnObject(g8,g1)
    c: Tangent(g2,g7) = 1.5708
    c: Tangent(g1,g7) = 1.5708
    c: Coincident(g9,g2)
    c: Coincident(g9,g1)
    c: PointOnObject(g11,g2)
    c: PointOnObject(g11,g3)
    c: Tangent(g2,g10) = 1.5708
    c: Tangent(g3,g10) = 1.5708
    c: Coincident(g12,g2)
    c: Coincident(g12,g3)
    c: PointOnObject(g14,g0)
    c: PointOnObject(g14,g3)
    c: Tangent(g0,g13) = 1.5708
    c: Tangent(g3,g13) = 1.5708
    c: Coincident(g15,g0)
    c: Coincident(g15,g3)
    c: Equal(g6,g9)
    c: Equal(g9,g12)
    c: Equal(g12,g15)
    c: DistanceX(g14,g3) = 0.8
FEATURE [PartDesign::Pad] Pad030
  Direction = (0,-1,2e-16)
  Length = 25.2
  Length2 = 10
  Midplane = true
  Placement = pos=(0,0,0) rot=(1,0,0;1.5708rad)
  Profile = -> Sketch135
  ReferenceAxis = -> Sketch135 [N_Axis]
  Refine = true
  Suppressed = false
  Type = 0
FEATURE [PartDesign::Body] Body009  label="perno fermo switch - caricabatterie - grilletto"
  AllowCompound = false
  Group = -> [Sketch135,Pad030]
  Origin = -> Origin009
  Tip = -> Pad030
FEATURE [Sketcher::SketchObject] Sketch136  label="scavo_rele"
  ArcFitTolerance = 1e-06
  AttachmentSupport = -> [XZ_Plane]
  ExternalGeometry = -> [Sketch]
  FullyConstrained = true
  MakeInternals = false
  MapMode = 5
  Placement = pos=(0,0,0) rot=(1,0,0;1.5708rad)
  sketch-geometry (7):
    g0: LineSegment [constr] StartX=-172.456 StartY=-60.9321 StartZ=0 EndX=-176.597 EndY=-73.6763 EndZ=0
    g1: LineSegment [constr] StartX=-172.456 StartY=-60.9321 StartZ=0 EndX=-170.364 EndY=-61.612 EndZ=0
    g2: LineSegment [constr] StartX=-172.456 StartY=-60.9321 StartZ=0 EndX=-176.07 EndY=-59.7579 EndZ=0
    g3: LineSegment StartX=-176.07 StartY=-59.7579 StartZ=0 EndX=-170.364 EndY=-61.612 EndZ=0
    g4: LineSegment StartX=-176.07 StartY=-59.7579 StartZ=0 EndX=-180.211 EndY=-72.502 EndZ=0
    g5: LineSegment StartX=-170.364 StartY=-61.612 StartZ=0 EndX=-174.505 EndY=-74.3561 EndZ=0
    g6: LineSegment StartX=-180.211 StartY=-72.502 StartZ=0 EndX=-174.505 EndY=-74.3561 EndZ=0
  constraints (19):
    c: Tangent(g0,g-3)
    c: Distance(g0,g-3) = 87.2
    c: Distance(g0,g0) = 13.4
    c: Coincident(g1,g0)
    c: Coincident(g2,g0)
    c: Distance(g2) = 3.8
    c: Distance(g1) = 2.2
    c: Perpendicular(g0,g1)
    c: Perpendicular(g0,g2)
    c: Coincident(g3,g2)
    c: Coincident(g3,g1)
    c: Equal(g4,g0)
    c: Equal(g5,g0)
    c: Parallel(g4,g0)
    c: Parallel(g5,g0)
    c: Coincident(g4,g2)
    c: Coincident(g5,g1)
    c: Coincident(g6,g4)
    c: Coincident(g6,g5)
FEATURE [Part::Extrusion] Extrude076  label="Extrude076 - scavo_rele"
  Base = -> Sketch136
  Dir = (0,-1,2e-16)
  DirMode = 2
  FaceMakerClass = Part::FaceMakerBullseye
  FaceMakerMode = 3
  LengthFwd = 18.2
  LengthRev = 0
  Solid = true
  Symmetric = true
FEATURE [Sketcher::SketchObject] Sketch137  label="scavo_nuovo_driver"
  ArcFitTolerance = 1e-06
  AttachmentSupport = -> [XZ_Plane]
  ExternalGeometry = -> [Sketch]
  FullyConstrained = true
  MakeInternals = false
  MapMode = 5
  Placement = pos=(0,0,0) rot=(1,0,0;1.5708rad)
  sketch-geometry (7):
    g0: LineSegment [constr] StartX=-160.034 StartY=-22.6997 StartZ=0 EndX=-164.854 EndY=-37.5361 EndZ=0
    g1: LineSegment [constr] StartX=-160.034 StartY=-22.6997 StartZ=0 EndX=-156.99 EndY=-23.6885 EndZ=0
    g2: LineSegment [constr] StartX=-160.034 StartY=-22.6997 StartZ=0 EndX=-163.648 EndY=-21.5254 EndZ=0
    g3: LineSegment StartX=-163.648 StartY=-21.5254 StartZ=0 EndX=-156.99 EndY=-23.6885 EndZ=0
    g4: LineSegment StartX=-163.648 StartY=-21.5254 StartZ=0 EndX=-168.468 EndY=-36.3619 EndZ=0
    g5: LineSegment StartX=-156.99 StartY=-23.6885 StartZ=0 EndX=-161.811 EndY=-38.525 EndZ=0
    g6: LineSegment StartX=-168.468 StartY=-36.3619 StartZ=0 EndX=-161.811 EndY=-38.525 EndZ=0
  constraints (19):
    c: Distance(g0,g-3) = 47
    c: Distance(g0) = 15.6
    c: Tangent(g0,g-3)
    c: Coincident(g1,g0)
    c: Coincident(g2,g0)
    c: Distance(g1) = 3.2
    c: Distance(g2) = 3.8
    c: Perpendicular(g0,g1)
    c: Perpendicular(g0,g2)
    c: Coincident(g3,g2)
    c: Coincident(g3,g1)
    c: Equal(g4,g0)
    c: Equal(g5,g0)
    c: Parallel(g4,g0)
    c: Parallel(g5,g0)
    c: Coincident(g4,g2)
    c: Coincident(g5,g1)
    c: Coincident(g6,g4)
    c: Coincident(g6,g5)
FEATURE [Part::Extrusion] Extrude077  label="Extrude077 - scavo_nuovo_driver"
  Base = -> Sketch137
  Dir = (0,-1,2e-16)
  DirMode = 2
  FaceMakerClass = Part::FaceMakerBullseye
  FaceMakerMode = 3
  LengthFwd = 20.8
  LengthRev = 0
  Solid = true
  Symmetric = true
FEATURE [Sketcher::SketchObject] Sketch138  label="scavo_nuovo_driver_alto"
  ArcFitTolerance = 1e-06
  AttachmentSupport = -> [XZ_Plane]
  ExternalGeometry = -> [Sketch]
  FullyConstrained = true
  MakeInternals = false
  MapMode = 5
  Placement = pos=(0,0,0) rot=(1,0,0;1.5708rad)
  sketch-geometry (7):
    g0: LineSegment [constr] StartX=-188.917 StartY=18.1185 StartZ=0 EndX=-187.75 EndY=4.97025 EndZ=0
    g1: LineSegment StartX=-187.75 StartY=4.97025 StartZ=0 EndX=-189.742 EndY=4.79337 EndZ=0
    g2: LineSegment StartX=-187.75 StartY=4.97025 StartZ=0 EndX=-182.769 EndY=5.41245 EndZ=0
    g3: LineSegment StartX=-190.909 StartY=17.9416 StartZ=0 EndX=-189.742 EndY=4.79337 EndZ=0
    g4: LineSegment StartX=-183.937 StartY=18.5607 StartZ=0 EndX=-182.769 EndY=5.41245 EndZ=0
    g5: LineSegment StartX=-190.909 StartY=17.9416 StartZ=0 EndX=-188.917 EndY=18.1185 EndZ=0
    g6: LineSegment StartX=-188.917 StartY=18.1185 StartZ=0 EndX=-183.937 EndY=18.5607 EndZ=0
  constraints (20):
    c: Distance(g0) = 13.2
    c: DistanceY(g-3,g0) = 9
    c: PointOnObject(g0,g-4)
    c: PointOnObject(g0,g-4)
    c: Coincident(g1,g0)
    c: Coincident(g2,g0)
    c: Distance(g1) = 2
    c: Distance(g2) = 5
    c: Perpendicular(g0,g1)
    c: Perpendicular(g0,g2)
    c: Equal(g3,g0)
    c: Parallel(g3,g0)
    c: Coincident(g3,g1)
    c: Equal(g4,g0)
    c: Parallel(g4,g0)
    c: Coincident(g4,g2)
    c: Coincident(g5,g3)
    c: Coincident(g5,g0)
    c: Coincident(g6,g0)
    c: Coincident(g6,g4)
FEATURE [Part::Extrusion] Extrude078  label="Extrude078 - scavo_nuovo_driver_alto"
  Base = -> Sketch138
  Dir = (0,-1,2e-16)
  DirMode = 2
  FaceMakerClass = Part::FaceMakerBullseye
  FaceMakerMode = 3
  LengthFwd = 17.2
  LengthRev = 0
  Solid = true
  Symmetric = true
FEATURE [Sketcher::SketchObject] Sketch139  label="fermi_nuovo_driver_alto"
  ArcFitTolerance = 1e-06
  AttachmentSupport = -> [XZ_Plane]
  ExternalGeometry = -> [Sketch138,Sketch]
  FullyConstrained = true
  MakeInternals = false
  MapMode = 5
  Placement = pos=(0,0,0) rot=(1,0,0;1.5708rad)
  sketch-geometry (17):
    g0: LineSegment [constr] StartX=-188.41 StartY=16.8018 StartZ=0 EndX=-187.948 EndY=14.1416 EndZ=0
    g1: LineSegment [constr] StartX=-187.948 StartY=14.1416 StartZ=0 EndX=-187.486 EndY=11.4815 EndZ=0
    g2: LineSegment StartX=-187.948 StartY=14.1416 StartZ=0 EndX=-187.76 EndY=13.0579 EndZ=0
    g3: LineSegment StartX=-187.948 StartY=14.1416 StartZ=0 EndX=-188.136 EndY=15.2254 EndZ=0
    g4: LineSegment StartX=-187.76 StartY=13.0579 StartZ=0 EndX=-185.592 EndY=13.4346 EndZ=0
    g5: LineSegment StartX=-188.136 StartY=15.2254 StartZ=0 EndX=-185.969 EndY=15.6021 EndZ=0
    g6: LineSegment StartX=-185.969 StartY=15.6021 StartZ=0 EndX=-185.592 EndY=13.4346 EndZ=0
    g7: LineSegment StartX=-187.486 StartY=11.4815 StartZ=0 EndX=-189.062 EndY=11.2075 EndZ=0
    g8: LineSegment StartX=-188.41 StartY=16.8018 StartZ=0 EndX=-189.987 EndY=16.5278 EndZ=0
    g9: LineSegment StartX=-189.987 StartY=16.5278 StartZ=0 EndX=-189.062 EndY=11.2075 EndZ=0
    g10: LineSegment StartX=-187.486 StartY=11.4815 StartZ=0 EndX=-185.318 EndY=11.8582 EndZ=0
    g11: LineSegment StartX=-188.41 StartY=16.8018 StartZ=0 EndX=-186.243 EndY=17.1785 EndZ=0
    g12: LineSegment StartX=-184.393 StartY=15.8761 StartZ=0 EndX=-184.016 EndY=13.7086 EndZ=0
    g13: ArcOfCircle CenterX=-185.969 CenterY=15.6021 CenterZ=0 NormalX=0 NormalY=0 NormalZ=1 AngleXU=0 Radius=1.6 StartAngle=0.172085 EndAngle=1.74288
    g14: GeomPoint [constr] X=-184.667 Y=17.4525 Z=0
    g15: ArcOfCircle CenterX=-185.592 CenterY=13.4346 CenterZ=0 NormalX=0 NormalY=0 NormalZ=1 AngleXU=0 Radius=1.6 StartAngle=4.88447 EndAngle=6.45527
    g16: GeomPoint [constr] X=-183.742 Y=12.1322 Z=0
  constraints (43):
    c: Tangent(g1,g0) = -1.5708
    c: Distance(g0) = 2.7
    c: Equal(g1,g0)
    c: Tangent(g1,g-5)
    c: Coincident(g2,g0)
    c: Coincident(g3,g0)
    c: Distance(g2) = 1.1
    c: Equal(g3,g2)
    c: PointOnObject(g3,g2)
    c: Coincident(g4,g2)
    c: Coincident(g5,g3)
    c: Distance(g4) = 2.2
    c: Equal(g4,g5)
    c: Perpendicular(g1,g4)
    c: Perpendicular(g0,g5)
    c: Coincident(g6,g5)
    c: Coincident(g6,g4)
    c: Coincident(g7,g1)
    c: Coincident(g8,g0)
    c: Distance(g7) = 1.6
    c: Equal(g7,g8)
    c: Perpendicular(g1,g7)
    c: Perpendicular(g8,g0)
    c: Coincident(g9,g8)
    c: Coincident(g9,g7)
    c: Coincident(g10,g1)
    c: Coincident(g11,g0)
    c: Distance(g10,g16) = 3.8
    c: Perpendicular(g1,g10)
    c: Perpendicular(g1,g11)
    c: DistanceY(g0,g-4) = 3.8
    c: PointOnObject(g14,g12)
    c: PointOnObject(g14,g11)
    c: Tangent(g12,g13) = 1.5708
    c: Tangent(g11,g13) = 1.5708
    c: PointOnObject(g16,g12)
    c: PointOnObject(g16,g10)
    c: Tangent(g12,g15) = 1.5708
    c: Tangent(g10,g15) = -1.5708
    c: Equal(g13,g15)
    c: Coincident(g13,g5)
    c: Parallel(g2,g0)
    c: PointOnObject(g0,g-5)
FEATURE [Part::Extrusion] Extrude079  label="Extrude079 - fermi_nuovo_driver_alto"
  Base = -> Sketch139
  Dir = (0,-1,2e-16)
  DirMode = 2
  FaceMakerClass = Part::FaceMakerBullseye
  FaceMakerMode = 3
  LengthFwd = 25.2
  LengthRev = 0
  Solid = true
  Symmetric = true
FEATURE [Sketcher::SketchObject] Sketch140  label="scavo_diodo_nuovo_driver_alto"
  ArcFitTolerance = 1e-06
  AttachmentSupport = -> [XZ_Plane]
  ExternalGeometry = -> [Sketch138]
  FullyConstrained = true
  MakeInternals = false
  MapMode = 5
  Placement = pos=(0,0,0) rot=(1,0,0;1.5708rad)
  sketch-geometry (4):
    g0: LineSegment StartX=-190.909 StartY=17.9416 StartZ=0 EndX=-189.742 EndY=4.79337 EndZ=0
    g1: LineSegment StartX=-193.898 StartY=17.6763 StartZ=0 EndX=-192.73 EndY=4.52805 EndZ=0
    g2: LineSegment StartX=-190.909 StartY=17.9416 StartZ=0 EndX=-193.898 EndY=17.6763 EndZ=0
    g3: LineSegment StartX=-192.73 StartY=4.52805 StartZ=0 EndX=-189.742 EndY=4.79337 EndZ=0
  constraints (11):
    c: Equal(g0,g-3)
    c: Parallel(g0,g-3)
    c: Equal(g1,g-3)
    c: Parallel(g1,g-3)
    c: Coincident(g2,g0)
    c: Distance(g2) = 3
    c: Perpendicular(g0,g2)
    c: Coincident(g1,g2)
    c: Coincident(g3,g1)
    c: Coincident(g3,g0)
    c: Coincident(g0,g-3)
FEATURE [Part::Extrusion] Extrude080  label="Extrude080 - scavo_diodo_nuovo_driver_alto"
  Base = -> Sketch140
  Dir = (0,-1,2e-16)
  DirMode = 2
  FaceMakerClass = Part::FaceMakerBullseye
  FaceMakerMode = 3
  LengthFwd = 4
  LengthRev = 0
  Placement = pos=(0,7.8,0) rot=(0,0,1;0rad)
  Solid = true
  Symmetric = false
FEATURE [Part::MultiFuse] Fusion001
  Refine = true
  Shapes = -> [Cut043,Extrude079]
FEATURE [Part::Cut] Cut044
  Base = -> Fusion001
  Refine = true
  Tool = -> Extrude078
FEATURE [Part::Cut] Cut045
  Base = -> Cut044
  Refine = true
  Tool = -> Extrude080
FEATURE [Sketcher::SketchObject] Sketch141  label="fermi_nuovo_driver"
  ArcFitTolerance = 1e-06
  AttachmentSupport = -> [XZ_Plane]
  ExternalGeometry = -> [Sketch,Sketch137]
  FullyConstrained = true
  MakeInternals = false
  MapMode = 5
  Placement = pos=(0,0,0) rot=(1,0,0;1.5708rad)
  sketch-geometry (17):
    g0: LineSegment [constr] StartX=-156.99 StartY=-23.6885 StartZ=0 EndX=-160.034 EndY=-22.6997 EndZ=0
    g1: LineSegment [constr] StartX=-160.034 StartY=-22.6997 StartZ=0 EndX=-162.815 EndY=-31.2592 EndZ=0
    g2: LineSegment [constr] StartX=-162.815 StartY=-31.2592 StartZ=0 EndX=-164.484 EndY=-36.3949 EndZ=0
    g3: LineSegment StartX=-164.484 StartY=-36.3949 StartZ=0 EndX=-166.576 EndY=-35.715 EndZ=0
    g4: LineSegment StartX=-167.603 StartY=-33.6989 StartZ=0 EndX=-166.923 EndY=-31.6066 EndZ=0
    g5: LineSegment StartX=-164.907 StartY=-30.5793 StartZ=0 EndX=-161.293 EndY=-31.7536 EndZ=0
    g6: LineSegment StartX=-161.293 StartY=-31.7536 StartZ=0 EndX=-162.962 EndY=-36.8893 EndZ=0
    g7: LineSegment StartX=-164.484 StartY=-36.3949 StartZ=0 EndX=-162.962 EndY=-36.8893 EndZ=0
    g8: LineSegment StartX=-165.402 StartY=-32.101 StartZ=0 EndX=-166.082 EndY=-34.1933 EndZ=0
    g9: LineSegment StartX=-166.082 StartY=-34.1933 StartZ=0 EndX=-163.989 EndY=-34.8732 EndZ=0
    g10: LineSegment StartX=-163.989 StartY=-34.8732 StartZ=0 EndX=-163.309 EndY=-32.7809 EndZ=0
    g11: LineSegment StartX=-163.309 StartY=-32.7809 StartZ=0 EndX=-165.402 EndY=-32.101 EndZ=0
    g12: ArcOfCircle CenterX=-165.402 CenterY=-32.101 CenterZ=0 NormalX=0 NormalY=0 NormalZ=1 AngleXU=0 Radius=1.6 StartAngle=1.25664 EndAngle=2.82743
    g13: GeomPoint [constr] X=-166.429 Y=-30.0849 Z=0
    g14: ArcOfCircle CenterX=-166.082 CenterY=-34.1933 CenterZ=0 NormalX=0 NormalY=0 NormalZ=1 AngleXU=0 Radius=1.6 StartAngle=2.82743 EndAngle=4.39823
    g15: GeomPoint [constr] X=-168.098 Y=-35.2206 Z=0
    g16: LineSegment [constr] StartX=-160.034 StartY=-22.6997 StartZ=0 EndX=-164.854 EndY=-37.5361 EndZ=0
  constraints (44):
    c: Coincident(g0,g-4)
    c: PointOnObject(g0,g-3)
    c: Parallel(g0,g-4)
    c: Coincident(g1,g0)
    c: Parallel(g1,g-3)
    c: Coincident(g2,g1)
    c: Distance(g2) = 5.4
    c: Coincident(g3,g2)
    c: Parallel(g2,g-3)
    c: Distance(g15,g13) = 5.4
    c: Perpendicular(g3,g2)
    c: Parallel(g4,g2)
    c: Distance(g5,g13) = 5.4
    c: Distance(g3,g15) = 3.8
    c: Perpendicular(g4,g5)
    c: Coincident(g6,g5)
    c: Distance(g6) = 5.4
    c: Parallel(g6,g4)
    c: Coincident(g7,g2)
    c: Coincident(g7,g6)
    c: Coincident(g8,g9)
    c: Coincident(g9,g10)
    c: Coincident(g10,g11)
    c: Coincident(g11,g8)
    c: Distance(g8,g10) = 2.2
    c: Distance(g9,g11) = 2.2
    c: Perpendicular(g11,g8)
    c: Equal(g8,g10)
    c: Equal(g11,g9)
    c: Tangent(g10,g2)
    c: Distance(g10,g1) = 1.6
    c: PointOnObject(g13,g4)
    c: PointOnObject(g13,g5)
    c: Tangent(g4,g12) = 1.5708
    c: Tangent(g5,g12) = 1.5708
    c: PointOnObject(g15,g4)
    c: Tangent(g4,g14) = 1.5708
    c: Tangent(g3,g14) = 1.5708
    c: Equal(g14,g12)
    c: Coincident(g12,g8)
    c: Coincident(g16,g0)
    c: PointOnObject(g16,g-5)
    c: Parallel(g16,g-3)
    c: Distance(g16,g2) = 1.2
FEATURE [Part::Extrusion] Extrude081  label="Extrude081 - fermi_nuovo_driver"
  Base = -> Sketch141
  Dir = (0,-1,2e-16)
  DirMode = 2
  FaceMakerClass = Part::FaceMakerBullseye
  FaceMakerMode = 3
  LengthFwd = 25.2
  LengthRev = 0
  Solid = true
  Symmetric = true
FEATURE [Part::MultiFuse] Fusion002
  Refine = true
  Shapes = -> [Cut045,Extrude081]
FEATURE [Part::Cut] Cut046
  Base = -> Fusion002
  Refine = true
  Tool = -> Extrude077
FEATURE [Sketcher::SketchObject] Sketch142  label="fermi_rele"
  ArcFitTolerance = 1e-06
  AttachmentSupport = -> [XZ_Plane]
  ExternalGeometry = -> [Sketch,Sketch136]
  FullyConstrained = true
  MakeInternals = false
  MapMode = 5
  Placement = pos=(0,0,0) rot=(1,0,0;1.5708rad)
  sketch-geometry (15):
    g0: LineSegment StartX=-176.936 StartY=-62.4208 StartZ=0 EndX=-177.615 EndY=-64.5131 EndZ=0
    g1: LineSegment StartX=-174.919 StartY=-61.3936 StartZ=0 EndX=-171.305 EndY=-62.5678 EndZ=0
    g2: LineSegment StartX=-171.305 StartY=-62.5678 StartZ=0 EndX=-172.974 EndY=-67.7035 EndZ=0
    g3: LineSegment StartX=-176.588 StartY=-66.5293 StartZ=0 EndX=-172.974 EndY=-67.7035 EndZ=0
    g4: LineSegment StartX=-175.414 StartY=-62.9152 StartZ=0 EndX=-173.322 EndY=-63.5951 EndZ=0
    g5: LineSegment StartX=-175.414 StartY=-62.9152 StartZ=0 EndX=-176.094 EndY=-65.0076 EndZ=0
    g6: LineSegment StartX=-173.322 StartY=-63.5951 StartZ=0 EndX=-174.001 EndY=-65.6874 EndZ=0
    g7: LineSegment StartX=-176.094 StartY=-65.0076 StartZ=0 EndX=-174.001 EndY=-65.6874 EndZ=0
    g8: LineSegment [constr] StartX=-173.322 StartY=-63.5951 StartZ=0 EndX=-172.827 EndY=-62.0734 EndZ=0
    g9: LineSegment [constr] StartX=-173.322 StartY=-63.5951 StartZ=0 EndX=-171.8 EndY=-64.0895 EndZ=0
    g10: LineSegment [constr] StartX=-170.364 StartY=-61.612 StartZ=0 EndX=-172.456 EndY=-60.9321 EndZ=0
    g11: ArcOfCircle CenterX=-175.414 CenterY=-62.9152 CenterZ=0 NormalX=0 NormalY=0 NormalZ=1 AngleXU=0 Radius=1.6 StartAngle=1.25664 EndAngle=2.82743
    g12: GeomPoint [constr] X=-176.441 Y=-60.8991 Z=0
    g13: ArcOfCircle CenterX=-176.094 CenterY=-65.0076 CenterZ=0 NormalX=0 NormalY=0 NormalZ=1 AngleXU=0 Radius=1.6 StartAngle=2.82743 EndAngle=4.39823
    g14: GeomPoint [constr] X=-178.11 Y=-66.0348 Z=0
  constraints (39):
    c: Distance(g14,g12) = 5.4
    c: Distance(g1,g12) = 5.4
    c: Perpendicular(g1,g0)
    c: Coincident(g2,g1)
    c: Parallel(g2,g0)
    c: Coincident(g3,g2)
    c: Parallel(g2,g-3)
    c: Coincident(g5,g4)
    c: Distance(g5) = 2.2
    c: Distance(g4) = 2.2
    c: Perpendicular(g4,g5)
    c: Coincident(g6,g4)
    c: Equal(g6,g5)
    c: Parallel(g6,g5)
    c: Coincident(g7,g5)
    c: Coincident(g7,g6)
    c: Coincident(g8,g4)
    c: Coincident(g9,g4)
    c: Distance(g8) = 1.6
    c: Distance(g9) = 1.6
    c: Parallel(g8,g6)
    c: Parallel(g9,g4)
    c: PointOnObject(g8,g1)
    c: PointOnObject(g9,g2)
    c: Coincident(g10,g-4)
    c: Parallel(g10,g-4)
    c: PointOnObject(g10,g-3)
    c: Tangent(g6,g-3) = 1.5708
    c: Distance(g4,g10) = 2.8
    c: PointOnObject(g12,g1)
    c: Tangent(g1,g11) = 1.5708
    c: Tangent(g0,g11) = -1.5708
    c: PointOnObject(g14,g3)
    c: PointOnObject(g14,g0)
    c: Tangent(g3,g13) = -1.5708
    c: Tangent(g0,g13) = -1.5708
    c: Equal(g11,g13)
    c: Coincident(g11,g4)
    c: Parallel(g3,g1)
FEATURE [Part::Extrusion] Extrude082  label="Extrude082 - fermi_rele"
  Base = -> Sketch142
  Dir = (0,-1,2e-16)
  DirMode = 2
  FaceMakerClass = Part::FaceMakerBullseye
  FaceMakerMode = 3
  LengthFwd = 25.2
  LengthRev = 0
  Solid = true
  Symmetric = true
FEATURE [Part::MultiFuse] Fusion003
  Refine = true
  Shapes = -> [Cut046,Extrude082]
FEATURE [Part::Cut] Cut047
  Base = -> Fusion003
  Refine = true
  Tool = -> Extrude076
FEATURE [Sketcher::SketchObject] Sketch143  label="foro_passaggio_cavi_led_batteria"
  ArcFitTolerance = 1e-06
  AttachmentSupport = -> [XZ_Plane]
  ExternalGeometry = -> [Sketch,Sketch042,Sketch036]
  FullyConstrained = true
  MakeInternals = false
  MapMode = 5
  Placement = pos=(0,0,0) rot=(1,0,0;1.5708rad)
  sketch-geometry (4):
    g0: LineSegment StartX=-207.775 StartY=-41.3701 StartZ=0 EndX=-213.607 EndY=-53.8767 EndZ=0
    g1: LineSegment StartX=-213.607 StartY=-53.8767 StartZ=0 EndX=-211.843 EndY=-59.5559 EndZ=0
    g2: LineSegment StartX=-207.775 StartY=-41.3701 StartZ=0 EndX=-207.775 EndY=-50.8316 EndZ=0
    g3: LineSegment StartX=-207.775 StartY=-50.8316 StartZ=0 EndX=-211.843 EndY=-59.5559 EndZ=0
  constraints (9):
    c: Coincident(g0,g-3)
    c: PointOnObject(g1,g-6)
    c: Coincident(g1,g0)
    c: Coincident(g2,g0)
    c: Coincident(g2,g-7)
    c: Coincident(g3,g2)
    c: Parallel(g3,g0)
    c: Coincident(g3,g1)
    c: Coincident(g0,g-5)
FEATURE [Part::Extrusion] Extrude083  label="Extrude083 - foro_passaggio_cavi_led_batteria"
  Base = -> Sketch143
  Dir = (0,-1,2e-16)
  DirMode = 2
  FaceMakerClass = Part::FaceMakerBullseye
  FaceMakerMode = 3
  LengthFwd = 6
  LengthRev = 0
  Solid = true
  Symmetric = true
FEATURE [Part::Cut] Cut048
  Base = -> Cut047
  Refine = true
  Tool = -> Extrude083
FEATURE [Sketcher::SketchObject] Sketch144  label="foro_areazione_alimentatore"
  ArcFitTolerance = 1e-06
  AttachmentSupport = -> [XZ_Plane]
  ExternalGeometry = -> [Sketch036]
  FullyConstrained = true
  MakeInternals = false
  MapMode = 5
  Placement = pos=(0,0,0) rot=(1,0,0;1.5708rad)
  sketch-geometry (4):
    g0: LineSegment StartX=-211.843 StartY=-60.3701 StartZ=0 EndX=-207.775 EndY=-60.3701 EndZ=0
    g1: LineSegment StartX=-207.775 StartY=-60.3701 StartZ=0 EndX=-207.775 EndY=-70.3701 EndZ=0
    g2: LineSegment StartX=-211.843 StartY=-60.3701 StartZ=0 EndX=-211.843 EndY=-70.3701 EndZ=0
    g3: LineSegment StartX=-207.775 StartY=-70.3701 StartZ=0 EndX=-211.843 EndY=-70.3701 EndZ=0
  constraints (11):
    c: Horizontal(g0)
    c: Distance(g1) = 10
    c: Coincident(g1,g0)
    c: Tangent(g1,g-3)
    c: PointOnObject(g0,g-4)
    c: Coincident(g2,g0)
    c: PointOnObject(g2,g-4)
    c: Coincident(g3,g1)
    c: Horizontal(g3)
    c: Coincident(g3,g2)
    c: DistanceY(g0,g-3) = 19
FEATURE [Part::Extrusion] Extrude084  label="Extrude084 - foro_areazione_alimentatore"
  Base = -> Sketch144
  Dir = (0,-1,2e-16)
  DirMode = 2
  FaceMakerClass = Part::FaceMakerBullseye
  FaceMakerMode = 3
  LengthFwd = 10
  LengthRev = 0
  Solid = true
  Symmetric = true
FEATURE [Part::Cut] Cut049
  Base = -> Cut048
  Refine = true
  Tool = -> Extrude084
FEATURE [Sketcher::SketchObject] Sketch145  label="foro_per_condesatore"
  ArcFitTolerance = 1e-06
  AttachmentSupport = -> [XZ_Plane]
  ExternalGeometry = -> [Sketch138]
  FullyConstrained = true
  MakeInternals = false
  MapMode = 5
  Placement = pos=(0,0,0) rot=(1,0,0;1.5708rad)
  sketch-geometry (1):
    g0: Circle CenterX=-179.742 CenterY=9.59337 CenterZ=0 NormalX=0 NormalY=0 NormalZ=1 AngleXU=0 Radius=5.4
  constraints (3):
    c: Diameter(g0) = 10.8
    c: DistanceX(g-3,g0) = 10
    c: DistanceY(g-3,g0) = 4.8
FEATURE [Part::Extrusion] Extrude085  label="Extrude085 - foro_per_condesatore"
  Base = -> Sketch145
  Dir = (0,-1,2e-16)
  DirMode = 2
  FaceMakerClass = Part::FaceMakerBullseye
  FaceMakerMode = 3
  LengthFwd = 25.2
  LengthRev = 0
  Solid = true
  Symmetric = true
FEATURE [Part::Cut] Cut050
  Base = -> Cut049
  Refine = true
  Tool = -> Extrude085
FEATURE [Sketcher::SketchObject] Sketch146  label="scavo_pulsante_6x6_per_led_batteria"
  ArcFitTolerance = 1e-06
  AttachmentSupport = -> [XZ_Plane]
  ExternalGeometry = -> [Sketch016]
  FullyConstrained = true
  MakeInternals = false
  MapMode = 5
  Placement = pos=(0,0,0) rot=(1,0,0;1.5708rad)
  sketch-geometry (5):
    g0: LineSegment StartX=-216.643 StartY=-65.8316 StartZ=0 EndX=-216.643 EndY=-72.8316 EndZ=0
    g1: LineSegment StartX=-216.643 StartY=-72.8316 StartZ=0 EndX=-210.243 EndY=-72.8316 EndZ=0
    g2: LineSegment StartX=-210.243 StartY=-72.8316 StartZ=0 EndX=-210.243 EndY=-65.8316 EndZ=0
    g3: LineSegment StartX=-210.243 StartY=-65.8316 StartZ=0 EndX=-216.643 EndY=-65.8316 EndZ=0
    g4: GeomPoint [constr] X=-213.443 Y=-69.3316 Z=0
  constraints (13):
    c: Coincident(g0,g1)
    c: Coincident(g1,g2)
    c: Coincident(g2,g3)
    c: Coincident(g3,g0)
    c: Vertical(g0)
    c: Vertical(g2)
    c: Horizontal(g1)
    c: Horizontal(g3)
    c: Distance(g0,g2) = 6.4
    c: Distance(g1,g3) = 7
    c: Tangent(g1,g-3)
    c: Symmetric(g0,g2,g4)
    c: Vertical(g-3,g4)
FEATURE [Part::Extrusion] Extrude086  label="Extrude086 - scavo_pulsante_6x6_per_led_batteria"
  Base = -> Sketch146
  Dir = (0,-1,2e-16)
  DirMode = 2
  FaceMakerClass = Part::FaceMakerBullseye
  FaceMakerMode = 3
  LengthFwd = 4
  LengthRev = 0
  Placement = pos=(0,12.6,0) rot=(0,0,1;0rad)
  Solid = true
  Symmetric = false
FEATURE [Sketcher::SketchObject] Sketch147  label="scavo_led_stato_batteria"
  ArcFitTolerance = 1e-06
  AttachmentSupport = -> [XZ_Plane]
  ExternalGeometry = -> [Sketch016]
  FullyConstrained = true
  MakeInternals = false
  MapMode = 5
  Placement = pos=(0,0,0) rot=(1,0,0;1.5708rad)
  sketch-geometry (5):
    g0: LineSegment StartX=-215.843 StartY=-56.2316 StartZ=0 EndX=-215.843 EndY=-65.4316 EndZ=0
    g1: LineSegment StartX=-215.843 StartY=-65.4316 StartZ=0 EndX=-211.043 EndY=-65.4316 EndZ=0
    g2: LineSegment StartX=-211.043 StartY=-65.4316 StartZ=0 EndX=-211.043 EndY=-56.2316 EndZ=0
    g3: LineSegment StartX=-211.043 StartY=-56.2316 StartZ=0 EndX=-215.843 EndY=-56.2316 EndZ=0
    g4: GeomPoint [constr] X=-213.443 Y=-60.8316 Z=0
  constraints (13):
    c: Coincident(g0,g1)
    c: Coincident(g1,g2)
    c: Coincident(g2,g3)
    c: Coincident(g3,g0)
    c: Distance(g0,g2) = 4.8
    c: Distance(g1,g3) = 9.2
    c: Equal(g0,g2)
    c: Equal(g1,g3)
    c: Perpendicular(g3,g0)
    c: DistanceY(g-3,g0) = 11.4
    c: Vertical(g2)
    c: Symmetric(g0,g2,g4)
    c: Vertical(g4,g-3)
FEATURE [Part::Extrusion] Extrude087  label="Extrude087 - scavo_led_stato_batteria"
  Base = -> Sketch147
  Dir = (0,-1,2e-16)
  DirMode = 2
  FaceMakerClass = Part::FaceMakerBullseye
  FaceMakerMode = 3
  LengthFwd = 2.2
  LengthRev = 0
  Placement = pos=(0,12.6,0) rot=(0,0,1;0rad)
  Solid = true
  Symmetric = false
FEATURE [Sketcher::SketchObject] Sketch148
  ArcFitTolerance = 1e-06
  AttachmentSupport = -> [Pad016]
  ExternalGeometry = -> [Pad016]
  FullyConstrained = true
  MakeInternals = false
  MapMode = 5
  Placement = pos=(0,0,-80.4316) rot=(1,0,0;3.14159rad)
  sketch-geometry (8):
    g0: LineSegment StartX=-176.685 StartY=3.6 StartZ=0 EndX=-186.685 EndY=3.6 EndZ=0
    g1: LineSegment StartX=-176.685 StartY=3.6 StartZ=0 EndX=-176.685 EndY=-9e-16 EndZ=0
    g2: LineSegment [constr] StartX=-186.685 StartY=3.6 StartZ=0 EndX=-186.685 EndY=-9e-16 EndZ=0
    g3: ArcOfEllipse CenterX=-186.685 CenterY=-9e-16 CenterZ=0 NormalX=0 NormalY=0 NormalZ=1 MajorRadius=10 MinorRadius=3.6 AngleXU=0 StartAngle=0 EndAngle=1.5708
    g4: LineSegment [constr] StartX=-176.685 StartY=-1e-15 StartZ=0 EndX=-196.685 EndY=-1e-15 EndZ=0
    g5: LineSegment [constr] StartX=-186.685 StartY=3.6 StartZ=0 EndX=-186.685 EndY=-3.6 EndZ=0
    g6: GeomPoint [constr] X=-177.356 Y=-1e-15 Z=0
    g7: GeomPoint [constr] X=-196.015 Y=-1e-15 Z=0
  constraints (13):
    c: Distance(g0) = 10
    c: Coincident(g0,g-5)
    c: PointOnObject(g0,g-3)
    c: Coincident(g1,g0)
    c: Coincident(g1,g-5)
    c: Coincident(g2,g0)
    c: Vertical(g2)
    c: PointOnObject(g2,g-4)
    c: InternalAlignment(g4-g7 -> g3) x4
    c: Coincident(g3,g2)
    c: Coincident(g3,g0)
    c: Coincident(g3,g1)
    c: Horizontal(g4)
FEATURE [PartDesign::SubtractivePipe] SubtractivePipe004
  AuxilleryCurvelinear = true
  AuxillerySpineTangent = false
  BaseFeature = -> Pad016
  Binormal = (0,0,0)
  Mode = 0
  Profile = -> Sketch148
  Refine = true
  Spine = -> Pad016 [Edge253]
  SpineTangent = false
  Suppressed = false
  Transformation = 0
  Transition = 0
FEATURE [Sketcher::SketchObject] Sketch149
  ArcFitTolerance = 1e-06
  AttachmentSupport = -> [Pad016]
  ExternalGeometry = -> [Pad016]
  FullyConstrained = true
  MakeInternals = false
  MapMode = 5
  Placement = pos=(0,0,-80.4316) rot=(1,0,0;3.14159rad)
  sketch-geometry (8):
    g0: LineSegment StartX=-215.932 StartY=3.6 StartZ=0 EndX=-205.932 EndY=3.6 EndZ=0
    g1: LineSegment StartX=-215.932 StartY=3.6 StartZ=0 EndX=-215.932 EndY=-4e-16 EndZ=0
    g2: LineSegment [constr] StartX=-205.932 StartY=3.6 StartZ=0 EndX=-205.932 EndY=-9e-16 EndZ=0
    g3: ArcOfEllipse CenterX=-205.932 CenterY=-1e-15 CenterZ=0 NormalX=0 NormalY=0 NormalZ=1 MajorRadius=10 MinorRadius=3.6 AngleXU=-3.14159 StartAngle=4.71239 EndAngle=6.28319
    g4: LineSegment [constr] StartX=-215.932 StartY=-1e-15 StartZ=0 EndX=-195.932 EndY=-1e-15 EndZ=0
    g5: LineSegment [constr] StartX=-205.932 StartY=-3.6 StartZ=0 EndX=-205.932 EndY=3.6 EndZ=0
    g6: GeomPoint [constr] X=-215.262 Y=-2.1e-15 Z=0
    g7: GeomPoint [constr] X=-196.602 Y=-9e-16 Z=0
  constraints (13):
    c: Distance(g0) = 10
    c: Coincident(g0,g-5)
    c: PointOnObject(g0,g-5)
    c: Coincident(g1,g0)
    c: Coincident(g1,g-4)
    c: Coincident(g2,g0)
    c: Vertical(g2)
    c: PointOnObject(g2,g-3)
    c: InternalAlignment(g4-g7 -> g3) x4
    c: Coincident(g3,g2)
    c: Coincident(g3,g0)
    c: Coincident(g3,g1)
    c: Horizontal(g4)
FEATURE [PartDesign::SubtractivePipe] SubtractivePipe005
  AuxilleryCurvelinear = true
  AuxillerySpineTangent = false
  BaseFeature = -> SubtractivePipe004
  Binormal = (0,0,0)
  Mode = 0
  Profile = -> Sketch149
  Refine = true
  Spine = -> Pad016 [Edge251,Edge256,Edge255]
  SpineTangent = false
  Suppressed = false
  Transformation = 0
  Transition = 0
FEATURE [PartDesign::SubtractiveLoft] SubtractiveLoft002
  BaseFeature = -> SubtractivePipe005
  Closed = false
  Profile = -> Sketch129
  Refine = true
  Ruled = false
  Sections = -> [Sketch130]
  Suppressed = false
FEATURE [PartDesign::SubtractiveLoft] SubtractiveLoft003
  BaseFeature = -> SubtractiveLoft002
  Closed = false
  Profile = -> Clone2D001
  Refine = true
  Ruled = false
  Sections = -> [Sketch131]
  Suppressed = false
FEATURE [PartDesign::Chamfer] Chamfer010
  Angle = 45
  Base = -> SubtractiveLoft003 [Edge203,Edge204,Edge202,Edge201,Edge195]
  BaseFeature = -> SubtractiveLoft003
  ChamferType = 0
  FlipDirection = false
  Refine = true
  Size = 1.5
  Size2 = 1
  SupportTransform = false
  Suppressed = false
  UseAllEdges = false
FEATURE [PartDesign::Chamfer] Chamfer011
  Angle = 45
  Base = -> Chamfer010 [Edge15]
  BaseFeature = -> Chamfer010
  ChamferType = 0
  FlipDirection = false
  Refine = true
  Size = 1.6
  Size2 = 1
  SupportTransform = false
  Suppressed = false
  UseAllEdges = false
FEATURE [PartDesign::Chamfer] Chamfer012
  Angle = 45
  Base = -> Chamfer011 [Edge10]
  BaseFeature = -> Chamfer011
  ChamferType = 0
  FlipDirection = false
  Refine = true
  Size = 3.5
  Size2 = 1
  SupportTransform = false
  Suppressed = false
  UseAllEdges = false
FEATURE [PartDesign::Chamfer] Chamfer013
  Angle = 45
  Base = -> Chamfer012 [Edge94]
  BaseFeature = -> Chamfer012
  ChamferType = 0
  FlipDirection = false
  Refine = true
  Size = 1.9
  Size2 = 1
  SupportTransform = false
  Suppressed = false
  UseAllEdges = false
FEATURE [PartDesign::Fillet] Fillet007
  Base = -> Chamfer013 [Edge83]
  BaseFeature = -> Chamfer013
  Radius = 1.1
  Refine = true
  SupportTransform = false
  Suppressed = false
  UseAllEdges = false
FEATURE [PartDesign::Fillet] Fillet008
  Base = -> Fillet007 [Edge75]
  BaseFeature = -> Fillet007
  Radius = 1.9
  Refine = true
  SupportTransform = false
  Suppressed = false
  UseAllEdges = false
FEATURE [PartDesign::Pocket] Pocket011
  BaseFeature = -> Fillet008
  Direction = (0,1,-2e-16)
  Length = 0.8
  Length2 = 5
  Profile = -> Sketch132
  ReferenceAxis = -> Sketch132 [N_Axis]
  Refine = true
  Suppressed = false
  Type = 0
FEATURE [PartDesign::Pocket] Pocket012
  BaseFeature = -> Pocket011
  Direction = (0,1,0)
  Length = 1
  Length2 = 5
  Profile = -> ShapeString
  ReferenceAxis = -> ShapeString [N_Axis]
  Refine = true
  Suppressed = false
  Type = 0
FEATURE [Sketcher::SketchObject] Sketch150
  ArcFitTolerance = 1e-06
  AttachmentSupport = -> [Pad008]
  ExternalGeometry = -> [Pad008]
  FullyConstrained = true
  MakeInternals = false
  MapMode = 5
  Placement = pos=(0,3.6,0) rot=(0,0.707107,0.707107;3.14159rad)
  sketch-geometry (7):
    g0: LineSegment [constr] StartX=210.343 StartY=-66.0316 StartZ=0 EndX=210.343 EndY=-72.8316 EndZ=0
    g1: LineSegment [constr] StartX=210.343 StartY=-72.8316 StartZ=0 EndX=216.543 EndY=-72.8316 EndZ=0
    g2: LineSegment [constr] StartX=216.543 StartY=-72.8316 StartZ=0 EndX=216.543 EndY=-66.0316 EndZ=0
    g3: LineSegment [constr] StartX=216.543 StartY=-66.0316 StartZ=0 EndX=210.343 EndY=-66.0316 EndZ=0
    g4: LineSegment [constr] StartX=210.343 StartY=-72.8316 StartZ=0 EndX=216.543 EndY=-66.0316 EndZ=0
    g5: LineSegment [constr] StartX=210.343 StartY=-66.0316 StartZ=0 EndX=213.443 EndY=-69.4316 EndZ=0
    g6: Circle CenterX=213.443 CenterY=-69.4316 CenterZ=0 NormalX=0 NormalY=0 NormalZ=1 AngleXU=0 Radius=2
  constraints (18):
    c: Coincident(g0,g1)
    c: Coincident(g1,g2)
    c: Coincident(g2,g3)
    c: Coincident(g3,g0)
    c: Vertical(g0)
    c: Vertical(g2)
    c: Horizontal(g1)
    c: Horizontal(g3)
    c: Distance(g0,g2) = 6.2
    c: Distance(g1,g3) = 6.8
    c: DistanceY(g-3,g1) = 4
    c: Coincident(g4,g0)
    c: Coincident(g4,g2)
    c: Coincident(g5,g0)
    c: Symmetric(g0,g2,g5)
    c: Diameter(g6) = 4
    c: Coincident(g6,g5)
    c: Vertical(g5,g-3)
FEATURE [Sketcher::SketchObject] Sketch151
  ArcFitTolerance = 1e-06
  AttachmentSupport = -> [Pad008]
  ExternalGeometry = -> [Pad008]
  FullyConstrained = true
  MakeInternals = false
  MapMode = 5
  Placement = pos=(0,3.6,0) rot=(0,0.707107,0.707107;3.14159rad)
  sketch-geometry (10):
    g0: LineSegment [constr] StartX=211.143 StartY=-56.2316 StartZ=0 EndX=211.143 EndY=-65.4316 EndZ=0
    g1: LineSegment [constr] StartX=211.143 StartY=-65.4316 StartZ=0 EndX=215.743 EndY=-65.4316 EndZ=0
    g2: LineSegment [constr] StartX=215.743 StartY=-65.4316 StartZ=0 EndX=215.743 EndY=-56.2316 EndZ=0
    g3: LineSegment [constr] StartX=215.743 StartY=-56.2316 StartZ=0 EndX=211.143 EndY=-56.2316 EndZ=0
    g4: LineSegment StartX=212.243 StartY=-63.8316 StartZ=0 EndX=214.643 EndY=-63.8316 EndZ=0
    g5: LineSegment StartX=214.643 StartY=-63.8316 StartZ=0 EndX=214.643 EndY=-57.0316 EndZ=0
    g6: LineSegment StartX=214.643 StartY=-57.0316 StartZ=0 EndX=212.243 EndY=-57.0316 EndZ=0
    g7: LineSegment StartX=212.243 StartY=-57.0316 StartZ=0 EndX=212.243 EndY=-63.8316 EndZ=0
    g8: GeomPoint [constr] X=213.443 Y=-60.4316 Z=0
    g9: GeomPoint [constr] X=213.443 Y=-60.8316 Z=0
  constraints (26):
    c: Coincident(g0,g1)
    c: Coincident(g1,g2)
    c: Coincident(g2,g3)
    c: Coincident(g3,g0)
    c: Vertical(g0)
    c: Vertical(g2)
    c: Horizontal(g1)
    c: Horizontal(g3)
    c: Distance(g0,g2) = 4.6
    c: Distance(g1,g3) = 9.2
    c: DistanceY(g-3,g1) = 11.4
    c: Coincident(g4,g5)
    c: Coincident(g5,g6)
    c: Coincident(g6,g7)
    c: Coincident(g7,g4)
    c: Horizontal(g4)
    c: Horizontal(g6)
    c: Vertical(g5)
    c: Vertical(g7)
    c: Symmetric(g6,g4,g8)
    c: Distance(g5,g7) = 2.4
    c: Distance(g4,g6) = 6.8
    c: Symmetric(g2,g0,g9)
    c: Vertical(g8,g9)
    c: DistanceY(g1,g4) = 1.6
    c: Vertical(g9,g-3)
FEATURE [PartDesign::Pocket] Pocket019
  BaseFeature = -> Pocket013
  Direction = (0,-1,2e-16)
  Length = 3.6
  Length2 = 5
  Profile = -> Sketch151
  ReferenceAxis = -> Sketch151 [N_Axis]
  Refine = true
  Suppressed = false
  Type = 0
FEATURE [PartDesign::Pocket] Pocket018
  BaseFeature = -> Pocket019
  Direction = (0,-1,2e-16)
  Length = 3.6
  Length2 = 5
  Profile = -> Sketch150
  ReferenceAxis = -> Sketch150 [N_Axis]
  Refine = true
  Suppressed = false
  Type = 0
FEATURE [PartDesign::Point] DatumPoint
  AttacherType = Attacher::AttachEnginePoint
  AttachmentSupport = -> [Sketch150]
  MapMode = 36
  Placement = pos=(-213.443,3.6,-69.4316) rot=(0,1,0;3.14159rad)
FEATURE [PartDesign::Plane] DatumPlane002
  AttachmentSupport = -> [DatumPoint]
  Length = 260.281
  MapMode = 1
  Placement = pos=(-213.443,3.6,-69.4316) rot=(0,0,1;0rad)
  ResizeMode = 0
  Width = 71.8377
FEATURE [Sketcher::SketchObject] Sketch152
  ArcFitTolerance = 1e-06
  AttachmentSupport = -> [DatumPlane002]
  ExternalGeometry = -> [Sketch150]
  FullyConstrained = true
  MakeInternals = false
  MapMode = 5
  Placement = pos=(-213.443,3.6,-69.4316) rot=(0,0,1;0rad)
  sketch-geometry (7):
    g0: LineSegment StartX=0 StartY=0 StartZ=0 EndX=-4 EndY=5.1e-15 EndZ=0
    g1: ArcOfEllipse CenterX=0 CenterY=0 CenterZ=0 NormalX=0 NormalY=0 NormalZ=1 MajorRadius=4 MinorRadius=3.6 AngleXU=3.14159 StartAngle=2e-16 EndAngle=1.5708
    g2: LineSegment [constr] StartX=-4 StartY=9e-16 StartZ=0 EndX=4 EndY=-9e-16 EndZ=0
    g3: LineSegment [constr] StartX=0 StartY=-3.6 StartZ=0 EndX=0 EndY=3.6 EndZ=0
    g4: GeomPoint [constr] X=-1.74356 Y=2.5e-15 Z=0
    g5: GeomPoint [constr] X=1.74356 Y=-2e-15 Z=0
    g6: LineSegment StartX=0 StartY=0 StartZ=0 EndX=-5.5e-15 EndY=-3.6 EndZ=0
  constraints (11):
    c: PointOnObject(g1,g-2)
    c: Distance(g0) = 4
    c: PointOnObject(g0,g-1)
    c: InternalAlignment(g2-g5 -> g1) x4
    c: Coincident(g1,g0)
    c: Vertical(g3)
    c: Coincident(g1,g-1)
    c: Distance(g6) = 3.6
    c: Coincident(g6,g1)
    c: Coincident(g1,g6)
    c: Coincident(g0,g1)
FEATURE [PartDesign::Groove] Groove
  Angle = 360
  Angle2 = 60
  Axis = (0,1,0)
  Base = (-213.443,3.6,-69.4316)
  BaseFeature = -> Pocket018
  Profile = -> Sketch152
  ReferenceAxis = -> Sketch152 [V_Axis]
  Refine = true
  Reversed = true
  Suppressed = false
  Type = 0
FEATURE [PartDesign::Body] Body006  label="lato SX"
  AllowCompound = false
  Group = -> [Binder,Pad019,Chamfer015,Pocket002,Sketch133,Sketch091,Pad005,Sketch092,Pocket001,Sketch093,Sketch094,Pad006,Sketch095,Pad007,Sketch096,Pad008,Sketch097,Pad009,Chamfer005,Pocket004,Sketch098,Pad010,Chamfer006,Pocket003,SubtractivePipe,SubtractivePipe001,Sketch099,Sketch106,Sketch107,Sketch108,Clone2D,Sketch109,SubtractiveLoft,SubtractiveLoft001,Sketch110,Sketch111,Sketch112,Chamfer016,Chamfer017,+15 more]
  Origin = -> Origin006
  Tip = -> Groove
FEATURE [Sketcher::SketchObject] Sketch153  label="ripieno_per_sostegno_led_batteria"
  ArcFitTolerance = 1e-06
  AttachmentSupport = -> [XZ_Plane]
  ExternalGeometry = -> [Sketch036]
  FullyConstrained = true
  MakeInternals = false
  MapMode = 5
  Placement = pos=(0,0,0) rot=(1,0,0;1.5708rad)
  sketch-geometry (4):
    g0: LineSegment StartX=-217.343 StartY=-54.5944 StartZ=0 EndX=-217.343 EndY=-63.1944 EndZ=0
    g1: LineSegment StartX=-217.343 StartY=-63.1944 StartZ=0 EndX=-211.843 EndY=-63.1944 EndZ=0
    g2: LineSegment StartX=-211.843 StartY=-63.1944 StartZ=0 EndX=-211.843 EndY=-54.5944 EndZ=0
    g3: LineSegment StartX=-211.843 StartY=-54.5944 StartZ=0 EndX=-217.343 EndY=-54.5944 EndZ=0
  constraints (11):
    c: Coincident(g0,g1)
    c: Coincident(g1,g2)
    c: Coincident(g2,g3)
    c: Coincident(g3,g0)
    c: Vertical(g0)
    c: Horizontal(g1)
    c: Horizontal(g3)
    c: Tangent(g2,g-3)
    c: DistanceY(g2,g-3) = 4.5
    c: DistanceX(g3,g3) = 5.5
    c: DistanceY(g0,g0) = 8.6
FEATURE [Part::Extrusion] Extrude088  label="Extrude088 - ripieno_per_sostegno_led_batteria"
  Base = -> Sketch153
  Dir = (0,-1,2e-16)
  DirMode = 2
  FaceMakerClass = Part::FaceMakerBullseye
  FaceMakerMode = 3
  LengthFwd = 4
  LengthRev = 0
  Placement = pos=(0,12.6,0) rot=(0,0,1;0rad)
  Solid = true
  Symmetric = false
FEATURE [Part::MultiFuse] Fusion004
  Refine = true
  Shapes = -> [Cut050,Extrude088]
FEATURE [Part::Cut] Cut051
  Base = -> Fusion004
  Refine = true
  Tool = -> Extrude087
FEATURE [Part::Cut] Cut052
  Base = -> Cut051
  Refine = true
  Tool = -> Extrude086
FEATURE [Sketcher::SketchObject] Sketch154
  ArcFitTolerance = 1e-06
  AttachmentSupport = -> [Pad016]
  ExternalGeometry = -> [Binder001]
  FullyConstrained = true
  MakeInternals = false
  MapMode = 5
  Placement = pos=(0,-3.6,0) rot=(1,0,0;1.5708rad)
  sketch-geometry (25):
    g0: LineSegment StartX=-214.643 StartY=-72.4316 StartZ=0 EndX=-212.243 EndY=-72.4316 EndZ=0
    g1: LineSegment StartX=-212.243 StartY=-72.4316 StartZ=0 EndX=-212.243 EndY=-71.2316 EndZ=0
    g2: LineSegment StartX=-212.243 StartY=-71.2316 StartZ=0 EndX=-214.643 EndY=-71.2316 EndZ=0
    g3: LineSegment StartX=-214.643 StartY=-71.2316 StartZ=0 EndX=-214.643 EndY=-72.4316 EndZ=0
    g4: GeomPoint [constr] X=-213.443 Y=-71.8316 Z=0
    g5: LineSegment StartX=-214.643 StartY=-69.6316 StartZ=0 EndX=-212.243 EndY=-69.6316 EndZ=0
    g6: LineSegment StartX=-212.243 StartY=-69.6316 StartZ=0 EndX=-212.243 EndY=-68.4316 EndZ=0
    g7: LineSegment StartX=-212.243 StartY=-68.4316 StartZ=0 EndX=-214.643 EndY=-68.4316 EndZ=0
    g8: LineSegment StartX=-214.643 StartY=-68.4316 StartZ=0 EndX=-214.643 EndY=-69.6316 EndZ=0
    g9: GeomPoint [constr] X=-213.443 Y=-69.0316 Z=0
    g10: LineSegment StartX=-214.643 StartY=-66.8316 StartZ=0 EndX=-212.243 EndY=-66.8316 EndZ=0
    g11: LineSegment StartX=-212.243 StartY=-66.8316 StartZ=0 EndX=-212.243 EndY=-65.6316 EndZ=0
    g12: LineSegment StartX=-212.243 StartY=-65.6316 StartZ=0 EndX=-214.643 EndY=-65.6316 EndZ=0
    g13: LineSegment StartX=-214.643 StartY=-65.6316 StartZ=0 EndX=-214.643 EndY=-66.8316 EndZ=0
    g14: GeomPoint [constr] X=-213.443 Y=-66.2316 Z=0
    g15: LineSegment StartX=-214.643 StartY=-64.0316 StartZ=0 EndX=-212.243 EndY=-64.0316 EndZ=0
    g16: LineSegment StartX=-212.243 StartY=-64.0316 StartZ=0 EndX=-212.243 EndY=-62.8316 EndZ=0
    g17: LineSegment StartX=-212.243 StartY=-62.8316 StartZ=0 EndX=-214.643 EndY=-62.8316 EndZ=0
    g18: LineSegment StartX=-214.643 StartY=-62.8316 StartZ=0 EndX=-214.643 EndY=-64.0316 EndZ=0
    g19: GeomPoint [constr] X=-213.443 Y=-63.4316 Z=0
    g20: LineSegment StartX=-214.643 StartY=-61.2316 StartZ=0 EndX=-212.243 EndY=-61.2316 EndZ=0
    g21: LineSegment StartX=-212.243 StartY=-61.2316 StartZ=0 EndX=-212.243 EndY=-60.0316 EndZ=0
    g22: LineSegment StartX=-212.243 StartY=-60.0316 StartZ=0 EndX=-214.643 EndY=-60.0316 EndZ=0
    g23: LineSegment StartX=-214.643 StartY=-60.0316 StartZ=0 EndX=-214.643 EndY=-61.2316 EndZ=0
    g24: GeomPoint [constr] X=-213.443 Y=-60.6316 Z=0
  constraints (65):
    c: Coincident(g0,g1)
    c: Coincident(g1,g2)
    c: Coincident(g2,g3)
    c: Coincident(g3,g0)
    c: Horizontal(g0)
    c: Horizontal(g2)
    c: Vertical(g1)
    c: Vertical(g3)
    c: Symmetric(g2,g0,g4)
    c: Distance(g1,g3) = 2.4
    c: Distance(g0,g2) = 1.2
    c: Coincident(g5,g6)
    c: Coincident(g6,g7)
    c: Coincident(g7,g8)
    c: Coincident(g8,g5)
    c: Horizontal(g5)
    c: Horizontal(g7)
    c: Vertical(g6)
    c: Vertical(g8)
    c: Symmetric(g7,g5,g9)
    c: Distance(g6,g8) = 2.4
    c: Distance(g5,g7) = 1.2
    c: Coincident(g10,g11)
    c: Coincident(g11,g12)
    c: Coincident(g12,g13)
    c: Coincident(g13,g10)
    c: Horizontal(g10)
    c: Horizontal(g12)
    c: Vertical(g11)
    c: Vertical(g13)
    c: Symmetric(g12,g10,g14)
    c: Distance(g11,g13) = 2.4
    c: Distance(g10,g12) = 1.2
    c: Coincident(g15,g16)
    c: Coincident(g16,g17)
    c: Coincident(g17,g18)
    c: Coincident(g18,g15)
    c: Horizontal(g15)
    c: Horizontal(g17)
    c: Vertical(g16)
    c: Vertical(g18)
    c: Symmetric(g17,g15,g19)
    c: Distance(g16,g18) = 2.4
    c: Distance(g15,g17) = 1.2
    c: Vertical(g4,g-3)
    c: Vertical(g9,g-3)
    c: Vertical(g14,g-3)
    c: Vertical(g19,g-3)
    c: DistanceY(g-3,g4) = 5
    c: DistanceY(g4,g9) = 2.8
    c: DistanceY(g9,g14) = 2.8
    c: DistanceY(g14,g19) = 2.8
    c: Coincident(g20,g21)
    c: Coincident(g21,g22)
    c: Coincident(g22,g23)
    c: Coincident(g23,g20)
    c: Horizontal(g20)
    c: Horizontal(g22)
    c: Vertical(g21)
    c: Vertical(g23)
    c: Symmetric(g22,g20,g24)
    c: Distance(g21,g23) = 2.4
    c: Distance(g20,g22) = 1.2
    c: DistanceY(g19,g24) = 2.8
    c: Vertical(g-3,g24)
FEATURE [PartDesign::Pocket] Pocket020
  BaseFeature = -> Pocket012
  Direction = (0,1,-2e-16)
  Length = 3.6
  Length2 = 5
  Profile = -> Sketch154
  ReferenceAxis = -> Sketch154 [N_Axis]
  Refine = true
  Suppressed = false
  Type = 0
FEATURE [PartDesign::Body] Body007  label="lato DX"
  AllowCompound = false
  Group = -> [Binder001,Sketch114,Pad011,Chamfer014,Sketch115,Pocket006,Sketch116,Pad012,Sketch117,Pocket007,Sketch118,Pad013,Sketch119,Pocket008,Pad017,Chamfer009,Pocket009,Sketch123,Sketch120,Pad014,Pad018,Chamfer008,Pocket010,Sketch121,Pad015,Sketch122,Pad016,SubtractivePipe004,SubtractivePipe005,Sketch149,Sketch148,Sketch124,Sketch125,Sketch126,Sketch129,Sketch130,Clone2D001,Sketch131,SubtractiveLoft002,+13 more]
  Origin = -> Origin007
  Tip = -> Pocket020
FEATURE [Sketcher::SketchObject] Sketch155  label="fermo per protezione batteria"
  ArcFitTolerance = 1e-06
  AttachmentSupport = -> [XZ_Plane]
  ExternalGeometry = -> [Sketch016,Sketch]
  FullyConstrained = true
  MakeInternals = false
  MapMode = 5
  Placement = pos=(0,0,0) rot=(1,0,0;1.5708rad)
  sketch-geometry (5):
    g0: LineSegment StartX=-183.305 StartY=-76.0316 StartZ=0 EndX=-179.305 EndY=-76.0316 EndZ=0
    g1: LineSegment StartX=-179.305 StartY=-76.0316 StartZ=0 EndX=-179.305 EndY=-74.4316 EndZ=0
    g2: LineSegment StartX=-179.305 StartY=-74.4316 StartZ=0 EndX=-183.305 EndY=-74.4316 EndZ=0
    g3: LineSegment [constr] StartX=-183.305 StartY=-76.0316 StartZ=0 EndX=-183.305 EndY=-78.4316 EndZ=0
    g4: LineSegment StartX=-183.305 StartY=-74.4316 StartZ=0 EndX=-183.305 EndY=-76.0316 EndZ=0
  constraints (16):
    c: Horizontal(g0)
    c: Distance(g1) = 1.6
    c: Coincident(g1,g0)
    c: Vertical(g1)
    c: Coincident(g2,g1)
    c: Horizontal(g2)
    c: Vertical(g3)
    c: PointOnObject(g3,g-4)
    c: Horizontal(g3,g0)
    c: Tangent(g3,g-3)
    c: Vertical(g0,g-3)
    c: Coincident(g4,g2)
    c: Coincident(g4,g0)
    c: Vertical(g4)
    c: Vertical(g0,g3)
    c: DistanceY(g3,g3) = 2.4
FEATURE [Part::Extrusion] Extrude089  label="Extrude089 - fermo per protezione batteria"
  Base = -> Sketch155
  Dir = (0,-1,2e-16)
  DirMode = 2
  FaceMakerClass = Part::FaceMakerBullseye
  FaceMakerMode = 3
  LengthFwd = 8
  LengthRev = 0
  Solid = true
  Symmetric = true
FEATURE [Sketcher::SketchObject] Sketch156  label="buco per protezione batteria"
  ArcFitTolerance = 1e-06
  AttachmentSupport = -> [XZ_Plane]
  ExternalGeometry = -> [Sketch,Sketch016]
  FullyConstrained = true
  MakeInternals = false
  MapMode = 5
  Placement = pos=(0,0,0) rot=(1,0,0;1.5708rad)
  sketch-geometry (5):
    g0: LineSegment [constr] StartX=-183.305 StartY=-76.8316 StartZ=0 EndX=-183.305 EndY=-78.4316 EndZ=0
    g1: LineSegment StartX=-200.305 StartY=-78.4316 StartZ=0 EndX=-200.305 EndY=-80.4316 EndZ=0
    g2: LineSegment StartX=-200.305 StartY=-80.4316 StartZ=0 EndX=-198.505 EndY=-80.4316 EndZ=0
    g3: LineSegment StartX=-198.505 StartY=-80.4316 StartZ=0 EndX=-198.505 EndY=-78.4316 EndZ=0
    g4: LineSegment StartX=-198.505 StartY=-78.4316 StartZ=0 EndX=-200.305 EndY=-78.4316 EndZ=0
  constraints (15):
    c: Vertical(g0)
    c: Tangent(g0,g-4)
    c: PointOnObject(g0,g-3)
    c: Horizontal(g0,g-4)
    c: Coincident(g1,g2)
    c: Coincident(g2,g3)
    c: Coincident(g3,g4)
    c: Coincident(g4,g1)
    c: Vertical(g1)
    c: Vertical(g3)
    c: Horizontal(g2)
    c: Distance(g1,g3) = 1.8
    c: Distance(g2,g4) = 2
    c: Tangent(g4,g-3)
    c: Distance(g3,g0) = 15.2
FEATURE [Part::Extrusion] Extrude090  label="Extrude090 - buco per protezione batteria"
  Base = -> Sketch156
  Dir = (0,-1,2e-16)
  DirMode = 2
  FaceMakerClass = Part::FaceMakerBullseye
  FaceMakerMode = 3
  LengthFwd = 4.8
  LengthRev = 0
  Solid = true
  Symmetric = true
FEATURE [Sketcher::SketchObject] Sketch157
  ArcFitTolerance = 1e-06
  AttachmentSupport = -> [XY_Plane010]
  FullyConstrained = true
  MakeInternals = false
  MapMode = 5
  sketch-geometry (9):
    g0: LineSegment [constr] StartX=1.8 StartY=8 StartZ=0 EndX=1.8 EndY=-8 EndZ=0
    g1: LineSegment StartX=1.8 StartY=8 StartZ=0 EndX=17 EndY=8 EndZ=0
    g2: LineSegment StartX=1.8 StartY=-8 StartZ=0 EndX=17 EndY=-8 EndZ=0
    g3: LineSegment StartX=0 StartY=8 StartZ=0 EndX=0 EndY=-8 EndZ=0
    g4: LineSegment StartX=1.8 StartY=8 StartZ=0 EndX=0 EndY=8 EndZ=0
    g5: LineSegment StartX=1.8 StartY=-8 StartZ=0 EndX=0 EndY=-8 EndZ=0
    g6: LineSegment StartX=17 StartY=8 StartZ=0 EndX=17 EndY=-8 EndZ=0
    g7: Circle CenterX=8.5 CenterY=0 CenterZ=0 NormalX=0 NormalY=0 NormalZ=1 AngleXU=0 Radius=5
    g8: LineSegment [constr] StartX=17 StartY=8 StartZ=0 EndX=17 EndY=0 EndZ=0
  constraints (23):
    c: DistanceY(g0,g0) = 16
    c: Distance(g1) = 15.2
    c: Coincident(g1,g0)
    c: Horizontal(g1)
    c: Coincident(g2,g0)
    c: Horizontal(g2)
    c: Equal(g1,g2)
    c: Symmetric(g0,g0,g-1)
    c: Equal(g3,g0)
    c: Coincident(g4,g0)
    c: Horizontal(g4)
    c: DistanceX(g4,g4) = 1.8
    c: Coincident(g5,g0)
    c: Horizontal(g5)
    c: Equal(g4,g5)
    c: Coincident(g3,g4)
    c: Tangent(g3,g-2)
    c: Coincident(g6,g1)
    c: Coincident(g6,g2)
    c: Coincident(g8,g1)
    c: Symmetric(g6,g6,g8)
    c: Symmetric(g8,g-1,g7)
    c: Diameter(g7) = 10
FEATURE [PartDesign::Pad] Pad031
  Direction = (0,0,1)
  Length = 1.4
  Length2 = 10
  Profile = -> Sketch157
  ReferenceAxis = -> Sketch157 [N_Axis]
  Refine = true
  Suppressed = false
  Type = 0
FEATURE [Sketcher::SketchObject] Sketch158
  ArcFitTolerance = 1e-06
  AttachmentSupport = -> [Pad031]
  ExternalGeometry = -> [Pad031]
  FullyConstrained = true
  MakeInternals = false
  MapMode = 5
  Placement = pos=(0,0,1.4) rot=(0,0,1;0rad)
  sketch-geometry (4):
    g0: LineSegment StartX=0 StartY=8 StartZ=0 EndX=0 EndY=-8 EndZ=0
    g1: LineSegment StartX=0 StartY=8 StartZ=0 EndX=1.8 EndY=8 EndZ=0
    g2: LineSegment StartX=1.8 StartY=8 StartZ=0 EndX=1.8 EndY=-8 EndZ=0
    g3: LineSegment StartX=0 StartY=-8 StartZ=0 EndX=1.8 EndY=-8 EndZ=0
  constraints (10):
    c: Coincident(g0,g-3)
    c: Coincident(g0,g-4)
    c: Distance(g1) = 1.8
    c: Coincident(g1,g0)
    c: PointOnObject(g1,g-3)
    c: Coincident(g2,g1)
    c: Vertical(g2)
    c: Coincident(g3,g0)
    c: PointOnObject(g3,g-4)
    c: Coincident(g3,g2)
FEATURE [PartDesign::Pad] Pad032
  BaseFeature = -> Pad031
  Direction = (0,0,1)
  Length = 6.4
  Length2 = 10
  Profile = -> Sketch158
  ReferenceAxis = -> Sketch158 [N_Axis]
  Refine = true
  Suppressed = false
  Type = 0
FEATURE [Sketcher::SketchObject] Sketch159
  ArcFitTolerance = 1e-06
  AttachmentSupport = -> [Pad032]
  ExternalGeometry = -> [Pad032,Pad031]
  FullyConstrained = true
  MakeInternals = false
  MapMode = 5
  Placement = pos=(0,0,7.8) rot=(0,0,1;0rad)
  sketch-geometry (7):
    g0: LineSegment StartX=0.1 StartY=2.2 StartZ=0 EndX=0.1 EndY=-2.2 EndZ=0
    g1: LineSegment StartX=0.1 StartY=-2.2 StartZ=0 EndX=1.7 EndY=-2.2 EndZ=0
    g2: LineSegment StartX=1.7 StartY=-2.2 StartZ=0 EndX=1.7 EndY=2.2 EndZ=0
    g3: LineSegment StartX=1.7 StartY=2.2 StartZ=0 EndX=0.1 EndY=2.2 EndZ=0
    g4: GeomPoint [constr] X=0.9 Y=8 Z=0
    g5: GeomPoint [constr] X=0.9 Y=-8 Z=0
    g6: LineSegment [constr] StartX=0.9 StartY=8 StartZ=0 EndX=0.9 EndY=-8 EndZ=0
  constraints (14):
    c: Coincident(g0,g1)
    c: Coincident(g1,g2)
    c: Coincident(g2,g3)
    c: Coincident(g3,g0)
    c: Vertical(g2)
    c: Horizontal(g1)
    c: Distance(g0,g2) = 1.6
    c: Distance(g1,g3) = 4.4
    c: Symmetric(g0,g0,g-1)
    c: Symmetric(g-4,g-4,g4)
    c: Symmetric(g-3,g-5,g5)
    c: Coincident(g6,g4)
    c: Coincident(g6,g5)
    c: Symmetric(g0,g2,g6)
FEATURE [PartDesign::Pad] Pad033
  BaseFeature = -> Pad032
  Direction = (0,0,1)
  Length = 1.4
  Length2 = 10
  Profile = -> Sketch159
  ReferenceAxis = -> Sketch159 [N_Axis]
  Refine = true
  Suppressed = false
  Type = 0
FEATURE [Part::Cut] Cut053
  Base = -> Cut052
  Refine = true
  Tool = -> Extrude089
FEATURE [Part::Cut] Cut054
  Base = -> Cut053
  Refine = true
  Tool = -> Extrude090
FEATURE [Sketcher::SketchObject] Sketch160
  ArcFitTolerance = 1e-06
  AttachmentSupport = -> [Pad033]
  ExternalGeometry = -> [Pad033]
  FullyConstrained = true
  MakeInternals = false
  MapMode = 5
  Placement = pos=(0,0,1.4) rot=(0,0,1;0rad)
  sketch-geometry (4):
    g0: LineSegment StartX=15.6 StartY=3.7 StartZ=0 EndX=15.6 EndY=-3.7 EndZ=0
    g1: LineSegment StartX=15.6 StartY=-3.7 StartZ=0 EndX=17 EndY=-3.7 EndZ=0
    g2: LineSegment StartX=17 StartY=-3.7 StartZ=0 EndX=17 EndY=3.7 EndZ=0
    g3: LineSegment StartX=17 StartY=3.7 StartZ=0 EndX=15.6 EndY=3.7 EndZ=0
  constraints (10):
    c: Coincident(g0,g1)
    c: Coincident(g1,g2)
    c: Coincident(g2,g3)
    c: Coincident(g3,g0)
    c: Horizontal(g1)
    c: Horizontal(g3)
    c: Distance(g0,g2) = 1.4
    c: Distance(g1,g3) = 7.4
    c: Symmetric(g0,g0,g-1)
    c: Tangent(g2,g-3)
FEATURE [PartDesign::Pad] Pad034
  BaseFeature = -> Pad033
  Direction = (0,0,1)
  Length = 2.4
  Length2 = 10
  Profile = -> Sketch160
  ReferenceAxis = -> Sketch160 [N_Axis]
  Refine = true
  Suppressed = false
  Type = 0
FEATURE [Sketcher::SketchObject] Sketch161
  ArcFitTolerance = 1e-06
  AttachmentSupport = -> [Pad034]
  ExternalGeometry = -> [Pad034]
  FullyConstrained = true
  MakeInternals = false
  MapMode = 5
  Placement = pos=(0,0,3.8) rot=(0,0,1;0rad)
  sketch-geometry (6):
    g0: LineSegment StartX=17 StartY=3.7 StartZ=0 EndX=21 EndY=3.7 EndZ=0
    g1: LineSegment StartX=17 StartY=3.7 StartZ=0 EndX=15.6 EndY=3.7 EndZ=0
    g2: LineSegment StartX=15.6 StartY=3.7 StartZ=0 EndX=15.6 EndY=-3.7 EndZ=0
    g3: LineSegment StartX=15.6 StartY=-3.7 StartZ=0 EndX=17 EndY=-3.7 EndZ=0
    g4: LineSegment StartX=17 StartY=-3.7 StartZ=0 EndX=21 EndY=-3.7 EndZ=0
    g5: LineSegment StartX=21 StartY=3.7 StartZ=0 EndX=21 EndY=-3.7 EndZ=0
  constraints (14):
    c: Distance(g0) = 4
    c: Coincident(g0,g-4)
    c: Horizontal(g0)
    c: Coincident(g1,g0)
    c: Coincident(g1,g-3)
    c: Coincident(g2,g1)
    c: Coincident(g2,g-5)
    c: Coincident(g3,g2)
    c: Coincident(g3,g-5)
    c: Coincident(g4,g3)
    c: Horizontal(g4)
    c: Equal(g4,g0)
    c: Coincident(g5,g0)
    c: Coincident(g5,g4)
FEATURE [PartDesign::Pad] Pad035
  BaseFeature = -> Pad034
  Direction = (0,0,1)
  Length = 1.4
  Length2 = 10
  Profile = -> Sketch161
  ReferenceAxis = -> Sketch161 [N_Axis]
  Refine = true
  Suppressed = false
  Type = 0
FEATURE [PartDesign::Body] Body010  label="Protezione_inferiore_batteria"
  AllowCompound = false
  Group = -> [Sketch157,Pad031,Sketch158,Pad032,Sketch159,Pad033,Sketch160,Pad034,Sketch161,Pad035]
  Origin = -> Origin010
  Tip = -> Pad035
FEATURE [Sketcher::SketchObject] Sketch162  label="scavo_saldature_nuovo_driver_alto"
  ArcFitTolerance = 1e-06
  AttachmentSupport = -> [XZ_Plane]
  ExternalGeometry = -> [Sketch138]
  FullyConstrained = true
  MakeInternals = false
  MapMode = 5
  Placement = pos=(0,0,0) rot=(1,0,0;1.5708rad)
  sketch-geometry (4):
    g0: LineSegment StartX=-192.503 StartY=17.8001 StartZ=0 EndX=-191.336 EndY=4.65187 EndZ=0
    g1: LineSegment StartX=-192.503 StartY=17.8001 StartZ=0 EndX=-190.909 EndY=17.9416 EndZ=0
    g2: LineSegment StartX=-190.909 StartY=17.9416 StartZ=0 EndX=-189.742 EndY=4.79337 EndZ=0
    g3: LineSegment StartX=-189.742 StartY=4.79337 StartZ=0 EndX=-191.336 EndY=4.65187 EndZ=0
  constraints (10):
    c: Parallel(g0,g-3)
    c: Equal(g0,g-3)
    c: Coincident(g1,g0)
    c: Perpendicular(g0,g1)
    c: Coincident(g1,g-3)
    c: Coincident(g2,g1)
    c: Coincident(g2,g-3)
    c: Coincident(g3,g2)
    c: Coincident(g3,g0)
    c: Distance(g1) = 1.6
FEATURE [PartDesign::Body] Body  label="Struttura pistola"
  AllowCompound = false
  Group = -> [Sketch,Sketch002,Sketch004,DatumPlane,Sketch005,DatumPlane001,CopyCut,Sketch008,Sketch009,Sketch010,Sketch011,Sketch012,Sketch013,Sketch014,Sketch015,Sketch016,Sketch017,Sketch018,Sketch019,Sketch020,Sketch022,Sketch023,Sketch024,Sketch025,Sketch026,Sketch027,Sketch029,Sketch030,Sketch031,Sketch032,Sketch033,Sketch034,Sketch035,Sketch036,Sketch037,Sketch038,Sketch039,Sketch040,Sketch041,Sketch042,+31 more]
  Origin = -> Origin
FEATURE [Part::Extrusion] Extrude091  label="Extrude091 - scavo_saldature_nuovo_driver_alto"
  Base = -> Sketch162
  Dir = (0,-1,2e-16)
  DirMode = 2
  FaceMakerClass = Part::FaceMakerBullseye
  FaceMakerMode = 3
  LengthFwd = 4
  LengthRev = 0
  Placement = pos=(0,-3.8,0) rot=(0,0,1;0rad)
  Solid = true
  Symmetric = false
FEATURE [Part::Cut] Cut055
  Base = -> Cut054
  Refine = true
  Tool = -> Extrude091
note: 2 file-system paths scrubbed to <path> (originals preserved in the JSON sidecar)
